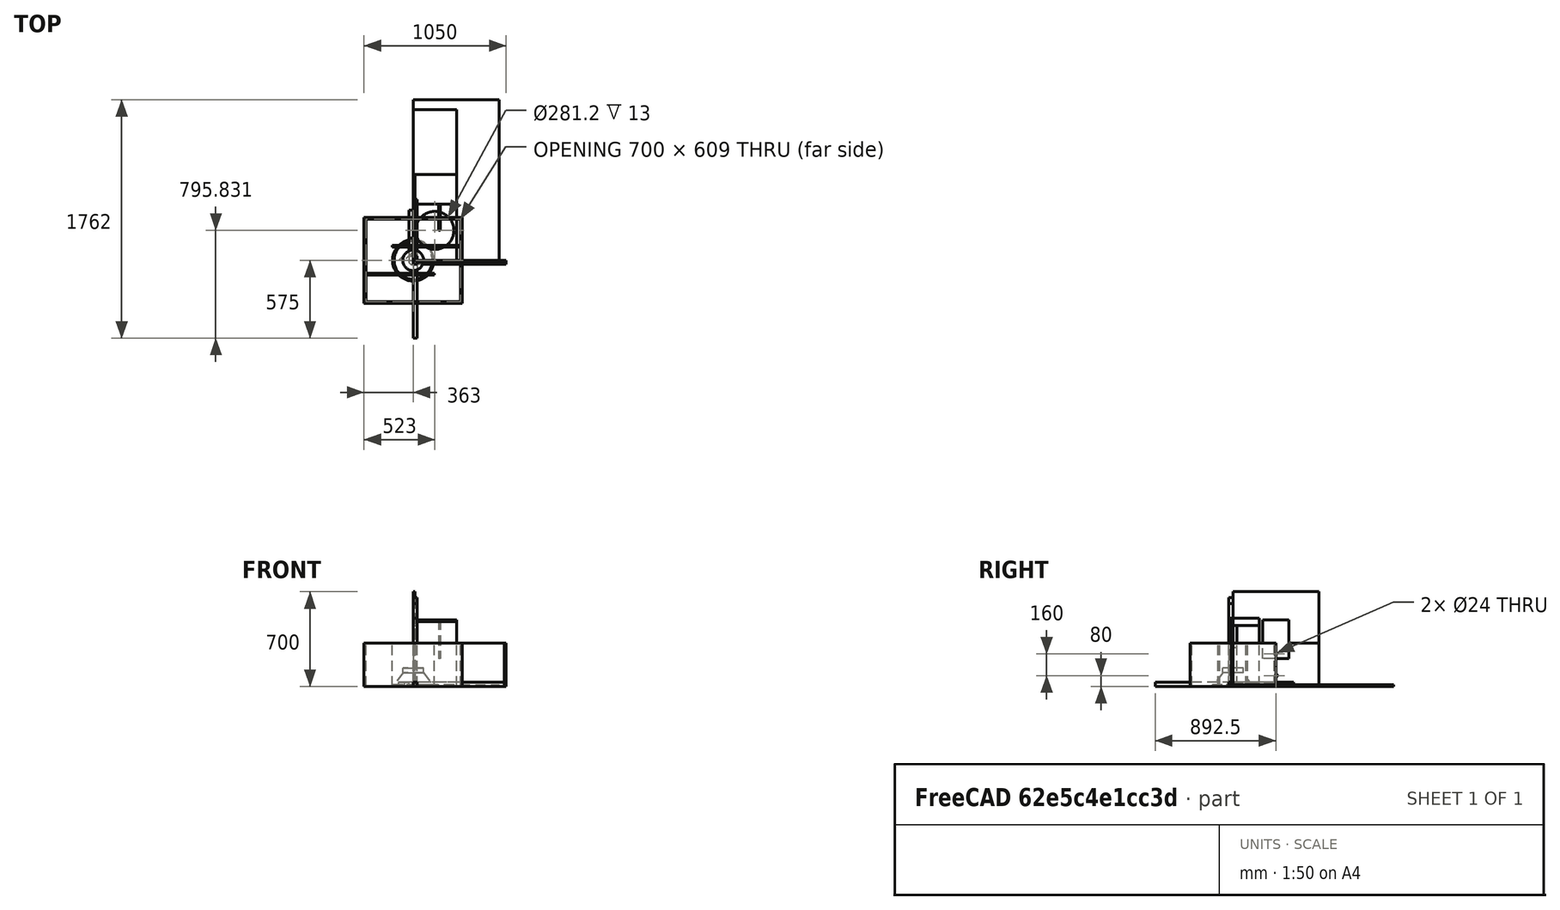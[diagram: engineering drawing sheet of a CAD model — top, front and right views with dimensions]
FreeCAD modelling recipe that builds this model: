
FCSTD DOCUMENT  (FreeCAD 1.0R39109 (Git))
Label: gfold
License: All rights reserved
LicenseURL: http://en.wikipedia.org/wiki/All_rights_reserved
objects: TechDraw::DrawViewDimension×119, TechDraw::DrawViewBalloon×73, TechDraw::DrawProjGroupItem×72, Sketcher::SketchObject×42, App::FeaturePython×42, App::Link×40, PartDesign::Body×38, PartDesign::Pad×37, TechDraw::DrawSVGTemplate×21, TechDraw::DrawPage×21, TechDraw::DrawProjGroup×20, TechDraw::DrawViewAnnotation×20, TechDraw::DrawViewSection×6, Spreadsheet::Sheet×3, App::DocumentObjectGroup×3, PartDesign::Revolution×1, Assembly::JointGroup×1, Assembly::AssemblyObject×1
note: 389 computed .brp shape members not serialized (recipe doc carries the construction recipe); baked Part::Feature solids carry a one-line shape summary decoded from their .brp

FEATURE [Spreadsheet::Sheet] Spreadsheet  label="dims"
  cells = A1='Width (internal); B1(width)==32 cm; A2='Depth (internal); B2(depth)==700 mm; A3='Height (internal); B3(height)==63.5 cm - 2 * thickness; A4='Panel Thickness; B4(thickness)==1.3 cm; A5='ratios; B5(ratio1)=0.33333; C5(ratio2)==ratio1; A6='driver offset; B6(driver_offset)==20 mm; A7='driver_mount; B7(driver_mount_diameter)==281.2 mm; A10='widths; B10(width1)==ratio1 * (height - 2 * thickness); C10(width2)==ratio2 * (height - 2 * thickness); D10(width3)==(1 - ratio1 - ratio2) * (height - 2 * thickness); H10==25.4 * 4
FEATURE [Sketcher::SketchObject] Sketch003  label="outsidepanels_2"
  ArcFitTolerance = 0
  AttachmentSupport = -> [XY_Plane]
  FullyConstrained = true
  MakeInternals = false
  MapMode = 5
  expr: Constraints[197] = <<dims>>.thickness
  expr: Constraints[198] = <<dims>>.width3
  expr: Constraints[199] = <<dims>>.depth
  expr: Constraints[200] = <<dims>>.width2
  expr: Constraints[201] = <<dims>>.width3
  expr: Constraints[202] = <<dims>>.width1
  expr: Constraints[203] = <<dims>>.width2
  expr: Constraints[206] = <<dims>>.depth / 2
  expr: Constraints[207] = <<dims>>.height / 2
  expr: Constraints[218] = <<dims>>.thickness
  expr: Constraints[219] = <<dims>>.thickness
  expr: Constraints[220] = <<dims>>.thickness
  expr: Constraints[221] = <<dims>>.thickness
  sketch-geometry (91):
    g0: LineSegment [constr] StartX=-350 StartY=304.5 StartZ=0 EndX=350 EndY=304.5 EndZ=0
    g1: LineSegment [constr] StartX=350 StartY=304.5 StartZ=0 EndX=350 EndY=-304.5 EndZ=0
    g2: LineSegment [constr] StartX=350 StartY=-304.5 StartZ=0 EndX=-350 EndY=-304.5 EndZ=0
    g3: LineSegment [constr] StartX=-350 StartY=-304.5 StartZ=0 EndX=-350 EndY=304.5 EndZ=0
    g4: LineSegment StartX=-155.669 StartY=110.169 StartZ=0 EndX=350 EndY=110.169 EndZ=0
    g5: LineSegment [constr] StartX=350 StartY=110.169 StartZ=0 EndX=350 EndY=97.1686 EndZ=0
    g6: LineSegment StartX=350 StartY=97.1686 StartZ=0 EndX=-155.669 EndY=97.1686 EndZ=0
    g7: LineSegment StartX=-155.669 StartY=97.1686 StartZ=0 EndX=-155.669 EndY=110.169 EndZ=0
    g8: LineSegment StartX=-350 StartY=-97.1628 StartZ=0 EndX=155.663 EndY=-97.1628 EndZ=0
    g9: LineSegment StartX=155.663 StartY=-97.1628 StartZ=0 EndX=155.663 EndY=-110.163 EndZ=0
    g10: LineSegment StartX=155.663 StartY=-110.163 StartZ=0 EndX=-350 EndY=-110.163 EndZ=0
    g11: LineSegment [constr] StartX=-350 StartY=-110.163 StartZ=0 EndX=-350 EndY=-97.1628 EndZ=0
    g12: LineSegment [constr] StartX=-155.669 StartY=304.5 StartZ=0 EndX=-252.834 EndY=304.5 EndZ=0
    g13: LineSegment [constr] StartX=-252.834 StartY=304.5 StartZ=0 EndX=-350 EndY=304.5 EndZ=0
    g14: LineSegment [constr] StartX=-350 StartY=304.5 StartZ=0 EndX=-350 EndY=207.334 EndZ=0
    g15: LineSegment [constr] StartX=-350 StartY=207.334 StartZ=0 EndX=-350 EndY=110.169 EndZ=0
    g16: LineSegment [constr] StartX=-252.834 StartY=304.5 StartZ=0 EndX=-204.251 EndY=207.334 EndZ=0
    g17: LineSegment [constr] StartX=-204.251 StartY=207.334 StartZ=0 EndX=-155.669 EndY=110.169 EndZ=0
    g18: LineSegment [constr] StartX=-155.669 StartY=110.169 StartZ=0 EndX=-252.834 EndY=158.751 EndZ=0
    g19: LineSegment [constr] StartX=-252.834 StartY=158.751 StartZ=0 EndX=-350 EndY=207.334 EndZ=0
    g20: LineSegment [constr] StartX=-155.669 StartY=110.169 StartZ=0 EndX=-155.669 EndY=207.334 EndZ=0
    g21: LineSegment [constr] StartX=-155.669 StartY=207.334 StartZ=0 EndX=-155.669 EndY=304.5 EndZ=0
    g22: LineSegment [constr] StartX=-155.669 StartY=110.169 StartZ=0 EndX=-252.834 EndY=110.169 EndZ=0
    g23: LineSegment [constr] StartX=-252.834 StartY=110.169 StartZ=0 EndX=-350 EndY=110.169 EndZ=0
    g24: LineSegment [constr] StartX=-155.669 StartY=97.1686 StartZ=0 EndX=-252.834 EndY=97.1686 EndZ=0
    g25: LineSegment [constr] StartX=-252.834 StartY=97.1686 StartZ=0 EndX=-350 EndY=97.1686 EndZ=0
    g26: LineSegment [constr] StartX=-155.669 StartY=97.1686 StartZ=0 EndX=-155.669 EndY=0.002915 EndZ=0
    g27: LineSegment [constr] StartX=-155.669 StartY=0.002915 StartZ=0 EndX=-155.669 EndY=-97.1628 EndZ=0
    g28: LineSegment [constr] StartX=-155.669 StartY=97.1686 StartZ=0 EndX=-252.834 EndY=48.5858 EndZ=0
    g29: LineSegment [constr] StartX=-350 StartY=97.1686 StartZ=0 EndX=-350 EndY=0.002915 EndZ=0
    g30: LineSegment [constr] StartX=-350 StartY=0.002915 StartZ=0 EndX=-350 EndY=-97.1628 EndZ=0
    g31: LineSegment [constr] StartX=-252.834 StartY=48.5858 StartZ=0 EndX=-350 EndY=0.002915 EndZ=0
    g32: LineSegment [constr] StartX=-155.669 StartY=97.1686 StartZ=0 EndX=-204.251 EndY=0.002915 EndZ=0
    g33: LineSegment [constr] StartX=-204.251 StartY=0.002915 StartZ=0 EndX=-252.834 EndY=-97.1628 EndZ=0
    g34: LineSegment [constr] StartX=-350 StartY=-97.1628 StartZ=0 EndX=-252.834 EndY=-97.1628 EndZ=0
    g35: LineSegment [constr] StartX=-252.834 StartY=-97.1628 StartZ=0 EndX=-155.669 EndY=-97.1628 EndZ=0
    g36: LineSegment [constr] StartX=155.663 StartY=97.1686 StartZ=0 EndX=155.663 EndY=0.002915 EndZ=0
    g37: LineSegment [constr] StartX=155.663 StartY=0.002915 StartZ=0 EndX=155.663 EndY=-97.1628 EndZ=0
    g38: LineSegment [constr] StartX=155.663 StartY=-97.1628 StartZ=0 EndX=252.831 EndY=-97.1628 EndZ=0
    g39: LineSegment [constr] StartX=252.831 StartY=-97.1628 StartZ=0 EndX=350 EndY=-97.1628 EndZ=0
    g40: LineSegment [constr] StartX=350 StartY=-97.1628 StartZ=0 EndX=350 EndY=0.002915 EndZ=0
    g41: LineSegment [constr] StartX=350 StartY=97.1686 StartZ=0 EndX=350 EndY=0.002915 EndZ=0
    g42: LineSegment [constr] StartX=155.663 StartY=97.1686 StartZ=0 EndX=252.831 EndY=97.1686 EndZ=0
    g43: LineSegment [constr] StartX=252.831 StartY=97.1686 StartZ=0 EndX=350 EndY=97.1686 EndZ=0
    g44: LineSegment [constr] StartX=252.831 StartY=97.1686 StartZ=0 EndX=204.247 EndY=0.002915 EndZ=0
    g45: LineSegment [constr] StartX=204.247 StartY=0.002915 StartZ=0 EndX=155.663 EndY=-97.1628 EndZ=0
    g46: LineSegment [constr] StartX=155.663 StartY=-97.1628 StartZ=0 EndX=252.831 EndY=-48.5799 EndZ=0
    g47: LineSegment [constr] StartX=252.831 StartY=-48.5799 StartZ=0 EndX=350 EndY=0.002915 EndZ=0
    g48: LineSegment [constr] StartX=155.663 StartY=-110.163 StartZ=0 EndX=252.831 EndY=-110.163 EndZ=0
    g49: LineSegment [constr] StartX=252.831 StartY=-110.163 StartZ=0 EndX=350 EndY=-110.163 EndZ=0
    g50: LineSegment [constr] StartX=155.663 StartY=-110.163 StartZ=0 EndX=155.663 EndY=-207.331 EndZ=0
    g51: LineSegment [constr] StartX=155.663 StartY=-207.331 StartZ=0 EndX=155.663 EndY=-304.5 EndZ=0
    g52: LineSegment [constr] StartX=155.663 StartY=-110.163 StartZ=0 EndX=204.247 EndY=-207.331 EndZ=0
    g53: LineSegment [constr] StartX=204.247 StartY=-207.331 StartZ=0 EndX=252.831 EndY=-304.5 EndZ=0
    g54: LineSegment [constr] StartX=155.663 StartY=-110.163 StartZ=0 EndX=252.831 EndY=-158.747 EndZ=0
    g55: LineSegment [constr] StartX=252.831 StartY=-158.747 StartZ=0 EndX=350 EndY=-207.331 EndZ=0
    g56: LineSegment [constr] StartX=350 StartY=-207.331 StartZ=0 EndX=350 EndY=-110.163 EndZ=0
    g57: LineSegment [constr] StartX=350 StartY=-207.331 StartZ=0 EndX=350 EndY=-304.5 EndZ=0
    g58: LineSegment [constr] StartX=252.831 StartY=-304.5 StartZ=0 EndX=350 EndY=-304.5 EndZ=0
    g59: LineSegment [constr] StartX=252.831 StartY=-304.5 StartZ=0 EndX=155.663 EndY=-304.5 EndZ=0
    g60: LineSegment [constr] StartX=-350 StartY=-110.163 StartZ=0 EndX=-350 EndY=-207.331 EndZ=0
    g61: LineSegment [constr] StartX=-350 StartY=-207.331 StartZ=0 EndX=-350 EndY=-304.5 EndZ=0
    g62: LineSegment [constr] StartX=350 StartY=304.5 StartZ=0 EndX=350 EndY=207.334 EndZ=0
    g63: LineSegment [constr] StartX=350 StartY=207.334 StartZ=0 EndX=350 EndY=110.169 EndZ=0
    g64: LineSegment [constr] StartX=350 StartY=207.334 StartZ=0 EndX=-155.669 EndY=207.334 EndZ=0
    g65: LineSegment [constr] StartX=-155.669 StartY=207.334 StartZ=0 EndX=-204.251 EndY=207.334 EndZ=0
    g66: LineSegment [constr] StartX=-204.251 StartY=207.334 StartZ=0 EndX=-252.834 EndY=158.751 EndZ=0
    g67: LineSegment [constr] StartX=-252.834 StartY=158.751 StartZ=0 EndX=-252.834 EndY=110.169 EndZ=0
    g68: LineSegment [constr] StartX=-252.834 StartY=110.169 StartZ=0 EndX=-252.834 EndY=97.1686 EndZ=0
    g69: LineSegment [constr] StartX=-252.834 StartY=97.1686 StartZ=0 EndX=-252.834 EndY=48.5858 EndZ=0
    g70: LineSegment [constr] StartX=-252.834 StartY=48.5858 StartZ=0 EndX=-204.251 EndY=0.002915 EndZ=0
    g71: LineSegment [constr] StartX=-204.251 StartY=0.002915 StartZ=0 EndX=-155.669 EndY=0.002915 EndZ=0
    g72: LineSegment [constr] StartX=-155.669 StartY=0.002915 StartZ=0 EndX=155.663 EndY=0.002915 EndZ=0
    g73: LineSegment [constr] StartX=155.663 StartY=0.002915 StartZ=0 EndX=204.247 EndY=0.002915 EndZ=0
    g74: LineSegment [constr] StartX=204.247 StartY=0.002915 StartZ=0 EndX=252.831 EndY=-48.5799 EndZ=0
    g75: LineSegment [constr] StartX=252.831 StartY=-48.5799 StartZ=0 EndX=252.831 EndY=-97.1628 EndZ=0
    g76: LineSegment [constr] StartX=252.831 StartY=-97.1628 StartZ=0 EndX=252.831 EndY=-110.163 EndZ=0
    g77: LineSegment [constr] StartX=252.831 StartY=-110.163 StartZ=0 EndX=252.831 EndY=-158.747 EndZ=0
    g78: LineSegment [constr] StartX=252.831 StartY=-158.747 StartZ=0 EndX=204.247 EndY=-207.331 EndZ=0
    g79: LineSegment [constr] StartX=155.663 StartY=-207.331 StartZ=0 EndX=204.247 EndY=-207.331 EndZ=0
    g80: LineSegment [constr] StartX=155.663 StartY=-207.331 StartZ=0 EndX=-350 EndY=-207.331 EndZ=0
    g81: LineSegment StartX=-363 StartY=317.5 StartZ=0 EndX=363 EndY=317.5 EndZ=0
    g82: LineSegment StartX=363 StartY=317.5 StartZ=0 EndX=363 EndY=-317.5 EndZ=0
    g83: LineSegment StartX=363 StartY=-317.5 StartZ=0 EndX=-363 EndY=-317.5 EndZ=0
    g84: LineSegment StartX=-363 StartY=-317.5 StartZ=0 EndX=-363 EndY=317.5 EndZ=0
    g85: LineSegment StartX=350 StartY=-304.5 StartZ=0 EndX=-350 EndY=-304.5 EndZ=0
    g86: LineSegment StartX=-350 StartY=304.5 StartZ=0 EndX=350 EndY=304.5 EndZ=0
    g87: LineSegment StartX=-350 StartY=304.5 StartZ=0 EndX=-350 EndY=-97.1628 EndZ=0
    g88: LineSegment StartX=-350 StartY=-110.163 StartZ=0 EndX=-350 EndY=-304.5 EndZ=0
    g89: LineSegment StartX=350 StartY=304.5 StartZ=0 EndX=350 EndY=110.169 EndZ=0
    g90: LineSegment StartX=350 StartY=97.1686 StartZ=0 EndX=350 EndY=-304.5 EndZ=0
  constraints (234):
    c: Coincident(g0,g1)
    c: Coincident(g1,g2)
    c: Coincident(g2,g3)
    c: Coincident(g3,g0)
    c: Horizontal(g0)
    c: Horizontal(g2)
    c: Vertical(g1)
    c: Vertical(g3)
    c: Coincident(g4,g5)
    c: Coincident(g5,g6)
    c: Coincident(g6,g7)
    c: Coincident(g7,g4)
    c: Horizontal(g4)
    c: Horizontal(g6)
    c: Vertical(g5)
    c: Vertical(g7)
    c: PointOnObject(g5,g1)
    c: Coincident(g8,g9)
    c: Coincident(g9,g10)
    c: Coincident(g10,g11)
    c: Coincident(g11,g8)
    c: Horizontal(g8)
    c: Horizontal(g10)
    c: Vertical(g9)
    c: Vertical(g11)
    c: PointOnObject(g8,g3)
    c: Equal(g7,g9)
    c: Coincident(g20,g4)
    c: PointOnObject(g21,g0)
    c: Coincident(g22,g4)
    c: PointOnObject(g23,g3)
    c: Coincident(g12,g21)
    c: PointOnObject(g12,g0)
    c: Coincident(g13,g12)
    c: Coincident(g13,g0)
    c: Coincident(g14,g0)
    c: PointOnObject(g14,g3)
    c: Coincident(g15,g14)
    c: Coincident(g15,g23)
    c: Equal(g14,g15)
    c: Equal(g12,g13)
    c: Coincident(g16,g12)
    c: Coincident(g17,g4)
    c: Coincident(g18,g4)
    c: Coincident(g19,g14)
    c: Coincident(g16,g17)
    c: Coincident(g18,g19)
    c: Coincident(g20,g21)
    c: Vertical(g20)
    c: Vertical(g21)
    c: Coincident(g22,g23)
    c: Horizontal(g22)
    c: Horizontal(g23)
    c: Equal(g17,g16)
    c: Equal(g21,g20)
    c: Equal(g19,g18)
    c: Equal(g22,g23)
    c: Parallel(g19,g18)
    c: Parallel(g16,g17)
    c: Coincident(g24,g6)
    c: Coincident(g25,g24)
    c: PointOnObject(g25,g3)
    c: Horizontal(g25)
    c: Parallel(g25,g24)
    c: Equal(g24,g25)
    c: Coincident(g26,g6)
    c: Coincident(g27,g26)
    c: PointOnObject(g27,g8)
    c: Parallel(g27,g26)
    c: Equal(g26,g27)
    c: Parallel(g27,g3)
    c: Coincident(g28,g6)
    c: Coincident(g29,g25)
    c: Coincident(g30,g8)
    c: Coincident(g29,g30)
    c: Equal(g29,g30)
    c: Coincident(g31,g28)
    c: Coincident(g31,g29)
    c: Parallel(g31,g28)
    c: Equal(g31,g28)
    c: Parallel(g30,g29)
    c: Coincident(g32,g6)
    c: Coincident(g33,g32)
    c: Coincident(g34,g8)
    c: Coincident(g34,g33)
    c: Coincident(g35,g33)
    c: Coincident(g35,g27)
    c: Parallel(g33,g32)
    c: Equal(g35,g34)
    c: Parallel(g35,g34)
    c: Equal(g33,g32)
    c: PointOnObject(g36,g6)
    c: Coincident(g37,g36)
    c: Coincident(g37,g8)
    c: Parallel(g37,g36)
    c: Parallel(g36,g1)
    c: Equal(g36,g37)
    c: Coincident(g38,g8)
    c: Horizontal(g38)
    c: Coincident(g39,g38)
    c: PointOnObject(g39,g1)
    c: Horizontal(g39)
    c: Coincident(g40,g39)
    c: Coincident(g41,g5)
    c: Coincident(g41,g40)
    c: Coincident(g42,g36)
    c: Coincident(g43,g42)
    c: Coincident(g43,g5)
    c: Coincident(g44,g42)
    c: Coincident(g45,g44)
    c: Coincident(g45,g8)
    c: Coincident(g46,g8)
    c: Coincident(g47,g46)
    c: Coincident(g47,g40)
    c: Equal(g42,g43)
    c: Equal(g44,g45)
    c: Parallel(g42,g43)
    c: Parallel(g45,g44)
    c: Equal(g46,g47)
    c: Equal(g41,g40)
    c: Parallel(g29,g40)
    c: Parallel(g46,g47)
    c: Equal(g38,g39)
    c: Coincident(g48,g9)
    c: Horizontal(g48)
    c: Coincident(g49,g48)
    c: PointOnObject(g49,g1)
    c: Horizontal(g49)
    c: Equal(g49,g48)
    c: Coincident(g50,g9)
    c: Vertical(g50)
    c: Coincident(g51,g50)
    c: PointOnObject(g51,g2)
    c: Vertical(g51)
    c: Equal(g50,g51)
    c: Coincident(g52,g9)
    c: Coincident(g53,g52)
    c: Coincident(g54,g9)
    c: Coincident(g55,g54)
    c: Coincident(g56,g55)
    c: Coincident(g56,g49)
    c: Coincident(g57,g55)
    c: Coincident(g57,g1)
    c: Coincident(g58,g53)
    c: Coincident(g58,g1)
    c: Coincident(g59,g53)
    c: Coincident(g59,g51)
    c: Equal(g56,g57)
    c: Parallel(g57,g56)
    c: Equal(g54,g55)
    c: Equal(g52,g53)
    c: Parallel(g52,g53)
    c: Parallel(g55,g54)
    c: Equal(g59,g58)
    c: Parallel(g59,g58)
    c: Coincident(g60,g10)
    c: Coincident(g61,g2)
    c: Equal(g60,g61)
    c: Parallel(g61,g60)
    c: Coincident(g62,g0)
    c: Coincident(g63,g62)
    c: Coincident(g63,g4)
    c: Equal(g62,g63)
    c: Parallel(g62,g63)
    c: Coincident(g64,g62)
    c: Coincident(g64,g20)
    c: Coincident(g65,g20)
    c: Coincident(g66,g16)
    c: Coincident(g66,g18)
    c: Coincident(g67,g18)
    c: Coincident(g67,g22)
    c: Coincident(g68,g22)
    c: Coincident(g68,g24)
    c: Coincident(g69,g24)
    c: Coincident(g69,g28)
    c: Coincident(g70,g28)
    c: Coincident(g70,g32)
    c: Coincident(g71,g32)
    c: Coincident(g71,g26)
    c: Coincident(g72,g26)
    c: Coincident(g72,g36)
    c: Coincident(g73,g36)
    c: Coincident(g73,g44)
    c: Coincident(g74,g44)
    c: Coincident(g74,g46)
    c: Coincident(g75,g46)
    c: Coincident(g75,g38)
    c: Coincident(g76,g38)
    c: Coincident(g76,g48)
    c: Coincident(g77,g48)
    c: Coincident(g77,g54)
    c: Coincident(g78,g54)
    c: Coincident(g78,g52)
    c: Coincident(g79,g50)
    c: Coincident(g79,g52)
    c: Coincident(g80,g50)
    c: Coincident(g65,g16)
    c: DistanceY(g10,g8) = 13
    c: DistanceY(g2,g49) = 194.337
    c: DistanceX(g0,g0) = 700
    c: DistanceX(g25,g6) = 194.331
    c: DistanceX(g9,g49) = 194.337
    c: DistanceY(g4,g0) = 194.331
    c: DistanceY(g39,g5) = 194.331
    c: Coincident(g61,g80)
    c: Coincident(g61,g60)
    c: DistanceX(g-1,g1) = 350
    c: DistanceY(g-1,g0) = 304.5
    c: Coincident(g81,g82)
    c: Coincident(g82,g83)
    c: Coincident(g83,g84)
    c: Coincident(g84,g81)
    c: Horizontal(g81)
    c: Horizontal(g83)
    c: Vertical(g82)
    c: Vertical(g84)
    c: Horizontal(g85)
    c: Horizontal(g86)
    c: DistanceY(g86,g81) = 13
    c: DistanceX(g81,g86) = 13
    c: DistanceY(g82,g85) = 13
    c: DistanceX(g85,g82) = 13
    c: Coincident(g85,g1)
    c: Coincident(g87,g86)
    c: Coincident(g87,g8)
    c: Vertical(g87)
    c: Coincident(g88,g10)
    c: Coincident(g88,g85)
    c: Vertical(g88)
    c: Coincident(g89,g86)
    c: Coincident(g89,g4)
    c: Coincident(g90,g6)
    c: Coincident(g90,g85)
    c: Coincident(g86,g0)
FEATURE [PartDesign::Pad] Pad001
  Direction = (0,0,1)
  Length = 320
  Length2 = 10
  Profile = -> Sketch003
  ReferenceAxis = -> Sketch003 [N_Axis]
  Suppressed = false
  Type = 0
  expr: Length = <<dims>>.width
FEATURE [Sketcher::SketchObject] Sketch004  label="sound_path_l12"
  ArcFitTolerance = 0
  AttachmentSupport = -> [XY_Plane]
  FullyConstrained = true
  MakeInternals = false
  MapMode = 5
  expr: Constraints[190] = <<dims>>.thickness
  expr: Constraints[191] = <<dims>>.width3
  expr: Constraints[192] = <<dims>>.depth
  expr: Constraints[193] = <<dims>>.width2
  expr: Constraints[194] = <<dims>>.width3
  expr: Constraints[195] = <<dims>>.width1
  expr: Constraints[196] = <<dims>>.width2
  expr: Constraints[199] = <<dims>>.depth / 2
  expr: Constraints[200] = <<dims>>.height / 2
  expr: Constraints[213] = <<dims>>.thickness
  expr: Constraints[234] = <<dims>>.driver_offset + <<dims>>.thickness
  sketch-geometry (91):
    g0: LineSegment [constr] StartX=-350 StartY=304.5 StartZ=0 EndX=350 EndY=304.5 EndZ=0
    g1: LineSegment [constr] StartX=350 StartY=304.5 StartZ=0 EndX=350 EndY=-304.5 EndZ=0
    g2: LineSegment [constr] StartX=350 StartY=-304.5 StartZ=0 EndX=-350 EndY=-304.5 EndZ=0
    g3: LineSegment [constr] StartX=-350 StartY=-304.5 StartZ=0 EndX=-350 EndY=304.5 EndZ=0
    g4: LineSegment [constr] StartX=-155.669 StartY=110.169 StartZ=0 EndX=350 EndY=110.169 EndZ=0
    g5: LineSegment [constr] StartX=350 StartY=110.169 StartZ=0 EndX=350 EndY=97.1686 EndZ=0
    g6: LineSegment [constr] StartX=350 StartY=97.1686 StartZ=0 EndX=-155.669 EndY=97.1686 EndZ=0
    g7: LineSegment [constr] StartX=-155.669 StartY=97.1686 StartZ=0 EndX=-155.669 EndY=110.169 EndZ=0
    g8: LineSegment [constr] StartX=-350 StartY=-97.1628 StartZ=0 EndX=155.663 EndY=-97.1628 EndZ=0
    g9: LineSegment [constr] StartX=155.663 StartY=-97.1628 StartZ=0 EndX=155.663 EndY=-110.163 EndZ=0
    g10: LineSegment [constr] StartX=155.663 StartY=-110.163 StartZ=0 EndX=-350 EndY=-110.163 EndZ=0
    g11: LineSegment [constr] StartX=-350 StartY=-110.163 StartZ=0 EndX=-350 EndY=-97.1628 EndZ=0
    g12: LineSegment [constr] StartX=-155.669 StartY=304.5 StartZ=0 EndX=-252.834 EndY=304.5 EndZ=0
    g13: LineSegment [constr] StartX=-252.834 StartY=304.5 StartZ=0 EndX=-350 EndY=304.5 EndZ=0
    g14: LineSegment [constr] StartX=-350 StartY=304.5 StartZ=0 EndX=-350 EndY=207.334 EndZ=0
    g15: LineSegment [constr] StartX=-350 StartY=207.334 StartZ=0 EndX=-350 EndY=110.169 EndZ=0
    g16: LineSegment [constr] StartX=-252.834 StartY=304.5 StartZ=0 EndX=-204.251 EndY=207.334 EndZ=0
    g17: LineSegment [constr] StartX=-204.251 StartY=207.334 StartZ=0 EndX=-155.669 EndY=110.169 EndZ=0
    g18: LineSegment [constr] StartX=-155.669 StartY=110.169 StartZ=0 EndX=-252.834 EndY=158.751 EndZ=0
    g19: LineSegment [constr] StartX=-252.834 StartY=158.751 StartZ=0 EndX=-350 EndY=207.334 EndZ=0
    g20: LineSegment [constr] StartX=-155.669 StartY=110.169 StartZ=0 EndX=-155.669 EndY=207.334 EndZ=0
    g21: LineSegment [constr] StartX=-155.669 StartY=207.334 StartZ=0 EndX=-155.669 EndY=304.5 EndZ=0
    g22: LineSegment [constr] StartX=-155.669 StartY=110.169 StartZ=0 EndX=-252.834 EndY=110.169 EndZ=0
    g23: LineSegment [constr] StartX=-252.834 StartY=110.169 StartZ=0 EndX=-350 EndY=110.169 EndZ=0
    g24: LineSegment [constr] StartX=-155.669 StartY=97.1686 StartZ=0 EndX=-252.834 EndY=97.1686 EndZ=0
    g25: LineSegment [constr] StartX=-252.834 StartY=97.1686 StartZ=0 EndX=-350 EndY=97.1686 EndZ=0
    g26: LineSegment [constr] StartX=-155.669 StartY=97.1686 StartZ=0 EndX=-155.669 EndY=0.002915 EndZ=0
    g27: LineSegment [constr] StartX=-155.669 StartY=0.002915 StartZ=0 EndX=-155.669 EndY=-97.1628 EndZ=0
    g28: LineSegment [constr] StartX=-155.669 StartY=97.1686 StartZ=0 EndX=-252.834 EndY=48.5858 EndZ=0
    g29: LineSegment [constr] StartX=-350 StartY=97.1686 StartZ=0 EndX=-350 EndY=0.002915 EndZ=0
    g30: LineSegment [constr] StartX=-350 StartY=0.002915 StartZ=0 EndX=-350 EndY=-97.1628 EndZ=0
    g31: LineSegment [constr] StartX=-252.834 StartY=48.5858 StartZ=0 EndX=-350 EndY=0.002915 EndZ=0
    g32: LineSegment [constr] StartX=-155.669 StartY=97.1686 StartZ=0 EndX=-204.251 EndY=0.002915 EndZ=0
    g33: LineSegment [constr] StartX=-204.251 StartY=0.002915 StartZ=0 EndX=-252.834 EndY=-97.1628 EndZ=0
    g34: LineSegment [constr] StartX=-350 StartY=-97.1628 StartZ=0 EndX=-252.834 EndY=-97.1628 EndZ=0
    g35: LineSegment [constr] StartX=-252.834 StartY=-97.1628 StartZ=0 EndX=-155.669 EndY=-97.1628 EndZ=0
    g36: LineSegment [constr] StartX=155.663 StartY=97.1686 StartZ=0 EndX=155.663 EndY=0.002915 EndZ=0
    g37: LineSegment [constr] StartX=155.663 StartY=0.002915 StartZ=0 EndX=155.663 EndY=-97.1628 EndZ=0
    g38: LineSegment [constr] StartX=155.663 StartY=-97.1628 StartZ=0 EndX=252.831 EndY=-97.1628 EndZ=0
    g39: LineSegment [constr] StartX=252.831 StartY=-97.1628 StartZ=0 EndX=350 EndY=-97.1628 EndZ=0
    g40: LineSegment [constr] StartX=350 StartY=-97.1628 StartZ=0 EndX=350 EndY=0.002915 EndZ=0
    g41: LineSegment [constr] StartX=350 StartY=97.1686 StartZ=0 EndX=350 EndY=0.002915 EndZ=0
    g42: LineSegment [constr] StartX=155.663 StartY=97.1686 StartZ=0 EndX=252.831 EndY=97.1686 EndZ=0
    g43: LineSegment [constr] StartX=252.831 StartY=97.1686 StartZ=0 EndX=350 EndY=97.1686 EndZ=0
    g44: LineSegment [constr] StartX=252.831 StartY=97.1686 StartZ=0 EndX=204.247 EndY=0.002915 EndZ=0
    g45: LineSegment [constr] StartX=204.247 StartY=0.002915 StartZ=0 EndX=155.663 EndY=-97.1628 EndZ=0
    g46: LineSegment [constr] StartX=155.663 StartY=-97.1628 StartZ=0 EndX=252.831 EndY=-48.5799 EndZ=0
    g47: LineSegment [constr] StartX=252.831 StartY=-48.5799 StartZ=0 EndX=350 EndY=0.002915 EndZ=0
    g48: LineSegment [constr] StartX=155.663 StartY=-110.163 StartZ=0 EndX=252.831 EndY=-110.163 EndZ=0
    g49: LineSegment [constr] StartX=252.831 StartY=-110.163 StartZ=0 EndX=350 EndY=-110.163 EndZ=0
    g50: LineSegment [constr] StartX=155.663 StartY=-110.163 StartZ=0 EndX=155.663 EndY=-207.331 EndZ=0
    g51: LineSegment [constr] StartX=155.663 StartY=-207.331 StartZ=0 EndX=155.663 EndY=-304.5 EndZ=0
    g52: LineSegment [constr] StartX=155.663 StartY=-110.163 StartZ=0 EndX=204.247 EndY=-207.331 EndZ=0
    g53: LineSegment [constr] StartX=204.247 StartY=-207.331 StartZ=0 EndX=252.831 EndY=-304.5 EndZ=0
    g54: LineSegment [constr] StartX=155.663 StartY=-110.163 StartZ=0 EndX=252.831 EndY=-158.747 EndZ=0
    g55: LineSegment [constr] StartX=252.831 StartY=-158.747 StartZ=0 EndX=350 EndY=-207.331 EndZ=0
    g56: LineSegment [constr] StartX=350 StartY=-207.331 StartZ=0 EndX=350 EndY=-110.163 EndZ=0
    g57: LineSegment [constr] StartX=350 StartY=-207.331 StartZ=0 EndX=350 EndY=-304.5 EndZ=0
    g58: LineSegment [constr] StartX=252.831 StartY=-304.5 StartZ=0 EndX=350 EndY=-304.5 EndZ=0
    g59: LineSegment [constr] StartX=252.831 StartY=-304.5 StartZ=0 EndX=155.663 EndY=-304.5 EndZ=0
    g60: LineSegment [constr] StartX=-350 StartY=-110.163 StartZ=0 EndX=-350 EndY=-207.331 EndZ=0
    g61: LineSegment [constr] StartX=-350 StartY=-207.331 StartZ=0 EndX=-350 EndY=-304.5 EndZ=0
    g62: LineSegment [constr] StartX=350 StartY=304.5 StartZ=0 EndX=350 EndY=207.334 EndZ=0
    g63: LineSegment [constr] StartX=350 StartY=207.334 StartZ=0 EndX=350 EndY=110.169 EndZ=0
    g64: LineSegment StartX=350 StartY=207.334 StartZ=0 EndX=-155.669 EndY=207.334 EndZ=0
    g65: LineSegment StartX=-155.669 StartY=207.334 StartZ=0 EndX=-204.251 EndY=207.334 EndZ=0
    g66: LineSegment StartX=-204.251 StartY=207.334 StartZ=0 EndX=-252.834 EndY=158.751 EndZ=0
    g67: LineSegment [constr] StartX=-252.834 StartY=97.1686 StartZ=0 EndX=-252.834 EndY=48.5858 EndZ=0
    g68: LineSegment [constr] StartX=-204.251 StartY=0.002915 StartZ=0 EndX=-155.669 EndY=0.002915 EndZ=0
    g69: LineSegment [constr] StartX=-155.669 StartY=0.002915 StartZ=0 EndX=155.663 EndY=0.002915 EndZ=0
    g70: LineSegment [constr] StartX=155.663 StartY=0.002915 StartZ=0 EndX=204.247 EndY=0.002915 EndZ=0
    g71: LineSegment [constr] StartX=204.247 StartY=0.002915 StartZ=0 EndX=252.831 EndY=-48.5799 EndZ=0
    g72: LineSegment [constr] StartX=252.831 StartY=-48.5799 StartZ=0 EndX=252.831 EndY=-97.1628 EndZ=0
    g73: LineSegment [constr] StartX=252.831 StartY=-97.1628 StartZ=0 EndX=252.831 EndY=-110.163 EndZ=0
    g74: LineSegment [constr] StartX=252.831 StartY=-110.163 StartZ=0 EndX=252.831 EndY=-158.747 EndZ=0
    g75: LineSegment [constr] StartX=252.831 StartY=-158.747 StartZ=0 EndX=204.247 EndY=-207.331 EndZ=0
    g76: LineSegment [constr] StartX=155.663 StartY=-207.331 StartZ=0 EndX=204.247 EndY=-207.331 EndZ=0
    g77: LineSegment [constr] StartX=155.663 StartY=-207.331 StartZ=0 EndX=-350 EndY=-207.331 EndZ=0
    g78: LineSegment [constr] StartX=-360 StartY=314.5 StartZ=0 EndX=360 EndY=314.5 EndZ=0
    g79: LineSegment [constr] StartX=360 StartY=314.5 StartZ=0 EndX=360 EndY=-317.5 EndZ=0
    g80: LineSegment [constr] StartX=360 StartY=-317.5 StartZ=0 EndX=-360 EndY=-317.5 EndZ=0
    g81: LineSegment [constr] StartX=-360 StartY=-317.5 StartZ=0 EndX=-360 EndY=314.5 EndZ=0
    g82: LineSegment [constr] StartX=350 StartY=-304.5 StartZ=0 EndX=-350 EndY=-304.5 EndZ=0
    g83: LineSegment [constr] StartX=-350 StartY=304.5 StartZ=0 EndX=350 EndY=304.5 EndZ=0
    g84: LineSegment [constr] StartX=-350 StartY=304.5 StartZ=0 EndX=-350 EndY=-97.1628 EndZ=0
    g85: LineSegment [constr] StartX=-350 StartY=-110.163 StartZ=0 EndX=-350 EndY=-304.5 EndZ=0
    g86: LineSegment [constr] StartX=350 StartY=304.5 StartZ=0 EndX=350 EndY=110.169 EndZ=0
    g87: LineSegment [constr] StartX=350 StartY=97.1686 StartZ=0 EndX=350 EndY=-304.5 EndZ=0
    g88: LineSegment [constr] StartX=-252.834 StartY=-97.1628 StartZ=0 EndX=-252.834 EndY=304.5 EndZ=0
    g89: LineSegment StartX=-252.834 StartY=158.751 StartZ=0 EndX=-252.834 EndY=77.1686 EndZ=0
    g90: LineSegment [constr] StartX=-252.834 StartY=77.1686 StartZ=0 EndX=-252.834 EndY=48.5858 EndZ=0
  constraints (235):
    c: Coincident(g0,g1)
    c: Coincident(g1,g2)
    c: Coincident(g2,g3)
    c: Coincident(g3,g0)
    c: Horizontal(g0)
    c: Horizontal(g2)
    c: Vertical(g1)
    c: Vertical(g3)
    c: Coincident(g4,g5)
    c: Coincident(g5,g6)
    c: Coincident(g6,g7)
    c: Coincident(g7,g4)
    c: Horizontal(g4)
    c: Horizontal(g6)
    c: Vertical(g5)
    c: Vertical(g7)
    c: PointOnObject(g5,g1)
    c: Coincident(g8,g9)
    c: Coincident(g9,g10)
    c: Coincident(g10,g11)
    c: Coincident(g11,g8)
    c: Horizontal(g8)
    c: Horizontal(g10)
    c: Vertical(g9)
    c: Vertical(g11)
    c: PointOnObject(g8,g3)
    c: Equal(g7,g9)
    c: Coincident(g20,g4)
    c: PointOnObject(g21,g0)
    c: Coincident(g22,g4)
    c: PointOnObject(g23,g3)
    c: Coincident(g12,g21)
    c: PointOnObject(g12,g0)
    c: Coincident(g13,g12)
    c: Coincident(g13,g0)
    c: Coincident(g14,g0)
    c: PointOnObject(g14,g3)
    c: Coincident(g15,g14)
    c: Coincident(g15,g23)
    c: Equal(g14,g15)
    c: Equal(g12,g13)
    c: Coincident(g16,g12)
    c: Coincident(g17,g4)
    c: Coincident(g18,g4)
    c: Coincident(g19,g14)
    c: Coincident(g16,g17)
    c: Coincident(g18,g19)
    c: Coincident(g20,g21)
    c: Vertical(g20)
    c: Vertical(g21)
    c: Coincident(g22,g23)
    c: Horizontal(g22)
    c: Horizontal(g23)
    c: Equal(g17,g16)
    c: Equal(g21,g20)
    c: Equal(g19,g18)
    c: Equal(g22,g23)
    c: Parallel(g19,g18)
    c: Parallel(g16,g17)
    c: Coincident(g24,g6)
    c: Coincident(g25,g24)
    c: PointOnObject(g25,g3)
    c: Horizontal(g25)
    c: Parallel(g25,g24)
    c: Equal(g24,g25)
    c: Coincident(g26,g6)
    c: Coincident(g27,g26)
    c: PointOnObject(g27,g8)
    c: Parallel(g27,g26)
    c: Equal(g26,g27)
    c: Parallel(g27,g3)
    c: Coincident(g28,g6)
    c: Coincident(g29,g25)
    c: Coincident(g30,g8)
    c: Coincident(g29,g30)
    c: Equal(g29,g30)
    c: Coincident(g31,g28)
    c: Coincident(g31,g29)
    c: Parallel(g31,g28)
    c: Equal(g31,g28)
    c: Parallel(g30,g29)
    c: Coincident(g32,g6)
    c: Coincident(g33,g32)
    c: Coincident(g34,g8)
    c: Coincident(g34,g33)
    c: Coincident(g35,g33)
    c: Coincident(g35,g27)
    c: Parallel(g33,g32)
    c: Equal(g35,g34)
    c: Parallel(g35,g34)
    c: Equal(g33,g32)
    c: PointOnObject(g36,g6)
    c: Coincident(g37,g36)
    c: Coincident(g37,g8)
    c: Parallel(g37,g36)
    c: Parallel(g36,g1)
    c: Equal(g36,g37)
    c: Coincident(g38,g8)
    c: Horizontal(g38)
    c: Coincident(g39,g38)
    c: PointOnObject(g39,g1)
    c: Horizontal(g39)
    c: Coincident(g40,g39)
    c: Coincident(g41,g5)
    c: Coincident(g41,g40)
    c: Coincident(g42,g36)
    c: Coincident(g43,g42)
    c: Coincident(g43,g5)
    c: Coincident(g44,g42)
    c: Coincident(g45,g44)
    c: Coincident(g45,g8)
    c: Coincident(g46,g8)
    c: Coincident(g47,g46)
    c: Coincident(g47,g40)
    c: Equal(g42,g43)
    c: Equal(g44,g45)
    c: Parallel(g42,g43)
    c: Parallel(g45,g44)
    c: Equal(g46,g47)
    c: Equal(g41,g40)
    c: Parallel(g29,g40)
    c: Parallel(g46,g47)
    c: Equal(g38,g39)
    c: Coincident(g48,g9)
    c: Horizontal(g48)
    c: Coincident(g49,g48)
    c: PointOnObject(g49,g1)
    c: Horizontal(g49)
    c: Equal(g49,g48)
    c: Coincident(g50,g9)
    c: Vertical(g50)
    c: Coincident(g51,g50)
    c: PointOnObject(g51,g2)
    c: Vertical(g51)
    c: Equal(g50,g51)
    c: Coincident(g52,g9)
    c: Coincident(g53,g52)
    c: Coincident(g54,g9)
    c: Coincident(g55,g54)
    c: Coincident(g56,g55)
    c: Coincident(g56,g49)
    c: Coincident(g57,g55)
    c: Coincident(g57,g1)
    c: Coincident(g58,g53)
    c: Coincident(g58,g1)
    c: Coincident(g59,g53)
    c: Coincident(g59,g51)
    c: Equal(g56,g57)
    c: Parallel(g57,g56)
    c: Equal(g54,g55)
    c: Equal(g52,g53)
    c: Parallel(g52,g53)
    c: Parallel(g55,g54)
    c: Equal(g59,g58)
    c: Parallel(g59,g58)
    c: Coincident(g60,g10)
    c: Coincident(g61,g2)
    c: Equal(g60,g61)
    c: Parallel(g61,g60)
    c: Coincident(g62,g0)
    c: Coincident(g63,g62)
    c: Coincident(g63,g4)
    c: Equal(g62,g63)
    c: Parallel(g62,g63)
    c: Coincident(g64,g62)
    c: Coincident(g64,g20)
    c: Coincident(g65,g20)
    c: Coincident(g66,g16)
    c: Coincident(g67,g24)
    c: Coincident(g67,g28)
    c: Coincident(g68,g32)
    c: Coincident(g68,g26)
    c: Coincident(g69,g26)
    c: Coincident(g69,g36)
    c: Coincident(g70,g36)
    c: Coincident(g70,g44)
    c: Coincident(g71,g44)
    c: Coincident(g71,g46)
    c: Coincident(g72,g46)
    c: Coincident(g72,g38)
    c: Coincident(g73,g38)
    c: Coincident(g73,g48)
    c: Coincident(g74,g48)
    c: Coincident(g74,g54)
    c: Coincident(g75,g54)
    c: Coincident(g75,g52)
    c: Coincident(g76,g50)
    c: Coincident(g76,g52)
    c: Coincident(g77,g50)
    c: Coincident(g65,g16)
    c: DistanceY(g10,g8) = 13
    c: DistanceY(g2,g49) = 194.337
    c: DistanceX(g0,g0) = 700
    c: DistanceX(g25,g6) = 194.331
    c: DistanceX(g9,g49) = 194.337
    c: DistanceY(g4,g0) = 194.331
    c: DistanceY(g39,g5) = 194.331
    c: Coincident(g61,g77)
    c: Coincident(g61,g60)
    c: DistanceX(g-1,g1) = 350
    c: DistanceY(g-1,g0) = 304.5
    c: Coincident(g78,g79)
    c: Coincident(g79,g80)
    c: Coincident(g80,g81)
    c: Coincident(g81,g78)
    c: Horizontal(g78)
    c: Horizontal(g80)
    c: Vertical(g79)
    c: Vertical(g81)
    c: Horizontal(g82)
    c: Horizontal(g83)
    c: DistanceY(g83,g78) = 10
    c: DistanceX(g78,g83) = 10
    c: DistanceY(g79,g82) = 13
    c: DistanceX(g82,g79) = 10
    c: Coincident(g82,g1)
    c: Coincident(g84,g83)
    c: Coincident(g84,g8)
    c: Vertical(g84)
    c: Coincident(g85,g10)
    c: Coincident(g85,g82)
    c: Vertical(g85)
    c: Coincident(g86,g83)
    c: Coincident(g86,g4)
    c: Coincident(g87,g6)
    c: Coincident(g87,g82)
    c: Coincident(g83,g0)
    c: Coincident(g88,g33)
    c: Coincident(g88,g12)
    c: Coincident(g89,g66)
    c: PointOnObject(g89,g88)
    c: Coincident(g90,g89)
    c: Coincident(g90,g28)
    c: Coincident(g66,g18)
    c: DistanceY(g89,g22) = 33
FEATURE [Spreadsheet::Sheet] Spreadsheet001  label="hornresp"
  cells = A1='Crosssections; B1==<<dims>>.width1 * <<dims>>.width; C1==<<dims>>.width2 * <<dims>>.width; D1==<<dims>>.width3 * <<dims>>.width; F1='Build modif; G1(build_mod)==3 * 3 cm * 3 cm + 1.3 cm * <<dims>>.width1; B2==B1 - build_mod; A3='L12; B3==<<sound_path_l12>>.Shape.Length; A4='L23; B4==<<sound_path_l23>>.Shape.Length; A5='L34; B5==<<sound_path_l34>>.Shape.Length; A6='L45; B6==<<sound_path_l45>>.Shape.Length
FEATURE [Sketcher::SketchObject] Sketch009  label="sound_path_l23"
  ArcFitTolerance = 0
  AttachmentSupport = -> [XY_Plane]
  FullyConstrained = true
  MakeInternals = false
  MapMode = 5
  expr: Constraints[191] = <<dims>>.width3
  expr: Constraints[192] = <<dims>>.depth
  expr: Constraints[193] = <<dims>>.width2
  expr: Constraints[194] = <<dims>>.width3
  expr: Constraints[195] = <<dims>>.width1
  expr: Constraints[196] = <<dims>>.width2
  expr: Constraints[199] = <<dims>>.depth / 2
  expr: Constraints[200] = <<dims>>.height / 2
  expr: Constraints[213] = <<dims>>.thickness
  expr: Constraints[238] = <<dims>>.driver_offset + <<dims>>.thickness
  sketch-geometry (93):
    g0: LineSegment [constr] StartX=-350 StartY=304.5 StartZ=0 EndX=350 EndY=304.5 EndZ=0
    g1: LineSegment [constr] StartX=350 StartY=304.5 StartZ=0 EndX=350 EndY=-298.5 EndZ=0
    g2: LineSegment [constr] StartX=350 StartY=-298.5 StartZ=0 EndX=-350 EndY=-298.5 EndZ=0
    g3: LineSegment [constr] StartX=-350 StartY=-298.5 StartZ=0 EndX=-350 EndY=304.5 EndZ=0
    g4: LineSegment [constr] StartX=-155.669 StartY=110.169 StartZ=0 EndX=350 EndY=110.169 EndZ=0
    g5: LineSegment [constr] StartX=350 StartY=110.169 StartZ=0 EndX=350 EndY=100.169 EndZ=0
    g6: LineSegment [constr] StartX=350 StartY=100.169 StartZ=0 EndX=-155.669 EndY=100.169 EndZ=0
    g7: LineSegment [constr] StartX=-155.669 StartY=100.169 StartZ=0 EndX=-155.669 EndY=110.169 EndZ=0
    g8: LineSegment [constr] StartX=-350 StartY=-94.1628 StartZ=0 EndX=155.663 EndY=-94.1628 EndZ=0
    g9: LineSegment [constr] StartX=155.663 StartY=-94.1628 StartZ=0 EndX=155.663 EndY=-104.163 EndZ=0
    g10: LineSegment [constr] StartX=155.663 StartY=-104.163 StartZ=0 EndX=-350 EndY=-104.163 EndZ=0
    g11: LineSegment [constr] StartX=-350 StartY=-104.163 StartZ=0 EndX=-350 EndY=-94.1628 EndZ=0
    g12: LineSegment [constr] StartX=-155.669 StartY=304.5 StartZ=0 EndX=-252.834 EndY=304.5 EndZ=0
    g13: LineSegment [constr] StartX=-252.834 StartY=304.5 StartZ=0 EndX=-350 EndY=304.5 EndZ=0
    g14: LineSegment [constr] StartX=-350 StartY=304.5 StartZ=0 EndX=-350 EndY=207.334 EndZ=0
    g15: LineSegment [constr] StartX=-350 StartY=207.334 StartZ=0 EndX=-350 EndY=110.169 EndZ=0
    g16: LineSegment [constr] StartX=-252.834 StartY=304.5 StartZ=0 EndX=-204.251 EndY=207.334 EndZ=0
    g17: LineSegment [constr] StartX=-204.251 StartY=207.334 StartZ=0 EndX=-155.669 EndY=110.169 EndZ=0
    g18: LineSegment [constr] StartX=-155.669 StartY=110.169 StartZ=0 EndX=-252.834 EndY=158.751 EndZ=0
    g19: LineSegment [constr] StartX=-252.834 StartY=158.751 StartZ=0 EndX=-350 EndY=207.334 EndZ=0
    g20: LineSegment [constr] StartX=-155.669 StartY=110.169 StartZ=0 EndX=-155.669 EndY=207.334 EndZ=0
    g21: LineSegment [constr] StartX=-155.669 StartY=207.334 StartZ=0 EndX=-155.669 EndY=304.5 EndZ=0
    g22: LineSegment [constr] StartX=-155.669 StartY=110.169 StartZ=0 EndX=-252.834 EndY=110.169 EndZ=0
    g23: LineSegment [constr] StartX=-252.834 StartY=110.169 StartZ=0 EndX=-350 EndY=110.169 EndZ=0
    g24: LineSegment [constr] StartX=-155.669 StartY=100.169 StartZ=0 EndX=-252.834 EndY=100.169 EndZ=0
    g25: LineSegment [constr] StartX=-252.834 StartY=100.169 StartZ=0 EndX=-350 EndY=100.169 EndZ=0
    g26: LineSegment [constr] StartX=-155.669 StartY=100.169 StartZ=0 EndX=-155.669 EndY=3.00292 EndZ=0
    g27: LineSegment [constr] StartX=-155.669 StartY=3.00292 StartZ=0 EndX=-155.669 EndY=-94.1628 EndZ=0
    g28: LineSegment [constr] StartX=-155.669 StartY=100.169 StartZ=0 EndX=-252.834 EndY=51.5858 EndZ=0
    g29: LineSegment [constr] StartX=-350 StartY=100.169 StartZ=0 EndX=-350 EndY=3.00292 EndZ=0
    g30: LineSegment [constr] StartX=-350 StartY=3.00292 StartZ=0 EndX=-350 EndY=-94.1628 EndZ=0
    g31: LineSegment [constr] StartX=-252.834 StartY=51.5858 StartZ=0 EndX=-350 EndY=3.00292 EndZ=0
    g32: LineSegment [constr] StartX=-155.669 StartY=100.169 StartZ=0 EndX=-204.251 EndY=3.00292 EndZ=0
    g33: LineSegment [constr] StartX=-204.251 StartY=3.00292 StartZ=0 EndX=-252.834 EndY=-94.1628 EndZ=0
    g34: LineSegment [constr] StartX=-350 StartY=-94.1628 StartZ=0 EndX=-252.834 EndY=-94.1628 EndZ=0
    g35: LineSegment [constr] StartX=-252.834 StartY=-94.1628 StartZ=0 EndX=-155.669 EndY=-94.1628 EndZ=0
    g36: LineSegment [constr] StartX=155.663 StartY=100.169 StartZ=0 EndX=155.663 EndY=3.00292 EndZ=0
    g37: LineSegment [constr] StartX=155.663 StartY=3.00292 StartZ=0 EndX=155.663 EndY=-94.1628 EndZ=0
    g38: LineSegment [constr] StartX=155.663 StartY=-94.1628 StartZ=0 EndX=252.831 EndY=-94.1628 EndZ=0
    g39: LineSegment [constr] StartX=252.831 StartY=-94.1628 StartZ=0 EndX=350 EndY=-94.1628 EndZ=0
    g40: LineSegment [constr] StartX=350 StartY=-94.1628 StartZ=0 EndX=350 EndY=3.00292 EndZ=0
    g41: LineSegment [constr] StartX=350 StartY=100.169 StartZ=0 EndX=350 EndY=3.00292 EndZ=0
    g42: LineSegment [constr] StartX=155.663 StartY=100.169 StartZ=0 EndX=252.831 EndY=100.169 EndZ=0
    g43: LineSegment [constr] StartX=252.831 StartY=100.169 StartZ=0 EndX=350 EndY=100.169 EndZ=0
    g44: LineSegment [constr] StartX=252.831 StartY=100.169 StartZ=0 EndX=204.247 EndY=3.00292 EndZ=0
    g45: LineSegment [constr] StartX=204.247 StartY=3.00292 StartZ=0 EndX=155.663 EndY=-94.1628 EndZ=0
    g46: LineSegment [constr] StartX=155.663 StartY=-94.1628 StartZ=0 EndX=252.831 EndY=-45.5799 EndZ=0
    g47: LineSegment [constr] StartX=252.831 StartY=-45.5799 StartZ=0 EndX=350 EndY=3.00292 EndZ=0
    g48: LineSegment [constr] StartX=155.663 StartY=-104.163 StartZ=0 EndX=252.831 EndY=-104.163 EndZ=0
    g49: LineSegment [constr] StartX=252.831 StartY=-104.163 StartZ=0 EndX=350 EndY=-104.163 EndZ=0
    g50: LineSegment [constr] StartX=155.663 StartY=-104.163 StartZ=0 EndX=155.663 EndY=-201.331 EndZ=0
    g51: LineSegment [constr] StartX=155.663 StartY=-201.331 StartZ=0 EndX=155.663 EndY=-298.5 EndZ=0
    g52: LineSegment [constr] StartX=155.663 StartY=-104.163 StartZ=0 EndX=204.247 EndY=-201.331 EndZ=0
    g53: LineSegment [constr] StartX=204.247 StartY=-201.331 StartZ=0 EndX=252.831 EndY=-298.5 EndZ=0
    g54: LineSegment [constr] StartX=155.663 StartY=-104.163 StartZ=0 EndX=252.831 EndY=-152.747 EndZ=0
    g55: LineSegment [constr] StartX=252.831 StartY=-152.747 StartZ=0 EndX=350 EndY=-201.331 EndZ=0
    g56: LineSegment [constr] StartX=350 StartY=-201.331 StartZ=0 EndX=350 EndY=-104.163 EndZ=0
    g57: LineSegment [constr] StartX=350 StartY=-201.331 StartZ=0 EndX=350 EndY=-298.5 EndZ=0
    g58: LineSegment [constr] StartX=252.831 StartY=-298.5 StartZ=0 EndX=350 EndY=-298.5 EndZ=0
    g59: LineSegment [constr] StartX=252.831 StartY=-298.5 StartZ=0 EndX=155.663 EndY=-298.5 EndZ=0
    g60: LineSegment [constr] StartX=-350 StartY=-104.163 StartZ=0 EndX=-350 EndY=-201.331 EndZ=0
    g61: LineSegment [constr] StartX=-350 StartY=-201.331 StartZ=0 EndX=-350 EndY=-298.5 EndZ=0
    g62: LineSegment [constr] StartX=350 StartY=304.5 StartZ=0 EndX=350 EndY=207.334 EndZ=0
    g63: LineSegment [constr] StartX=350 StartY=207.334 StartZ=0 EndX=350 EndY=110.169 EndZ=0
    g64: LineSegment [constr] StartX=350 StartY=207.334 StartZ=0 EndX=-155.669 EndY=207.334 EndZ=0
    g65: LineSegment [constr] StartX=-155.669 StartY=207.334 StartZ=0 EndX=-204.251 EndY=207.334 EndZ=0
    g66: LineSegment [constr] StartX=-204.251 StartY=207.334 StartZ=0 EndX=-252.834 EndY=158.751 EndZ=0
    g67: LineSegment [constr] StartX=-252.834 StartY=100.169 StartZ=0 EndX=-252.834 EndY=51.5858 EndZ=0
    g68: LineSegment StartX=-204.251 StartY=3.00292 StartZ=0 EndX=-155.669 EndY=3.00292 EndZ=0
    g69: LineSegment StartX=-155.669 StartY=3.00292 StartZ=0 EndX=155.663 EndY=3.00292 EndZ=0
    g70: LineSegment [constr] StartX=155.663 StartY=3.00292 StartZ=0 EndX=204.247 EndY=3.00292 EndZ=0
    g71: LineSegment [constr] StartX=204.247 StartY=3.00292 StartZ=0 EndX=252.831 EndY=-45.5799 EndZ=0
    g72: LineSegment [constr] StartX=252.831 StartY=-45.5799 StartZ=0 EndX=252.831 EndY=-94.1628 EndZ=0
    g73: LineSegment [constr] StartX=252.831 StartY=-94.1628 StartZ=0 EndX=252.831 EndY=-104.163 EndZ=0
    g74: LineSegment [constr] StartX=252.831 StartY=-104.163 StartZ=0 EndX=252.831 EndY=-152.747 EndZ=0
    g75: LineSegment [constr] StartX=252.831 StartY=-152.747 StartZ=0 EndX=204.247 EndY=-201.331 EndZ=0
    g76: LineSegment [constr] StartX=155.663 StartY=-201.331 StartZ=0 EndX=204.247 EndY=-201.331 EndZ=0
    g77: LineSegment [constr] StartX=155.663 StartY=-201.331 StartZ=0 EndX=-350 EndY=-201.331 EndZ=0
    g78: LineSegment [constr] StartX=-360 StartY=314.5 StartZ=0 EndX=360 EndY=314.5 EndZ=0
    g79: LineSegment [constr] StartX=360 StartY=314.5 StartZ=0 EndX=360 EndY=-311.5 EndZ=0
    g80: LineSegment [constr] StartX=360 StartY=-311.5 StartZ=0 EndX=-360 EndY=-311.5 EndZ=0
    g81: LineSegment [constr] StartX=-360 StartY=-311.5 StartZ=0 EndX=-360 EndY=314.5 EndZ=0
    g82: LineSegment [constr] StartX=350 StartY=-298.5 StartZ=0 EndX=-350 EndY=-298.5 EndZ=0
    g83: LineSegment [constr] StartX=-350 StartY=304.5 StartZ=0 EndX=350 EndY=304.5 EndZ=0
    g84: LineSegment [constr] StartX=-350 StartY=304.5 StartZ=0 EndX=-350 EndY=-94.1628 EndZ=0
    g85: LineSegment [constr] StartX=-350 StartY=-104.163 StartZ=0 EndX=-350 EndY=-298.5 EndZ=0
    g86: LineSegment [constr] StartX=350 StartY=304.5 StartZ=0 EndX=350 EndY=110.169 EndZ=0
    g87: LineSegment [constr] StartX=350 StartY=100.169 StartZ=0 EndX=350 EndY=-298.5 EndZ=0
    g88: LineSegment [constr] StartX=-252.834 StartY=-94.1628 StartZ=0 EndX=-252.834 EndY=304.5 EndZ=0
    g89: LineSegment [constr] StartX=-252.834 StartY=158.751 StartZ=0 EndX=-252.834 EndY=77.1686 EndZ=0
    g90: LineSegment [constr] StartX=-252.834 StartY=77.1686 StartZ=0 EndX=-252.834 EndY=51.5858 EndZ=0
    g91: LineSegment StartX=-204.251 StartY=3.00292 StartZ=0 EndX=-252.834 EndY=51.5858 EndZ=0
    g92: LineSegment StartX=-252.834 StartY=51.5858 StartZ=0 EndX=-252.834 EndY=77.1686 EndZ=0
  constraints (239):
    c: Coincident(g0,g1)
    c: Coincident(g1,g2)
    c: Coincident(g2,g3)
    c: Coincident(g3,g0)
    c: Horizontal(g0)
    c: Horizontal(g2)
    c: Vertical(g1)
    c: Vertical(g3)
    c: Coincident(g4,g5)
    c: Coincident(g5,g6)
    c: Coincident(g6,g7)
    c: Coincident(g7,g4)
    c: Horizontal(g4)
    c: Horizontal(g6)
    c: Vertical(g5)
    c: Vertical(g7)
    c: PointOnObject(g5,g1)
    c: Coincident(g8,g9)
    c: Coincident(g9,g10)
    c: Coincident(g10,g11)
    c: Coincident(g11,g8)
    c: Horizontal(g8)
    c: Horizontal(g10)
    c: Vertical(g9)
    c: Vertical(g11)
    c: PointOnObject(g8,g3)
    c: Equal(g7,g9)
    c: Coincident(g20,g4)
    c: PointOnObject(g21,g0)
    c: Coincident(g22,g4)
    c: PointOnObject(g23,g3)
    c: Coincident(g12,g21)
    c: PointOnObject(g12,g0)
    c: Coincident(g13,g12)
    c: Coincident(g13,g0)
    c: Coincident(g14,g0)
    c: PointOnObject(g14,g3)
    c: Coincident(g15,g14)
    c: Coincident(g15,g23)
    c: Equal(g14,g15)
    c: Equal(g12,g13)
    c: Coincident(g16,g12)
    c: Coincident(g17,g4)
    c: Coincident(g18,g4)
    c: Coincident(g19,g14)
    c: Coincident(g16,g17)
    c: Coincident(g18,g19)
    c: Coincident(g20,g21)
    c: Vertical(g20)
    c: Vertical(g21)
    c: Coincident(g22,g23)
    c: Horizontal(g22)
    c: Horizontal(g23)
    c: Equal(g17,g16)
    c: Equal(g21,g20)
    c: Equal(g19,g18)
    c: Equal(g22,g23)
    c: Parallel(g19,g18)
    c: Parallel(g16,g17)
    c: Coincident(g24,g6)
    c: Coincident(g25,g24)
    c: PointOnObject(g25,g3)
    c: Horizontal(g25)
    c: Parallel(g25,g24)
    c: Equal(g24,g25)
    c: Coincident(g26,g6)
    c: Coincident(g27,g26)
    c: PointOnObject(g27,g8)
    c: Parallel(g27,g26)
    c: Equal(g26,g27)
    c: Parallel(g27,g3)
    c: Coincident(g28,g6)
    c: Coincident(g29,g25)
    c: Coincident(g30,g8)
    c: Coincident(g29,g30)
    c: Equal(g29,g30)
    c: Coincident(g31,g28)
    c: Coincident(g31,g29)
    c: Parallel(g31,g28)
    c: Equal(g31,g28)
    c: Parallel(g30,g29)
    c: Coincident(g32,g6)
    c: Coincident(g33,g32)
    c: Coincident(g34,g8)
    c: Coincident(g34,g33)
    c: Coincident(g35,g33)
    c: Coincident(g35,g27)
    c: Parallel(g33,g32)
    c: Equal(g35,g34)
    c: Parallel(g35,g34)
    c: Equal(g33,g32)
    c: PointOnObject(g36,g6)
    c: Coincident(g37,g36)
    c: Coincident(g37,g8)
    c: Parallel(g37,g36)
    c: Parallel(g36,g1)
    c: Equal(g36,g37)
    c: Coincident(g38,g8)
    c: Horizontal(g38)
    c: Coincident(g39,g38)
    c: PointOnObject(g39,g1)
    c: Horizontal(g39)
    c: Coincident(g40,g39)
    c: Coincident(g41,g5)
    c: Coincident(g41,g40)
    c: Coincident(g42,g36)
    c: Coincident(g43,g42)
    c: Coincident(g43,g5)
    c: Coincident(g44,g42)
    c: Coincident(g45,g44)
    c: Coincident(g45,g8)
    c: Coincident(g46,g8)
    c: Coincident(g47,g46)
    c: Coincident(g47,g40)
    c: Equal(g42,g43)
    c: Equal(g44,g45)
    c: Parallel(g42,g43)
    c: Parallel(g45,g44)
    c: Equal(g46,g47)
    c: Equal(g41,g40)
    c: Parallel(g29,g40)
    c: Parallel(g46,g47)
    c: Equal(g38,g39)
    c: Coincident(g48,g9)
    c: Horizontal(g48)
    c: Coincident(g49,g48)
    c: PointOnObject(g49,g1)
    c: Horizontal(g49)
    c: Equal(g49,g48)
    c: Coincident(g50,g9)
    c: Vertical(g50)
    c: Coincident(g51,g50)
    c: PointOnObject(g51,g2)
    c: Vertical(g51)
    c: Equal(g50,g51)
    c: Coincident(g52,g9)
    c: Coincident(g53,g52)
    c: Coincident(g54,g9)
    c: Coincident(g55,g54)
    c: Coincident(g56,g55)
    c: Coincident(g56,g49)
    c: Coincident(g57,g55)
    c: Coincident(g57,g1)
    c: Coincident(g58,g53)
    c: Coincident(g58,g1)
    c: Coincident(g59,g53)
    c: Coincident(g59,g51)
    c: Equal(g56,g57)
    c: Parallel(g57,g56)
    c: Equal(g54,g55)
    c: Equal(g52,g53)
    c: Parallel(g52,g53)
    c: Parallel(g55,g54)
    c: Equal(g59,g58)
    c: Parallel(g59,g58)
    c: Coincident(g60,g10)
    c: Coincident(g61,g2)
    c: Equal(g60,g61)
    c: Parallel(g61,g60)
    c: Coincident(g62,g0)
    c: Coincident(g63,g62)
    c: Coincident(g63,g4)
    c: Equal(g62,g63)
    c: Parallel(g62,g63)
    c: Coincident(g64,g62)
    c: Coincident(g64,g20)
    c: Coincident(g65,g20)
    c: Coincident(g66,g16)
    c: Coincident(g67,g24)
    c: Coincident(g67,g28)
    c: Coincident(g68,g32)
    c: Coincident(g68,g26)
    c: Coincident(g69,g26)
    c: Coincident(g69,g36)
    c: Coincident(g70,g36)
    c: Coincident(g70,g44)
    c: Coincident(g71,g44)
    c: Coincident(g71,g46)
    c: Coincident(g72,g46)
    c: Coincident(g72,g38)
    c: Coincident(g73,g38)
    c: Coincident(g73,g48)
    c: Coincident(g74,g48)
    c: Coincident(g74,g54)
    c: Coincident(g75,g54)
    c: Coincident(g75,g52)
    c: Coincident(g76,g50)
    c: Coincident(g76,g52)
    c: Coincident(g77,g50)
    c: Coincident(g65,g16)
    c: DistanceY(g10,g8) = 10
    c: DistanceY(g2,g49) = 194.337
    c: DistanceX(g0,g0) = 700
    c: DistanceX(g25,g6) = 194.331
    c: DistanceX(g9,g49) = 194.337
    c: DistanceY(g4,g0) = 194.331
    c: DistanceY(g39,g5) = 194.331
    c: Coincident(g61,g77)
    c: Coincident(g61,g60)
    c: DistanceX(g-1,g1) = 350
    c: DistanceY(g-1,g0) = 304.5
    c: Coincident(g78,g79)
    c: Coincident(g79,g80)
    c: Coincident(g80,g81)
    c: Coincident(g81,g78)
    c: Horizontal(g78)
    c: Horizontal(g80)
    c: Vertical(g79)
    c: Vertical(g81)
    c: Horizontal(g82)
    c: Horizontal(g83)
    c: DistanceY(g83,g78) = 10
    c: DistanceX(g78,g83) = 10
    c: DistanceY(g79,g82) = 13
    c: DistanceX(g82,g79) = 10
    c: Coincident(g82,g1)
    c: Coincident(g84,g83)
    c: Coincident(g84,g8)
    c: Vertical(g84)
    c: Coincident(g85,g10)
    c: Coincident(g85,g82)
    c: Vertical(g85)
    c: Coincident(g86,g83)
    c: Coincident(g86,g4)
    c: Coincident(g87,g6)
    c: Coincident(g87,g82)
    c: Coincident(g83,g0)
    c: Coincident(g88,g33)
    c: Coincident(g88,g12)
    c: Coincident(g89,g66)
    c: PointOnObject(g89,g88)
    c: Coincident(g90,g89)
    c: Coincident(g90,g28)
    c: Coincident(g66,g18)
    c: Coincident(g91,g32)
    c: Coincident(g91,g28)
    c: Coincident(g92,g91)
    c: Coincident(g92,g89)
    c: DistanceY(g89,g22) = 33
FEATURE [Sketcher::SketchObject] Sketch010  label="sound_path_l34"
  ArcFitTolerance = 0
  AttachmentSupport = -> [XY_Plane]
  FullyConstrained = true
  MakeInternals = false
  MapMode = 5
  expr: Constraints[191] = <<dims>>.width3
  expr: Constraints[192] = <<dims>>.depth
  expr: Constraints[193] = <<dims>>.width2
  expr: Constraints[194] = <<dims>>.width3
  expr: Constraints[195] = <<dims>>.width1
  expr: Constraints[196] = <<dims>>.width2
  expr: Constraints[199] = <<dims>>.depth / 2
  expr: Constraints[200] = <<dims>>.height / 2
  expr: Constraints[213] = <<dims>>.thickness
  expr: Constraints[238] = <<dims>>.driver_offset + <<dims>>.thickness
  sketch-geometry (93):
    g0: LineSegment [constr] StartX=-350 StartY=304.5 StartZ=0 EndX=350 EndY=304.5 EndZ=0
    g1: LineSegment [constr] StartX=350 StartY=304.5 StartZ=0 EndX=350 EndY=-298.5 EndZ=0
    g2: LineSegment [constr] StartX=350 StartY=-298.5 StartZ=0 EndX=-350 EndY=-298.5 EndZ=0
    g3: LineSegment [constr] StartX=-350 StartY=-298.5 StartZ=0 EndX=-350 EndY=304.5 EndZ=0
    g4: LineSegment [constr] StartX=-155.669 StartY=110.169 StartZ=0 EndX=350 EndY=110.169 EndZ=0
    g5: LineSegment [constr] StartX=350 StartY=110.169 StartZ=0 EndX=350 EndY=100.169 EndZ=0
    g6: LineSegment [constr] StartX=350 StartY=100.169 StartZ=0 EndX=-155.669 EndY=100.169 EndZ=0
    g7: LineSegment [constr] StartX=-155.669 StartY=100.169 StartZ=0 EndX=-155.669 EndY=110.169 EndZ=0
    g8: LineSegment [constr] StartX=-350 StartY=-94.1628 StartZ=0 EndX=155.663 EndY=-94.1628 EndZ=0
    g9: LineSegment [constr] StartX=155.663 StartY=-94.1628 StartZ=0 EndX=155.663 EndY=-104.163 EndZ=0
    g10: LineSegment [constr] StartX=155.663 StartY=-104.163 StartZ=0 EndX=-350 EndY=-104.163 EndZ=0
    g11: LineSegment [constr] StartX=-350 StartY=-104.163 StartZ=0 EndX=-350 EndY=-94.1628 EndZ=0
    g12: LineSegment [constr] StartX=-155.669 StartY=304.5 StartZ=0 EndX=-252.834 EndY=304.5 EndZ=0
    g13: LineSegment [constr] StartX=-252.834 StartY=304.5 StartZ=0 EndX=-350 EndY=304.5 EndZ=0
    g14: LineSegment [constr] StartX=-350 StartY=304.5 StartZ=0 EndX=-350 EndY=207.334 EndZ=0
    g15: LineSegment [constr] StartX=-350 StartY=207.334 StartZ=0 EndX=-350 EndY=110.169 EndZ=0
    g16: LineSegment [constr] StartX=-252.834 StartY=304.5 StartZ=0 EndX=-204.251 EndY=207.334 EndZ=0
    g17: LineSegment [constr] StartX=-204.251 StartY=207.334 StartZ=0 EndX=-155.669 EndY=110.169 EndZ=0
    g18: LineSegment [constr] StartX=-155.669 StartY=110.169 StartZ=0 EndX=-252.834 EndY=158.751 EndZ=0
    g19: LineSegment [constr] StartX=-252.834 StartY=158.751 StartZ=0 EndX=-350 EndY=207.334 EndZ=0
    g20: LineSegment [constr] StartX=-155.669 StartY=110.169 StartZ=0 EndX=-155.669 EndY=207.334 EndZ=0
    g21: LineSegment [constr] StartX=-155.669 StartY=207.334 StartZ=0 EndX=-155.669 EndY=304.5 EndZ=0
    g22: LineSegment [constr] StartX=-155.669 StartY=110.169 StartZ=0 EndX=-252.834 EndY=110.169 EndZ=0
    g23: LineSegment [constr] StartX=-252.834 StartY=110.169 StartZ=0 EndX=-350 EndY=110.169 EndZ=0
    g24: LineSegment [constr] StartX=-155.669 StartY=100.169 StartZ=0 EndX=-252.834 EndY=100.169 EndZ=0
    g25: LineSegment [constr] StartX=-252.834 StartY=100.169 StartZ=0 EndX=-350 EndY=100.169 EndZ=0
    g26: LineSegment [constr] StartX=-155.669 StartY=100.169 StartZ=0 EndX=-155.669 EndY=3.00292 EndZ=0
    g27: LineSegment [constr] StartX=-155.669 StartY=3.00292 StartZ=0 EndX=-155.669 EndY=-94.1628 EndZ=0
    g28: LineSegment [constr] StartX=-155.669 StartY=100.169 StartZ=0 EndX=-252.834 EndY=51.5858 EndZ=0
    g29: LineSegment [constr] StartX=-350 StartY=100.169 StartZ=0 EndX=-350 EndY=3.00292 EndZ=0
    g30: LineSegment [constr] StartX=-350 StartY=3.00292 StartZ=0 EndX=-350 EndY=-94.1628 EndZ=0
    g31: LineSegment [constr] StartX=-252.834 StartY=51.5858 StartZ=0 EndX=-350 EndY=3.00292 EndZ=0
    g32: LineSegment [constr] StartX=-155.669 StartY=100.169 StartZ=0 EndX=-204.251 EndY=3.00292 EndZ=0
    g33: LineSegment [constr] StartX=-204.251 StartY=3.00292 StartZ=0 EndX=-252.834 EndY=-94.1628 EndZ=0
    g34: LineSegment [constr] StartX=-350 StartY=-94.1628 StartZ=0 EndX=-252.834 EndY=-94.1628 EndZ=0
    g35: LineSegment [constr] StartX=-252.834 StartY=-94.1628 StartZ=0 EndX=-155.669 EndY=-94.1628 EndZ=0
    g36: LineSegment [constr] StartX=155.663 StartY=100.169 StartZ=0 EndX=155.663 EndY=3.00292 EndZ=0
    g37: LineSegment [constr] StartX=155.663 StartY=3.00292 StartZ=0 EndX=155.663 EndY=-94.1628 EndZ=0
    g38: LineSegment [constr] StartX=155.663 StartY=-94.1628 StartZ=0 EndX=252.831 EndY=-94.1628 EndZ=0
    g39: LineSegment [constr] StartX=252.831 StartY=-94.1628 StartZ=0 EndX=350 EndY=-94.1628 EndZ=0
    g40: LineSegment [constr] StartX=350 StartY=-94.1628 StartZ=0 EndX=350 EndY=3.00292 EndZ=0
    g41: LineSegment [constr] StartX=350 StartY=100.169 StartZ=0 EndX=350 EndY=3.00292 EndZ=0
    g42: LineSegment [constr] StartX=155.663 StartY=100.169 StartZ=0 EndX=252.831 EndY=100.169 EndZ=0
    g43: LineSegment [constr] StartX=252.831 StartY=100.169 StartZ=0 EndX=350 EndY=100.169 EndZ=0
    g44: LineSegment [constr] StartX=252.831 StartY=100.169 StartZ=0 EndX=204.247 EndY=3.00292 EndZ=0
    g45: LineSegment [constr] StartX=204.247 StartY=3.00292 StartZ=0 EndX=155.663 EndY=-94.1628 EndZ=0
    g46: LineSegment [constr] StartX=155.663 StartY=-94.1628 StartZ=0 EndX=252.831 EndY=-45.5799 EndZ=0
    g47: LineSegment [constr] StartX=252.831 StartY=-45.5799 StartZ=0 EndX=350 EndY=3.00292 EndZ=0
    g48: LineSegment [constr] StartX=155.663 StartY=-104.163 StartZ=0 EndX=252.831 EndY=-104.163 EndZ=0
    g49: LineSegment [constr] StartX=252.831 StartY=-104.163 StartZ=0 EndX=350 EndY=-104.163 EndZ=0
    g50: LineSegment [constr] StartX=155.663 StartY=-104.163 StartZ=0 EndX=155.663 EndY=-201.331 EndZ=0
    g51: LineSegment [constr] StartX=155.663 StartY=-201.331 StartZ=0 EndX=155.663 EndY=-298.5 EndZ=0
    g52: LineSegment [constr] StartX=155.663 StartY=-104.163 StartZ=0 EndX=204.247 EndY=-201.331 EndZ=0
    g53: LineSegment [constr] StartX=204.247 StartY=-201.331 StartZ=0 EndX=252.831 EndY=-298.5 EndZ=0
    g54: LineSegment [constr] StartX=155.663 StartY=-104.163 StartZ=0 EndX=252.831 EndY=-152.747 EndZ=0
    g55: LineSegment [constr] StartX=252.831 StartY=-152.747 StartZ=0 EndX=350 EndY=-201.331 EndZ=0
    g56: LineSegment [constr] StartX=350 StartY=-201.331 StartZ=0 EndX=350 EndY=-104.163 EndZ=0
    g57: LineSegment [constr] StartX=350 StartY=-201.331 StartZ=0 EndX=350 EndY=-298.5 EndZ=0
    g58: LineSegment [constr] StartX=252.831 StartY=-298.5 StartZ=0 EndX=350 EndY=-298.5 EndZ=0
    g59: LineSegment [constr] StartX=252.831 StartY=-298.5 StartZ=0 EndX=155.663 EndY=-298.5 EndZ=0
    g60: LineSegment [constr] StartX=-350 StartY=-104.163 StartZ=0 EndX=-350 EndY=-201.331 EndZ=0
    g61: LineSegment [constr] StartX=-350 StartY=-201.331 StartZ=0 EndX=-350 EndY=-298.5 EndZ=0
    g62: LineSegment [constr] StartX=350 StartY=304.5 StartZ=0 EndX=350 EndY=207.334 EndZ=0
    g63: LineSegment [constr] StartX=350 StartY=207.334 StartZ=0 EndX=350 EndY=110.169 EndZ=0
    g64: LineSegment [constr] StartX=350 StartY=207.334 StartZ=0 EndX=-155.669 EndY=207.334 EndZ=0
    g65: LineSegment [constr] StartX=-155.669 StartY=207.334 StartZ=0 EndX=-204.251 EndY=207.334 EndZ=0
    g66: LineSegment [constr] StartX=-204.251 StartY=207.334 StartZ=0 EndX=-252.834 EndY=158.751 EndZ=0
    g67: LineSegment [constr] StartX=-252.834 StartY=100.169 StartZ=0 EndX=-252.834 EndY=51.5858 EndZ=0
    g68: LineSegment [constr] StartX=-204.251 StartY=3.00292 StartZ=0 EndX=-155.669 EndY=3.00292 EndZ=0
    g69: LineSegment [constr] StartX=-155.669 StartY=3.00292 StartZ=0 EndX=155.663 EndY=3.00292 EndZ=0
    g70: LineSegment StartX=155.663 StartY=3.00292 StartZ=0 EndX=204.247 EndY=3.00292 EndZ=0
    g71: LineSegment StartX=204.247 StartY=3.00292 StartZ=0 EndX=252.831 EndY=-45.5799 EndZ=0
    g72: LineSegment StartX=252.831 StartY=-45.5799 StartZ=0 EndX=252.831 EndY=-94.1628 EndZ=0
    g73: LineSegment [constr] StartX=252.831 StartY=-94.1628 StartZ=0 EndX=252.831 EndY=-104.163 EndZ=0
    g74: LineSegment [constr] StartX=252.831 StartY=-104.163 StartZ=0 EndX=252.831 EndY=-152.747 EndZ=0
    g75: LineSegment [constr] StartX=252.831 StartY=-152.747 StartZ=0 EndX=204.247 EndY=-201.331 EndZ=0
    g76: LineSegment [constr] StartX=155.663 StartY=-201.331 StartZ=0 EndX=204.247 EndY=-201.331 EndZ=0
    g77: LineSegment [constr] StartX=155.663 StartY=-201.331 StartZ=0 EndX=-350 EndY=-201.331 EndZ=0
    g78: LineSegment [constr] StartX=-360 StartY=314.5 StartZ=0 EndX=360 EndY=314.5 EndZ=0
    g79: LineSegment [constr] StartX=360 StartY=314.5 StartZ=0 EndX=360 EndY=-311.5 EndZ=0
    g80: LineSegment [constr] StartX=360 StartY=-311.5 StartZ=0 EndX=-360 EndY=-311.5 EndZ=0
    g81: LineSegment [constr] StartX=-360 StartY=-311.5 StartZ=0 EndX=-360 EndY=314.5 EndZ=0
    g82: LineSegment [constr] StartX=350 StartY=-298.5 StartZ=0 EndX=-350 EndY=-298.5 EndZ=0
    g83: LineSegment [constr] StartX=-350 StartY=304.5 StartZ=0 EndX=350 EndY=304.5 EndZ=0
    g84: LineSegment [constr] StartX=-350 StartY=304.5 StartZ=0 EndX=-350 EndY=-94.1628 EndZ=0
    g85: LineSegment [constr] StartX=-350 StartY=-104.163 StartZ=0 EndX=-350 EndY=-298.5 EndZ=0
    g86: LineSegment [constr] StartX=350 StartY=304.5 StartZ=0 EndX=350 EndY=110.169 EndZ=0
    g87: LineSegment [constr] StartX=350 StartY=100.169 StartZ=0 EndX=350 EndY=-298.5 EndZ=0
    g88: LineSegment [constr] StartX=-252.834 StartY=-94.1628 StartZ=0 EndX=-252.834 EndY=304.5 EndZ=0
    g89: LineSegment [constr] StartX=-252.834 StartY=158.751 StartZ=0 EndX=-252.834 EndY=77.1686 EndZ=0
    g90: LineSegment [constr] StartX=-252.834 StartY=77.1686 StartZ=0 EndX=-252.834 EndY=51.5858 EndZ=0
    g91: LineSegment [constr] StartX=-204.251 StartY=3.00292 StartZ=0 EndX=-252.834 EndY=51.5858 EndZ=0
    g92: LineSegment [constr] StartX=-252.834 StartY=51.5858 StartZ=0 EndX=-252.834 EndY=77.1686 EndZ=0
  constraints (239):
    c: Coincident(g0,g1)
    c: Coincident(g1,g2)
    c: Coincident(g2,g3)
    c: Coincident(g3,g0)
    c: Horizontal(g0)
    c: Horizontal(g2)
    c: Vertical(g1)
    c: Vertical(g3)
    c: Coincident(g4,g5)
    c: Coincident(g5,g6)
    c: Coincident(g6,g7)
    c: Coincident(g7,g4)
    c: Horizontal(g4)
    c: Horizontal(g6)
    c: Vertical(g5)
    c: Vertical(g7)
    c: PointOnObject(g5,g1)
    c: Coincident(g8,g9)
    c: Coincident(g9,g10)
    c: Coincident(g10,g11)
    c: Coincident(g11,g8)
    c: Horizontal(g8)
    c: Horizontal(g10)
    c: Vertical(g9)
    c: Vertical(g11)
    c: PointOnObject(g8,g3)
    c: Equal(g7,g9)
    c: Coincident(g20,g4)
    c: PointOnObject(g21,g0)
    c: Coincident(g22,g4)
    c: PointOnObject(g23,g3)
    c: Coincident(g12,g21)
    c: PointOnObject(g12,g0)
    c: Coincident(g13,g12)
    c: Coincident(g13,g0)
    c: Coincident(g14,g0)
    c: PointOnObject(g14,g3)
    c: Coincident(g15,g14)
    c: Coincident(g15,g23)
    c: Equal(g14,g15)
    c: Equal(g12,g13)
    c: Coincident(g16,g12)
    c: Coincident(g17,g4)
    c: Coincident(g18,g4)
    c: Coincident(g19,g14)
    c: Coincident(g16,g17)
    c: Coincident(g18,g19)
    c: Coincident(g20,g21)
    c: Vertical(g20)
    c: Vertical(g21)
    c: Coincident(g22,g23)
    c: Horizontal(g22)
    c: Horizontal(g23)
    c: Equal(g17,g16)
    c: Equal(g21,g20)
    c: Equal(g19,g18)
    c: Equal(g22,g23)
    c: Parallel(g19,g18)
    c: Parallel(g16,g17)
    c: Coincident(g24,g6)
    c: Coincident(g25,g24)
    c: PointOnObject(g25,g3)
    c: Horizontal(g25)
    c: Parallel(g25,g24)
    c: Equal(g24,g25)
    c: Coincident(g26,g6)
    c: Coincident(g27,g26)
    c: PointOnObject(g27,g8)
    c: Parallel(g27,g26)
    c: Equal(g26,g27)
    c: Parallel(g27,g3)
    c: Coincident(g28,g6)
    c: Coincident(g29,g25)
    c: Coincident(g30,g8)
    c: Coincident(g29,g30)
    c: Equal(g29,g30)
    c: Coincident(g31,g28)
    c: Coincident(g31,g29)
    c: Parallel(g31,g28)
    c: Equal(g31,g28)
    c: Parallel(g30,g29)
    c: Coincident(g32,g6)
    c: Coincident(g33,g32)
    c: Coincident(g34,g8)
    c: Coincident(g34,g33)
    c: Coincident(g35,g33)
    c: Coincident(g35,g27)
    c: Parallel(g33,g32)
    c: Equal(g35,g34)
    c: Parallel(g35,g34)
    c: Equal(g33,g32)
    c: PointOnObject(g36,g6)
    c: Coincident(g37,g36)
    c: Coincident(g37,g8)
    c: Parallel(g37,g36)
    c: Parallel(g36,g1)
    c: Equal(g36,g37)
    c: Coincident(g38,g8)
    c: Horizontal(g38)
    c: Coincident(g39,g38)
    c: PointOnObject(g39,g1)
    c: Horizontal(g39)
    c: Coincident(g40,g39)
    c: Coincident(g41,g5)
    c: Coincident(g41,g40)
    c: Coincident(g42,g36)
    c: Coincident(g43,g42)
    c: Coincident(g43,g5)
    c: Coincident(g44,g42)
    c: Coincident(g45,g44)
    c: Coincident(g45,g8)
    c: Coincident(g46,g8)
    c: Coincident(g47,g46)
    c: Coincident(g47,g40)
    c: Equal(g42,g43)
    c: Equal(g44,g45)
    c: Parallel(g42,g43)
    c: Parallel(g45,g44)
    c: Equal(g46,g47)
    c: Equal(g41,g40)
    c: Parallel(g29,g40)
    c: Parallel(g46,g47)
    c: Equal(g38,g39)
    c: Coincident(g48,g9)
    c: Horizontal(g48)
    c: Coincident(g49,g48)
    c: PointOnObject(g49,g1)
    c: Horizontal(g49)
    c: Equal(g49,g48)
    c: Coincident(g50,g9)
    c: Vertical(g50)
    c: Coincident(g51,g50)
    c: PointOnObject(g51,g2)
    c: Vertical(g51)
    c: Equal(g50,g51)
    c: Coincident(g52,g9)
    c: Coincident(g53,g52)
    c: Coincident(g54,g9)
    c: Coincident(g55,g54)
    c: Coincident(g56,g55)
    c: Coincident(g56,g49)
    c: Coincident(g57,g55)
    c: Coincident(g57,g1)
    c: Coincident(g58,g53)
    c: Coincident(g58,g1)
    c: Coincident(g59,g53)
    c: Coincident(g59,g51)
    c: Equal(g56,g57)
    c: Parallel(g57,g56)
    c: Equal(g54,g55)
    c: Equal(g52,g53)
    c: Parallel(g52,g53)
    c: Parallel(g55,g54)
    c: Equal(g59,g58)
    c: Parallel(g59,g58)
    c: Coincident(g60,g10)
    c: Coincident(g61,g2)
    c: Equal(g60,g61)
    c: Parallel(g61,g60)
    c: Coincident(g62,g0)
    c: Coincident(g63,g62)
    c: Coincident(g63,g4)
    c: Equal(g62,g63)
    c: Parallel(g62,g63)
    c: Coincident(g64,g62)
    c: Coincident(g64,g20)
    c: Coincident(g65,g20)
    c: Coincident(g66,g16)
    c: Coincident(g67,g24)
    c: Coincident(g67,g28)
    c: Coincident(g68,g32)
    c: Coincident(g68,g26)
    c: Coincident(g69,g26)
    c: Coincident(g69,g36)
    c: Coincident(g70,g36)
    c: Coincident(g70,g44)
    c: Coincident(g71,g44)
    c: Coincident(g71,g46)
    c: Coincident(g72,g46)
    c: Coincident(g72,g38)
    c: Coincident(g73,g38)
    c: Coincident(g73,g48)
    c: Coincident(g74,g48)
    c: Coincident(g74,g54)
    c: Coincident(g75,g54)
    c: Coincident(g75,g52)
    c: Coincident(g76,g50)
    c: Coincident(g76,g52)
    c: Coincident(g77,g50)
    c: Coincident(g65,g16)
    c: DistanceY(g10,g8) = 10
    c: DistanceY(g2,g49) = 194.337
    c: DistanceX(g0,g0) = 700
    c: DistanceX(g25,g6) = 194.331
    c: DistanceX(g9,g49) = 194.337
    c: DistanceY(g4,g0) = 194.331
    c: DistanceY(g39,g5) = 194.331
    c: Coincident(g61,g77)
    c: Coincident(g61,g60)
    c: DistanceX(g-1,g1) = 350
    c: DistanceY(g-1,g0) = 304.5
    c: Coincident(g78,g79)
    c: Coincident(g79,g80)
    c: Coincident(g80,g81)
    c: Coincident(g81,g78)
    c: Horizontal(g78)
    c: Horizontal(g80)
    c: Vertical(g79)
    c: Vertical(g81)
    c: Horizontal(g82)
    c: Horizontal(g83)
    c: DistanceY(g83,g78) = 10
    c: DistanceX(g78,g83) = 10
    c: DistanceY(g79,g82) = 13
    c: DistanceX(g82,g79) = 10
    c: Coincident(g82,g1)
    c: Coincident(g84,g83)
    c: Coincident(g84,g8)
    c: Vertical(g84)
    c: Coincident(g85,g10)
    c: Coincident(g85,g82)
    c: Vertical(g85)
    c: Coincident(g86,g83)
    c: Coincident(g86,g4)
    c: Coincident(g87,g6)
    c: Coincident(g87,g82)
    c: Coincident(g83,g0)
    c: Coincident(g88,g33)
    c: Coincident(g88,g12)
    c: Coincident(g89,g66)
    c: PointOnObject(g89,g88)
    c: Coincident(g90,g89)
    c: Coincident(g90,g28)
    c: Coincident(g66,g18)
    c: Coincident(g91,g32)
    c: Coincident(g91,g28)
    c: Coincident(g92,g91)
    c: Coincident(g92,g89)
    c: DistanceY(g89,g22) = 33
FEATURE [Sketcher::SketchObject] Sketch011  label="sound_path_l45"
  ArcFitTolerance = 0
  AttachmentSupport = -> [XY_Plane]
  FullyConstrained = true
  MakeInternals = false
  MapMode = 5
  expr: Constraints[191] = <<dims>>.width3
  expr: Constraints[192] = <<dims>>.depth
  expr: Constraints[193] = <<dims>>.width2
  expr: Constraints[194] = <<dims>>.width3
  expr: Constraints[195] = <<dims>>.width1
  expr: Constraints[196] = <<dims>>.width2
  expr: Constraints[199] = <<dims>>.depth / 2
  expr: Constraints[200] = <<dims>>.height / 2
  expr: Constraints[213] = <<dims>>.thickness
  expr: Constraints[238] = <<dims>>.driver_offset + <<dims>>.thickness
  sketch-geometry (93):
    g0: LineSegment [constr] StartX=-350 StartY=304.5 StartZ=0 EndX=350 EndY=304.5 EndZ=0
    g1: LineSegment [constr] StartX=350 StartY=304.5 StartZ=0 EndX=350 EndY=-298.5 EndZ=0
    g2: LineSegment [constr] StartX=350 StartY=-298.5 StartZ=0 EndX=-350 EndY=-298.5 EndZ=0
    g3: LineSegment [constr] StartX=-350 StartY=-298.5 StartZ=0 EndX=-350 EndY=304.5 EndZ=0
    g4: LineSegment [constr] StartX=-155.669 StartY=110.169 StartZ=0 EndX=350 EndY=110.169 EndZ=0
    g5: LineSegment [constr] StartX=350 StartY=110.169 StartZ=0 EndX=350 EndY=100.169 EndZ=0
    g6: LineSegment [constr] StartX=350 StartY=100.169 StartZ=0 EndX=-155.669 EndY=100.169 EndZ=0
    g7: LineSegment [constr] StartX=-155.669 StartY=100.169 StartZ=0 EndX=-155.669 EndY=110.169 EndZ=0
    g8: LineSegment [constr] StartX=-350 StartY=-94.1628 StartZ=0 EndX=155.663 EndY=-94.1628 EndZ=0
    g9: LineSegment [constr] StartX=155.663 StartY=-94.1628 StartZ=0 EndX=155.663 EndY=-104.163 EndZ=0
    g10: LineSegment [constr] StartX=155.663 StartY=-104.163 StartZ=0 EndX=-350 EndY=-104.163 EndZ=0
    g11: LineSegment [constr] StartX=-350 StartY=-104.163 StartZ=0 EndX=-350 EndY=-94.1628 EndZ=0
    g12: LineSegment [constr] StartX=-155.669 StartY=304.5 StartZ=0 EndX=-252.834 EndY=304.5 EndZ=0
    g13: LineSegment [constr] StartX=-252.834 StartY=304.5 StartZ=0 EndX=-350 EndY=304.5 EndZ=0
    g14: LineSegment [constr] StartX=-350 StartY=304.5 StartZ=0 EndX=-350 EndY=207.334 EndZ=0
    g15: LineSegment [constr] StartX=-350 StartY=207.334 StartZ=0 EndX=-350 EndY=110.169 EndZ=0
    g16: LineSegment [constr] StartX=-252.834 StartY=304.5 StartZ=0 EndX=-204.251 EndY=207.334 EndZ=0
    g17: LineSegment [constr] StartX=-204.251 StartY=207.334 StartZ=0 EndX=-155.669 EndY=110.169 EndZ=0
    g18: LineSegment [constr] StartX=-155.669 StartY=110.169 StartZ=0 EndX=-252.834 EndY=158.751 EndZ=0
    g19: LineSegment [constr] StartX=-252.834 StartY=158.751 StartZ=0 EndX=-350 EndY=207.334 EndZ=0
    g20: LineSegment [constr] StartX=-155.669 StartY=110.169 StartZ=0 EndX=-155.669 EndY=207.334 EndZ=0
    g21: LineSegment [constr] StartX=-155.669 StartY=207.334 StartZ=0 EndX=-155.669 EndY=304.5 EndZ=0
    g22: LineSegment [constr] StartX=-155.669 StartY=110.169 StartZ=0 EndX=-252.834 EndY=110.169 EndZ=0
    g23: LineSegment [constr] StartX=-252.834 StartY=110.169 StartZ=0 EndX=-350 EndY=110.169 EndZ=0
    g24: LineSegment [constr] StartX=-155.669 StartY=100.169 StartZ=0 EndX=-252.834 EndY=100.169 EndZ=0
    g25: LineSegment [constr] StartX=-252.834 StartY=100.169 StartZ=0 EndX=-350 EndY=100.169 EndZ=0
    g26: LineSegment [constr] StartX=-155.669 StartY=100.169 StartZ=0 EndX=-155.669 EndY=3.00291 EndZ=0
    g27: LineSegment [constr] StartX=-155.669 StartY=3.00291 StartZ=0 EndX=-155.669 EndY=-94.1628 EndZ=0
    g28: LineSegment [constr] StartX=-155.669 StartY=100.169 StartZ=0 EndX=-252.834 EndY=51.5858 EndZ=0
    g29: LineSegment [constr] StartX=-350 StartY=100.169 StartZ=0 EndX=-350 EndY=3.00291 EndZ=0
    g30: LineSegment [constr] StartX=-350 StartY=3.00291 StartZ=0 EndX=-350 EndY=-94.1628 EndZ=0
    g31: LineSegment [constr] StartX=-252.834 StartY=51.5858 StartZ=0 EndX=-350 EndY=3.00291 EndZ=0
    g32: LineSegment [constr] StartX=-155.669 StartY=100.169 StartZ=0 EndX=-204.251 EndY=3.00291 EndZ=0
    g33: LineSegment [constr] StartX=-204.251 StartY=3.00291 StartZ=0 EndX=-252.834 EndY=-94.1628 EndZ=0
    g34: LineSegment [constr] StartX=-350 StartY=-94.1628 StartZ=0 EndX=-252.834 EndY=-94.1628 EndZ=0
    g35: LineSegment [constr] StartX=-252.834 StartY=-94.1628 StartZ=0 EndX=-155.669 EndY=-94.1628 EndZ=0
    g36: LineSegment [constr] StartX=155.663 StartY=100.169 StartZ=0 EndX=155.663 EndY=3.00291 EndZ=0
    g37: LineSegment [constr] StartX=155.663 StartY=3.00291 StartZ=0 EndX=155.663 EndY=-94.1628 EndZ=0
    g38: LineSegment [constr] StartX=155.663 StartY=-94.1628 StartZ=0 EndX=252.831 EndY=-94.1628 EndZ=0
    g39: LineSegment [constr] StartX=252.831 StartY=-94.1628 StartZ=0 EndX=350 EndY=-94.1628 EndZ=0
    g40: LineSegment [constr] StartX=350 StartY=-94.1628 StartZ=0 EndX=350 EndY=3.00291 EndZ=0
    g41: LineSegment [constr] StartX=350 StartY=100.169 StartZ=0 EndX=350 EndY=3.00291 EndZ=0
    g42: LineSegment [constr] StartX=155.663 StartY=100.169 StartZ=0 EndX=252.831 EndY=100.169 EndZ=0
    g43: LineSegment [constr] StartX=252.831 StartY=100.169 StartZ=0 EndX=350 EndY=100.169 EndZ=0
    g44: LineSegment [constr] StartX=252.831 StartY=100.169 StartZ=0 EndX=204.247 EndY=3.00291 EndZ=0
    g45: LineSegment [constr] StartX=204.247 StartY=3.00291 StartZ=0 EndX=155.663 EndY=-94.1628 EndZ=0
    g46: LineSegment [constr] StartX=155.663 StartY=-94.1628 StartZ=0 EndX=252.831 EndY=-45.5799 EndZ=0
    g47: LineSegment [constr] StartX=252.831 StartY=-45.5799 StartZ=0 EndX=350 EndY=3.00291 EndZ=0
    g48: LineSegment [constr] StartX=155.663 StartY=-104.163 StartZ=0 EndX=252.831 EndY=-104.163 EndZ=0
    g49: LineSegment [constr] StartX=252.831 StartY=-104.163 StartZ=0 EndX=350 EndY=-104.163 EndZ=0
    g50: LineSegment [constr] StartX=155.663 StartY=-104.163 StartZ=0 EndX=155.663 EndY=-201.331 EndZ=0
    g51: LineSegment [constr] StartX=155.663 StartY=-201.331 StartZ=0 EndX=155.663 EndY=-298.5 EndZ=0
    g52: LineSegment [constr] StartX=155.663 StartY=-104.163 StartZ=0 EndX=204.247 EndY=-201.331 EndZ=0
    g53: LineSegment [constr] StartX=204.247 StartY=-201.331 StartZ=0 EndX=252.831 EndY=-298.5 EndZ=0
    g54: LineSegment [constr] StartX=155.663 StartY=-104.163 StartZ=0 EndX=252.831 EndY=-152.747 EndZ=0
    g55: LineSegment [constr] StartX=252.831 StartY=-152.747 StartZ=0 EndX=350 EndY=-201.331 EndZ=0
    g56: LineSegment [constr] StartX=350 StartY=-201.331 StartZ=0 EndX=350 EndY=-104.163 EndZ=0
    g57: LineSegment [constr] StartX=350 StartY=-201.331 StartZ=0 EndX=350 EndY=-298.5 EndZ=0
    g58: LineSegment [constr] StartX=252.831 StartY=-298.5 StartZ=0 EndX=350 EndY=-298.5 EndZ=0
    g59: LineSegment [constr] StartX=252.831 StartY=-298.5 StartZ=0 EndX=155.663 EndY=-298.5 EndZ=0
    g60: LineSegment [constr] StartX=-350 StartY=-104.163 StartZ=0 EndX=-350 EndY=-201.331 EndZ=0
    g61: LineSegment [constr] StartX=-350 StartY=-201.331 StartZ=0 EndX=-350 EndY=-298.5 EndZ=0
    g62: LineSegment [constr] StartX=350 StartY=304.5 StartZ=0 EndX=350 EndY=207.334 EndZ=0
    g63: LineSegment [constr] StartX=350 StartY=207.334 StartZ=0 EndX=350 EndY=110.169 EndZ=0
    g64: LineSegment [constr] StartX=350 StartY=207.334 StartZ=0 EndX=-155.669 EndY=207.334 EndZ=0
    g65: LineSegment [constr] StartX=-155.669 StartY=207.334 StartZ=0 EndX=-204.251 EndY=207.334 EndZ=0
    g66: LineSegment [constr] StartX=-204.251 StartY=207.334 StartZ=0 EndX=-252.834 EndY=158.751 EndZ=0
    g67: LineSegment [constr] StartX=-252.834 StartY=100.169 StartZ=0 EndX=-252.834 EndY=51.5858 EndZ=0
    g68: LineSegment [constr] StartX=-204.251 StartY=3.00291 StartZ=0 EndX=-155.669 EndY=3.00291 EndZ=0
    g69: LineSegment [constr] StartX=-155.669 StartY=3.00291 StartZ=0 EndX=155.663 EndY=3.00291 EndZ=0
    g70: LineSegment [constr] StartX=155.663 StartY=3.00291 StartZ=0 EndX=204.247 EndY=3.00291 EndZ=0
    g71: LineSegment [constr] StartX=204.247 StartY=3.00291 StartZ=0 EndX=252.831 EndY=-45.5799 EndZ=0
    g72: LineSegment [constr] StartX=252.831 StartY=-45.5799 StartZ=0 EndX=252.831 EndY=-94.1628 EndZ=0
    g73: LineSegment StartX=252.831 StartY=-94.1628 StartZ=0 EndX=252.831 EndY=-104.163 EndZ=0
    g74: LineSegment StartX=252.831 StartY=-104.163 StartZ=0 EndX=252.831 EndY=-152.747 EndZ=0
    g75: LineSegment StartX=252.831 StartY=-152.747 StartZ=0 EndX=204.247 EndY=-201.331 EndZ=0
    g76: LineSegment StartX=155.663 StartY=-201.331 StartZ=0 EndX=204.247 EndY=-201.331 EndZ=0
    g77: LineSegment StartX=155.663 StartY=-201.331 StartZ=0 EndX=-350 EndY=-201.331 EndZ=0
    g78: LineSegment [constr] StartX=-360 StartY=314.5 StartZ=0 EndX=360 EndY=314.5 EndZ=0
    g79: LineSegment [constr] StartX=360 StartY=314.5 StartZ=0 EndX=360 EndY=-311.5 EndZ=0
    g80: LineSegment [constr] StartX=360 StartY=-311.5 StartZ=0 EndX=-360 EndY=-311.5 EndZ=0
    g81: LineSegment [constr] StartX=-360 StartY=-311.5 StartZ=0 EndX=-360 EndY=314.5 EndZ=0
    g82: LineSegment [constr] StartX=350 StartY=-298.5 StartZ=0 EndX=-350 EndY=-298.5 EndZ=0
    g83: LineSegment [constr] StartX=-350 StartY=304.5 StartZ=0 EndX=350 EndY=304.5 EndZ=0
    g84: LineSegment [constr] StartX=-350 StartY=304.5 StartZ=0 EndX=-350 EndY=-94.1628 EndZ=0
    g85: LineSegment [constr] StartX=-350 StartY=-104.163 StartZ=0 EndX=-350 EndY=-298.5 EndZ=0
    g86: LineSegment [constr] StartX=350 StartY=304.5 StartZ=0 EndX=350 EndY=110.169 EndZ=0
    g87: LineSegment [constr] StartX=350 StartY=100.169 StartZ=0 EndX=350 EndY=-298.5 EndZ=0
    g88: LineSegment [constr] StartX=-252.834 StartY=-94.1628 StartZ=0 EndX=-252.834 EndY=304.5 EndZ=0
    g89: LineSegment [constr] StartX=-252.834 StartY=158.751 StartZ=0 EndX=-252.834 EndY=77.1686 EndZ=0
    g90: LineSegment [constr] StartX=-252.834 StartY=77.1686 StartZ=0 EndX=-252.834 EndY=51.5858 EndZ=0
    g91: LineSegment [constr] StartX=-204.251 StartY=3.00291 StartZ=0 EndX=-252.834 EndY=51.5858 EndZ=0
    g92: LineSegment [constr] StartX=-252.834 StartY=51.5858 StartZ=0 EndX=-252.834 EndY=77.1686 EndZ=0
  constraints (239):
    c: Coincident(g0,g1)
    c: Coincident(g1,g2)
    c: Coincident(g2,g3)
    c: Coincident(g3,g0)
    c: Horizontal(g0)
    c: Horizontal(g2)
    c: Vertical(g1)
    c: Vertical(g3)
    c: Coincident(g4,g5)
    c: Coincident(g5,g6)
    c: Coincident(g6,g7)
    c: Coincident(g7,g4)
    c: Horizontal(g4)
    c: Horizontal(g6)
    c: Vertical(g5)
    c: Vertical(g7)
    c: PointOnObject(g5,g1)
    c: Coincident(g8,g9)
    c: Coincident(g9,g10)
    c: Coincident(g10,g11)
    c: Coincident(g11,g8)
    c: Horizontal(g8)
    c: Horizontal(g10)
    c: Vertical(g9)
    c: Vertical(g11)
    c: PointOnObject(g8,g3)
    c: Equal(g7,g9)
    c: Coincident(g20,g4)
    c: PointOnObject(g21,g0)
    c: Coincident(g22,g4)
    c: PointOnObject(g23,g3)
    c: Coincident(g12,g21)
    c: PointOnObject(g12,g0)
    c: Coincident(g13,g12)
    c: Coincident(g13,g0)
    c: Coincident(g14,g0)
    c: PointOnObject(g14,g3)
    c: Coincident(g15,g14)
    c: Coincident(g15,g23)
    c: Equal(g14,g15)
    c: Equal(g12,g13)
    c: Coincident(g16,g12)
    c: Coincident(g17,g4)
    c: Coincident(g18,g4)
    c: Coincident(g19,g14)
    c: Coincident(g16,g17)
    c: Coincident(g18,g19)
    c: Coincident(g20,g21)
    c: Vertical(g20)
    c: Vertical(g21)
    c: Coincident(g22,g23)
    c: Horizontal(g22)
    c: Horizontal(g23)
    c: Equal(g17,g16)
    c: Equal(g21,g20)
    c: Equal(g19,g18)
    c: Equal(g22,g23)
    c: Parallel(g19,g18)
    c: Parallel(g16,g17)
    c: Coincident(g24,g6)
    c: Coincident(g25,g24)
    c: PointOnObject(g25,g3)
    c: Horizontal(g25)
    c: Parallel(g25,g24)
    c: Equal(g24,g25)
    c: Coincident(g26,g6)
    c: Coincident(g27,g26)
    c: PointOnObject(g27,g8)
    c: Parallel(g27,g26)
    c: Equal(g26,g27)
    c: Parallel(g27,g3)
    c: Coincident(g28,g6)
    c: Coincident(g29,g25)
    c: Coincident(g30,g8)
    c: Coincident(g29,g30)
    c: Equal(g29,g30)
    c: Coincident(g31,g28)
    c: Coincident(g31,g29)
    c: Parallel(g31,g28)
    c: Equal(g31,g28)
    c: Parallel(g30,g29)
    c: Coincident(g32,g6)
    c: Coincident(g33,g32)
    c: Coincident(g34,g8)
    c: Coincident(g34,g33)
    c: Coincident(g35,g33)
    c: Coincident(g35,g27)
    c: Parallel(g33,g32)
    c: Equal(g35,g34)
    c: Parallel(g35,g34)
    c: Equal(g33,g32)
    c: PointOnObject(g36,g6)
    c: Coincident(g37,g36)
    c: Coincident(g37,g8)
    c: Parallel(g37,g36)
    c: Parallel(g36,g1)
    c: Equal(g36,g37)
    c: Coincident(g38,g8)
    c: Horizontal(g38)
    c: Coincident(g39,g38)
    c: PointOnObject(g39,g1)
    c: Horizontal(g39)
    c: Coincident(g40,g39)
    c: Coincident(g41,g5)
    c: Coincident(g41,g40)
    c: Coincident(g42,g36)
    c: Coincident(g43,g42)
    c: Coincident(g43,g5)
    c: Coincident(g44,g42)
    c: Coincident(g45,g44)
    c: Coincident(g45,g8)
    c: Coincident(g46,g8)
    c: Coincident(g47,g46)
    c: Coincident(g47,g40)
    c: Equal(g42,g43)
    c: Equal(g44,g45)
    c: Parallel(g42,g43)
    c: Parallel(g45,g44)
    c: Equal(g46,g47)
    c: Equal(g41,g40)
    c: Parallel(g29,g40)
    c: Parallel(g46,g47)
    c: Equal(g38,g39)
    c: Coincident(g48,g9)
    c: Horizontal(g48)
    c: Coincident(g49,g48)
    c: PointOnObject(g49,g1)
    c: Horizontal(g49)
    c: Equal(g49,g48)
    c: Coincident(g50,g9)
    c: Vertical(g50)
    c: Coincident(g51,g50)
    c: PointOnObject(g51,g2)
    c: Vertical(g51)
    c: Equal(g50,g51)
    c: Coincident(g52,g9)
    c: Coincident(g53,g52)
    c: Coincident(g54,g9)
    c: Coincident(g55,g54)
    c: Coincident(g56,g55)
    c: Coincident(g56,g49)
    c: Coincident(g57,g55)
    c: Coincident(g57,g1)
    c: Coincident(g58,g53)
    c: Coincident(g58,g1)
    c: Coincident(g59,g53)
    c: Coincident(g59,g51)
    c: Equal(g56,g57)
    c: Parallel(g57,g56)
    c: Equal(g54,g55)
    c: Equal(g52,g53)
    c: Parallel(g52,g53)
    c: Parallel(g55,g54)
    c: Equal(g59,g58)
    c: Parallel(g59,g58)
    c: Coincident(g60,g10)
    c: Coincident(g61,g2)
    c: Equal(g60,g61)
    c: Parallel(g61,g60)
    c: Coincident(g62,g0)
    c: Coincident(g63,g62)
    c: Coincident(g63,g4)
    c: Equal(g62,g63)
    c: Parallel(g62,g63)
    c: Coincident(g64,g62)
    c: Coincident(g64,g20)
    c: Coincident(g65,g20)
    c: Coincident(g66,g16)
    c: Coincident(g67,g24)
    c: Coincident(g67,g28)
    c: Coincident(g68,g32)
    c: Coincident(g68,g26)
    c: Coincident(g69,g26)
    c: Coincident(g69,g36)
    c: Coincident(g70,g36)
    c: Coincident(g70,g44)
    c: Coincident(g71,g44)
    c: Coincident(g71,g46)
    c: Coincident(g72,g46)
    c: Coincident(g72,g38)
    c: Coincident(g73,g38)
    c: Coincident(g73,g48)
    c: Coincident(g74,g48)
    c: Coincident(g74,g54)
    c: Coincident(g75,g54)
    c: Coincident(g75,g52)
    c: Coincident(g76,g50)
    c: Coincident(g76,g52)
    c: Coincident(g77,g50)
    c: Coincident(g65,g16)
    c: DistanceY(g10,g8) = 10
    c: DistanceY(g2,g49) = 194.337
    c: DistanceX(g0,g0) = 700
    c: DistanceX(g25,g6) = 194.331
    c: DistanceX(g9,g49) = 194.337
    c: DistanceY(g4,g0) = 194.331
    c: DistanceY(g39,g5) = 194.331
    c: Coincident(g61,g77)
    c: Coincident(g61,g60)
    c: DistanceX(g-1,g1) = 350
    c: DistanceY(g-1,g0) = 304.5
    c: Coincident(g78,g79)
    c: Coincident(g79,g80)
    c: Coincident(g80,g81)
    c: Coincident(g81,g78)
    c: Horizontal(g78)
    c: Horizontal(g80)
    c: Vertical(g79)
    c: Vertical(g81)
    c: Horizontal(g82)
    c: Horizontal(g83)
    c: DistanceY(g83,g78) = 10
    c: DistanceX(g78,g83) = 10
    c: DistanceY(g79,g82) = 13
    c: DistanceX(g82,g79) = 10
    c: Coincident(g82,g1)
    c: Coincident(g84,g83)
    c: Coincident(g84,g8)
    c: Vertical(g84)
    c: Coincident(g85,g10)
    c: Coincident(g85,g82)
    c: Vertical(g85)
    c: Coincident(g86,g83)
    c: Coincident(g86,g4)
    c: Coincident(g87,g6)
    c: Coincident(g87,g82)
    c: Coincident(g83,g0)
    c: Coincident(g88,g33)
    c: Coincident(g88,g12)
    c: Coincident(g89,g66)
    c: PointOnObject(g89,g88)
    c: Coincident(g90,g89)
    c: Coincident(g90,g28)
    c: Coincident(g66,g18)
    c: Coincident(g91,g32)
    c: Coincident(g91,g28)
    c: Coincident(g92,g91)
    c: Coincident(g92,g89)
    c: DistanceY(g89,g22) = 33
FEATURE [PartDesign::Body] Body  label="soundpath"
  AllowCompound = false
  Group = -> [Sketch003,Pad001,Sketch004,Sketch009,Sketch010,Sketch011]
  Origin = -> Origin
  Tip = -> Pad001
FEATURE [Sketcher::SketchObject] Sketch012
  ArcFitTolerance = 1e-06
  AttachmentSupport = -> [XZ_Plane002]
  FullyConstrained = true
  MakeInternals = false
  MapMode = 5
  Placement = pos=(0,0,0) rot=(1,0,0;1.5708rad)
  expr: Constraints[10] = <<bdim>>.bpb_h
  sketch-geometry (4):
    g0: LineSegment StartX=0 StartY=0 StartZ=0 EndX=30 EndY=0 EndZ=0
    g1: LineSegment StartX=30 StartY=0 StartZ=0 EndX=30 EndY=30 EndZ=0
    g2: LineSegment StartX=30 StartY=30 StartZ=0 EndX=0 EndY=30 EndZ=0
    g3: LineSegment StartX=0 StartY=30 StartZ=0 EndX=0 EndY=0 EndZ=0
  constraints (11):
    c: Coincident(g0,g1)
    c: Coincident(g1,g2)
    c: Coincident(g2,g3)
    c: Coincident(g3,g0)
    c: Horizontal(g0)
    c: Horizontal(g2)
    c: Vertical(g1)
    c: Vertical(g3)
    c: Coincident(g0,g-1)
    c: Equal(g2,g1)
    c: DistanceX(g2,g2) = 30
FEATURE [PartDesign::Pad] Pad
  Direction = (0,-1,2e-16)
  Length = 575
  Length2 = 10
  Placement = pos=(0,0,0) rot=(1,0,0;1.5708rad)
  Profile = -> Sketch012
  ReferenceAxis = -> Sketch012 [N_Axis]
  Suppressed = false
  Type = 0
  expr: Length = <<bdim>>.bpb_w
FEATURE [PartDesign::Body] Body001  label="back_bar_001"
  AllowCompound = false
  Group = -> [Sketch012,Pad]
  Origin = -> Origin002
  Tip = -> Pad
FEATURE [Spreadsheet::Sheet] Spreadsheet002  label="bdim"
  cells = B2='width; C2='height; D2='thick; F2='bar side size; G2(bar_side_size)==30 mm; A3='back panels; B3(bp_w)==tp_w; C3(bp_h)==<<dims>>.width; D3(bp_t)==<<dims>>.thickness; F3='driver; A4='back panel bars; B4(bpb_w)==bp_w - 2 * bar_side_size; C4(bpb_h)==bar_side_size; D4(bpb_t)==bar_side_size; F4='baffle diam; G4(baffle_diameter)==<<dims>>.driver_mount_diameter; A5='bottom panel; B5(tp_w)==635 mm; C5(tp_h)==<<dims>>.depth; D5(tp_t)==<<dims>>.thickness; F5='total diam; G5(dr_tdiam)==305.6 mm; A6='side panel; B6(sp_w)==<<dims>>.width; C6(sp_h)==<<dims>>.depth - fp_t - bp_t; D6(sp_thick)==<<dims>>.thickness; F6='depth; G6(dr_d)==135.9 mm; A7='side panel bar 1; B7(spb_w)==sp_h; C7(spb_h)==bar_side_size; D7(spb_t)==bar_side_size; F7='speakon cutout diam; G7(spkon_cd)==24 mm; A8='side panel bar 2; B8(spbb_w)==sp_w - 2 * bar_side_size; C8(spbb_h)==bar_side_size; D8(spbb_t)==bar_side_size; F8='speakon bolt length; G8(spkon_bl)==29.2 mm; A9='front panel; B9(fp_w)==bp_w - <<dims>>.width3 - tp_t - f2_t; C9(fp_h)==bp_h; D9(fp_t)==<<dims>>.thickness; F9='bolt diam; G9==3.2 mm; A10='fin 1; B10(f1_w)==sp_h - <<dims>>.width1; C10(f1_h)==bp_h; D10(f1_t)==<<dims>>.thickness; A11='fin 2; B11(f2_w)==sp_h - <<dims>>.width2 + fp_t; C11(f2_h)==bp_h; D11(f2_t)==<<dims>>.thickness; G11==1187 mm - tp_h; A12='front panel bar; B12(fpb_w)==bar_side_size; C12(fpb_h)==fp_w - spb_h - sp_thick; D12(fpb_t)==bar_side_size; A13='side panel 2; B13(sp2_w)==<<dims>>.width; C13(sp2_h)==<<dims>>.depth - bp_t; D13(sp2_t)==<<dims>>.thickness; F13==bpb_w - fpb_h; A14='side panel 2 bar 1; B14(sp2b1_w)==sp2_h; C14(sp2b1_h)==bar_side_size; D14(sp2b1_t)==bar_side_size; A15='side panel 2 bar 2; B15(sp2b2_w)==sp_w - 2 * bar_side_size; C15(sp2b2_h)==bar_side_size; D15(sp2b2_t)==bar_side_size; A16='brace bar fin 2; B16(bbf2_w)==f2_w - bbf2_t - fp_t; C16(bbf2_h)==bar_side_size; D16(bbf2_t)==bar_side_size; A17='brace bar fin 1; B17(bbf1_w)==f1_w - bar_side_size; C17(bbf1_h)==bar_side_size; D17(bbf1_t)==bar_side_size; A18='brace bar back panel 1; B18(bbbp1_w)==<<dims>>.width2 + <<dims>>.width3 + f2_t - spb_t; C18(bbbp1_h)==bar_side_size; D18(bbbp1_t)==bar_side_size; A19='brace bar back panel 2; B19(bbbp2_w)==<<dims>>.width1 - spb_t; C19(bbbp2_h)==bar_side_size; D19(bbbp2_t)==bar_side_size; A20='middle brace bar fin 1 ; B20(mbbf1_w)==f1_w - bar_side_size; C20(mbbf1_h)==bar_side_size; D20(mbbf1_t)==bar_side_size; A21='driver brace bar; B21(dbb_w)==150 mm; C21(dbb_h)==bar_side_size; D21(dbb_t)==bar_side_size; A22='driver brace bar 2; B22(dbb2_w)==70 mm; C22(dbb2_h)==bar_side_size; D22(dbb2_t)==bar_side_size; A23='middle brace bar fin 2; B23(mbbf2_w)==f2_w + fp_t; C23(mbbf2_h)==bar_side_size; D23(mbbf2_t)==bar_side_size; A24='middle brace bar side pannel 2; B24(mbbsp2_w)==sp2_h - bar_side_size; C24(mbbsp2_h)==bar_side_size; D24(mbbsp2_t)==bar_side_size; A25='fin support 2; B25(f2s_w)==f2_w + fp_t; C25(f2s_h)==<<dims>>.width1; D25(f2s_t)==<<dims>>.thickness; A26='fin support 12; B26(f12s_w)==sp_h - <<dims>>.width1 - <<dims>>.width2; C26(f12s_h)==<<dims>>.width2; D26(f12s_t)==<<dims>>.thickness; A27='fin support 1; B27(f1s_w)==f1_w - bar_side_size; C27(f1s_h)==<<dims>>.width2; D27(f1s_t)==<<dims>>.thickness; A28='middle brace bar side pannel 1; B28(mbbsp1_w)==sp_h - 2 * bar_side_size; C28(mbbsp1_h)==bar_side_size; D28(mbbsp1_t)==bar_side_size; A29='middle brace bar fin 1 and 2; B29(mbbf12_w)==sp_h - <<dims>>.width1 - <<dims>>.width2; C29(mbbf12_h)==bar_side_size; D29(mbbf12_t)==bar_side_size; A30='pannel A; B30(pA_w)==1187 mm; C30(pA_h)==tp_w; D30(pA_t)==<<dims>>.thickness; A31='pannel B; B31(pB_w)==1115 mm; C31(pB_h)==<<dims>>.width; D31(pB_t)==<<dims>>.thickness; A32='pannel C; B32(pC_w)==tp_w; C32(pC_h)==<<dims>>.width; D32(pC_t)==<<dims>>.thickness; A33='middle brace bar back panel 2; B33(mbbbp2_w)==bbbp2_w - bar_side_size; C33(mbbbp2_h)==bbbp2_h; D33(mbbbp2_t)==bbbp2_t
FEATURE [Sketcher::SketchObject] Sketch014
  ArcFitTolerance = 1e-06
  AttachmentSupport = -> [YZ_Plane004]
  FullyConstrained = true
  MakeInternals = false
  MapMode = 5
  Placement = pos=(0,0,0) rot=(0.57735,0.57735,0.57735;2.0944rad)
  expr: Constraints[10] = <<bdim>>.bp_w
  expr: Constraints[25] = <<bdim>>.bp_h * 0.25
  expr: Constraints[26] = <<bdim>>.spkon_bl
  expr: Constraints[28] = <<bdim>>.spkon_cd
  expr: Constraints[29] = <<bdim>>.bp_w / 2
  expr: Constraints[31] = <<bdim>>.bp_h * 0.25
  expr: Constraints[32] = <<bdim>>.bp_w / 2
  expr: Constraints[9] = <<bdim>>.bp_h
  sketch-geometry (13):
    g0: LineSegment StartX=0 StartY=0 StartZ=0 EndX=635 EndY=0 EndZ=0
    g1: LineSegment StartX=635 StartY=0 StartZ=0 EndX=635 EndY=320 EndZ=0
    g2: LineSegment StartX=635 StartY=320 StartZ=0 EndX=0 EndY=320 EndZ=0
    g3: LineSegment StartX=0 StartY=320 StartZ=0 EndX=0 EndY=0 EndZ=0
    g4: LineSegment [constr] StartX=332.1 StartY=254.6 StartZ=0 EndX=332.1 EndY=225.4 EndZ=0
    g5: LineSegment [constr] StartX=332.1 StartY=225.4 StartZ=0 EndX=302.9 EndY=225.4 EndZ=0
    g6: LineSegment [constr] StartX=302.9 StartY=225.4 StartZ=0 EndX=302.9 EndY=254.6 EndZ=0
    g7: LineSegment [constr] StartX=302.9 StartY=254.6 StartZ=0 EndX=332.1 EndY=254.6 EndZ=0
    g8: LineSegment [constr] StartX=332.1 StartY=225.4 StartZ=0 EndX=302.9 EndY=254.6 EndZ=0
    g9: LineSegment [constr] StartX=302.9 StartY=225.4 StartZ=0 EndX=332.1 EndY=254.6 EndZ=0
    g10: GeomPoint [constr] X=317.5 Y=240 Z=0
    g11: Circle CenterX=317.5 CenterY=240 CenterZ=0 NormalX=0 NormalY=0 NormalZ=1 AngleXU=0 Radius=12
    g12: Circle CenterX=317.5 CenterY=80 CenterZ=0 NormalX=0 NormalY=0 NormalZ=1 AngleXU=0 Radius=12
  constraints (33):
    c: Coincident(g0,g1)
    c: Coincident(g1,g2)
    c: Coincident(g2,g3)
    c: Coincident(g3,g0)
    c: Horizontal(g0)
    c: Horizontal(g2)
    c: Vertical(g1)
    c: Vertical(g3)
    c: Coincident(g0,g-1)
    c: DistanceY(g3,g3) = 320
    c: DistanceX(g0,g0) = 635
    c: Coincident(g4,g5)
    c: Coincident(g5,g6)
    c: Coincident(g6,g7)
    c: Coincident(g7,g4)
    c: Vertical(g4)
    c: Vertical(g6)
    c: Horizontal(g5)
    c: Horizontal(g7)
    c: Equal(g5,g4)
    c: Coincident(g8,g4)
    c: Coincident(g8,g6)
    c: Coincident(g9,g5)
    c: Coincident(g9,g4)
    c: Symmetric(g8,g8,g10)
    c: DistanceY(g10,g2) = 80
    c: DistanceY(g6,g6) = 29.2
    c: Coincident(g11,g10)
    c: Diameter(g11) = 24
    c: DistanceX(g2,g10) = 317.5
    c: Equal(g12,g11)
    c: DistanceY(g0,g12) = 80
    c: DistanceX(g0,g12) = 317.5
FEATURE [PartDesign::Pad] Pad003
  Direction = (1,0,0)
  Length = 13
  Length2 = 10
  Placement = pos=(0,0,0) rot=(1,1,1;2.0944rad)
  Profile = -> Sketch014
  ReferenceAxis = -> Sketch014 [N_Axis]
  Suppressed = false
  Type = 0
  expr: Length = <<bdim>>.bp_t
FEATURE [PartDesign::Body] Body003  label="back_panel"
  AllowCompound = false
  Group = -> [Sketch014,Pad003]
  Origin = -> Origin004
  Tip = -> Pad003
FEATURE [Sketcher::SketchObject] Sketch015
  ArcFitTolerance = 1e-06
  AttachmentSupport = -> [XZ_Plane005]
  FullyConstrained = true
  MakeInternals = false
  MapMode = 5
  Placement = pos=(0,0,0) rot=(1,0,0;1.5708rad)
  expr: Constraints[10] = <<bdim>>.bpb_h
  sketch-geometry (4):
    g0: LineSegment StartX=0 StartY=0 StartZ=0 EndX=30 EndY=0 EndZ=0
    g1: LineSegment StartX=30 StartY=0 StartZ=0 EndX=30 EndY=30 EndZ=0
    g2: LineSegment StartX=30 StartY=30 StartZ=0 EndX=0 EndY=30 EndZ=0
    g3: LineSegment StartX=0 StartY=30 StartZ=0 EndX=0 EndY=0 EndZ=0
  constraints (11):
    c: Coincident(g0,g1)
    c: Coincident(g1,g2)
    c: Coincident(g2,g3)
    c: Coincident(g3,g0)
    c: Horizontal(g0)
    c: Horizontal(g2)
    c: Vertical(g1)
    c: Vertical(g3)
    c: Coincident(g0,g-1)
    c: Equal(g2,g1)
    c: DistanceX(g2,g2) = 30
FEATURE [PartDesign::Pad] Pad004
  Direction = (0,-1,2e-16)
  Length = 575
  Length2 = 10
  Placement = pos=(0,0,0) rot=(1,0,0;1.5708rad)
  Profile = -> Sketch015
  ReferenceAxis = -> Sketch015 [N_Axis]
  Suppressed = false
  Type = 0
  expr: Length = <<bdim>>.bpb_w
FEATURE [PartDesign::Body] Body004  label="back_bar_002"
  AllowCompound = false
  Group = -> [Sketch015,Pad004]
  Origin = -> Origin005
  Tip = -> Pad004
FEATURE [Sketcher::SketchObject] Sketch017
  ArcFitTolerance = 1e-06
  AttachmentSupport = -> [YZ_Plane007]
  FullyConstrained = true
  MakeInternals = false
  MapMode = 5
  Placement = pos=(0,0,0) rot=(0.57735,0.57735,0.57735;2.0944rad)
  expr: Constraints[10] = <<bdim>>.tp_h
  expr: Constraints[9] = <<bdim>>.tp_w
  sketch-geometry (4):
    g0: LineSegment StartX=0 StartY=0 StartZ=0 EndX=635 EndY=0 EndZ=0
    g1: LineSegment StartX=635 StartY=0 StartZ=0 EndX=635 EndY=700 EndZ=0
    g2: LineSegment StartX=635 StartY=700 StartZ=0 EndX=0 EndY=700 EndZ=0
    g3: LineSegment StartX=0 StartY=700 StartZ=0 EndX=0 EndY=0 EndZ=0
  constraints (11):
    c: Coincident(g0,g1)
    c: Coincident(g1,g2)
    c: Coincident(g2,g3)
    c: Coincident(g3,g0)
    c: Horizontal(g0)
    c: Horizontal(g2)
    c: Vertical(g1)
    c: Vertical(g3)
    c: Coincident(g0,g-1)
    c: DistanceX(g0,g0) = 635
    c: DistanceY(g3,g3) = 700
FEATURE [PartDesign::Pad] Pad006
  Direction = (1,0,0)
  Length = 13
  Length2 = 10
  Placement = pos=(0,0,0) rot=(1,1,1;2.0944rad)
  Profile = -> Sketch017
  ReferenceAxis = -> Sketch017 [N_Axis]
  Suppressed = false
  Type = 0
  expr: Length = <<bdim>>.tp_t
FEATURE [PartDesign::Body] Body006  label="bottom_panel"
  AllowCompound = false
  Group = -> [Sketch017,Pad006]
  Origin = -> Origin007
  Tip = -> Pad006
FEATURE [Sketcher::SketchObject] Sketch018
  ArcFitTolerance = 1e-06
  AttachmentSupport = -> [YZ_Plane008]
  FullyConstrained = true
  MakeInternals = false
  MapMode = 5
  Placement = pos=(0,0,0) rot=(0.57735,0.57735,0.57735;2.0944rad)
  expr: Constraints[10] = <<bdim>>.tp_h
  expr: Constraints[9] = <<bdim>>.tp_w
  sketch-geometry (4):
    g0: LineSegment StartX=0 StartY=0 StartZ=0 EndX=635 EndY=0 EndZ=0
    g1: LineSegment StartX=635 StartY=0 StartZ=0 EndX=635 EndY=700 EndZ=0
    g2: LineSegment StartX=635 StartY=700 StartZ=0 EndX=0 EndY=700 EndZ=0
    g3: LineSegment StartX=0 StartY=700 StartZ=0 EndX=0 EndY=0 EndZ=0
  constraints (11):
    c: Coincident(g0,g1)
    c: Coincident(g1,g2)
    c: Coincident(g2,g3)
    c: Coincident(g3,g0)
    c: Horizontal(g0)
    c: Horizontal(g2)
    c: Vertical(g1)
    c: Vertical(g3)
    c: Coincident(g0,g-1)
    c: DistanceX(g0,g0) = 635
    c: DistanceY(g3,g3) = 700
FEATURE [PartDesign::Pad] Pad007
  Direction = (1,0,0)
  Length = 13
  Length2 = 10
  Placement = pos=(0,0,0) rot=(1,1,1;2.0944rad)
  Profile = -> Sketch018
  ReferenceAxis = -> Sketch018 [N_Axis]
  Suppressed = false
  Type = 0
  expr: Length = <<bdim>>.tp_t
FEATURE [PartDesign::Body] Body007  label="top_panel"
  AllowCompound = false
  Group = -> [Sketch018,Pad007]
  Origin = -> Origin008
  Tip = -> Pad007
FEATURE [Sketcher::SketchObject] Sketch019
  ArcFitTolerance = 1e-06
  AttachmentSupport = -> [YZ_Plane009]
  FullyConstrained = true
  MakeInternals = false
  MapMode = 5
  Placement = pos=(0,0,0) rot=(0.57735,0.57735,0.57735;2.0944rad)
  expr: Constraints[18] = <<bdim>>.dr_d
  expr: Constraints[19] = <<bdim>>.dr_tdiam / 2
  expr: Constraints[20] = 6.4 mm
  expr: Constraints[22] = <<bdim>>.baffle_diameter / 2
  expr: Constraints[23] = <<bdim>>.dr_tdiam / 4
  expr: Constraints[24] = <<bdim>>.dr_d / 4
  expr: Constraints[25] = <<bdim>>.dr_d / 4
  sketch-geometry (9):
    g0: ArcOfCircle CenterX=0 CenterY=207.3 CenterZ=0 NormalX=0 NormalY=0 NormalZ=1 AngleXU=0 Radius=207.3 StartAngle=4.71239 EndAngle=4.87702
    g1: LineSegment StartX=33.975 StartY=2.80308 StartZ=0 EndX=146.4 EndY=0 EndZ=0
    g2: LineSegment StartX=146.4 StartY=0 StartZ=0 EndX=152.8 EndY=0 EndZ=0
    g3: LineSegment StartX=152.8 StartY=0 StartZ=0 EndX=152.8 EndY=12.2 EndZ=0
    g4: LineSegment StartX=152.8 StartY=12.2 StartZ=0 EndX=140.6 EndY=12.2 EndZ=0
    g5: LineSegment StartX=140.6 StartY=12.2 StartZ=0 EndX=76.4 EndY=101.925 EndZ=0
    g6: LineSegment StartX=76.4 StartY=101.925 StartZ=0 EndX=76.4 EndY=135.9 EndZ=0
    g7: LineSegment StartX=76.4 StartY=135.9 StartZ=0 EndX=0 EndY=135.9 EndZ=0
    g8: LineSegment StartX=0 StartY=135.9 StartZ=0 EndX=-3.81e-14 EndY=0 EndZ=0
  constraints (27):
    c: Coincident(g0,g-1)
    c: PointOnObject(g0,g-2)
    c: Coincident(g1,g0)
    c: PointOnObject(g1,g-1)
    c: Coincident(g1,g2)
    c: PointOnObject(g2,g-1)
    c: Coincident(g2,g3)
    c: Vertical(g3)
    c: Coincident(g3,g4)
    c: Horizontal(g4)
    c: Coincident(g4,g5)
    c: Coincident(g5,g6)
    c: Vertical(g6)
    c: Coincident(g6,g7)
    c: PointOnObject(g7,g-2)
    c: Horizontal(g7)
    c: Coincident(g7,g8)
    c: Coincident(g8,g0)
    c: DistanceY(g8,g8) = 135.9
    c: DistanceX(g0,g2) = 152.8
    c: DistanceX(g2,g2) = 6.4
    c: Radius(g0) = 207.3
    c: DistanceX(g0,g4) = 140.6
    c: DistanceX(g7,g7) = 76.4
    c: DistanceY(g6,g6) = 33.975
    c: DistanceX(g0,g0) = 33.975
    c: Equal(g3,g4)
FEATURE [PartDesign::Revolution] Revolution
  Angle = 360
  Angle2 = 60
  Axis = (0,0,1)
  Base = (0,0,0)
  Placement = pos=(0,0,0) rot=(1,1,1;2.0944rad)
  Profile = -> Sketch019
  ReferenceAxis = -> Sketch019 [V_Axis]
  Reversed = true
  Suppressed = false
  Type = 0
FEATURE [PartDesign::Body] Body008  label="12lfa_driver"
  AllowCompound = false
  Group = -> [Sketch019,Revolution]
  Origin = -> Origin009
  Tip = -> Revolution
FEATURE [Sketcher::SketchObject] Sketch020
  ArcFitTolerance = 1e-06
  AttachmentSupport = -> [XZ_Plane010]
  FullyConstrained = true
  MakeInternals = false
  MapMode = 5
  Placement = pos=(0,0,0) rot=(1,0,0;1.5708rad)
  expr: Constraints[10] = <<bdim>>.sp_h
  expr: Constraints[9] = <<bdim>>.sp_w
  sketch-geometry (4):
    g0: LineSegment StartX=0 StartY=0 StartZ=0 EndX=674 EndY=0 EndZ=0
    g1: LineSegment StartX=674 StartY=0 StartZ=0 EndX=674 EndY=320 EndZ=0
    g2: LineSegment StartX=674 StartY=320 StartZ=0 EndX=0 EndY=320 EndZ=0
    g3: LineSegment StartX=0 StartY=320 StartZ=0 EndX=0 EndY=0 EndZ=0
  constraints (11):
    c: Coincident(g0,g1)
    c: Coincident(g1,g2)
    c: Coincident(g2,g3)
    c: Coincident(g3,g0)
    c: Horizontal(g0)
    c: Horizontal(g2)
    c: Vertical(g1)
    c: Vertical(g3)
    c: Coincident(g0,g-1)
    c: DistanceY(g3,g3) = 320
    c: DistanceX(g0,g0) = 674
FEATURE [PartDesign::Pad] Pad008
  Direction = (0,-1,2e-16)
  Length = 13
  Length2 = 10
  Placement = pos=(0,0,0) rot=(1,0,0;1.5708rad)
  Profile = -> Sketch020
  ReferenceAxis = -> Sketch020 [N_Axis]
  Suppressed = false
  Type = 0
  expr: Length = <<bdim>>.sp_thick
FEATURE [PartDesign::Body] Body009  label="side_panel_001"
  AllowCompound = false
  Group = -> [Sketch020,Pad008]
  Origin = -> Origin010
  Tip = -> Pad008
FEATURE [Sketcher::SketchObject] Sketch021
  ArcFitTolerance = 1e-06
  AttachmentSupport = -> [XZ_Plane011]
  FullyConstrained = true
  MakeInternals = false
  MapMode = 5
  Placement = pos=(0,0,0) rot=(1,0,0;1.5708rad)
  expr: Constraints[10] = <<bdim>>.spb_h
  expr: Constraints[9] = <<bdim>>.spb_w
  sketch-geometry (4):
    g0: LineSegment StartX=0 StartY=0 StartZ=0 EndX=674 EndY=0 EndZ=0
    g1: LineSegment StartX=674 StartY=0 StartZ=0 EndX=674 EndY=30 EndZ=0
    g2: LineSegment StartX=674 StartY=30 StartZ=0 EndX=0 EndY=30 EndZ=0
    g3: LineSegment StartX=0 StartY=30 StartZ=0 EndX=0 EndY=0 EndZ=0
  constraints (11):
    c: Coincident(g0,g1)
    c: Coincident(g1,g2)
    c: Coincident(g2,g3)
    c: Coincident(g3,g0)
    c: Horizontal(g0)
    c: Horizontal(g2)
    c: Vertical(g1)
    c: Vertical(g3)
    c: Coincident(g0,g-1)
    c: DistanceX(g2,g2) = 674
    c: DistanceY(g3,g3) = 30
FEATURE [PartDesign::Pad] Pad009
  Direction = (0,-1,2e-16)
  Length = 30
  Length2 = 10
  Placement = pos=(0,0,0) rot=(1,0,0;1.5708rad)
  Profile = -> Sketch021
  ReferenceAxis = -> Sketch021 [N_Axis]
  Suppressed = false
  Type = 0
  expr: Length = <<bdim>>.spb_h
FEATURE [PartDesign::Body] Body010  label="side_panel_001_bar_001"
  AllowCompound = false
  Group = -> [Sketch021,Pad009]
  Origin = -> Origin011
  Tip = -> Pad009
FEATURE [Sketcher::SketchObject] Sketch022
  ArcFitTolerance = 1e-06
  AttachmentSupport = -> [XZ_Plane012]
  FullyConstrained = true
  MakeInternals = false
  MapMode = 5
  Placement = pos=(0,0,0) rot=(1,0,0;1.5708rad)
  expr: Constraints[10] = <<bdim>>.spb_h
  expr: Constraints[9] = <<bdim>>.spb_w
  sketch-geometry (4):
    g0: LineSegment StartX=0 StartY=0 StartZ=0 EndX=674 EndY=0 EndZ=0
    g1: LineSegment StartX=674 StartY=0 StartZ=0 EndX=674 EndY=30 EndZ=0
    g2: LineSegment StartX=674 StartY=30 StartZ=0 EndX=0 EndY=30 EndZ=0
    g3: LineSegment StartX=0 StartY=30 StartZ=0 EndX=0 EndY=0 EndZ=0
  constraints (11):
    c: Coincident(g0,g1)
    c: Coincident(g1,g2)
    c: Coincident(g2,g3)
    c: Coincident(g3,g0)
    c: Horizontal(g0)
    c: Horizontal(g2)
    c: Vertical(g1)
    c: Vertical(g3)
    c: Coincident(g0,g-1)
    c: DistanceX(g2,g2) = 674
    c: DistanceY(g3,g3) = 30
FEATURE [PartDesign::Pad] Pad010
  Direction = (0,-1,2e-16)
  Length = 30
  Length2 = 10
  Placement = pos=(0,0,0) rot=(1,0,0;1.5708rad)
  Profile = -> Sketch022
  ReferenceAxis = -> Sketch022 [N_Axis]
  Suppressed = false
  Type = 0
  expr: Length = <<bdim>>.spb_h
FEATURE [PartDesign::Body] Body011  label="side_panel_001_bar_002"
  AllowCompound = false
  Group = -> [Sketch022,Pad010]
  Origin = -> Origin012
  Tip = -> Pad010
FEATURE [Sketcher::SketchObject] Sketch023
  ArcFitTolerance = 1e-06
  AttachmentSupport = -> [XZ_Plane013]
  FullyConstrained = true
  MakeInternals = false
  MapMode = 5
  Placement = pos=(0,0,0) rot=(1,0,0;1.5708rad)
  expr: Constraints[10] = <<bdim>>.spbb_w
  expr: Constraints[9] = <<bdim>>.spbb_h
  sketch-geometry (4):
    g0: LineSegment StartX=0 StartY=0 StartZ=0 EndX=30 EndY=0 EndZ=0
    g1: LineSegment StartX=30 StartY=0 StartZ=0 EndX=30 EndY=260 EndZ=0
    g2: LineSegment StartX=30 StartY=260 StartZ=0 EndX=0 EndY=260 EndZ=0
    g3: LineSegment StartX=0 StartY=260 StartZ=0 EndX=0 EndY=0 EndZ=0
  constraints (11):
    c: Coincident(g0,g1)
    c: Coincident(g1,g2)
    c: Coincident(g2,g3)
    c: Coincident(g3,g0)
    c: Horizontal(g0)
    c: Horizontal(g2)
    c: Vertical(g1)
    c: Vertical(g3)
    c: Coincident(g0,g-1)
    c: DistanceX(g2,g2) = 30
    c: DistanceY(g3,g3) = 260
FEATURE [Sketcher::SketchObject] Sketch024
  ArcFitTolerance = 1e-06
  AttachmentSupport = -> [XZ_Plane014]
  FullyConstrained = true
  MakeInternals = false
  MapMode = 5
  Placement = pos=(0,0,0) rot=(1,0,0;1.5708rad)
  expr: Constraints[10] = <<bdim>>.spbb_w
  expr: Constraints[9] = <<bdim>>.spbb_h
  sketch-geometry (4):
    g0: LineSegment StartX=0 StartY=0 StartZ=0 EndX=30 EndY=0 EndZ=0
    g1: LineSegment StartX=30 StartY=0 StartZ=0 EndX=30 EndY=260 EndZ=0
    g2: LineSegment StartX=30 StartY=260 StartZ=0 EndX=0 EndY=260 EndZ=0
    g3: LineSegment StartX=0 StartY=260 StartZ=0 EndX=0 EndY=0 EndZ=0
  constraints (11):
    c: Coincident(g0,g1)
    c: Coincident(g1,g2)
    c: Coincident(g2,g3)
    c: Coincident(g3,g0)
    c: Horizontal(g0)
    c: Horizontal(g2)
    c: Vertical(g1)
    c: Vertical(g3)
    c: Coincident(g0,g-1)
    c: DistanceX(g2,g2) = 30
    c: DistanceY(g3,g3) = 260
FEATURE [PartDesign::Pad] Pad012
  Direction = (0,-1,2e-16)
  Length = 30
  Length2 = 10
  Placement = pos=(0,0,0) rot=(1,0,0;1.5708rad)
  Profile = -> Sketch024
  ReferenceAxis = -> Sketch024 [N_Axis]
  Suppressed = false
  Type = 0
  expr: Length = <<bdim>>.spb_h
FEATURE [PartDesign::Body] Body013  label="side_panel_001_bar_004"
  AllowCompound = false
  Group = -> [Sketch024,Pad012]
  Origin = -> Origin014
  Tip = -> Pad012
FEATURE [Sketcher::SketchObject] Sketch025
  ArcFitTolerance = 1e-06
  AttachmentSupport = -> [XZ_Plane015]
  FullyConstrained = true
  MakeInternals = false
  MapMode = 5
  Placement = pos=(0,0,0) rot=(1,0,0;1.5708rad)
  expr: Constraints[10] = <<bdim>>.sp2_h
  expr: Constraints[9] = <<bdim>>.sp2_w
  sketch-geometry (4):
    g0: LineSegment StartX=0 StartY=0 StartZ=0 EndX=687 EndY=0 EndZ=0
    g1: LineSegment StartX=687 StartY=0 StartZ=0 EndX=687 EndY=320 EndZ=0
    g2: LineSegment StartX=687 StartY=320 StartZ=0 EndX=0 EndY=320 EndZ=0
    g3: LineSegment StartX=0 StartY=320 StartZ=0 EndX=0 EndY=0 EndZ=0
  constraints (11):
    c: Coincident(g0,g1)
    c: Coincident(g1,g2)
    c: Coincident(g2,g3)
    c: Coincident(g3,g0)
    c: Horizontal(g0)
    c: Horizontal(g2)
    c: Vertical(g1)
    c: Vertical(g3)
    c: Coincident(g0,g-1)
    c: DistanceY(g3,g3) = 320
    c: DistanceX(g0,g0) = 687
FEATURE [PartDesign::Pad] Pad013
  Direction = (0,-1,2e-16)
  Length = 13
  Length2 = 10
  Placement = pos=(0,0,0) rot=(1,0,0;1.5708rad)
  Profile = -> Sketch025
  ReferenceAxis = -> Sketch025 [N_Axis]
  Suppressed = false
  Type = 0
  expr: Length = <<bdim>>.sp_thick
FEATURE [PartDesign::Body] Body014  label="side_panel_002"
  AllowCompound = false
  Group = -> [Sketch025,Pad013]
  Origin = -> Origin015
  Tip = -> Pad013
FEATURE [Sketcher::SketchObject] Sketch026
  ArcFitTolerance = 1e-06
  AttachmentSupport = -> [XZ_Plane016]
  FullyConstrained = true
  MakeInternals = false
  MapMode = 5
  Placement = pos=(0,0,0) rot=(1,0,0;1.5708rad)
  expr: Constraints[10] = <<bdim>>.sp2b1_h
  expr: Constraints[9] = <<bdim>>.sp2b1_w
  sketch-geometry (4):
    g0: LineSegment StartX=0 StartY=0 StartZ=0 EndX=687 EndY=0 EndZ=0
    g1: LineSegment StartX=687 StartY=0 StartZ=0 EndX=687 EndY=30 EndZ=0
    g2: LineSegment StartX=687 StartY=30 StartZ=0 EndX=0 EndY=30 EndZ=0
    g3: LineSegment StartX=0 StartY=30 StartZ=0 EndX=0 EndY=0 EndZ=0
  constraints (11):
    c: Coincident(g0,g1)
    c: Coincident(g1,g2)
    c: Coincident(g2,g3)
    c: Coincident(g3,g0)
    c: Horizontal(g0)
    c: Horizontal(g2)
    c: Vertical(g1)
    c: Vertical(g3)
    c: Coincident(g0,g-1)
    c: DistanceX(g2,g2) = 687
    c: DistanceY(g3,g3) = 30
FEATURE [PartDesign::Pad] Pad014
  Direction = (0,-1,2e-16)
  Length = 30
  Length2 = 10
  Placement = pos=(0,0,0) rot=(1,0,0;1.5708rad)
  Profile = -> Sketch026
  ReferenceAxis = -> Sketch026 [N_Axis]
  Suppressed = false
  Type = 0
  expr: Length = <<bdim>>.spb_h
FEATURE [PartDesign::Body] Body015  label="side_panel_002_bar_001"
  AllowCompound = false
  Group = -> [Sketch026,Pad014]
  Origin = -> Origin016
  Tip = -> Pad014
FEATURE [Sketcher::SketchObject] Sketch027
  ArcFitTolerance = 1e-06
  AttachmentSupport = -> [XZ_Plane017]
  FullyConstrained = true
  MakeInternals = false
  MapMode = 5
  Placement = pos=(0,0,0) rot=(1,0,0;1.5708rad)
  expr: Constraints[10] = <<bdim>>.sp2b1_h
  expr: Constraints[9] = <<bdim>>.sp2b1_w
  sketch-geometry (4):
    g0: LineSegment StartX=0 StartY=0 StartZ=0 EndX=687 EndY=0 EndZ=0
    g1: LineSegment StartX=687 StartY=0 StartZ=0 EndX=687 EndY=30 EndZ=0
    g2: LineSegment StartX=687 StartY=30 StartZ=0 EndX=0 EndY=30 EndZ=0
    g3: LineSegment StartX=0 StartY=30 StartZ=0 EndX=0 EndY=0 EndZ=0
  constraints (11):
    c: Coincident(g0,g1)
    c: Coincident(g1,g2)
    c: Coincident(g2,g3)
    c: Coincident(g3,g0)
    c: Horizontal(g0)
    c: Horizontal(g2)
    c: Vertical(g1)
    c: Vertical(g3)
    c: Coincident(g0,g-1)
    c: DistanceX(g2,g2) = 687
    c: DistanceY(g3,g3) = 30
FEATURE [PartDesign::Pad] Pad015
  Direction = (0,-1,2e-16)
  Length = 30
  Length2 = 10
  Placement = pos=(0,0,0) rot=(1,0,0;1.5708rad)
  Profile = -> Sketch027
  ReferenceAxis = -> Sketch027 [N_Axis]
  Suppressed = false
  Type = 0
  expr: Length = <<bdim>>.spb_h
FEATURE [PartDesign::Body] Body016  label="side_panel_002_bar_002"
  AllowCompound = false
  Group = -> [Sketch027,Pad015]
  Origin = -> Origin017
  Tip = -> Pad015
FEATURE [Sketcher::SketchObject] Sketch028
  ArcFitTolerance = 1e-06
  AttachmentSupport = -> [XZ_Plane018]
  FullyConstrained = true
  MakeInternals = false
  MapMode = 5
  Placement = pos=(0,0,0) rot=(1,0,0;1.5708rad)
  expr: Constraints[10] = <<bdim>>.sp2b2_w
  expr: Constraints[9] = <<bdim>>.sp2b2_h
  sketch-geometry (4):
    g0: LineSegment StartX=0 StartY=0 StartZ=0 EndX=30 EndY=0 EndZ=0
    g1: LineSegment StartX=30 StartY=0 StartZ=0 EndX=30 EndY=260 EndZ=0
    g2: LineSegment StartX=30 StartY=260 StartZ=0 EndX=0 EndY=260 EndZ=0
    g3: LineSegment StartX=0 StartY=260 StartZ=0 EndX=0 EndY=0 EndZ=0
  constraints (11):
    c: Coincident(g0,g1)
    c: Coincident(g1,g2)
    c: Coincident(g2,g3)
    c: Coincident(g3,g0)
    c: Horizontal(g0)
    c: Horizontal(g2)
    c: Vertical(g1)
    c: Vertical(g3)
    c: Coincident(g0,g-1)
    c: DistanceX(g2,g2) = 30
    c: DistanceY(g3,g3) = 260
FEATURE [PartDesign::Pad] Pad016
  Direction = (0,-1,2e-16)
  Length = 30
  Length2 = 10
  Placement = pos=(0,0,0) rot=(1,0,0;1.5708rad)
  Profile = -> Sketch028
  ReferenceAxis = -> Sketch028 [N_Axis]
  Suppressed = false
  Type = 0
  expr: Length = <<bdim>>.spb_h
FEATURE [PartDesign::Body] Body017  label="side_panel_002_bar_003"
  AllowCompound = false
  Group = -> [Sketch028,Pad016]
  Origin = -> Origin018
  Tip = -> Pad016
FEATURE [Sketcher::SketchObject] Sketch029
  ArcFitTolerance = 1e-06
  AttachmentSupport = -> [XZ_Plane019]
  FullyConstrained = true
  MakeInternals = false
  MapMode = 5
  Placement = pos=(0,0,0) rot=(1,0,0;1.5708rad)
  expr: Constraints[10] = <<bdim>>.sp2b2_w
  expr: Constraints[9] = <<bdim>>.sp2b2_h
  sketch-geometry (4):
    g0: LineSegment StartX=0 StartY=0 StartZ=0 EndX=30 EndY=0 EndZ=0
    g1: LineSegment StartX=30 StartY=0 StartZ=0 EndX=30 EndY=260 EndZ=0
    g2: LineSegment StartX=30 StartY=260 StartZ=0 EndX=0 EndY=260 EndZ=0
    g3: LineSegment StartX=0 StartY=260 StartZ=0 EndX=0 EndY=0 EndZ=0
  constraints (11):
    c: Coincident(g0,g1)
    c: Coincident(g1,g2)
    c: Coincident(g2,g3)
    c: Coincident(g3,g0)
    c: Horizontal(g0)
    c: Horizontal(g2)
    c: Vertical(g1)
    c: Vertical(g3)
    c: Coincident(g0,g-1)
    c: DistanceX(g2,g2) = 30
    c: DistanceY(g3,g3) = 260
FEATURE [PartDesign::Pad] Pad017
  Direction = (0,-1,2e-16)
  Length = 30
  Length2 = 10
  Placement = pos=(0,0,0) rot=(1,0,0;1.5708rad)
  Profile = -> Sketch029
  ReferenceAxis = -> Sketch029 [N_Axis]
  Suppressed = false
  Type = 0
  expr: Length = <<bdim>>.spb_h
FEATURE [PartDesign::Body] Body018  label="side_panel_002_bar_004"
  AllowCompound = false
  Group = -> [Sketch029,Pad017]
  Origin = -> Origin019
  Tip = -> Pad017
FEATURE [App::Link] bottom_panel  label="bottom_panel001"
  LinkedObject = -> Body006
FEATURE [App::FeaturePython] GroundedJoint  # Assembly grounded joint (typed FeaturePython)
  ObjectToGround = -> bottom_panel
FEATURE [App::Link] back_panel  label="back_panel001"
  LinkPlacement = pos=(13,-6e-15,13) rot=(0,1,0;1.5708rad)
  LinkedObject = -> Body003
  Placement = pos=(13,-6e-15,13) rot=(0,1,0;1.5708rad)
FEATURE [App::FeaturePython] Joint  label="back_panel_to_bottom"  # Assembly joint (typed FeaturePython)
  Activated = true
  AngleMax = 0
  AngleMin = 0
  Detach1 = false
  Detach2 = false
  Distance = 0
  Distance2 = 0
  EnableAngleMax = false
  EnableAngleMin = false
  EnableLengthMax = false
  EnableLengthMin = false
  JointType = 0 (Fixed)
  LengthMax = 0
  LengthMin = 0
  Offset1 = pos=(0,0,0) rot=(0,0,1;1.5708rad)
  Placement1 = pos=(13,317.5,-1.043e-13) rot=(1,0,0;4.71239rad)
  Placement2 = pos=(13,317.5,-1.048e-13) rot=(0.57735,0.57735,0.57735;4.18879rad)
  Reference1 = -> Assembly [bottom_panel.Edge4,bottom_panel.Edge4]
  Reference2 = -> Assembly [back_panel.Edge4,back_panel.Edge4]
FEATURE [App::Link] top_panel  label="top_panel001"
  LinkPlacement = pos=(333,-1.39e-14,2.7e-13) rot=(0,0,1;0rad)
  LinkedObject = -> Body007
  Placement = pos=(333,-1.39e-14,2.7e-13) rot=(0,0,1;0rad)
FEATURE [App::FeaturePython] Joint003  label="Fixed002"  # Assembly joint (typed FeaturePython)
  Activated = true
  AngleMax = 0
  AngleMin = 0
  Detach1 = false
  Detach2 = false
  Distance = 0
  Distance2 = 0
  EnableAngleMax = false
  EnableAngleMin = false
  EnableLengthMax = false
  EnableLengthMin = false
  JointType = 0 (Fixed)
  LengthMax = 0
  LengthMin = 0
  Offset2 = pos=(0,0,0) rot=(0,0,-1;1.5708rad)
  Placement1 = pos=(13,317.5,320) rot=(-0.57735,-0.57735,0.57735;4.18879rad)
  Placement2 = pos=(0,317.5,-1.057e-13) rot=(0,0.707107,0.707107;3.14159rad)
  Reference1 = -> Assembly [back_panel.Edge10,back_panel.Edge10]
  Reference2 = -> Assembly [top_panel.Edge3,top_panel.Edge3]
FEATURE [App::Link] side_panel_001  label="side_panel_1"
  LinkPlacement = pos=(13,635,687) rot=(0,1,0;1.5708rad)
  LinkedObject = -> Body009
  Placement = pos=(13,635,687) rot=(0,1,0;1.5708rad)
FEATURE [App::FeaturePython] Joint004  label="Fixed003"  # Assembly joint (typed FeaturePython)
  Activated = true
  AngleMax = 0
  AngleMin = 0
  Detach1 = false
  Detach2 = false
  Distance = 0
  Distance2 = 0
  EnableAngleMax = false
  EnableAngleMin = false
  EnableLengthMax = false
  EnableLengthMin = false
  JointType = 0 (Fixed)
  LengthMax = 0
  LengthMin = 0
  Offset2 = pos=(0,0,0) rot=(0,0,1;3.14159rad)
  Placement1 = pos=(337,1.137e-13,320) rot=(-0.707107,0,0.707107;3.14159rad)
  Placement2 = pos=(-1.137e-13,635,350) rot=(0,0,1;3.14159rad)
  Reference1 = -> Assembly [side_panel_001.Edge9,side_panel_001.Edge9]
  Reference2 = -> Assembly [top_panel.Edge6,top_panel.Edge6]
FEATURE [App::Link] side_panel_001_bar_001  label="side_panel_1_bar_a"
  LinkPlacement = pos=(13,592,687) rot=(-0.57735,0.57735,0.57735;2.0944rad)
  LinkedObject = -> Body010
  Placement = pos=(13,592,687) rot=(-0.57735,0.57735,0.57735;2.0944rad)
FEATURE [App::Link] side_panel_001_bar_002  label="side_panel_1_bar_b"
  LinkPlacement = pos=(303,622,687) rot=(0,1,0;1.5708rad)
  LinkedObject = -> Body011
  Placement = pos=(303,622,687) rot=(0,1,0;1.5708rad)
FEATURE [App::Link] side_panel_001_bar_003  label="side_panel_1_bar_c"
  LinkPlacement = pos=(43,622,43) rot=(0,1,0;1.5708rad)
  LinkedObject = -> Body012
  Placement = pos=(43,622,43) rot=(0,1,0;1.5708rad)
FEATURE [App::Link] side_panel_001_bar_004  label="side_panel_1_bar_d"
  LinkPlacement = pos=(43,592,687) rot=(0.57735,0.57735,0.57735;2.0944rad)
  LinkedObject = -> Body013
  Placement = pos=(43,592,687) rot=(0.57735,0.57735,0.57735;2.0944rad)
FEATURE [App::FeaturePython] Joint005  label="Fixed"  # Assembly joint (typed FeaturePython)
  Activated = true
  AngleMax = 0
  AngleMin = 0
  Detach1 = false
  Detach2 = false
  Distance = 0
  Distance2 = 0
  EnableAngleMax = false
  EnableAngleMin = false
  EnableLengthMax = false
  EnableLengthMin = false
  JointType = 0 (Fixed)
  LengthMax = 0
  LengthMin = 0
  Placement1 = pos=(337,0,30) rot=(-0.707107,0,0.707107;3.14159rad)
  Placement2 = pos=(337,-13,320) rot=(-0.707107,0,0.707107;3.14159rad)
  Reference1 = -> Assembly [side_panel_001_bar_002.Edge9,side_panel_001_bar_002.Edge9]
  Reference2 = -> Assembly [side_panel_001.Edge10,side_panel_001.Edge10]
FEATURE [App::FeaturePython] Joint006  label="Fixed004"  # Assembly joint (typed FeaturePython)
  Activated = true
  AngleMax = 0
  AngleMin = 0
  Detach1 = false
  Detach2 = false
  Distance = 0
  Distance2 = 0
  EnableAngleMax = false
  EnableAngleMin = false
  EnableLengthMax = false
  EnableLengthMin = false
  JointType = 0 (Fixed)
  LengthMax = 0
  LengthMin = 0
  Offset2 = pos=(0,0,0) rot=(0,0,1;1.5708rad)
  Placement1 = pos=(30,0,130) rot=(0,0,1;0rad)
  Placement2 = pos=(0,-13,160) rot=(0.707107,0.707107,0;3.14159rad)
  Reference1 = -> Assembly [side_panel_001_bar_004.Edge6,side_panel_001_bar_004.Edge6]
  Reference2 = -> Assembly [side_panel_001.Edge12,side_panel_001.Edge12]
FEATURE [App::FeaturePython] Joint007  label="Fixed005"  # Assembly joint (typed FeaturePython)
  Activated = true
  AngleMax = 0
  AngleMin = 0
  Detach1 = false
  Detach2 = false
  Distance = 0
  Distance2 = 0
  EnableAngleMax = false
  EnableAngleMin = false
  EnableLengthMax = false
  EnableLengthMin = false
  JointType = 0 (Fixed)
  LengthMax = 0
  LengthMin = 0
  Offset2 = pos=(0,0,0) rot=(0,0,1;1.5708rad)
  Placement1 = pos=(337,-13,1.8e-15) rot=(0.707107,0,0.707107;3.14159rad)
  Placement2 = pos=(337,-1.24e-14,30) rot=(-0.57735,0.57735,0.57735;4.18879rad)
  Reference1 = -> Assembly [side_panel_001.Edge4,side_panel_001.Edge4]
  Reference2 = -> Assembly [side_panel_001_bar_001.Edge9,side_panel_001_bar_001.Edge9]
FEATURE [App::FeaturePython] Joint008  label="Fixed006"  # Assembly joint (typed FeaturePython)
  Activated = true
  AngleMax = 0
  AngleMin = 0
  Detach1 = false
  Detach2 = false
  Distance = 0
  Distance2 = 0
  EnableAngleMax = false
  EnableAngleMin = false
  EnableLengthMax = false
  EnableLengthMin = false
  JointType = 0 (Fixed)
  LengthMax = 0
  LengthMin = 0
  Placement1 = pos=(674,-13,160) rot=(0,0,1;0rad)
  Placement2 = pos=(30,1.137e-13,130) rot=(0,0,1;0rad)
  Reference1 = -> Assembly [side_panel_001.Edge7,side_panel_001.Edge7]
  Reference2 = -> Assembly [side_panel_001_bar_003.Edge6,side_panel_001_bar_003.Edge6]
FEATURE [App::Link] side_panel_002_bar_001  label="side_panel_2_bar_a"
  LinkPlacement = pos=(303,43,13) rot=(0.57735,-0.57735,0.57735;2.0944rad)
  LinkedObject = -> Body015
  Placement = pos=(303,43,13) rot=(0.57735,-0.57735,0.57735;2.0944rad)
FEATURE [App::Link] side_panel_002_bar_004  label="side_panel_2_bar_c"
  LinkPlacement = pos=(303,13,43) rot=(-0.707107,0,0.707107;3.14159rad)
  LinkedObject = -> Body018
  Placement = pos=(303,13,43) rot=(-0.707107,0,0.707107;3.14159rad)
FEATURE [App::Link] side_panel_002_bar_002  label="side_panel_2_bar_b"
  LinkPlacement = pos=(43,43,700) rot=(-0.57735,-0.57735,0.57735;4.18879rad)
  LinkedObject = -> Body016
  Placement = pos=(43,43,700) rot=(-0.57735,-0.57735,0.57735;4.18879rad)
FEATURE [App::Link] side_panel_002  label="side_panel_2"
  LinkPlacement = pos=(333,13,13) rot=(0,-1,0;1.5708rad)
  LinkedObject = -> Body014
  Placement = pos=(333,13,13) rot=(0,-1,0;1.5708rad)
FEATURE [App::FeaturePython] Joint009  label="Fixed007"  # Assembly joint (typed FeaturePython)
  Activated = true
  AngleMax = 0
  AngleMin = 0
  Detach1 = false
  Detach2 = false
  Distance = 0
  Distance2 = 0
  EnableAngleMax = false
  EnableAngleMin = false
  EnableLengthMax = false
  EnableLengthMin = false
  JointType = 0 (Fixed)
  LengthMax = 0
  LengthMin = 0
  Offset2 = pos=(0,0,-6.5) rot=(0,0,1;3.14159rad)
  Placement1 = pos=(343.5,-13,320) rot=(-0.707107,0,0.707107;3.14159rad)
  Placement2 = pos=(13,3.6e-14,356.5) rot=(1,0,0;3.14159rad)
  Reference1 = -> Assembly [side_panel_002.Edge10,side_panel_002.Edge10]
  Reference2 = -> Assembly [bottom_panel.Edge12,bottom_panel.Edge12]
  expr: .Offset2.Base.z = -<<bdim>>.bp_t / 2
FEATURE [App::FeaturePython] Joint010  label="Fixed008"  # Assembly joint (typed FeaturePython)
  Activated = true
  AngleMax = 0
  AngleMin = 0
  Detach1 = false
  Detach2 = false
  Distance = 0
  Distance2 = 0
  EnableAngleMax = false
  EnableAngleMin = false
  EnableLengthMax = false
  EnableLengthMin = false
  JointType = 0 (Fixed)
  LengthMax = 0
  LengthMin = 0
  Offset2 = pos=(0,0,0) rot=(0,0,-1;1.5708rad)
  Placement1 = pos=(343.5,-30,30) rot=(-0.707107,0,0.707107;3.14159rad)
  Placement2 = pos=(343.5,7.11e-14,320) rot=(-0.57735,-0.57735,0.57735;2.0944rad)
  Reference1 = -> Assembly [side_panel_002_bar_002.Edge10,side_panel_002_bar_002.Edge10]
  Reference2 = -> Assembly [side_panel_002.Edge9,side_panel_002.Edge9]
FEATURE [App::FeaturePython] Joint011  label="Fixed009"  # Assembly joint (typed FeaturePython)
  Activated = true
  AngleMax = 0
  AngleMin = 0
  Detach1 = false
  Detach2 = false
  Distance = 0
  Distance2 = 0
  EnableAngleMax = false
  EnableAngleMin = false
  EnableLengthMax = false
  EnableLengthMin = false
  JointType = 0 (Fixed)
  LengthMax = 0
  LengthMin = 0
  Offset2 = pos=(0,0,0) rot=(0,0,-1;1.5708rad)
  Placement1 = pos=(343.5,0,0) rot=(0.707107,0,0.707107;3.14159rad)
  Placement2 = pos=(343.5,-30,30) rot=(-0.57735,-0.57735,0.57735;2.0944rad)
  Reference1 = -> Assembly [side_panel_002.Edge3,side_panel_002.Edge3]
  Reference2 = -> Assembly [side_panel_002_bar_001.Edge10,side_panel_002_bar_001.Edge10]
FEATURE [App::FeaturePython] Joint013  label="Fixed011"  # Assembly joint (typed FeaturePython)
  Activated = true
  AngleMax = 0
  AngleMin = 0
  Detach1 = false
  Detach2 = false
  Distance = 0
  Distance2 = 0
  EnableAngleMax = false
  EnableAngleMin = false
  EnableLengthMax = false
  EnableLengthMin = false
  JointType = 0 (Fixed)
  LengthMax = 0
  LengthMin = 0
  Placement1 = pos=(0,3.55e-14,160) rot=(0,1,0;3.14159rad)
  Placement2 = pos=(30,2.84e-14,130) rot=(0,0,1;0rad)
  Reference1 = -> Assembly [side_panel_002.Edge11,side_panel_002.Edge11]
  Reference2 = -> Assembly [side_panel_002_bar_004.Edge6,side_panel_002_bar_004.Edge6]
FEATURE [Sketcher::SketchObject] Sketch030
  ArcFitTolerance = 1e-06
  AttachmentSupport = -> [XZ_Plane020]
  FullyConstrained = true
  MakeInternals = false
  MapMode = 5
  Placement = pos=(0,0,0) rot=(1,0,0;1.5708rad)
  expr: Constraints[10] = <<bdim>>.f1_h
  expr: Constraints[9] = <<bdim>>.f1_w
  sketch-geometry (4):
    g0: LineSegment StartX=0 StartY=0 StartZ=0 EndX=320 EndY=0 EndZ=0
    g1: LineSegment StartX=320 StartY=0 StartZ=0 EndX=320 EndY=479.669 EndZ=0
    g2: LineSegment StartX=320 StartY=479.669 StartZ=0 EndX=0 EndY=479.669 EndZ=0
    g3: LineSegment StartX=0 StartY=479.669 StartZ=0 EndX=0 EndY=0 EndZ=0
  constraints (11):
    c: Coincident(g0,g1)
    c: Coincident(g1,g2)
    c: Coincident(g2,g3)
    c: Coincident(g3,g0)
    c: Horizontal(g0)
    c: Horizontal(g2)
    c: Vertical(g1)
    c: Vertical(g3)
    c: Coincident(g0,g-1)
    c: DistanceY(g1,g1) = 479.669
    c: DistanceX(g0,g0) = 320
FEATURE [Sketcher::SketchObject] Sketch031
  ArcFitTolerance = 1e-06
  AttachmentSupport = -> [XZ_Plane021]
  FullyConstrained = true
  MakeInternals = false
  MapMode = 5
  Placement = pos=(0,0,0) rot=(1,0,0;1.5708rad)
  expr: Constraints[10] = <<bdim>>.f2_h
  expr: Constraints[9] = <<bdim>>.f2_w
  sketch-geometry (4):
    g0: LineSegment StartX=0 StartY=0 StartZ=0 EndX=320 EndY=0 EndZ=0
    g1: LineSegment StartX=320 StartY=0 StartZ=0 EndX=320 EndY=492.669 EndZ=0
    g2: LineSegment StartX=320 StartY=492.669 StartZ=0 EndX=0 EndY=492.669 EndZ=0
    g3: LineSegment StartX=0 StartY=492.669 StartZ=0 EndX=0 EndY=0 EndZ=0
  constraints (11):
    c: Coincident(g0,g1)
    c: Coincident(g1,g2)
    c: Coincident(g2,g3)
    c: Coincident(g3,g0)
    c: Horizontal(g0)
    c: Horizontal(g2)
    c: Vertical(g1)
    c: Vertical(g3)
    c: Coincident(g0,g-1)
    c: DistanceY(g1,g1) = 492.669
    c: DistanceX(g0,g0) = 320
FEATURE [PartDesign::Pad] Pad019
  Direction = (0,-1,2e-16)
  Length = 13
  Length2 = 10
  Placement = pos=(0,0,0) rot=(1,0,0;1.5708rad)
  Profile = -> Sketch031
  ReferenceAxis = -> Sketch031 [N_Axis]
  Suppressed = false
  Type = 0
  expr: Length = <<bdim>>.f2_t
FEATURE [PartDesign::Body] Body020  label="fin_2_model"
  AllowCompound = false
  Group = -> [Sketch031,Pad019]
  Origin = -> Origin021
  Tip = -> Pad019
FEATURE [Sketcher::SketchObject] Sketch032
  ArcFitTolerance = 1e-06
  AttachmentSupport = -> [XY_Plane022]
  FullyConstrained = true
  MakeInternals = false
  MapMode = 5
  expr: Constraints[10] = <<bdim>>.fp_w
  expr: Constraints[18] = <<bdim>>.baffle_diameter
  expr: Constraints[19] = <<dims>>.width1 + <<bdim>>.sp_thick * 0.5 + <<dims>>.driver_offset
  expr: Constraints[9] = <<bdim>>.fp_h
  sketch-geometry (7):
    g0: LineSegment StartX=0 StartY=0 StartZ=0 EndX=320 EndY=0 EndZ=0
    g1: LineSegment StartX=320 StartY=0 StartZ=0 EndX=320 EndY=414.663 EndZ=0
    g2: LineSegment StartX=320 StartY=414.663 StartZ=0 EndX=0 EndY=414.663 EndZ=0
    g3: LineSegment StartX=0 StartY=414.663 StartZ=0 EndX=0 EndY=0 EndZ=0
    g4: Circle CenterX=160 CenterY=220.831 CenterZ=0 NormalX=0 NormalY=0 NormalZ=1 AngleXU=0 Radius=140.6
    g5: LineSegment [constr] StartX=0 StartY=220.831 StartZ=0 EndX=160 EndY=220.831 EndZ=0
    g6: LineSegment [constr] StartX=160 StartY=220.831 StartZ=0 EndX=320 EndY=220.831 EndZ=0
  constraints (20):
    c: Coincident(g0,g1)
    c: Coincident(g1,g2)
    c: Coincident(g2,g3)
    c: Coincident(g3,g0)
    c: Horizontal(g0)
    c: Horizontal(g2)
    c: Vertical(g1)
    c: Vertical(g3)
    c: Coincident(g0,g-1)
    c: DistanceX(g2,g2) = 320
    c: DistanceY(g3,g3) = 414.663
    c: PointOnObject(g5,g3)
    c: Coincident(g5,g4)
    c: Horizontal(g5)
    c: Coincident(g6,g4)
    c: PointOnObject(g6,g1)
    c: Parallel(g6,g5)
    c: Equal(g5,g6)
    c: Diameter(g4) = 281.2
    c: DistanceY(g0,g5) = 220.831
FEATURE [Sketcher::SketchObject] Sketch033
  ArcFitTolerance = 1e-06
  AttachmentSupport = -> [XY_Plane023]
  FullyConstrained = true
  MakeInternals = false
  MapMode = 5
  expr: Constraints[13] = <<bdim>>.fpb_h
  expr: Constraints[15] = (<<bdim>>.baffle_diameter + <<bdim>>.dr_tdiam) / 4
  expr: Constraints[16] = <<bdim>>.fp_h / 2
  expr: Constraints[17] = <<dims>>.width1 + <<bdim>>.sp_thick * 0.5 + <<dims>>.driver_offset - <<bdim>>.bar_side_size - <<bdim>>.sp_thick
  expr: Constraints[6] = <<bdim>>.fpb_t
  sketch-geometry (6):
    g0: LineSegment StartX=0 StartY=0 StartZ=0 EndX=30 EndY=0 EndZ=0
    g1: LineSegment StartX=30 StartY=371.663 StartZ=0 EndX=0 EndY=371.663 EndZ=0
    g2: LineSegment StartX=0 StartY=371.663 StartZ=0 EndX=0 EndY=0 EndZ=0
    g3: LineSegment StartX=30 StartY=371.663 StartZ=0 EndX=30 EndY=261.809 EndZ=0
    g4: LineSegment StartX=30 StartY=0 StartZ=0 EndX=30 EndY=125.854 EndZ=0
    g5: ArcOfCircle CenterX=160 CenterY=193.831 CenterZ=0 NormalX=0 NormalY=0 NormalZ=1 AngleXU=0 Radius=146.7 StartAngle=2.65979 EndAngle=3.62339
  constraints (18):
    c: Coincident(g1,g2)
    c: Coincident(g2,g0)
    c: Horizontal(g0)
    c: Horizontal(g1)
    c: Vertical(g2)
    c: Coincident(g0,g-1)
    c: DistanceX(g1,g1) = 30
    c: Coincident(g3,g1)
    c: Vertical(g3)
    c: Coincident(g4,g0)
    c: Vertical(g4)
    c: Coincident(g5,g3)
    c: Coincident(g5,g4)
    c: DistanceY(g2,g2) = 371.663
    c: Equal(g1,g0)
    c: Radius(g5) = 146.7
    c: DistanceX(g0,g5) = 160
    c: DistanceY(g5,g1) = 177.831
FEATURE [PartDesign::Pad] Pad021
  Direction = (0,0,1)
  Length = 30
  Length2 = 10
  Profile = -> Sketch033
  ReferenceAxis = -> Sketch033 [N_Axis]
  Suppressed = false
  Type = 0
  expr: Length = <<bdim>>.bar_side_size
FEATURE [PartDesign::Body] Body022  label="fp_bar_1"
  AllowCompound = false
  Group = -> [Sketch033,Pad021]
  Origin = -> Origin023
  Tip = -> Pad021
FEATURE [App::Link] front_panel  label="front_panel001"
  LinkPlacement = pos=(333,635,687) rot=(0,0,1;3.14159rad)
  LinkedObject = -> Body021
  Placement = pos=(333,635,687) rot=(0,0,1;3.14159rad)
FEATURE [App::Link] fp_bar_1  label="front_panel_bar_a"
  LinkPlacement = pos=(333,220.337,687) rot=(0,1,0;3.14159rad)
  LinkedObject = -> Body022
  Placement = pos=(333,220.337,687) rot=(0,1,0;3.14159rad)
FEATURE [App::Link] fp_bar_002  label="front_panel_bar_b"
  LinkPlacement = pos=(13,220.337,657) rot=(0,0,1;0rad)
  LinkedObject = -> Body022
  Placement = pos=(13,220.337,657) rot=(0,0,1;0rad)
FEATURE [App::Link] _2lfa_driver  label="12lfa_driver001"
  LinkPlacement = pos=(173,414.169,712.2) rot=(0.707107,0.707107,0;3.14159rad)
  LinkedObject = -> Body008
  Placement = pos=(173,414.169,712.2) rot=(0.707107,0.707107,0;3.14159rad)
FEATURE [App::FeaturePython] Joint019  label="Fixed017"  # Assembly joint (typed FeaturePython)
  Activated = true
  AngleMax = 0
  AngleMin = 0
  Detach1 = false
  Detach2 = false
  Distance = 0
  Distance2 = 0
  EnableAngleMax = false
  EnableAngleMin = false
  EnableLengthMax = false
  EnableLengthMin = false
  JointType = 0 (Fixed)
  LengthMax = 0
  LengthMin = 0
  Offset1 = pos=(0,0,0) rot=(1,0,0;3.14159rad)
  Placement1 = pos=(160,220.831,13) rot=(1,0,0;3.14159rad)
  Placement2 = pos=(0,0,12.2) rot=(-0.707107,-0.707107,0;3.14159rad)
  Reference1 = -> Assembly [front_panel.Edge15,front_panel.Edge15]
  Reference2 = -> Assembly [_2lfa_driver.Edge9,_2lfa_driver.Edge9]
FEATURE [App::FeaturePython] Joint021  label="Fixed018"  # Assembly joint (typed FeaturePython)
  Activated = true
  AngleMax = 0
  AngleMin = 0
  Detach1 = false
  Detach2 = false
  Distance = 0
  Distance2 = 0
  EnableAngleMax = false
  EnableAngleMin = false
  EnableLengthMax = false
  EnableLengthMin = false
  JointType = 0 (Fixed)
  LengthMax = 0
  LengthMin = 0
  Offset2 = pos=(0,0,0) rot=(0,0,1;3.14159rad)
  Placement1 = pos=(13,635,700) rot=(-0.57735,-0.57735,0.57735;4.18879rad)
  Placement2 = pos=(320,0,13) rot=(0.57735,-0.57735,-0.57735;4.18879rad)
  Reference1 = -> Assembly [bottom_panel.Edge10,bottom_panel.Vertex6]
  Reference2 = -> Assembly [front_panel.Edge7,front_panel.Vertex4]
FEATURE [App::FeaturePython] Joint022  label="Fixed019"  # Assembly joint (typed FeaturePython)
  Activated = true
  AngleMax = 0
  AngleMin = 0
  Detach1 = false
  Detach2 = false
  Distance = 0
  Distance2 = 0
  EnableAngleMax = false
  EnableAngleMin = false
  EnableLengthMax = false
  EnableLengthMin = false
  JointType = 0 (Fixed)
  LengthMax = 0
  LengthMin = 0
  Offset2 = pos=(0,0,0) rot=(0,0,1;3.14159rad)
  Placement1 = pos=(0,414.663,0) rot=(-0.57735,-0.57735,0.57735;4.18879rad)
  Placement2 = pos=(0,0,0) rot=(-0.57735,0.57735,-0.57735;4.18879rad)
  Reference1 = -> Assembly [front_panel.Edge11,front_panel.Vertex7]
  Reference2 = -> Assembly [fp_bar_1.Edge6,fp_bar_1.Vertex5]
  expr: .Offset2.Base.z = 0
FEATURE [App::FeaturePython] Joint026  label="Unnamed"  # WARN: FeaturePython — macro-defined, semantics opaque (R4)
FEATURE [Sketcher::SketchObject] Sketch034
  ArcFitTolerance = 1e-06
  AttachmentSupport = -> [YZ_Plane024]
  FullyConstrained = true
  MakeInternals = false
  MapMode = 5
  Placement = pos=(0,0,0) rot=(0.57735,0.57735,0.57735;2.0944rad)
  expr: Constraints[10] = <<bdim>>.bbf2_w
  expr: Constraints[9] = <<bdim>>.bbf2_h
  sketch-geometry (4):
    g0: LineSegment StartX=0 StartY=0 StartZ=0 EndX=30 EndY=0 EndZ=0
    g1: LineSegment StartX=30 StartY=0 StartZ=0 EndX=30 EndY=449.669 EndZ=0
    g2: LineSegment StartX=30 StartY=449.669 StartZ=0 EndX=0 EndY=449.669 EndZ=0
    g3: LineSegment StartX=0 StartY=449.669 StartZ=0 EndX=0 EndY=0 EndZ=0
  constraints (11):
    c: Coincident(g0,g1)
    c: Coincident(g1,g2)
    c: Coincident(g2,g3)
    c: Coincident(g3,g0)
    c: Horizontal(g0)
    c: Horizontal(g2)
    c: Vertical(g1)
    c: Vertical(g3)
    c: Coincident(g0,g-1)
    c: DistanceX(g2,g2) = 30
    c: DistanceY(g1,g1) = 449.669
FEATURE [PartDesign::Pad] Pad022
  Direction = (1,0,0)
  Length = 30
  Length2 = 10
  Placement = pos=(0,0,0) rot=(1,1,1;2.0944rad)
  Profile = -> Sketch034
  ReferenceAxis = -> Sketch034 [N_Axis]
  Suppressed = false
  Type = 0
  expr: Length = <<bdim>>.bbf2_t
FEATURE [PartDesign::Body] Body023  label="brace bar fin 2"
  AllowCompound = false
  Group = -> [Sketch034,Pad022]
  Origin = -> Origin024
  Tip = -> Pad022
FEATURE [App::Link] brace_bar_fin_2  label="brace bar fin 2 b"
  LinkPlacement = pos=(43,250.337,207.331) rot=(0,0,1;3.14159rad)
  LinkedObject = -> Body023
  Placement = pos=(43,250.337,207.331) rot=(0,0,1;3.14159rad)
FEATURE [App::Link] brace_bar_fin_003  label="brace bar fin 2 a"
  LinkPlacement = pos=(303,250.337,207.331) rot=(0,0,1;4.71239rad)
  LinkedObject = -> Body023
  Placement = pos=(303,250.337,207.331) rot=(0,0,1;4.71239rad)
FEATURE [Sketcher::SketchObject] Sketch035
  ArcFitTolerance = 1e-06
  AttachmentSupport = -> [YZ_Plane025]
  FullyConstrained = true
  MakeInternals = false
  MapMode = 5
  Placement = pos=(0,0,0) rot=(0.57735,0.57735,0.57735;2.0944rad)
  expr: Constraints[10] = <<bdim>>.bbf1_w
  expr: Constraints[9] = <<bdim>>.bbf2_h
  sketch-geometry (4):
    g0: LineSegment StartX=0 StartY=0 StartZ=0 EndX=30 EndY=0 EndZ=0
    g1: LineSegment StartX=30 StartY=0 StartZ=0 EndX=30 EndY=449.669 EndZ=0
    g2: LineSegment StartX=30 StartY=449.669 StartZ=0 EndX=0 EndY=449.669 EndZ=0
    g3: LineSegment StartX=0 StartY=449.669 StartZ=0 EndX=0 EndY=0 EndZ=0
  constraints (11):
    c: Coincident(g0,g1)
    c: Coincident(g1,g2)
    c: Coincident(g2,g3)
    c: Coincident(g3,g0)
    c: Horizontal(g0)
    c: Horizontal(g2)
    c: Vertical(g1)
    c: Vertical(g3)
    c: Coincident(g0,g-1)
    c: DistanceX(g2,g2) = 30
    c: DistanceY(g1,g1) = 449.669
FEATURE [PartDesign::Pad] Pad023
  Direction = (1,0,0)
  Length = 30
  Length2 = 10
  Placement = pos=(0,0,0) rot=(1,1,1;2.0944rad)
  Profile = -> Sketch035
  ReferenceAxis = -> Sketch035 [N_Axis]
  Suppressed = false
  Type = 0
  expr: Length = <<bdim>>.bbf2_t
FEATURE [PartDesign::Body] Body024  label="brace bar fin 1"
  AllowCompound = false
  Group = -> [Sketch035,Pad023]
  Origin = -> Origin025
  Tip = -> Pad023
FEATURE [App::Link] brace_bar_fin_1  label="brace bar fin 1 b"
  LinkPlacement = pos=(303,427.669,43) rot=(0,0,1;0rad)
  LinkedObject = -> Body024
  Placement = pos=(303,427.669,43) rot=(0,0,1;0rad)
FEATURE [App::Link] brace_bar_fin_004  label="brace bar fin 1 a"
  LinkPlacement = pos=(13,427.669,43) rot=(0,0,1;0rad)
  LinkedObject = -> Body024
  Placement = pos=(13,427.669,43) rot=(0,0,1;0rad)
FEATURE [Sketcher::SketchObject] Sketch036
  ArcFitTolerance = 1e-06
  AttachmentSupport = -> [XY_Plane026]
  FullyConstrained = true
  MakeInternals = false
  MapMode = 5
  expr: Constraints[10] = <<bdim>>.bbbp2_w
  expr: Constraints[9] = <<bdim>>.bbbp2_t
  sketch-geometry (4):
    g0: LineSegment StartX=0 StartY=0 StartZ=0 EndX=0 EndY=164.331 EndZ=0
    g1: LineSegment StartX=0 StartY=164.331 StartZ=0 EndX=-30 EndY=164.331 EndZ=0
    g2: LineSegment StartX=-30 StartY=164.331 StartZ=0 EndX=-30 EndY=0 EndZ=0
    g3: LineSegment StartX=-30 StartY=0 StartZ=0 EndX=0 EndY=0 EndZ=0
  constraints (11):
    c: Coincident(g0,g1)
    c: Coincident(g1,g2)
    c: Coincident(g2,g3)
    c: Coincident(g3,g0)
    c: Vertical(g0)
    c: Vertical(g2)
    c: Horizontal(g1)
    c: Horizontal(g3)
    c: Coincident(g0,g-1)
    c: DistanceX(g1,g1) = 30
    c: DistanceY(g2,g2) = 164.331
FEATURE [Sketcher::SketchObject] Sketch037
  ArcFitTolerance = 1e-06
  AttachmentSupport = -> [XY_Plane027]
  FullyConstrained = true
  MakeInternals = false
  MapMode = 5
  expr: Constraints[10] = <<bdim>>.bbbp1_w
  expr: Constraints[9] = <<bdim>>.bbbp1_t
  sketch-geometry (4):
    g0: LineSegment StartX=0 StartY=0 StartZ=0 EndX=0 EndY=371.669 EndZ=0
    g1: LineSegment StartX=0 StartY=371.669 StartZ=0 EndX=-30 EndY=371.669 EndZ=0
    g2: LineSegment StartX=-30 StartY=371.669 StartZ=0 EndX=-30 EndY=0 EndZ=0
    g3: LineSegment StartX=-30 StartY=0 StartZ=0 EndX=0 EndY=0 EndZ=0
  constraints (11):
    c: Coincident(g0,g1)
    c: Coincident(g1,g2)
    c: Coincident(g2,g3)
    c: Coincident(g3,g0)
    c: Vertical(g0)
    c: Vertical(g2)
    c: Horizontal(g1)
    c: Horizontal(g3)
    c: Coincident(g0,g-1)
    c: DistanceX(g1,g1) = 30
    c: DistanceY(g2,g2) = 371.669
FEATURE [PartDesign::Pad] Pad025
  Direction = (0,0,1)
  Length = 30
  Length2 = 10
  Profile = -> Sketch037
  ReferenceAxis = -> Sketch037 [N_Axis]
  Suppressed = false
  Type = 0
  expr: Length = <<bdim>>.bbbp1_t
FEATURE [PartDesign::Body] Body026  label="brace_bar_back_panel_2"
  AllowCompound = false
  Group = -> [Sketch037,Pad025]
  Origin = -> Origin027
  Tip = -> Pad025
FEATURE [App::Link] brace_bar_back_panel_1  label="brace_bar_back_panel_f"
  LinkPlacement = pos=(43,427.669,13) rot=(0,0,1;0rad)
  LinkedObject = -> Body025
  Placement = pos=(43,427.669,13) rot=(0,0,1;0rad)
FEATURE [App::Link] brace_bar_back_panel_2  label="brace_bar_back_panel_a"
  LinkPlacement = pos=(43,43,13) rot=(0,0,1;0rad)
  LinkedObject = -> Body026
  Placement = pos=(43,43,13) rot=(0,0,1;0rad)
FEATURE [App::FeaturePython] Joint037  label="Fixed031"  # Assembly joint (typed FeaturePython)
  Activated = true
  AngleMax = 0
  AngleMin = 0
  Detach1 = false
  Detach2 = false
  Distance = 0
  Distance2 = 0
  EnableAngleMax = false
  EnableAngleMin = false
  EnableLengthMax = false
  EnableLengthMin = false
  JointType = 0 (Fixed)
  LengthMax = 0
  LengthMin = 0
  Offset2 = pos=(0,0,0) rot=(0,0,-1;1.5708rad)
  Placement1 = pos=(-30,0,0) rot=(0,0,1;0rad)
  Placement2 = pos=(687,-30,0) rot=(0.57735,0.57735,0.57735;2.0944rad)
  Reference1 = -> Assembly [brace_bar_back_panel_2.Edge8,brace_bar_back_panel_2.Vertex7]
  Reference2 = -> Assembly [side_panel_002_bar_002.Edge4,side_panel_002_bar_002.Vertex4]
FEATURE [App::FeaturePython] Joint038  label="Fixed032"  # Assembly joint (typed FeaturePython)
  Activated = true
  AngleMax = 0
  AngleMin = 0
  Detach1 = false
  Detach2 = false
  Distance = 0
  Distance2 = 0
  EnableAngleMax = false
  EnableAngleMin = false
  EnableLengthMax = false
  EnableLengthMin = false
  JointType = 0 (Fixed)
  LengthMax = 0
  LengthMin = 0
  Offset2 = pos=(0,0,0) rot=(0,0,1;1.5708rad)
  Placement1 = pos=(674,-3.73e-14,0) rot=(0.707107,0,0.707107;3.14159rad)
  Placement2 = pos=(-30,164.331,0) rot=(0,0,1;1.5708rad)
  Reference1 = -> Assembly [side_panel_001_bar_001.Edge3,side_panel_001_bar_001.Vertex3]
  Reference2 = -> Assembly [brace_bar_back_panel_1.Edge5,brace_bar_back_panel_1.Vertex5]
FEATURE [App::Link] brace_bar_back_panel_003  label="brace_bar_back_panel_b"
  LinkPlacement = pos=(333,43,13) rot=(0,0,1;0rad)
  LinkedObject = -> Body026
  Placement = pos=(333,43,13) rot=(0,0,1;0rad)
FEATURE [App::Link] brace_bar_back_panel_004  label="brace_bar_back_panel_c"
  LinkPlacement = pos=(303,427.669,13) rot=(0,1,0;1.5708rad)
  LinkedObject = -> Body025
  Placement = pos=(303,427.669,13) rot=(0,1,0;1.5708rad)
FEATURE [App::FeaturePython] Joint039  label="Fixed033"  # Assembly joint (typed FeaturePython)
  Activated = true
  AngleMax = 0
  AngleMin = 0
  Detach1 = false
  Detach2 = false
  Distance = 0
  Distance2 = 0
  EnableAngleMax = false
  EnableAngleMin = false
  EnableLengthMax = false
  EnableLengthMin = false
  JointType = 0 (Fixed)
  LengthMax = 0
  LengthMin = 0
  Offset2 = pos=(0,0,-43) rot=(0,0,-1;1.5708rad)
  Placement1 = pos=(0,0,0) rot=(0.57735,0.57735,0.57735;4.18879rad)
  Placement2 = pos=(-1.066e-13,43,320) rot=(0,-0.707107,0.707107;3.14159rad)
  Reference1 = -> Assembly [brace_bar_back_panel_003.Edge3,brace_bar_back_panel_003.Vertex1]
  Reference2 = -> Assembly [back_panel.Edge9,back_panel.Vertex7]
  expr: .Offset2.Base.z = -(<<bdim>>.sp_thick + <<bdim>>.spb_t)
FEATURE [App::FeaturePython] Joint040  label="Fixed034"  # Assembly joint (typed FeaturePython)
  Activated = true
  AngleMax = 0
  AngleMin = 0
  Detach1 = false
  Detach2 = false
  Distance = 0
  Distance2 = 0
  EnableAngleMax = false
  EnableAngleMin = false
  EnableLengthMax = false
  EnableLengthMin = false
  JointType = 0 (Fixed)
  LengthMax = 0
  LengthMin = 0
  Offset2 = pos=(0,0,43) rot=(0,0,-1;3.14159rad)
  Placement1 = pos=(0,164.331,30) rot=(0.57735,0.57735,0.57735;4.18879rad)
  Placement2 = pos=(-1.066e-13,592,320) rot=(0.57735,-0.57735,0.57735;2.0944rad)
  Reference1 = -> Assembly [brace_bar_back_panel_004.Edge4,brace_bar_back_panel_004.Vertex4]
  Reference2 = -> Assembly [back_panel.Edge9,back_panel.Vertex5]
  expr: .Offset2.Base.z = <<bdim>>.sp_thick + <<bdim>>.spb_t
  expr: .Offset2.Rotation.Yaw = -180
FEATURE [App::Link] brace_bar_back_panel_005  label="brace_bar_back_panel_d"
  LinkPlacement = pos=(188,43,13) rot=(0,0,1;0rad)
  LinkedObject = -> Body026
  Placement = pos=(188,43,13) rot=(0,0,1;0rad)
FEATURE [App::FeaturePython] Joint041  label="Fixed035"  # Assembly joint (typed FeaturePython)
  Activated = true
  AngleMax = 0
  AngleMin = 0
  Detach1 = false
  Detach2 = false
  Distance = 0
  Distance2 = 0
  EnableAngleMax = false
  EnableAngleMin = false
  EnableLengthMax = false
  EnableLengthMin = false
  JointType = 0 (Fixed)
  LengthMax = 0
  LengthMin = 0
  Offset2 = pos=(0,0,0) rot=(0,0,1;3.14159rad)
  Placement1 = pos=(30,-30,130) rot=(0,0,1;0rad)
  Placement2 = pos=(-15,0,0) rot=(0,-1,0;4.71239rad)
  Reference1 = -> Assembly [side_panel_002_bar_004.Edge7,side_panel_002_bar_004.Edge7]
  Reference2 = -> Assembly [brace_bar_back_panel_005.Edge11,brace_bar_back_panel_005.Edge11]
FEATURE [Sketcher::SketchObject] Sketch
  ArcFitTolerance = 1e-06
  AttachmentSupport = -> [YZ_Plane028]
  FullyConstrained = true
  MakeInternals = false
  MapMode = 5
  Placement = pos=(0,0,0) rot=(0.57735,0.57735,0.57735;2.0944rad)
  expr: Constraints[10] = <<bdim>>.mbbf1_w
  expr: Constraints[9] = <<bdim>>.mbbf1_h
  sketch-geometry (4):
    g0: LineSegment StartX=0 StartY=0 StartZ=0 EndX=449.669 EndY=0 EndZ=0
    g1: LineSegment StartX=449.669 StartY=0 StartZ=0 EndX=449.669 EndY=30 EndZ=0
    g2: LineSegment StartX=449.669 StartY=30 StartZ=0 EndX=0 EndY=30 EndZ=0
    g3: LineSegment StartX=0 StartY=30 StartZ=0 EndX=0 EndY=0 EndZ=0
  constraints (11):
    c: Coincident(g0,g1)
    c: Coincident(g1,g2)
    c: Coincident(g2,g3)
    c: Coincident(g3,g0)
    c: Horizontal(g0)
    c: Horizontal(g2)
    c: Vertical(g1)
    c: Vertical(g3)
    c: Coincident(g0,g-1)
    c: DistanceY(g1,g1) = 30
    c: DistanceX(g2,g2) = 449.669
FEATURE [PartDesign::Pad] Pad026
  Direction = (1,0,0)
  Length = 30
  Length2 = 10
  Placement = pos=(0,0,0) rot=(1,1,1;2.0944rad)
  Profile = -> Sketch
  ReferenceAxis = -> Sketch [N_Axis]
  Suppressed = false
  Type = 0
  expr: Length = <<bdim>>.mbbf1_t
FEATURE [PartDesign::Body] Body027  label="middle brace bar fin 1 model"
  AllowCompound = false
  Group = -> [Sketch,Pad026]
  Origin = -> Origin028
  Tip = -> Pad026
FEATURE [App::Link] side_panel_001_bar_008  label="cross_brace_fin_1"
  LinkPlacement = pos=(303,457.669,13) rot=(0,-1,0;1.5708rad)
  LinkedObject = -> Body013
  Placement = pos=(303,457.669,13) rot=(0,-1,0;1.5708rad)
FEATURE [App::Link] middle_brace_bar_fin_1  label="middle brace bar fin 1"
  LinkPlacement = pos=(158,427.669,492.669) rot=(-1,0,0;1.5708rad)
  LinkedObject = -> Body027
  Placement = pos=(158,427.669,492.669) rot=(-1,0,0;1.5708rad)
FEATURE [App::FeaturePython] Joint044  label="Fixed038"  # Assembly joint (typed FeaturePython)
  Activated = true
  AngleMax = 0
  AngleMin = 0
  Detach1 = false
  Detach2 = false
  Distance = 0
  Distance2 = 0
  EnableAngleMax = false
  EnableAngleMin = false
  EnableLengthMax = false
  EnableLengthMin = false
  JointType = 0 (Fixed)
  LengthMax = 0
  LengthMin = 0
  Offset2 = pos=(0,0,0) rot=(0,0,1;1.5708rad)
  Placement1 = pos=(30,5.68e-14,130) rot=(0,0,1;0rad)
  Placement2 = pos=(15,449.669,30) rot=(0.57735,-0.57735,0.57735;4.18879rad)
  Reference1 = -> Assembly [side_panel_001_bar_008.Edge6,side_panel_001_bar_008.Edge6]
  Reference2 = -> Assembly [middle_brace_bar_fin_1.Edge5,middle_brace_bar_fin_1.Edge5]
FEATURE [Sketcher::SketchObject] Sketch038
  ArcFitTolerance = 1e-06
  AttachmentSupport = -> [XY_Plane029]
  FullyConstrained = true
  MakeInternals = false
  MapMode = 5
  expr: Constraints[12] = <<bdim>>.dbb_h
  expr: Constraints[13] = <<bdim>>.dbb_w
  sketch-geometry (5):
    g0: LineSegment StartX=0 StartY=106.066 StartZ=0 EndX=0 EndY=63.6396 EndZ=0
    g1: LineSegment StartX=0 StartY=63.6396 StartZ=0 EndX=-63.6396 EndY=0 EndZ=0
    g2: LineSegment StartX=-63.6396 StartY=0 StartZ=0 EndX=-106.066 EndY=0 EndZ=0
    g3: LineSegment StartX=-106.066 StartY=0 StartZ=0 EndX=0 EndY=106.066 EndZ=0
    g4: LineSegment [constr] StartX=-84.8528 StartY=21.2132 StartZ=0 EndX=-63.6396 EndY=0 EndZ=0
  constraints (15):
    c: PointOnObject(g0,g-2)
    c: PointOnObject(g0,g-2)
    c: Coincident(g0,g1)
    c: PointOnObject(g1,g-1)
    c: Coincident(g1,g2)
    c: PointOnObject(g2,g-1)
    c: Coincident(g2,g3)
    c: Coincident(g3,g0)
    c: Equal(g0,g2)
    c: Parallel(g3,g1)
    c: PointOnObject(g4,g3)
    c: Perpendicular(g3,g4)
    c: Distance(g4) = 30
    c: Distance(g3) = 150
    c: Coincident(g4,g1)
FEATURE [PartDesign::Pad] Pad027
  Direction = (0,0,1)
  Length = 30
  Length2 = 10
  Profile = -> Sketch038
  ReferenceAxis = -> Sketch038 [N_Axis]
  Suppressed = false
  Type = 0
  expr: Length = <<bdim>>.dbb_t
FEATURE [PartDesign::Body] Body028  label="driver_brace_bar"
  AllowCompound = false
  Group = -> [Sketch038,Pad027]
  Origin = -> Origin029
  Tip = -> Pad027
FEATURE [App::Link] driver_brace_bar  label="driver_brace_bar_a"
  LinkPlacement = pos=(43,592,657) rot=(0,0,1;3.14159rad)
  LinkedObject = -> Body028
  Placement = pos=(43,592,657) rot=(0,0,1;3.14159rad)
FEATURE [App::Link] driver_brace_bar001  label="driver_brace_bar_b"
  LinkPlacement = pos=(303,592,657) rot=(0,0,1;1.5708rad)
  LinkedObject = -> Body028
  Placement = pos=(303,592,657) rot=(0,0,1;1.5708rad)
FEATURE [App::FeaturePython] Joint045  label="Slider039"  # Assembly joint (typed FeaturePython)
  Activated = true
  AngleMax = 0
  AngleMin = 0
  Detach1 = false
  Detach2 = false
  Distance = 0
  Distance2 = 0
  EnableAngleMax = false
  EnableAngleMin = false
  EnableLengthMax = false
  EnableLengthMin = false
  JointType = 3 (Slider)
  LengthMax = 0
  LengthMin = 0
  Offset2 = pos=(0,0,0) rot=(0,0,-1;1.5708rad)
  Placement1 = pos=(-84.8528,0,30) rot=(-0.707107,0,0.707107;3.14159rad)
  Placement2 = pos=(0,0,130) rot=(-0.707107,0.707107,0;3.14159rad)
  Reference1 = -> Assembly [driver_brace_bar.Edge10,driver_brace_bar.Edge10]
  Reference2 = -> Assembly [side_panel_001_bar_004.Edge11,side_panel_001_bar_004.Edge11]
FEATURE [App::FeaturePython] Joint046  label="Slider"  # Assembly joint (typed FeaturePython)
  Activated = true
  AngleMax = 0
  AngleMin = 0
  Detach1 = false
  Detach2 = false
  Distance = 0
  Distance2 = 0
  EnableAngleMax = false
  EnableAngleMin = false
  EnableLengthMax = false
  EnableLengthMin = false
  JointType = 3 (Slider)
  LengthMax = 0
  LengthMin = 0
  Placement1 = pos=(0,84.8528,30) rot=(-0.57735,-0.57735,0.57735;4.18879rad)
  Placement2 = pos=(30,316.736,30) rot=(-0.57735,-0.57735,0.57735;4.18879rad)
  Reference1 = -> Assembly [driver_brace_bar.Edge4,driver_brace_bar.Edge4]
  Reference2 = -> Assembly [fp_bar_002.Edge18,fp_bar_002.Edge18]
FEATURE [App::FeaturePython] Joint047  label="Slider040"  # Assembly joint (typed FeaturePython)
  Activated = true
  AngleMax = 0
  AngleMin = 0
  Detach1 = false
  Detach2 = false
  Distance = 0
  Distance2 = 0
  EnableAngleMax = false
  EnableAngleMin = false
  EnableLengthMax = false
  EnableLengthMin = false
  JointType = 3 (Slider)
  LengthMax = 0
  LengthMin = 0
  Offset2 = pos=(0,0,0) rot=(0,0,-1;1.5708rad)
  Placement1 = pos=(0,0,130) rot=(0,1,0;3.14159rad)
  Placement2 = pos=(-1.137e-13,84.8528,30) rot=(0,-0.707107,0.707107;3.14159rad)
  Reference1 = -> Assembly [side_panel_001_bar_004.Edge11,side_panel_001_bar_004.Edge11]
  Reference2 = -> Assembly [driver_brace_bar001.Edge4,driver_brace_bar001.Edge4]
FEATURE [App::FeaturePython] Joint048  label="Slider041"  # Assembly joint (typed FeaturePython)
  Activated = true
  AngleMax = 0
  AngleMin = 0
  Detach1 = false
  Detach2 = false
  Distance = 0
  Distance2 = 0
  EnableAngleMax = false
  EnableAngleMin = false
  EnableLengthMax = false
  EnableLengthMin = false
  JointType = 3 (Slider)
  LengthMax = 0
  LengthMin = 0
  Placement1 = pos=(-84.8528,0,30) rot=(-0.707107,0,0.707107;3.14159rad)
  Placement2 = pos=(30,316.736,0) rot=(-0.57735,-0.57735,0.57735;4.18879rad)
  Reference1 = -> Assembly [driver_brace_bar001.Edge10,driver_brace_bar001.Edge10]
  Reference2 = -> Assembly [fp_bar_1.Edge17,fp_bar_1.Edge17]
FEATURE [PartDesign::Pad] Pad011
  Direction = (0,-1,2e-16)
  Length = 30
  Length2 = 10
  Placement = pos=(0,0,0) rot=(1,0,0;1.5708rad)
  Profile = -> Sketch023
  ReferenceAxis = -> Sketch023 [N_Axis]
  Suppressed = false
  Type = 0
  expr: Length = <<bdim>>.spb_h
FEATURE [PartDesign::Body] Body012  label="side_panel_001_bar_003"
  AllowCompound = false
  Group = -> [Sketch023,Pad011]
  Origin = -> Origin013
  Tip = -> Pad011
FEATURE [Sketcher::SketchObject] Sketch040
  ArcFitTolerance = 1e-06
  AttachmentSupport = -> [XZ_Plane031]
  FullyConstrained = true
  MakeInternals = false
  MapMode = 5
  Placement = pos=(0,0,0) rot=(1,0,0;1.5708rad)
  expr: Constraints[10] = <<bdim>>.mbbf2_w
  expr: Constraints[9] = <<bdim>>.mbbf2_h
  sketch-geometry (4):
    g0: LineSegment StartX=0 StartY=0 StartZ=0 EndX=30 EndY=0 EndZ=0
    g1: LineSegment StartX=30 StartY=0 StartZ=0 EndX=30 EndY=505.669 EndZ=0
    g2: LineSegment StartX=30 StartY=505.669 StartZ=0 EndX=0 EndY=505.669 EndZ=0
    g3: LineSegment StartX=0 StartY=505.669 StartZ=0 EndX=0 EndY=0 EndZ=0
  constraints (11):
    c: Coincident(g0,g1)
    c: Coincident(g1,g2)
    c: Coincident(g2,g3)
    c: Coincident(g3,g0)
    c: Horizontal(g0)
    c: Horizontal(g2)
    c: Vertical(g1)
    c: Vertical(g3)
    c: Coincident(g0,g-1)
    c: DistanceX(g2,g2) = 30
    c: DistanceY(g1,g1) = 505.669
FEATURE [PartDesign::Pad] Pad028
  Direction = (0,-1,2e-16)
  Length = 30
  Length2 = 10
  Placement = pos=(0,0,0) rot=(1,0,0;1.5708rad)
  Profile = -> Sketch040
  ReferenceAxis = -> Sketch040 [N_Axis]
  Suppressed = false
  Type = 0
  expr: Length = <<bdim>>.mbbf2_t
FEATURE [PartDesign::Body] Body030  label="middle_brace_bar_fin_2_model"
  AllowCompound = false
  Group = -> [Sketch040,Pad028]
  Origin = -> Origin031
  Tip = -> Pad028
FEATURE [Sketcher::SketchObject] Sketch041
  ArcFitTolerance = 1e-06
  AttachmentSupport = -> [XZ_Plane032]
  FullyConstrained = true
  MakeInternals = false
  MapMode = 5
  Placement = pos=(0,0,0) rot=(1,0,0;1.5708rad)
  expr: Constraints[10] = <<bdim>>.mbbsp2_w
  expr: Constraints[9] = <<bdim>>.mbbsp2_h
  sketch-geometry (4):
    g0: LineSegment StartX=0 StartY=0 StartZ=0 EndX=30 EndY=0 EndZ=0
    g1: LineSegment StartX=30 StartY=0 StartZ=0 EndX=30 EndY=657 EndZ=0
    g2: LineSegment StartX=30 StartY=657 StartZ=0 EndX=0 EndY=657 EndZ=0
    g3: LineSegment StartX=0 StartY=657 StartZ=0 EndX=0 EndY=0 EndZ=0
  constraints (11):
    c: Coincident(g0,g1)
    c: Coincident(g1,g2)
    c: Coincident(g2,g3)
    c: Coincident(g3,g0)
    c: Horizontal(g0)
    c: Horizontal(g2)
    c: Vertical(g1)
    c: Vertical(g3)
    c: Coincident(g0,g-1)
    c: DistanceX(g2,g2) = 30
    c: DistanceY(g1,g1) = 657
FEATURE [PartDesign::Pad] Pad029
  Direction = (0,-1,2e-16)
  Length = 30
  Length2 = 10
  Placement = pos=(0,0,0) rot=(1,0,0;1.5708rad)
  Profile = -> Sketch041
  ReferenceAxis = -> Sketch041 [N_Axis]
  Suppressed = false
  Type = 0
  expr: Length = <<bdim>>.mbbsp2_t
FEATURE [PartDesign::Body] Body031  label="middle_brace_bar_side_panel_003"
  AllowCompound = false
  Group = -> [Sketch041,Pad029]
  Origin = -> Origin032
  Tip = -> Pad029
FEATURE [TechDraw::DrawSVGTemplate] Template
  Height = 215.9
  Orientation = 1
  Template = <path>
  Width = 279.4
FEATURE [TechDraw::DrawProjGroupItem] View  label="P1 (côté)"
  Caption = P1 (côté)
  CoarseView = false
  Direction = (-2e-16,1,0)
  Focus = 100
  HardHidden = false
  IsoCount = 0
  IsoHidden = false
  IsoVisible = false
  LockPosition = true
  Perspective = false
  Rotation = 0
  RotationVector = (1,0,0)
  Scale = 0.1
  ScaleType = 2
  ScrubCount = 1
  SeamHidden = false
  SeamVisible = true
  SmoothHidden = false
  SmoothVisible = true
  Type = 0
  X = 0
  XDirection = (-1,-2e-16,0)
  XSource = -> [top_panel]
  Y = 0
FEATURE [TechDraw::DrawProjGroupItem] ProjItem  label="P1 (devant)"
  Caption = P1 (devant)
  CoarseView = false
  Direction = (-1,-1e-16,0)
  Focus = 100
  HardHidden = false
  IsoCount = 0
  IsoHidden = false
  IsoVisible = false
  LockPosition = false
  Perspective = false
  Rotation = 0
  RotationVector = (1,0,0)
  Scale = 0.1
  ScaleType = 0
  ScrubCount = 1
  SeamHidden = false
  SeamVisible = true
  SmoothHidden = false
  SmoothVisible = true
  Type = 2
  X = -47.4
  XDirection = (1e-16,-1,0)
  XSource = -> [top_panel]
  Y = 0
FEATURE [TechDraw::DrawProjGroup] ProjGroup
  Anchor = -> View
  AutoDistribute = true
  LockPosition = false
  ProjectionType = 0
  Rotation = 0
  Scale = 0.1
  ScaleType = 0
  Views = -> [View,ProjItem]
  X = 82.9098
  XSource = -> [top_panel]
  Y = 178.334
  spacingX = 15
  spacingY = 15
FEATURE [TechDraw::DrawProjGroupItem] View002  label="P2 (devant)"
  Caption = P2 (devant)
  CoarseView = false
  Direction = (1,-1e-16,0)
  Focus = 100
  HardHidden = false
  IsoCount = 0
  IsoHidden = false
  IsoVisible = false
  LockPosition = true
  Perspective = false
  Rotation = 0
  RotationVector = (1,0,0)
  Scale = 0.1
  ScaleType = 2
  ScrubCount = 1
  SeamHidden = false
  SeamVisible = true
  SmoothHidden = false
  SmoothVisible = true
  Type = 0
  X = 0
  XDirection = (1e-16,1,0)
  XSource = -> [bottom_panel]
  Y = 0
FEATURE [TechDraw::DrawProjGroupItem] ProjItem002  label="P2 (côté)"
  Caption = P2 (côté)
  CoarseView = false
  Direction = (0,-1,0)
  Focus = 100
  HardHidden = false
  IsoCount = 0
  IsoHidden = false
  IsoVisible = false
  LockPosition = false
  Perspective = false
  Rotation = 0
  RotationVector = (1,0,0)
  ScaleType = 2
  ScrubCount = 1
  SeamHidden = false
  SeamVisible = true
  SmoothHidden = false
  SmoothVisible = true
  Type = 1
  X = 47.4
  XDirection = (1,0,0)
  XSource = -> [bottom_panel]
  Y = 0
FEATURE [TechDraw::DrawProjGroup] ProjGroup002
  Anchor = -> View002
  AutoDistribute = true
  LockPosition = false
  ProjectionType = 0
  Rotation = 0
  Scale = 0.1
  ScaleType = 0
  Views = -> [View002,ProjItem002]
  X = 35.4839
  XSource = -> [bottom_panel]
  Y = 87.3167
  spacingX = 15
  spacingY = 15
FEATURE [TechDraw::DrawProjGroupItem] View003  label="P4 (devant)"
  Caption = P4 (devant)
  CoarseView = false
  Direction = (0,-1,0)
  Focus = 100
  HardHidden = false
  IsoCount = 0
  IsoHidden = false
  IsoVisible = false
  LockPosition = true
  Perspective = false
  Rotation = 0
  RotationVector = (1,0,0)
  Scale = 0.1
  ScaleType = 2
  ScrubCount = 1
  SeamHidden = false
  SeamVisible = true
  SmoothHidden = false
  SmoothVisible = true
  Type = 0
  X = 0
  XDirection = (1,0,0)
  XSource = -> [side_panel_002]
  Y = 0
FEATURE [TechDraw::DrawProjGroupItem] ProjItem003  label="P4 (côté)"
  Caption = P4 (côté)
  CoarseView = false
  Direction = (1,-1e-16,0)
  Focus = 100
  HardHidden = false
  IsoCount = 0
  IsoHidden = false
  IsoVisible = false
  LockPosition = false
  Perspective = false
  Rotation = 0
  RotationVector = (1,0,0)
  ScaleType = 2
  ScrubCount = 1
  SeamHidden = false
  SeamVisible = true
  SmoothHidden = false
  SmoothVisible = true
  Type = 2
  X = -31.65
  XDirection = (1e-16,1,0)
  XSource = -> [side_panel_002]
  Y = 0
FEATURE [TechDraw::DrawProjGroup] ProjGroup003
  Anchor = -> View003
  AutoDistribute = true
  LockPosition = false
  ProjectionType = 0
  Rotation = 0
  Scale = 0.1
  ScaleType = 0
  Views = -> [View003,ProjItem003]
  X = 148.911
  XSource = -> [side_panel_002]
  Y = 79.8518
  spacingX = 15
  spacingY = 15
FEATURE [TechDraw::DrawProjGroupItem] View004  label="P5 (devant)"
  Caption = P5 (devant)
  CoarseView = false
  Direction = (0,0,1)
  Focus = 100
  HardHidden = false
  IsoCount = 0
  IsoHidden = false
  IsoVisible = false
  LockPosition = true
  Perspective = false
  Rotation = 0
  RotationVector = (1,0,0)
  Scale = 0.1
  ScaleType = 2
  ScrubCount = 1
  SeamHidden = false
  SeamVisible = true
  SmoothHidden = false
  SmoothVisible = true
  Type = 0
  X = 0
  XDirection = (-1,1e-16,0)
  XSource = -> [front_panel]
  Y = 0
FEATURE [TechDraw::DrawProjGroupItem] ProjItem004  label="P5 (côté)"
  Caption = P5 (côté)
  CoarseView = false
  Direction = (1,-1e-16,1e-16)
  Focus = 100
  HardHidden = false
  IsoCount = 0
  IsoHidden = false
  IsoVisible = false
  LockPosition = false
  Perspective = false
  Rotation = 0
  RotationVector = (1,0,0)
  ScaleType = 2
  ScrubCount = 1
  SeamHidden = false
  SeamVisible = true
  SmoothHidden = false
  SmoothVisible = true
  Type = 1
  X = 31.65
  XDirection = (-1e-16,0,1)
  XSource = -> [front_panel]
  Y = 0
FEATURE [TechDraw::DrawProjGroup] ProjGroup004
  Anchor = -> View004
  AutoDistribute = true
  LockPosition = false
  ProjectionType = 0
  Rotation = 0
  Scale = 0.1
  ScaleType = 0
  Views = -> [View004,ProjItem004]
  X = 220.332
  XSource = -> [front_panel]
  Y = 188.094
  spacingX = 15
  spacingY = 15
FEATURE [TechDraw::DrawProjGroupItem] View005  label="P6 (devant)"
  Caption = P6 (devant)
  CoarseView = false
  Direction = (0,0,1)
  Focus = 100
  HardHidden = false
  IsoCount = 0
  IsoHidden = false
  IsoVisible = false
  LockPosition = true
  Perspective = false
  Rotation = 0
  RotationVector = (1,0,0)
  Scale = 0.1
  ScaleType = 2
  ScrubCount = 1
  SeamHidden = false
  SeamVisible = true
  SmoothHidden = false
  SmoothVisible = true
  Type = 0
  X = 0
  XDirection = (-1,-2e-16,0)
  XSource = -> [back_panel]
  Y = 0
FEATURE [TechDraw::DrawProjGroupItem] ProjItem005  label="P6 (côté)"
  Caption = P6 (côté)
  CoarseView = false
  Direction = (1,2e-16,1e-16)
  Focus = 100
  HardHidden = false
  IsoCount = 0
  IsoHidden = false
  IsoVisible = false
  LockPosition = false
  Perspective = false
  Rotation = 0
  RotationVector = (1,0,0)
  ScaleType = 2
  ScrubCount = 1
  SeamHidden = false
  SeamVisible = true
  SmoothHidden = false
  SmoothVisible = true
  Type = 1
  X = 31.65
  XDirection = (-1e-16,0,1)
  XSource = -> [back_panel]
  Y = 0
FEATURE [TechDraw::DrawProjGroup] ProjGroup005
  Anchor = -> View005
  AutoDistribute = true
  LockPosition = false
  ProjectionType = 0
  Rotation = 0
  Scale = 0.1
  ScaleType = 0
  Views = -> [View005,ProjItem005]
  X = 221.075
  XSource = -> [back_panel]
  Y = 112.677
  spacingX = 15
  spacingY = 15
FEATURE [TechDraw::DrawViewDimension] Dimension
  AngleOverride = false
  Arbitrary = false
  ArbitraryTolerances = false
  BoxCorners = (2) [(-31.75,-35,0),(31.75,35,0)]
  EqualTolerance = true
  ExtensionAngle = 0
  FormatSpec = %.2w
  FormatSpecOverTolerance = %+.2w
  FormatSpecUnderTolerance = %+.2w
  Inverted = false
  LineAngle = 0
  LockPosition = false
  MeasureType = 1
  OverTolerance = 0
  References2D = -> [ProjItem]
  Rotation = 0
  Scale = 0.1
  ScaleType = 0
  TheoreticalExact = false
  Type = 2
  UnderTolerance = 0
  X = 19.6478
  Y = 0
FEATURE [TechDraw::DrawViewDimension] Dimension001
  AngleOverride = false
  Arbitrary = false
  ArbitraryTolerances = false
  BoxCorners = (2) [(-31.75,-35,0),(31.75,35,0)]
  EqualTolerance = true
  ExtensionAngle = 0
  FormatSpec = %.2w
  FormatSpecOverTolerance = %+.2w
  FormatSpecUnderTolerance = %+.2w
  Inverted = false
  LineAngle = 0
  LockPosition = false
  MeasureType = 1
  OverTolerance = 0
  References2D = -> [ProjItem]
  Rotation = 0
  Scale = 0.1
  ScaleType = 0
  TheoreticalExact = false
  Type = 1
  UnderTolerance = 0
  X = 0
  Y = -23.8556
FEATURE [TechDraw::DrawViewDimension] Dimension002
  AngleOverride = false
  Arbitrary = false
  ArbitraryTolerances = false
  BoxCorners = (2) [(-0.65,-35,0),(0.65,35,0)]
  EqualTolerance = true
  ExtensionAngle = 0
  FormatSpec = %.2w
  FormatSpecOverTolerance = %+.2w
  FormatSpecUnderTolerance = %+.2w
  Inverted = false
  LineAngle = 0
  LockPosition = false
  MeasureType = 1
  OverTolerance = 0
  References2D = -> [View]
  Rotation = 0
  Scale = 0.1
  ScaleType = 0
  TheoreticalExact = false
  Type = 1
  UnderTolerance = 0
  X = 8.24101
  Y = -32.5462
FEATURE [TechDraw::DrawViewDimension] Dimension005
  AngleOverride = false
  Arbitrary = false
  ArbitraryTolerances = false
  BoxCorners = (2) [(-31.75,-35,0),(31.75,35,0)]
  EqualTolerance = true
  ExtensionAngle = 0
  FormatSpec = %.2w
  FormatSpecOverTolerance = %+.2w
  FormatSpecUnderTolerance = %+.2w
  Inverted = false
  LineAngle = 0
  LockPosition = false
  MeasureType = 1
  OverTolerance = 0
  References2D = -> [View002]
  Rotation = 0
  Scale = 0.1
  ScaleType = 0
  TheoreticalExact = false
  Type = 1
  UnderTolerance = 0
  X = 0
  Y = 28.4383
FEATURE [TechDraw::DrawViewDimension] Dimension006
  AngleOverride = false
  Arbitrary = false
  ArbitraryTolerances = false
  BoxCorners = (2) [(-31.75,-35,0),(31.75,35,0)]
  EqualTolerance = true
  ExtensionAngle = 0
  FormatSpec = %.2w
  FormatSpecOverTolerance = %+.2w
  FormatSpecUnderTolerance = %+.2w
  Inverted = false
  LineAngle = 0
  LockPosition = false
  MeasureType = 1
  OverTolerance = 0
  References2D = -> [View002]
  Rotation = 0
  Scale = 0.1
  ScaleType = 0
  TheoreticalExact = false
  Type = 2
  UnderTolerance = 0
  X = 17.069
  Y = 0
FEATURE [TechDraw::DrawViewDimension] Dimension007
  AngleOverride = false
  Arbitrary = false
  ArbitraryTolerances = false
  BoxCorners = (2) [(-16,-34.35,0),(16,34.35,0)]
  EqualTolerance = true
  ExtensionAngle = 0
  FormatSpec = %.2w
  FormatSpecOverTolerance = %+.2w
  FormatSpecUnderTolerance = %+.2w
  Inverted = false
  LineAngle = 0
  LockPosition = false
  MeasureType = 1
  OverTolerance = 0
  References2D = -> [View003]
  Rotation = 0
  Scale = 0.1
  ScaleType = 0
  TheoreticalExact = false
  Type = 2
  UnderTolerance = 0
  X = 5.32102
  Y = 0
FEATURE [TechDraw::DrawViewDimension] Dimension008
  AngleOverride = false
  Arbitrary = false
  ArbitraryTolerances = false
  BoxCorners = (2) [(-16,-34.35,0),(16,34.35,0)]
  EqualTolerance = true
  ExtensionAngle = 0
  FormatSpec = %.2w
  FormatSpecOverTolerance = %+.2w
  FormatSpecUnderTolerance = %+.2w
  Inverted = false
  LineAngle = 0
  LockPosition = false
  MeasureType = 1
  OverTolerance = 0
  References2D = -> [View003]
  Rotation = 0
  Scale = 0.1
  ScaleType = 0
  TheoreticalExact = false
  Type = 1
  UnderTolerance = 0
  X = 0
  Y = -20.426
FEATURE [TechDraw::DrawViewDimension] Dimension013
  AngleOverride = false
  Arbitrary = false
  ArbitraryTolerances = false
  BoxCorners = (2) [(-16,-21.3735,0),(16,21.3735,0)]
  EqualTolerance = true
  ExtensionAngle = 0
  FormatSpec = %.2w
  FormatSpecOverTolerance = %+.2w
  FormatSpecUnderTolerance = %+.2w
  Inverted = false
  LineAngle = 0
  LockPosition = false
  MeasureType = 1
  OverTolerance = 0
  References2D = -> [View004]
  Rotation = 0
  Scale = 0.1
  ScaleType = 0
  TheoreticalExact = false
  Type = 1
  UnderTolerance = 0
  X = -41.0727
  Y = 5.45329
FEATURE [TechDraw::DrawViewDimension] Dimension014
  AngleOverride = false
  Arbitrary = false
  ArbitraryTolerances = false
  BoxCorners = (2) [(-16,-21.3735,0),(16,21.3735,0)]
  EqualTolerance = true
  ExtensionAngle = 0
  FormatSpec = %.0w
  FormatSpecOverTolerance = %+.2w
  FormatSpecUnderTolerance = %+.2w
  Inverted = false
  LineAngle = 0
  LockPosition = false
  MeasureType = 1
  OverTolerance = 0
  References2D = -> [View004]
  Rotation = 0
  Scale = 0.1
  ScaleType = 0
  TheoreticalExact = false
  Type = 2
  UnderTolerance = 0
  X = -39.2453
  Y = -31.5495
FEATURE [TechDraw::DrawViewDimension] Dimension015
  AngleOverride = false
  Arbitrary = false
  ArbitraryTolerances = false
  BoxCorners = (2) [(-16,-21.3735,0),(16,21.3735,0)]
  EqualTolerance = true
  ExtensionAngle = 0
  FormatSpec = %.0w
  FormatSpecOverTolerance = %+.2w
  FormatSpecUnderTolerance = %+.2w
  Inverted = false
  LineAngle = 0
  LockPosition = false
  MeasureType = 1
  OverTolerance = 0
  References2D = -> [View004]
  Rotation = 0
  Scale = 0.1
  ScaleType = 0
  TheoreticalExact = false
  Type = 2
  UnderTolerance = 0
  X = -26.7795
  Y = -9.19157
FEATURE [TechDraw::DrawViewDimension] Dimension016
  AngleOverride = false
  Arbitrary = false
  ArbitraryTolerances = false
  BoxCorners = (2) [(-16,-21.3735,0),(16,21.3735,0)]
  EqualTolerance = true
  ExtensionAngle = 0
  FormatSpec = %.2w
  FormatSpecOverTolerance = %+.2w
  FormatSpecUnderTolerance = %+.2w
  Inverted = false
  LineAngle = 0
  LockPosition = false
  MeasureType = 1
  OverTolerance = 0
  References2D = -> [View004]
  Rotation = 0
  Scale = 0.1
  ScaleType = 0
  TheoreticalExact = false
  Type = 1
  UnderTolerance = 0
  X = -28.3615
  Y = 14.6531
FEATURE [TechDraw::DrawViewDimension] Dimension017
  AngleOverride = false
  Arbitrary = false
  ArbitraryTolerances = false
  BoxCorners = (2) [(-16,-21.3735,0),(16,21.3735,0)]
  EqualTolerance = true
  ExtensionAngle = 0
  FormatSpec = R%.0w
  FormatSpecOverTolerance = %+.2w
  FormatSpecUnderTolerance = %+.2w
  Inverted = false
  LineAngle = 0
  LockPosition = false
  MeasureType = 1
  OverTolerance = 0
  References2D = -> [View004]
  Rotation = 0
  Scale = 0.1
  ScaleType = 0
  TheoreticalExact = false
  Type = 4
  UnderTolerance = 0
  X = 6.96392
  Y = -3.79915
FEATURE [TechDraw::DrawViewDimension] Dimension018
  AngleOverride = false
  Arbitrary = false
  ArbitraryTolerances = false
  BoxCorners = (2) [(-16,-31.75,0),(16,31.75,0)]
  EqualTolerance = true
  ExtensionAngle = 0
  FormatSpec = %.2w
  FormatSpecOverTolerance = %+.2w
  FormatSpecUnderTolerance = %+.2w
  Inverted = false
  LineAngle = 0
  LockPosition = false
  MeasureType = 1
  OverTolerance = 0
  References2D = -> [View005]
  Rotation = 0
  Scale = 0.1
  ScaleType = 0
  TheoreticalExact = false
  Type = 2
  UnderTolerance = 0
  X = -26.1882
  Y = -42.9207
FEATURE [TechDraw::DrawViewDimension] Dimension019
  AngleOverride = false
  Arbitrary = false
  ArbitraryTolerances = false
  BoxCorners = (2) [(-16,-31.75,0),(16,31.75,0)]
  EqualTolerance = true
  ExtensionAngle = 0
  FormatSpec = %.2w
  FormatSpecOverTolerance = %+.2w
  FormatSpecUnderTolerance = %+.2w
  Inverted = false
  LineAngle = 0
  LockPosition = false
  MeasureType = 1
  OverTolerance = 0
  References2D = -> [View005]
  Rotation = 0
  Scale = 0.1
  ScaleType = 0
  TheoreticalExact = false
  Type = 1
  UnderTolerance = 0
  X = -30.9983
  Y = -19.7121
FEATURE [TechDraw::DrawViewBalloon] Balloon
  BubbleShape = 0
  EndType = 0
  EndTypeScale = 1
  KinkLength = 5
  LockPosition = false
  OriginX = 22.2232
  OriginY = -10.9673
  Rotation = 0
  Scale = 0.1
  ScaleType = 0
  ShapeScale = 1
  SourceView = -> ProjItem
  Text = A
  TextWrapLen = -1
  X = -168.944
  Y = 206.341
FEATURE [TechDraw::DrawViewBalloon] Balloon001
  BubbleShape = 0
  EndType = 0
  EndTypeScale = 1
  KinkLength = 5
  LockPosition = false
  OriginX = -5.21113
  OriginY = -7.66096
  Rotation = 0
  Scale = 0.1
  ScaleType = 0
  ShapeScale = 1
  SourceView = -> View002
  Text = A
  TextWrapLen = -1
  X = -161.762
  Y = 157.722
FEATURE [TechDraw::DrawViewBalloon] Balloon003
  BubbleShape = 0
  EndType = 0
  EndTypeScale = 1
  KinkLength = 5
  LockPosition = false
  OriginX = -60.1623
  OriginY = 120.42
  Rotation = 0
  Scale = 0.1
  ScaleType = 0
  ShapeScale = 1
  SourceView = -> View003
  Text = B
  TextWrapLen = -1
  X = 29.0647
  Y = 265.034
FEATURE [TechDraw::DrawViewBalloon] Balloon004
  BubbleShape = 0
  EndType = 0
  EndTypeScale = 1
  KinkLength = 5
  LockPosition = false
  OriginX = 32.5366
  OriginY = -165.408
  Rotation = 0
  Scale = 0.1
  ScaleType = 0
  ShapeScale = 1
  SourceView = -> View004
  Text = C
  TextWrapLen = -1
  X = -106.706
  Y = -169.646
FEATURE [TechDraw::DrawViewBalloon] Balloon005
  BubbleShape = 0
  EndType = 0
  EndTypeScale = 1
  KinkLength = 5
  LockPosition = false
  OriginX = -91.2013
  OriginY = 54.2872
  Rotation = 0
  Scale = 0.1
  ScaleType = 0
  ShapeScale = 1
  SourceView = -> View005
  Text = C
  TextWrapLen = -1
  X = 108.799
  Y = 254.287
FEATURE [Sketcher::SketchObject] Sketch042
  ArcFitTolerance = 1e-06
  AttachmentSupport = -> [YZ_Plane033]
  FullyConstrained = true
  MakeInternals = false
  MapMode = 5
  Placement = pos=(0,0,0) rot=(0.57735,0.57735,0.57735;2.0944rad)
  expr: Constraints[10] = <<bdim>>.f2s_w
  expr: Constraints[9] = <<bdim>>.f2s_h
  sketch-geometry (4):
    g0: LineSegment StartX=0 StartY=0 StartZ=0 EndX=194.331 EndY=0 EndZ=0
    g1: LineSegment StartX=194.331 StartY=0 StartZ=0 EndX=194.331 EndY=505.669 EndZ=0
    g2: LineSegment StartX=194.331 StartY=505.669 StartZ=0 EndX=0 EndY=505.669 EndZ=0
    g3: LineSegment StartX=0 StartY=505.669 StartZ=0 EndX=0 EndY=0 EndZ=0
  constraints (11):
    c: Coincident(g0,g1)
    c: Coincident(g1,g2)
    c: Coincident(g2,g3)
    c: Coincident(g3,g0)
    c: Horizontal(g0)
    c: Horizontal(g2)
    c: Vertical(g1)
    c: Vertical(g3)
    c: Coincident(g0,g-1)
    c: DistanceX(g2,g2) = 194.331
    c: DistanceY(g3,g3) = 505.669
FEATURE [PartDesign::Pad] Pad030
  Direction = (1,0,0)
  Length = 13
  Length2 = 10
  Placement = pos=(0,0,0) rot=(1,1,1;2.0944rad)
  Profile = -> Sketch042
  ReferenceAxis = -> Sketch042 [N_Axis]
  Suppressed = false
  Type = 0
  expr: Length = <<bdim>>.f2s_t
FEATURE [PartDesign::Body] Body032  label="fin 2 support"
  AllowCompound = false
  Group = -> [Sketch042,Pad030]
  Origin = -> Origin033
  Tip = -> Pad030
FEATURE [App::Link] fin_1_support  label="fin 1 support001"
  LinkPlacement = pos=(188,13,194.331) rot=(0,0,1;0rad)
  LinkedObject = -> Body032
  Placement = pos=(188,13,194.331) rot=(0,0,1;0rad)
FEATURE [App::Link] middle_brace_bar_side_panel_1  label="middle_brace_bar_side_panel_2"
  LinkPlacement = pos=(158,43,43) rot=(0,0,1;0rad)
  LinkedObject = -> Body031
  Placement = pos=(158,43,43) rot=(0,0,1;0rad)
FEATURE [App::FeaturePython] Joint052  label="Fixed040"  # Assembly joint (typed FeaturePython)
  Activated = true
  AngleMax = 0
  AngleMin = 0
  Detach1 = false
  Detach2 = false
  Distance = 0
  Distance2 = 0
  EnableAngleMax = false
  EnableAngleMin = false
  EnableLengthMax = false
  EnableLengthMin = false
  JointType = 0 (Fixed)
  LengthMax = 0
  LengthMin = 0
  Placement1 = pos=(-15,0,30) rot=(0.707107,0,0.707107;3.14159rad)
  Placement2 = pos=(15,0,0) rot=(0.707107,0,0.707107;3.14159rad)
  Reference1 = -> Assembly [brace_bar_back_panel_005.Edge12,brace_bar_back_panel_005.Edge12]
  Reference2 = -> Assembly [middle_brace_bar_side_panel_1.Edge3,middle_brace_bar_side_panel_1.Edge3]
FEATURE [PartDesign::Pad] Pad020
  Direction = (0,0,1)
  Length = 13
  Length2 = 10
  Profile = -> Sketch032
  ReferenceAxis = -> Sketch032 [N_Axis]
  Suppressed = false
  Type = 0
  expr: Length = <<bdim>>.fp_t
FEATURE [PartDesign::Body] Body021  label="front_panel"
  AllowCompound = false
  Group = -> [Sketch032,Pad020]
  Origin = -> Origin022
  Tip = -> Pad020
FEATURE [PartDesign::Pad] Pad018
  Direction = (0,-1,2e-16)
  Length = 13
  Length2 = 10
  Placement = pos=(0,0,0) rot=(1,0,0;1.5708rad)
  Profile = -> Sketch030
  ReferenceAxis = -> Sketch030 [N_Axis]
  Suppressed = false
  Type = 0
  expr: Length = <<bdim>>.f1_t
FEATURE [PartDesign::Body] Body019  label="fin_1_model"
  AllowCompound = false
  Group = -> [Sketch030,Pad018]
  Origin = -> Origin020
  Tip = -> Pad018
FEATURE [App::Link] middle_brace_bar_fin_2
  LinkPlacement = pos=(158,207.337,194.331) rot=(0,0,1;0rad)
  LinkedObject = -> Body030
  Placement = pos=(158,207.337,194.331) rot=(0,0,1;0rad)
FEATURE [App::FeaturePython] Joint054  label="Fixed042"  # Assembly joint (typed FeaturePython)
  Activated = true
  AngleMax = 0
  AngleMin = 0
  Detach1 = false
  Detach2 = false
  Distance = 0
  Distance2 = 0
  EnableAngleMax = false
  EnableAngleMin = false
  EnableLengthMax = false
  EnableLengthMin = false
  JointType = 0 (Fixed)
  LengthMax = 0
  LengthMin = 0
  Offset2 = pos=(0,0,0) rot=(0,0,1;3.14159rad)
  Placement1 = pos=(-1.421e-13,5.68e-14,505.669) rot=(0,1,0;3.14159rad)
  Placement2 = pos=(30,-30,657) rot=(0,0,1;3.14159rad)
  Reference1 = -> Assembly [fin_1_support.Edge11,fin_1_support.Vertex7]
  Reference2 = -> Assembly [middle_brace_bar_side_panel_1.Edge7,middle_brace_bar_side_panel_1.Vertex6]
FEATURE [Sketcher::SketchObject] Sketch043
  ArcFitTolerance = 1e-06
  AttachmentSupport = -> [YZ_Plane034]
  FullyConstrained = true
  MakeInternals = false
  MapMode = 5
  Placement = pos=(0,0,0) rot=(0.57735,0.57735,0.57735;2.0944rad)
  expr: Constraints[10] = <<bdim>>.f1s_w
  expr: Constraints[9] = <<bdim>>.f1s_h
  sketch-geometry (4):
    g0: LineSegment StartX=0 StartY=0 StartZ=0 EndX=194.331 EndY=0 EndZ=0
    g1: LineSegment StartX=194.331 StartY=0 StartZ=0 EndX=194.331 EndY=449.669 EndZ=0
    g2: LineSegment StartX=194.331 StartY=449.669 StartZ=0 EndX=0 EndY=449.669 EndZ=0
    g3: LineSegment StartX=0 StartY=449.669 StartZ=0 EndX=0 EndY=0 EndZ=0
  constraints (11):
    c: Coincident(g0,g1)
    c: Coincident(g1,g2)
    c: Coincident(g2,g3)
    c: Coincident(g3,g0)
    c: Horizontal(g0)
    c: Horizontal(g2)
    c: Vertical(g1)
    c: Vertical(g3)
    c: Coincident(g0,g-1)
    c: DistanceX(g2,g2) = 194.331
    c: DistanceY(g3,g3) = 449.669
FEATURE [PartDesign::Pad] Pad031
  Direction = (1,0,0)
  Length = 13
  Length2 = 10
  Placement = pos=(0,0,0) rot=(1,1,1;2.0944rad)
  Profile = -> Sketch043
  ReferenceAxis = -> Sketch043 [N_Axis]
  Suppressed = false
  Type = 0
  expr: Length = <<bdim>>.f1s_t
FEATURE [PartDesign::Body] Body033  label="fin 1 support"
  AllowCompound = false
  Group = -> [Sketch043,Pad031]
  Origin = -> Origin034
  Tip = -> Pad031
FEATURE [App::Link] fin_1_support001  label="fin 1 support002"
  LinkPlacement = pos=(188,427.669,43) rot=(0,0,1;0rad)
  LinkedObject = -> Body033
  Placement = pos=(188,427.669,43) rot=(0,0,1;0rad)
FEATURE [App::FeaturePython] Joint055  label="Fixed043"  # Assembly joint (typed FeaturePython)
  Activated = true
  AngleMax = 0
  AngleMin = 0
  Detach1 = false
  Detach2 = false
  Distance = 0
  Distance2 = 0
  EnableAngleMax = false
  EnableAngleMin = false
  EnableLengthMax = false
  EnableLengthMin = false
  JointType = 0 (Fixed)
  LengthMax = 0
  LengthMin = 0
  Offset2 = pos=(0,0,0) rot=(0,0,1;1.5708rad)
  Placement1 = pos=(30,224.834,-1.137e-13) rot=(0.57735,0.57735,0.57735;4.18879rad)
  Placement2 = pos=(-5.68e-14,5.68e-14,224.834) rot=(0.707107,0.707107,0;3.14159rad)
  Reference1 = -> Assembly [middle_brace_bar_fin_1.Edge4,middle_brace_bar_fin_1.Edge4]
  Reference2 = -> Assembly [fin_1_support001.Edge11,fin_1_support001.Edge11]
FEATURE [Sketcher::SketchObject] Sketch044
  ArcFitTolerance = 1e-06
  AttachmentSupport = -> [XZ_Plane035]
  FullyConstrained = true
  MakeInternals = false
  MapMode = 5
  Placement = pos=(0,0,0) rot=(1,0,0;1.5708rad)
  expr: Constraints[10] = <<bdim>>.mbbsp1_w
  expr: Constraints[9] = <<bdim>>.mbbsp1_h
  sketch-geometry (4):
    g0: LineSegment StartX=0 StartY=0 StartZ=0 EndX=30 EndY=0 EndZ=0
    g1: LineSegment StartX=30 StartY=0 StartZ=0 EndX=30 EndY=614 EndZ=0
    g2: LineSegment StartX=30 StartY=614 StartZ=0 EndX=0 EndY=614 EndZ=0
    g3: LineSegment StartX=0 StartY=614 StartZ=0 EndX=0 EndY=0 EndZ=0
  constraints (11):
    c: Coincident(g0,g1)
    c: Coincident(g1,g2)
    c: Coincident(g2,g3)
    c: Coincident(g3,g0)
    c: Horizontal(g0)
    c: Horizontal(g2)
    c: Vertical(g1)
    c: Vertical(g3)
    c: Coincident(g0,g-1)
    c: DistanceX(g2,g2) = 30
    c: DistanceY(g1,g1) = 614
FEATURE [PartDesign::Pad] Pad032
  AlongSketchNormal = false
  Direction = (0,-1,2e-16)
  Length = 30
  Length2 = 10
  Placement = pos=(0,0,0) rot=(1,0,0;1.5708rad)
  Profile = -> Sketch044
  ReferenceAxis = -> Sketch044 [N_Axis]
  Suppressed = false
  Type = 0
  expr: Length = <<bdim>>.mbbsp1_t
FEATURE [PartDesign::Body] Body034  label="middle_brace_bar_side_panel_1_model"
  AllowCompound = false
  Group = -> [Sketch044,Pad032]
  Origin = -> Origin035
  Tip = -> Pad032
FEATURE [App::Link] middle_brace_bar_side_panel_002  label="middle_brace_bar_side_panel_1"
  LinkPlacement = pos=(158,622,43) rot=(0,0,1;0rad)
  LinkedObject = -> Body034
  Placement = pos=(158,622,43) rot=(0,0,1;0rad)
FEATURE [App::FeaturePython] Joint056  label="Fixed044"  # Assembly joint (typed FeaturePython)
  Activated = true
  AngleMax = 0
  AngleMin = 0
  Detach1 = false
  Detach2 = false
  Distance = 0
  Distance2 = 0
  EnableAngleMax = false
  EnableAngleMin = false
  EnableLengthMax = false
  EnableLengthMin = false
  JointType = 0 (Fixed)
  LengthMax = 0
  LengthMin = 0
  Placement1 = pos=(30,0,0) rot=(0,0,1;0rad)
  Placement2 = pos=(0,194.331,-6.39e-14) rot=(0,0,1;0rad)
  Reference1 = -> Assembly [middle_brace_bar_side_panel_002.Edge6,middle_brace_bar_side_panel_002.Vertex3]
  Reference2 = -> Assembly [fin_1_support001.Edge6,fin_1_support001.Vertex3]
FEATURE [Sketcher::SketchObject] Sketch045
  ArcFitTolerance = 1e-06
  AttachmentSupport = -> [YZ_Plane036]
  FullyConstrained = true
  MakeInternals = false
  MapMode = 5
  Placement = pos=(0,0,0) rot=(0.57735,0.57735,0.57735;2.0944rad)
  expr: Constraints[10] = <<bdim>>.mbbf12_w
  expr: Constraints[9] = <<bdim>>.mbbf12_h
  sketch-geometry (4):
    g0: LineSegment StartX=0 StartY=0 StartZ=0 EndX=30 EndY=0 EndZ=0
    g1: LineSegment StartX=30 StartY=0 StartZ=0 EndX=30 EndY=285.337 EndZ=0
    g2: LineSegment StartX=30 StartY=285.337 StartZ=0 EndX=0 EndY=285.337 EndZ=0
    g3: LineSegment StartX=0 StartY=285.337 StartZ=0 EndX=0 EndY=0 EndZ=0
  constraints (11):
    c: Coincident(g0,g1)
    c: Coincident(g1,g2)
    c: Coincident(g2,g3)
    c: Coincident(g3,g0)
    c: Horizontal(g0)
    c: Horizontal(g2)
    c: Vertical(g1)
    c: Vertical(g3)
    c: Coincident(g0,g-1)
    c: DistanceX(g2,g2) = 30
    c: DistanceY(g1,g1) = 285.337
FEATURE [PartDesign::Pad] Pad033
  Direction = (1,0,0)
  Length = 30
  Length2 = 10
  Placement = pos=(0,0,0) rot=(1,1,1;2.0944rad)
  Profile = -> Sketch045
  ReferenceAxis = -> Sketch045 [N_Axis]
  Suppressed = false
  Type = 0
  expr: Length = <<bdim>>.mbbf12_t
FEATURE [PartDesign::Body] Body035  label="middle_brace_bar_fin_1and_2"
  AllowCompound = false
  Group = -> [Sketch045,Pad033]
  Origin = -> Origin036
  Tip = -> Pad033
FEATURE [App::Link] middle_brace_bar_fin_1and_2  label="middle_brace_bar_fin_1and_2_fin1"
  LinkPlacement = pos=(158,384.669,207.331) rot=(0,0,1;0rad)
  LinkedObject = -> Body035
  Placement = pos=(158,384.669,207.331) rot=(0,0,1;0rad)
FEATURE [Sketcher::SketchObject] Sketch046
  ArcFitTolerance = 1e-06
  AttachmentSupport = -> [YZ_Plane037]
  FullyConstrained = true
  MakeInternals = false
  MapMode = 5
  Placement = pos=(0,0,0) rot=(0.57735,0.57735,0.57735;2.0944rad)
  expr: Constraints[10] = <<bdim>>.f12s_w
  expr: Constraints[9] = <<bdim>>.f12s_h
  sketch-geometry (4):
    g0: LineSegment StartX=0 StartY=0 StartZ=0 EndX=194.331 EndY=0 EndZ=0
    g1: LineSegment StartX=194.331 StartY=0 StartZ=0 EndX=194.331 EndY=285.337 EndZ=0
    g2: LineSegment StartX=194.331 StartY=285.337 StartZ=0 EndX=0 EndY=285.337 EndZ=0
    g3: LineSegment StartX=0 StartY=285.337 StartZ=0 EndX=0 EndY=0 EndZ=0
  constraints (11):
    c: Coincident(g0,g1)
    c: Coincident(g1,g2)
    c: Coincident(g2,g3)
    c: Coincident(g3,g0)
    c: Horizontal(g0)
    c: Horizontal(g2)
    c: Vertical(g1)
    c: Vertical(g3)
    c: Coincident(g0,g-1)
    c: DistanceX(g2,g2) = 194.331
    c: DistanceY(g1,g1) = 285.337
FEATURE [PartDesign::Pad] Pad034
  Direction = (1,0,0)
  Length = 13
  Length2 = 10
  Placement = pos=(0,0,0) rot=(1,1,1;2.0944rad)
  Profile = -> Sketch046
  ReferenceAxis = -> Sketch046 [N_Axis]
  Suppressed = false
  Type = 0
  expr: Length = <<bdim>>.f12s_t
FEATURE [PartDesign::Body] Body036  label="fin_support_1and2"
  AllowCompound = false
  Group = -> [Sketch046,Pad034]
  Origin = -> Origin037
  Placement = pos=(201,220.337,492.669) rot=(0,1,0;3.14159rad)
  Tip = -> Pad034
FEATURE [App::Link] middle_brace_bar_fin_1and_003  label="middle_brace_bar_fin_1and_2_fin2"
  LinkPlacement = pos=(188,220.337,492.669) rot=(0,1,0;3.14159rad)
  LinkedObject = -> Body035
  Placement = pos=(188,220.337,492.669) rot=(0,1,0;3.14159rad)
FEATURE [Sketcher::SketchObject] Sketch047
  ArcFitTolerance = 1e-06
  AttachmentSupport = -> [XY_Plane038]
  FullyConstrained = true
  MakeInternals = false
  MapMode = 5
  expr: Constraints[10] = <<bdim>>.pA_h
  expr: Constraints[9] = <<bdim>>.pA_w
  sketch-geometry (4):
    g0: LineSegment StartX=0 StartY=0 StartZ=0 EndX=635 EndY=0 EndZ=0
    g1: LineSegment StartX=635 StartY=0 StartZ=0 EndX=635 EndY=1187 EndZ=0
    g2: LineSegment StartX=635 StartY=1187 StartZ=0 EndX=0 EndY=1187 EndZ=0
    g3: LineSegment StartX=0 StartY=1187 StartZ=0 EndX=0 EndY=0 EndZ=0
  constraints (11):
    c: Coincident(g0,g1)
    c: Coincident(g1,g2)
    c: Coincident(g2,g3)
    c: Coincident(g3,g0)
    c: Horizontal(g0)
    c: Horizontal(g2)
    c: Vertical(g1)
    c: Vertical(g3)
    c: Coincident(g0,g-1)
    c: DistanceY(g3,g3) = 1187
    c: DistanceX(g0,g0) = 635
FEATURE [PartDesign::Pad] Pad035
  Direction = (0,0,1)
  Length = 13
  Length2 = 10
  Profile = -> Sketch047
  ReferenceAxis = -> Sketch047 [N_Axis]
  Suppressed = false
  Type = 0
  expr: Length = <<bdim>>.pA_t
FEATURE [PartDesign::Body] Body037  label="panel_A"
  AllowCompound = false
  Group = -> [Sketch047,Pad035]
  Origin = -> Origin038
  Tip = -> Pad035
FEATURE [Sketcher::SketchObject] Sketch048
  ArcFitTolerance = 1e-06
  AttachmentSupport = -> [XY_Plane039]
  FullyConstrained = true
  MakeInternals = false
  MapMode = 5
  expr: Constraints[10] = <<bdim>>.pB_h
  expr: Constraints[9] = <<bdim>>.pB_w
  sketch-geometry (4):
    g0: LineSegment StartX=0 StartY=0 StartZ=0 EndX=320 EndY=0 EndZ=0
    g1: LineSegment StartX=320 StartY=0 StartZ=0 EndX=320 EndY=1115 EndZ=0
    g2: LineSegment StartX=320 StartY=1115 StartZ=0 EndX=0 EndY=1115 EndZ=0
    g3: LineSegment StartX=0 StartY=1115 StartZ=0 EndX=0 EndY=0 EndZ=0
  constraints (11):
    c: Coincident(g0,g1)
    c: Coincident(g1,g2)
    c: Coincident(g2,g3)
    c: Coincident(g3,g0)
    c: Horizontal(g0)
    c: Horizontal(g2)
    c: Vertical(g1)
    c: Vertical(g3)
    c: Coincident(g0,g-1)
    c: DistanceY(g3,g3) = 1115
    c: DistanceX(g0,g0) = 320
FEATURE [PartDesign::Pad] Pad036
  Direction = (0,0,1)
  Length = 13
  Length2 = 10
  Profile = -> Sketch048
  ReferenceAxis = -> Sketch048 [N_Axis]
  Suppressed = false
  Type = 0
  expr: Length = <<bdim>>.pB_t
FEATURE [PartDesign::Body] Body038  label="panel_B"
  AllowCompound = false
  Group = -> [Sketch048,Pad036]
  Origin = -> Origin039
  Tip = -> Pad036
FEATURE [Sketcher::SketchObject] Sketch049
  ArcFitTolerance = 1e-06
  AttachmentSupport = -> [XY_Plane040]
  FullyConstrained = true
  MakeInternals = false
  MapMode = 5
  expr: Constraints[10] = <<bdim>>.pC_h
  expr: Constraints[9] = <<bdim>>.pC_w
  sketch-geometry (4):
    g0: LineSegment StartX=0 StartY=0 StartZ=0 EndX=320 EndY=0 EndZ=0
    g1: LineSegment StartX=320 StartY=0 StartZ=0 EndX=320 EndY=635 EndZ=0
    g2: LineSegment StartX=320 StartY=635 StartZ=0 EndX=0 EndY=635 EndZ=0
    g3: LineSegment StartX=0 StartY=635 StartZ=0 EndX=0 EndY=0 EndZ=0
  constraints (11):
    c: Coincident(g0,g1)
    c: Coincident(g1,g2)
    c: Coincident(g2,g3)
    c: Coincident(g3,g0)
    c: Horizontal(g0)
    c: Horizontal(g2)
    c: Vertical(g1)
    c: Vertical(g3)
    c: Coincident(g0,g-1)
    c: DistanceY(g3,g3) = 635
    c: DistanceX(g0,g0) = 320
FEATURE [PartDesign::Pad] Pad037
  Direction = (0,0,1)
  Length = 13
  Length2 = 10
  Profile = -> Sketch049
  ReferenceAxis = -> Sketch049 [N_Axis]
  Suppressed = false
  Type = 0
  expr: Length = <<bdim>>.pC_t
FEATURE [PartDesign::Body] Body039  label="panel_C"
  AllowCompound = false
  Group = -> [Sketch049,Pad037]
  Origin = -> Origin040
  Tip = -> Pad037
FEATURE [TechDraw::DrawSVGTemplate] Template001
  Height = 210
  Orientation = 1
  Template = <path>
  Width = 297
FEATURE [TechDraw::DrawProjGroupItem] View008  label="Pannel A 1"
  CoarseView = false
  Direction = (0,0,-1)
  Focus = 100
  HardHidden = false
  IsoCount = 0
  IsoHidden = false
  IsoVisible = false
  LockPosition = false
  Perspective = false
  Rotation = 0
  RotationVector = (1,0,0)
  Scale = 0.2
  ScaleType = 0
  ScrubCount = 1
  SeamHidden = false
  SeamVisible = true
  SmoothHidden = false
  SmoothVisible = true
  Source = -> [Body037]
  Type = 0
  X = 148.464
  XDirection = (1e-16,-1,0)
  Y = 116.148
FEATURE [TechDraw::DrawProjGroupItem] View009
  CoarseView = false
  Direction = (-1,-1e-16,0)
  Focus = 100
  HardHidden = false
  IsoCount = 0
  IsoHidden = false
  IsoVisible = false
  LockPosition = false
  Perspective = false
  Rotation = 0
  RotationVector = (1,0,0)
  Scale = 0.2
  ScaleType = 0
  ScrubCount = 1
  SeamHidden = false
  SeamVisible = true
  SmoothHidden = false
  SmoothVisible = true
  Type = 0
  X = 99.7776
  XDirection = (0,-1e-16,1)
  XSource = -> [bottom_panel]
  Y = 116.148
FEATURE [TechDraw::DrawProjGroupItem] View010
  CoarseView = false
  Direction = (-1,1e-16,0)
  Focus = 100
  HardHidden = false
  IsoCount = 0
  IsoHidden = false
  IsoVisible = false
  LockPosition = false
  Perspective = false
  Rotation = 0
  RotationVector = (1,0,0)
  Scale = 0.2
  ScaleType = 0
  ScrubCount = 1
  SeamHidden = false
  SeamVisible = true
  SmoothHidden = false
  SmoothVisible = true
  Type = 0
  X = 190.442
  XDirection = (1e-16,1,0)
  XSource = -> [fin_1_support]
  Y = 101.911
FEATURE [TechDraw::DrawViewBalloon] Balloon009
  BubbleShape = 0
  EndType = 0
  EndTypeScale = 1
  KinkLength = 5
  LockPosition = false
  OriginX = 35.1354
  OriginY = 81.0982
  Rotation = 0
  Scale = 0.2
  ScaleType = 0
  ShapeScale = 1
  SourceView = -> View010
  Text = P9
  TextWrapLen = -1
  X = 158.007
  Y = -418.465
FEATURE [TechDraw::DrawViewBalloon] Balloon010
  BubbleShape = 0
  EndType = 0
  EndTypeScale = 1
  KinkLength = 5
  LockPosition = false
  OriginX = 90.8733
  OriginY = 128.282
  Rotation = 0
  Scale = 0.2
  ScaleType = 0
  ShapeScale = 1
  SourceView = -> View009
  Text = P1
  TextWrapLen = -1
  X = 213.745
  Y = 241.351
FEATURE [TechDraw::DrawProjGroupItem] View011
  CoarseView = false
  Direction = (-1,-1e-16,0)
  Focus = 100
  HardHidden = false
  IsoCount = 0
  IsoHidden = false
  IsoVisible = false
  LockPosition = false
  Perspective = false
  Rotation = 0
  RotationVector = (1,0,0)
  Scale = 0.2
  ScaleType = 0
  ScrubCount = 1
  SeamHidden = false
  SeamVisible = true
  SmoothHidden = false
  SmoothVisible = true
  Type = 0
  X = 231.114
  XDirection = (1e-16,-1,0)
  XSource = -> [fin_1_support001]
  Y = 97.5628
FEATURE [TechDraw::DrawViewBalloon] Balloon011
  BubbleShape = 0
  EndType = 0
  EndTypeScale = 1
  KinkLength = 5
  LockPosition = false
  OriginX = -16.7112
  OriginY = 106.904
  Rotation = 0
  Scale = 0.2
  ScaleType = 0
  ShapeScale = 1
  SourceView = -> View011
  Text = P10
  TextWrapLen = -1
  X = 71.0805
  Y = 482.463
FEATURE [TechDraw::DrawViewAnnotation] Annotation
  Font = osifont
  LineSpace = 100
  LockPosition = false
  MaxWidth = -1
  Rotation = 0
  Scale = 0.2
  ScaleType = 0
  Text = Plan de coupe: Panneau A1 | Dimensions en mm | Échelle 1 pour 5
  TextSize = 5
  TextStyle = 0
  X = 45.1095
  Y = 17.7308
FEATURE [TechDraw::DrawViewDimension] Dimension020
  AngleOverride = false
  Arbitrary = false
  ArbitraryTolerances = false
  BoxCorners = (2) [(-118.7,-63.5,0),(118.7,63.5,0)]
  EqualTolerance = true
  ExtensionAngle = 0
  FormatSpec = %.2w
  FormatSpecOverTolerance = %+.2w
  FormatSpecUnderTolerance = %+.2w
  Inverted = false
  LineAngle = 0
  LockPosition = false
  MeasureType = 1
  OverTolerance = 0
  References2D = -> [View008]
  Rotation = 0
  Scale = 0.2
  ScaleType = 0
  TheoreticalExact = false
  Type = 1
  UnderTolerance = 0
  X = -4.79125
  Y = 75.9247
FEATURE [TechDraw::DrawViewDimension] Dimension021
  AngleOverride = false
  Arbitrary = false
  ArbitraryTolerances = false
  BoxCorners = (2) [(-118.7,-63.5,0),(118.7,63.5,0)]
  EqualTolerance = true
  ExtensionAngle = 0
  FormatSpec = %.2w
  FormatSpecOverTolerance = %+.2w
  FormatSpecUnderTolerance = %+.2w
  Inverted = false
  LineAngle = 0
  LockPosition = false
  MeasureType = 1
  OverTolerance = 0
  References2D = -> [View008]
  Rotation = 0
  Scale = 0.2
  ScaleType = 0
  TheoreticalExact = false
  Type = 2
  UnderTolerance = 0
  X = 128.967
  Y = 0
FEATURE [TechDraw::DrawViewDimension] Dimension022
  AngleOverride = false
  Arbitrary = false
  ArbitraryTolerances = false
  BoxCorners = (2) [(-70,-63.5,0),(70,63.5,0)]
  EqualTolerance = true
  ExtensionAngle = 0
  FormatSpec = %.2w
  FormatSpecOverTolerance = %+.2w
  FormatSpecUnderTolerance = %+.2w
  Inverted = false
  LineAngle = 0
  LockPosition = false
  MeasureType = 1
  OverTolerance = 0
  References2D = -> [View009]
  Rotation = 0
  Scale = 0.2
  ScaleType = 0
  TheoreticalExact = false
  Type = 1
  UnderTolerance = 0
  X = 0
  Y = 57.7864
FEATURE [TechDraw::DrawViewDimension] Dimension023
  AngleOverride = false
  Arbitrary = false
  ArbitraryTolerances = false
  BoxCorners = (2) [(-70,-63.5,0),(70,63.5,0)]
  EqualTolerance = true
  ExtensionAngle = 0
  FormatSpec = %.2w
  FormatSpecOverTolerance = %+.2w
  FormatSpecUnderTolerance = %+.2w
  Inverted = false
  LineAngle = 0
  LockPosition = false
  MeasureType = 1
  OverTolerance = 0
  References2D = -> [View009]
  Rotation = 0
  Scale = 0.2
  ScaleType = 0
  TheoreticalExact = false
  Type = 2
  UnderTolerance = 0
  X = -49.1238
  Y = 0
FEATURE [TechDraw::DrawViewDimension] Dimension024
  AngleOverride = false
  Arbitrary = false
  ArbitraryTolerances = false
  BoxCorners = (2) [(-19.4331,-49.2669,0),(19.4331,49.2669,0)]
  EqualTolerance = true
  ExtensionAngle = 0
  FormatSpec = %.0w
  FormatSpecOverTolerance = %+.2w
  FormatSpecUnderTolerance = %+.2w
  Inverted = false
  LineAngle = 0
  LockPosition = false
  MeasureType = 1
  OverTolerance = 0
  References2D = -> [View010]
  Rotation = 0
  Scale = 0.2
  ScaleType = 0
  TheoreticalExact = false
  Type = 1
  UnderTolerance = 0
  X = 0
  Y = 39.4465
FEATURE [TechDraw::DrawViewDimension] Dimension025
  AngleOverride = false
  Arbitrary = false
  ArbitraryTolerances = false
  BoxCorners = (2) [(-19.4331,-49.2669,0),(19.4331,49.2669,0)]
  EqualTolerance = true
  ExtensionAngle = 0
  FormatSpec = %.0w
  FormatSpecOverTolerance = %+.2w
  FormatSpecUnderTolerance = %+.2w
  Inverted = false
  LineAngle = 0
  LockPosition = false
  MeasureType = 1
  OverTolerance = 0
  References2D = -> [View010]
  Rotation = 0
  Scale = 0.2
  ScaleType = 0
  TheoreticalExact = false
  Type = 2
  UnderTolerance = 0
  X = -10.3228
  Y = 0
FEATURE [TechDraw::DrawViewDimension] Dimension026
  AngleOverride = false
  Arbitrary = false
  ArbitraryTolerances = false
  BoxCorners = (2) [(-19.4331,-44.9669,0),(19.4331,44.9669,0)]
  EqualTolerance = true
  ExtensionAngle = 0
  FormatSpec = %.0w
  FormatSpecOverTolerance = %+.2w
  FormatSpecUnderTolerance = %+.2w
  Inverted = false
  LineAngle = 0
  LockPosition = false
  MeasureType = 1
  OverTolerance = 0
  References2D = -> [View011]
  Rotation = 0
  Scale = 0.2
  ScaleType = 0
  TheoreticalExact = false
  Type = 1
  UnderTolerance = 0
  X = 0
  Y = -27.4211
FEATURE [TechDraw::DrawViewDimension] Dimension027
  AngleOverride = false
  Arbitrary = false
  ArbitraryTolerances = false
  BoxCorners = (2) [(-19.4331,-44.9669,0),(19.4331,44.9669,0)]
  EqualTolerance = true
  ExtensionAngle = 0
  FormatSpec = %.0w
  FormatSpecOverTolerance = %+.2w
  FormatSpecUnderTolerance = %+.2w
  Inverted = false
  LineAngle = 0
  LockPosition = false
  MeasureType = 1
  OverTolerance = 0
  References2D = -> [View011]
  Rotation = 0
  Scale = 0.2
  ScaleType = 0
  TheoreticalExact = false
  Type = 2
  UnderTolerance = 0
  X = 7.05495
  Y = 0
FEATURE [TechDraw::DrawPage] Page001  label="panel_A1_cuts"
  KeepUpdated = true
  NextBalloonIndex = 4
  ProjectionType = 0
  Scale = 0.2
  Template = -> Template001
  Views = -> [View008,View009,View010,Balloon009,Balloon010,View011,Balloon011,Annotation,Dimension020,Dimension021,Dimension022,Dimension023,Dimension024,Dimension025,Dimension026,Dimension027]
FEATURE [TechDraw::DrawSVGTemplate] Template002
  Height = 210
  Orientation = 1
  Template = <path>
  Width = 297
FEATURE [TechDraw::DrawProjGroupItem] View012  label="Pannel A 2"
  CoarseView = false
  Direction = (0,0,-1)
  Focus = 100
  HardHidden = false
  IsoCount = 0
  IsoHidden = false
  IsoVisible = false
  LockPosition = false
  Perspective = false
  Rotation = 0
  RotationVector = (1,0,0)
  Scale = 0.2
  ScaleType = 0
  ScrubCount = 1
  SeamHidden = false
  SeamVisible = true
  SmoothHidden = false
  SmoothVisible = true
  Source = -> [Body037]
  Type = 0
  X = 148.5
  XDirection = (1e-16,-1,0)
  Y = 105
FEATURE [TechDraw::DrawProjGroupItem] View013
  CoarseView = false
  Direction = (-1,-1e-16,0)
  Focus = 100
  HardHidden = false
  IsoCount = 0
  IsoHidden = false
  IsoVisible = false
  LockPosition = false
  Perspective = false
  Rotation = 0
  RotationVector = (1,0,0)
  Scale = 0.2
  ScaleType = 0
  ScrubCount = 1
  SeamHidden = false
  SeamVisible = true
  SmoothHidden = false
  SmoothVisible = true
  Type = 0
  X = 99.7844
  XDirection = (0,-1e-16,1)
  XSource = -> [top_panel]
  Y = 105
FEATURE [TechDraw::DrawProjGroupItem] View014
  CoarseView = false
  Direction = (-1,-1e-16,0)
  Focus = 100
  HardHidden = false
  IsoCount = 0
  IsoHidden = false
  IsoVisible = false
  LockPosition = false
  Perspective = false
  Rotation = 0
  RotationVector = (1,0,0)
  Scale = 0.2
  ScaleType = 0
  ScrubCount = 1
  SeamHidden = false
  SeamVisible = true
  SmoothHidden = false
  SmoothVisible = true
  Source = -> [Body036]
  Type = 0
  X = 190.556
  XDirection = (1e-16,-1,0)
  Y = 140.32
FEATURE [TechDraw::DrawViewBalloon] Balloon012
  BubbleShape = 0
  EndType = 0
  EndTypeScale = 1
  KinkLength = 5
  LockPosition = false
  OriginX = 128.317
  OriginY = -26.0595
  Rotation = 0
  Scale = 0.2
  ScaleType = 0
  ShapeScale = 1
  SourceView = -> View013
  Text = P2
  TextWrapLen = -1
  X = 228.317
  Y = 73.9405
FEATURE [TechDraw::DrawViewBalloon] Balloon013
  BubbleShape = 0
  EndType = 0
  EndTypeScale = 1
  KinkLength = 5
  LockPosition = false
  OriginX = 16.5907
  OriginY = 21.3529
  Rotation = 0
  Scale = 0.2
  ScaleType = 0
  ShapeScale = 1
  SourceView = -> View014
  Text = P11
  TextWrapLen = -1
  X = -39.2609
  Y = 102.171
FEATURE [TechDraw::DrawViewAnnotation] Annotation001
  Font = osifont
  LineSpace = 100
  LockPosition = false
  MaxWidth = -1
  Rotation = 0
  Scale = 0.2
  ScaleType = 0
  Text = Plan de coupe: Panneau A2 | Dimensions en mm | Échelle 1 pour 5
  TextSize = 5
  TextStyle = 0
  X = 41.8511
  Y = 16.1016
FEATURE [TechDraw::DrawViewDimension] Dimension028
  AngleOverride = false
  Arbitrary = false
  ArbitraryTolerances = false
  BoxCorners = (2) [(-70,-63.5,0),(70,63.5,0)]
  EqualTolerance = true
  ExtensionAngle = 0
  FormatSpec = %.2w
  FormatSpecOverTolerance = %+.2w
  FormatSpecUnderTolerance = %+.2w
  Inverted = false
  LineAngle = 0
  LockPosition = false
  MeasureType = 1
  OverTolerance = 0
  References2D = -> [View013]
  Rotation = 0
  Scale = 0.2
  ScaleType = 0
  TheoreticalExact = false
  Type = 1
  UnderTolerance = 0
  X = 0
  Y = -40.2278
FEATURE [TechDraw::DrawViewDimension] Dimension029
  AngleOverride = false
  Arbitrary = false
  ArbitraryTolerances = false
  BoxCorners = (2) [(-70,-63.5,0),(70,63.5,0)]
  EqualTolerance = true
  ExtensionAngle = 0
  FormatSpec = %.2w
  FormatSpecOverTolerance = %+.2w
  FormatSpecUnderTolerance = %+.2w
  Inverted = false
  LineAngle = 0
  LockPosition = false
  MeasureType = 1
  OverTolerance = 0
  References2D = -> [View013]
  Rotation = 0
  Scale = 0.2
  ScaleType = 0
  TheoreticalExact = false
  Type = 2
  UnderTolerance = 0
  X = -32.1213
  Y = 0
FEATURE [TechDraw::DrawViewDimension] Dimension030
  AngleOverride = false
  Arbitrary = false
  ArbitraryTolerances = false
  BoxCorners = (2) [(-19.4331,-28.5337,0),(19.4331,28.5337,0)]
  EqualTolerance = true
  ExtensionAngle = 0
  FormatSpec = %.0w
  FormatSpecOverTolerance = %+.2w
  FormatSpecUnderTolerance = %+.2w
  Inverted = false
  LineAngle = 0
  LockPosition = false
  MeasureType = 1
  OverTolerance = 0
  References2D = -> [View014]
  Rotation = 0
  Scale = 0.2
  ScaleType = 0
  TheoreticalExact = false
  Type = 1
  UnderTolerance = 0
  X = 0
  Y = -15.8513
FEATURE [TechDraw::DrawViewDimension] Dimension031
  AngleOverride = false
  Arbitrary = false
  ArbitraryTolerances = false
  BoxCorners = (2) [(-19.4331,-28.5337,0),(19.4331,28.5337,0)]
  EqualTolerance = true
  ExtensionAngle = 0
  FormatSpec = %.0w
  FormatSpecOverTolerance = %+.2w
  FormatSpecUnderTolerance = %+.2w
  Inverted = false
  LineAngle = 0
  LockPosition = false
  MeasureType = 1
  OverTolerance = 0
  References2D = -> [View014]
  Rotation = 0
  Scale = 0.2
  ScaleType = 0
  TheoreticalExact = false
  Type = 2
  UnderTolerance = 0
  X = 37.3074
  Y = -15.5173
FEATURE [TechDraw::DrawSVGTemplate] Template003
  Height = 210
  Orientation = 1
  Template = <path>
  Width = 297
FEATURE [TechDraw::DrawProjGroupItem] View015  label="Pannel B1"
  CoarseView = false
  Direction = (0,0,-1)
  Focus = 100
  HardHidden = false
  IsoCount = 0
  IsoHidden = false
  IsoVisible = false
  LockPosition = false
  Perspective = false
  Rotation = 0
  RotationVector = (1,0,0)
  Scale = 0.2
  ScaleType = 0
  ScrubCount = 1
  SeamHidden = false
  SeamVisible = true
  SmoothHidden = false
  SmoothVisible = true
  Source = -> [Body038]
  Type = 0
  X = 148.5
  XDirection = (1e-16,-1,0)
  Y = 105
FEATURE [TechDraw::DrawProjGroupItem] View016
  CoarseView = false
  Direction = (0,-1,0)
  Focus = 100
  HardHidden = false
  IsoCount = 0
  IsoHidden = false
  IsoVisible = false
  LockPosition = false
  Perspective = false
  Rotation = 0
  RotationVector = (1,0,0)
  Scale = 0.2
  ScaleType = 0
  ScrubCount = 1
  SeamHidden = false
  SeamVisible = true
  SmoothHidden = false
  SmoothVisible = true
  Source = -> [Body019]
  Type = 0
  X = 220.263
  XDirection = (1e-16,0,1)
  Y = 105
FEATURE [TechDraw::DrawViewDimension] Dimension032
  AngleOverride = false
  Arbitrary = false
  ArbitraryTolerances = false
  BoxCorners = (2) [(-118.7,-32,0),(118.7,32,0)]
  EqualTolerance = true
  ExtensionAngle = 0
  FormatSpec = %.2w
  FormatSpecOverTolerance = %+.2w
  FormatSpecUnderTolerance = %+.2w
  Inverted = false
  LineAngle = 0
  LockPosition = false
  MeasureType = 1
  OverTolerance = 0
  References2D = -> [View015]
  Rotation = 0
  Scale = 0.2
  ScaleType = 0
  TheoreticalExact = false
  Type = 1
  UnderTolerance = 0
  X = 0
  Y = -67.6622
FEATURE [TechDraw::DrawViewDimension] Dimension035
  AngleOverride = false
  Arbitrary = false
  ArbitraryTolerances = false
  BoxCorners = (2) [(-47.9669,-32,0),(47.9669,32,0)]
  EqualTolerance = true
  ExtensionAngle = 0
  FormatSpec = %.0w
  FormatSpecOverTolerance = %+.2w
  FormatSpecUnderTolerance = %+.2w
  Inverted = false
  LineAngle = 0
  LockPosition = false
  MeasureType = 1
  OverTolerance = 0
  References2D = -> [View016]
  Rotation = 0
  Scale = 0.2
  ScaleType = 0
  TheoreticalExact = false
  Type = 1
  UnderTolerance = 0
  X = 0
  Y = -19.4334
FEATURE [TechDraw::DrawViewAnnotation] Annotation002
  Font = osifont
  LineSpace = 100
  LockPosition = false
  MaxWidth = -1
  Rotation = 0
  Scale = 0.2
  ScaleType = 0
  Text = Plan de coupe: Panneau B1 | Dimensions en mm | Échelle 1 pour 5
  TextSize = 5
  TextStyle = 0
  X = 41.8511
  Y = 16.1016
FEATURE [TechDraw::DrawSVGTemplate] Template004
  Height = 210
  Orientation = 1
  Template = <path>
  Width = 297
FEATURE [TechDraw::DrawProjGroupItem] View018  label="Pannel B2"
  CoarseView = false
  Direction = (0,0,-1)
  Focus = 100
  HardHidden = false
  IsoCount = 0
  IsoHidden = false
  IsoVisible = false
  LockPosition = false
  Perspective = false
  Rotation = 0
  RotationVector = (1,0,0)
  Scale = 0.2
  ScaleType = 0
  ScrubCount = 1
  SeamHidden = false
  SeamVisible = true
  SmoothHidden = false
  SmoothVisible = true
  Source = -> [Body038]
  Type = 0
  X = 148.5
  XDirection = (1e-16,-1,0)
  Y = 105
FEATURE [TechDraw::DrawViewDimension] Dimension038
  AngleOverride = false
  Arbitrary = false
  ArbitraryTolerances = false
  BoxCorners = (2) [(-118.7,-32,0),(118.7,32,0)]
  EqualTolerance = true
  ExtensionAngle = 0
  FormatSpec = %.2w
  FormatSpecOverTolerance = %+.2w
  FormatSpecUnderTolerance = %+.2w
  Inverted = false
  LineAngle = 0
  LockPosition = false
  MeasureType = 1
  OverTolerance = 0
  References2D = -> [View018]
  Rotation = 0
  Scale = 0.2
  ScaleType = 0
  TheoreticalExact = false
  Type = 1
  UnderTolerance = 0
  X = 0
  Y = 46.0596
FEATURE [TechDraw::DrawViewDimension] Dimension039
  AngleOverride = false
  Arbitrary = false
  ArbitraryTolerances = false
  BoxCorners = (2) [(-118.7,-32,0),(118.7,32,0)]
  EqualTolerance = true
  ExtensionAngle = 0
  FormatSpec = %.2w
  FormatSpecOverTolerance = %+.2w
  FormatSpecUnderTolerance = %+.2w
  Inverted = false
  LineAngle = 0
  LockPosition = false
  MeasureType = 1
  OverTolerance = 0
  References2D = -> [View018]
  Rotation = 0
  Scale = 0.2
  ScaleType = 0
  TheoreticalExact = false
  Type = 2
  UnderTolerance = 0
  X = 132.737
  Y = -3.02752
FEATURE [TechDraw::DrawViewAnnotation] Annotation003
  Font = osifont
  LineSpace = 100
  LockPosition = false
  MaxWidth = -1
  Rotation = 0
  Scale = 0.2
  ScaleType = 0
  Text = Plan de coupe: Panneau B2 | Dimensions en mm | Échelle 1 pour 5 | Même pour panneaux prime '
  TextSize = 5
  TextStyle = 0
  X = 42.1383
  Y = 28.1637
FEATURE [TechDraw::DrawProjGroupItem] View021  label="P3 (devant)"
  Caption = P3 (devant)
  CoarseView = false
  Direction = (0,-1,0)
  Focus = 100
  HardHidden = false
  IsoCount = 0
  IsoHidden = false
  IsoVisible = false
  LockPosition = true
  Perspective = false
  Rotation = 0
  RotationVector = (1,0,0)
  Scale = 0.1
  ScaleType = 2
  ScrubCount = 1
  SeamHidden = false
  SeamVisible = true
  SmoothHidden = false
  SmoothVisible = true
  Type = 0
  X = 0
  XDirection = (1,0,0)
  XSource = -> [side_panel_001]
  Y = 0
FEATURE [TechDraw::DrawProjGroupItem] ProjItem008  label="P3 (côté)"
  Caption = P3 (côté)
  CoarseView = false
  Direction = (1,-1e-16,0)
  Focus = 100
  HardHidden = false
  IsoCount = 0
  IsoHidden = false
  IsoVisible = false
  LockPosition = false
  Perspective = false
  Rotation = 0
  RotationVector = (1,0,0)
  ScaleType = 2
  ScrubCount = 1
  SeamHidden = false
  SeamVisible = true
  SmoothHidden = false
  SmoothVisible = true
  Type = 2
  X = -31.65
  XDirection = (1e-16,1,0)
  XSource = -> [side_panel_001]
  Y = 0
FEATURE [TechDraw::DrawProjGroup] ProjGroup008
  Anchor = -> View021
  AutoDistribute = true
  LockPosition = false
  ProjectionType = 0
  Rotation = 0
  Scale = 0.1
  ScaleType = 0
  Views = -> [View021,ProjItem008]
  X = 147.252
  XSource = -> [side_panel_001]
  Y = 176.73
  spacingX = 15
  spacingY = 15
FEATURE [TechDraw::DrawViewDimension] Dimension041
  AngleOverride = false
  Arbitrary = false
  ArbitraryTolerances = false
  BoxCorners = (2) [(-16,-33.7,0),(16,33.7,0)]
  EqualTolerance = true
  ExtensionAngle = 0
  FormatSpec = %.2w
  FormatSpecOverTolerance = %+.2w
  FormatSpecUnderTolerance = %+.2w
  Inverted = false
  LineAngle = 0
  LockPosition = false
  MeasureType = 1
  OverTolerance = 0
  References2D = -> [View021]
  Rotation = 0
  Scale = 0.1
  ScaleType = 0
  TheoreticalExact = false
  Type = 1
  UnderTolerance = 0
  X = 0
  Y = -24.2906
FEATURE [TechDraw::DrawViewDimension] Dimension042
  AngleOverride = false
  Arbitrary = false
  ArbitraryTolerances = false
  BoxCorners = (2) [(-16,-33.7,0),(16,33.7,0)]
  EqualTolerance = true
  ExtensionAngle = 0
  FormatSpec = %.2w
  FormatSpecOverTolerance = %+.2w
  FormatSpecUnderTolerance = %+.2w
  Inverted = false
  LineAngle = 0
  LockPosition = false
  MeasureType = 1
  OverTolerance = 0
  References2D = -> [View021]
  Rotation = 0
  Scale = 0.1
  ScaleType = 0
  TheoreticalExact = false
  Type = 2
  UnderTolerance = 0
  X = 4.37964
  Y = 0
FEATURE [TechDraw::DrawViewBalloon] Balloon017
  BubbleShape = 0
  EndType = 0
  EndTypeScale = 1
  KinkLength = 5
  LockPosition = false
  OriginX = -114.061
  OriginY = -28.1487
  Rotation = 0
  Scale = 0.2
  ScaleType = 0
  ShapeScale = 1
  SourceView = -> View016
  Text = P7
  TextWrapLen = -1
  X = -14.0615
  Y = 71.8513
FEATURE [App::DocumentObjectGroup] Group001  label="Simulations"
  Group = -> [Body,Spreadsheet001]
FEATURE [TechDraw::DrawSVGTemplate] Template005
  Height = 210
  Orientation = 1
  Template = <path>
  Width = 297
FEATURE [TechDraw::DrawProjGroupItem] View022  label="P11 (devant)"
  Caption = P11 (devant)
  CoarseView = false
  Direction = (-1,-1e-16,0)
  Focus = 100
  HardHidden = false
  IsoCount = 0
  IsoHidden = false
  IsoVisible = false
  LockPosition = true
  Perspective = false
  Rotation = 0
  RotationVector = (1,0,0)
  Scale = 0.2
  ScaleType = 2
  ScrubCount = 1
  SeamHidden = false
  SeamVisible = true
  SmoothHidden = false
  SmoothVisible = true
  Source = -> [Body036]
  Type = 0
  X = 0
  XDirection = (1e-16,-1,0)
  Y = 0
FEATURE [TechDraw::DrawProjGroupItem] ProjItem009  label="P11 (côté)"
  Caption = P11 (côté)
  CoarseView = false
  Direction = (0,-1,0)
  Focus = 100
  HardHidden = false
  IsoCount = 0
  IsoHidden = false
  IsoVisible = false
  LockPosition = false
  Perspective = false
  Rotation = 0
  RotationVector = (1,0,0)
  Scale = 0.2
  ScaleType = 0
  ScrubCount = 1
  SeamHidden = false
  SeamVisible = true
  SmoothHidden = false
  SmoothVisible = true
  Source = -> [Body036]
  Type = 2
  X = -35.7331
  XDirection = (1,0,0)
  Y = 0
FEATURE [TechDraw::DrawProjGroup] ProjGroup009
  Anchor = -> View022
  AutoDistribute = true
  LockPosition = false
  ProjectionType = 0
  Rotation = 0
  Scale = 0.2
  ScaleType = 0
  Source = -> [Body036]
  Views = -> [View022,ProjItem009]
  X = 239.901
  Y = 153.343
  spacingX = 15
  spacingY = 15
FEATURE [TechDraw::DrawViewDimension] Dimension043
  AngleOverride = false
  Arbitrary = false
  ArbitraryTolerances = false
  BoxCorners = (2) [(-9.71657,-14.2669,0),(9.71657,14.2669,0)]
  EqualTolerance = true
  ExtensionAngle = 0
  FormatSpec = %.0w
  FormatSpecOverTolerance = %+.2w
  FormatSpecUnderTolerance = %+.2w
  Inverted = false
  LineAngle = 0
  LockPosition = false
  MeasureType = 1
  OverTolerance = 0
  References2D = -> [View022]
  Rotation = 0
  Scale = 0.2
  ScaleType = 0
  TheoreticalExact = false
  Type = 2
  UnderTolerance = 0
  X = -6.41382
  Y = 0
FEATURE [TechDraw::DrawViewDimension] Dimension044
  AngleOverride = false
  Arbitrary = false
  ArbitraryTolerances = false
  BoxCorners = (2) [(-9.71657,-14.2669,0),(9.71657,14.2669,0)]
  EqualTolerance = true
  ExtensionAngle = 0
  FormatSpec = %.0w
  FormatSpecOverTolerance = %+.2w
  FormatSpecUnderTolerance = %+.2w
  Inverted = false
  LineAngle = 0
  LockPosition = false
  MeasureType = 1
  OverTolerance = 0
  References2D = -> [View022]
  Rotation = 0
  Scale = 0.2
  ScaleType = 0
  TheoreticalExact = false
  Type = 1
  UnderTolerance = 0
  X = 0
  Y = 37.184
FEATURE [TechDraw::DrawViewDimension] Dimension045
  AngleOverride = false
  Arbitrary = false
  ArbitraryTolerances = false
  BoxCorners = (2) [(-0.65,-14.2669,0),(0.65,14.2669,0)]
  EqualTolerance = true
  ExtensionAngle = 0
  FormatSpec = %.2w
  FormatSpecOverTolerance = %+.2w
  FormatSpecUnderTolerance = %+.2w
  Inverted = false
  LineAngle = 0
  LockPosition = false
  MeasureType = 1
  OverTolerance = 0
  References2D = -> [ProjItem009]
  Rotation = 0
  Scale = 0.2
  ScaleType = 0
  TheoreticalExact = false
  Type = 1
  UnderTolerance = 0
  X = 0
  Y = 40.2761
FEATURE [TechDraw::DrawProjGroupItem] View023  label="P9 (devant)"
  Caption = P9 (devant)
  CoarseView = false
  Direction = (1,-1e-16,0)
  Focus = 100
  HardHidden = false
  IsoCount = 0
  IsoHidden = false
  IsoVisible = false
  LockPosition = true
  Perspective = false
  Rotation = 0
  RotationVector = (1,0,0)
  Scale = 0.2
  ScaleType = 2
  ScrubCount = 1
  SeamHidden = false
  SeamVisible = true
  SmoothHidden = false
  SmoothVisible = true
  Type = 0
  X = 0
  XDirection = (1e-16,1,0)
  XSource = -> [fin_1_support]
  Y = 0
FEATURE [TechDraw::DrawProjGroupItem] ProjItem010  label="P9 (côté)"
  Caption = P9 (côté)
  CoarseView = false
  Direction = (0,-1,0)
  Focus = 100
  HardHidden = false
  IsoCount = 0
  IsoHidden = false
  IsoVisible = false
  LockPosition = false
  Perspective = false
  Rotation = 0
  RotationVector = (1,0,0)
  Scale = 0.2
  ScaleType = 0
  ScrubCount = 1
  SeamHidden = false
  SeamVisible = true
  SmoothHidden = false
  SmoothVisible = true
  Type = 1
  X = 35.7331
  XDirection = (1,0,0)
  XSource = -> [fin_1_support]
  Y = 0
FEATURE [TechDraw::DrawProjGroup] ProjGroup010
  Anchor = -> View023
  AutoDistribute = true
  LockPosition = false
  ProjectionType = 0
  Rotation = 0
  Scale = 0.2
  ScaleType = 0
  Views = -> [View023,ProjItem010]
  X = 52.8552
  XSource = -> [fin_1_support]
  Y = 146.319
  spacingX = 15
  spacingY = 15
FEATURE [TechDraw::DrawProjGroupItem] View024  label="P10 (côté)"
  Caption = P10 (côté)
  CoarseView = false
  Direction = (0,-1,0)
  Focus = 100
  HardHidden = false
  IsoCount = 0
  IsoHidden = false
  IsoVisible = false
  LockPosition = true
  Perspective = false
  Rotation = 0
  RotationVector = (1,0,0)
  Scale = 0.2
  ScaleType = 2
  ScrubCount = 1
  SeamHidden = false
  SeamVisible = true
  SmoothHidden = false
  SmoothVisible = true
  Type = 0
  X = 0
  XDirection = (1,0,0)
  XSource = -> [fin_1_support001]
  Y = 0
FEATURE [TechDraw::DrawProjGroupItem] ProjItem011  label="P10 (devant)"
  Caption = P10 (devant)
  CoarseView = false
  Direction = (1,-1e-16,0)
  Focus = 100
  HardHidden = false
  IsoCount = 0
  IsoHidden = false
  IsoVisible = false
  LockPosition = false
  Perspective = false
  Rotation = 0
  RotationVector = (1,0,0)
  Scale = 0.2
  ScaleType = 0
  ScrubCount = 1
  SeamHidden = false
  SeamVisible = true
  SmoothHidden = false
  SmoothVisible = true
  Type = 2
  X = -35.7331
  XDirection = (1e-16,1,0)
  XSource = -> [fin_1_support001]
  Y = 0
FEATURE [TechDraw::DrawProjGroup] ProjGroup011
  Anchor = -> View024
  AutoDistribute = true
  LockPosition = false
  ProjectionType = 0
  Rotation = 0
  Scale = 0.2
  ScaleType = 0
  Views = -> [View024,ProjItem011]
  X = 166.864
  XSource = -> [fin_1_support001]
  Y = 147.084
  spacingX = 15
  spacingY = 15
FEATURE [TechDraw::DrawViewDimension] Dimension046
  AngleOverride = false
  Arbitrary = false
  ArbitraryTolerances = false
  BoxCorners = (2) [(-19.4331,-44.9669,0),(19.4331,44.9669,0)]
  EqualTolerance = true
  ExtensionAngle = 0
  FormatSpec = %.0w
  FormatSpecOverTolerance = %+.2w
  FormatSpecUnderTolerance = %+.2w
  Inverted = false
  LineAngle = 0
  LockPosition = false
  MeasureType = 1
  OverTolerance = 0
  References2D = -> [ProjItem011]
  Rotation = 0
  Scale = 0.2
  ScaleType = 0
  TheoreticalExact = false
  Type = 1
  UnderTolerance = 0
  X = 0
  Y = 54.3533
FEATURE [TechDraw::DrawViewDimension] Dimension047
  AngleOverride = false
  Arbitrary = false
  ArbitraryTolerances = false
  BoxCorners = (2) [(-19.4331,-44.9669,0),(19.4331,44.9669,0)]
  EqualTolerance = true
  ExtensionAngle = 0
  FormatSpec = %.0w
  FormatSpecOverTolerance = %+.2w
  FormatSpecUnderTolerance = %+.2w
  Inverted = false
  LineAngle = 0
  LockPosition = false
  MeasureType = 1
  OverTolerance = 0
  References2D = -> [ProjItem011]
  Rotation = 0
  Scale = 0.2
  ScaleType = 0
  TheoreticalExact = false
  Type = 2
  UnderTolerance = 0
  X = 8.33834
  Y = 0
FEATURE [TechDraw::DrawViewDimension] Dimension048
  AngleOverride = false
  Arbitrary = false
  ArbitraryTolerances = false
  BoxCorners = (2) [(-1.3,-44.9669,0),(1.3,44.9669,0)]
  EqualTolerance = true
  ExtensionAngle = 0
  FormatSpec = %.2w
  FormatSpecOverTolerance = %+.2w
  FormatSpecUnderTolerance = %+.2w
  Inverted = false
  LineAngle = 0
  LockPosition = false
  MeasureType = 1
  OverTolerance = 0
  References2D = -> [View024]
  Rotation = 0
  Scale = 0.2
  ScaleType = 0
  TheoreticalExact = false
  Type = 1
  UnderTolerance = 0
  X = 7.20703
  Y = -40.1375
FEATURE [TechDraw::DrawViewDimension] Dimension049
  AngleOverride = false
  Arbitrary = false
  ArbitraryTolerances = false
  BoxCorners = (2) [(-19.4331,-49.2669,0),(19.4331,49.2669,0)]
  EqualTolerance = true
  ExtensionAngle = 0
  FormatSpec = %.0w
  FormatSpecOverTolerance = %+.2w
  FormatSpecUnderTolerance = %+.2w
  Inverted = false
  LineAngle = 0
  LockPosition = false
  MeasureType = 1
  OverTolerance = 0
  References2D = -> [View023]
  Rotation = 0
  Scale = 0.2
  ScaleType = 0
  TheoreticalExact = false
  Type = 1
  UnderTolerance = 0
  X = 4.68457
  Y = 32.3079
FEATURE [TechDraw::DrawViewDimension] Dimension050
  AngleOverride = false
  Arbitrary = false
  ArbitraryTolerances = false
  BoxCorners = (2) [(-19.4331,-49.2669,0),(19.4331,49.2669,0)]
  EqualTolerance = true
  ExtensionAngle = 0
  FormatSpec = %.0w
  FormatSpecOverTolerance = %+.2w
  FormatSpecUnderTolerance = %+.2w
  Inverted = false
  LineAngle = 0
  LockPosition = false
  MeasureType = 1
  OverTolerance = 0
  References2D = -> [View023]
  Rotation = 0
  Scale = 0.2
  ScaleType = 0
  TheoreticalExact = false
  Type = 2
  UnderTolerance = 0
  X = -9.70365
  Y = 0
FEATURE [TechDraw::DrawViewAnnotation] Annotation004
  Font = osifont
  LineSpace = 100
  LockPosition = false
  MaxWidth = -1
  Rotation = 0
  Scale = 0.1
  ScaleType = 0
  Text = Panneaux 1 à 8 | Dimensions en mm | Échelle 1 pour 10
  TextSize = 5
  TextStyle = 0
  X = 29.0298
  Y = 16.1744
FEATURE [TechDraw::DrawViewAnnotation] Annotation005
  Font = osifont
  LineSpace = 100
  LockPosition = false
  MaxWidth = -1
  Rotation = 0
  Scale = 0.2
  ScaleType = 0
  Text = Panneaux 8 à 11 | Dimensions en mm | Échelle 1 pour 10
  TextSize = 5
  TextStyle = 0
  X = 30.0344
  Y = 21.1855
FEATURE [TechDraw::DrawSVGTemplate] Template006
  Height = 210
  Orientation = 1
  Template = <path>
  Width = 297
FEATURE [TechDraw::DrawProjGroupItem] View025  label="Panel C1"
  Caption = Panel C1
  CoarseView = false
  Direction = (0,0,-1)
  Focus = 100
  HardHidden = false
  IsoCount = 0
  IsoHidden = false
  IsoVisible = false
  LockPosition = false
  Perspective = false
  Rotation = 0
  RotationVector = (1,0,0)
  Scale = 0.2
  ScaleType = 0
  ScrubCount = 1
  SeamHidden = false
  SeamVisible = true
  SmoothHidden = false
  SmoothVisible = true
  Source = -> [Body039]
  Type = 0
  X = 148.5
  XDirection = (1,0,0)
  Y = 104.73
FEATURE [TechDraw::DrawViewAnnotation] Annotation006
  Font = osifont
  LineSpace = 100
  LockPosition = false
  MaxWidth = -1
  Rotation = 0
  Scale = 0.2
  ScaleType = 0
  Text = Plan de coupe: Panneau C1 | Dimensions en mm | Échelle 1 pour 5 | Répéter pour P8'`
  TextSize = 5
  TextStyle = 0
  X = 42.7285
  Y = 26.9227
FEATURE [PartDesign::Pad] Pad024
  Direction = (0,0,1)
  Length = 30
  Length2 = 10
  Profile = -> Sketch036
  ReferenceAxis = -> Sketch036 [N_Axis]
  Suppressed = false
  Type = 0
  expr: Length = <<bdim>>.bbbp1_t
FEATURE [PartDesign::Body] Body025  label="brace_bar_back_panel_1"
  AllowCompound = false
  Group = -> [Sketch036,Pad024]
  Origin = -> Origin026
  Tip = -> Pad024
FEATURE [TechDraw::DrawProjGroupItem] View027
  CoarseView = false
  Direction = (-1,-1e-16,0)
  Focus = 100
  HardHidden = false
  IsoCount = 0
  IsoHidden = false
  IsoVisible = false
  LockPosition = false
  Perspective = false
  Rotation = 0
  RotationVector = (1,0,0)
  Scale = 0.2
  ScaleType = 0
  ScrubCount = 1
  SeamHidden = false
  SeamVisible = true
  SmoothHidden = false
  SmoothVisible = true
  Source = -> [Pad034]
  Type = 0
  X = 190.556
  XDirection = (1e-16,-1,0)
  Y = 72.5473
FEATURE [TechDraw::DrawViewDimension] Dimension056
  AngleOverride = false
  Arbitrary = false
  ArbitraryTolerances = false
  BoxCorners = (2) [(-19.4331,-28.5337,0),(19.4331,28.5337,0)]
  EqualTolerance = true
  ExtensionAngle = 0
  FormatSpec = %.0w
  FormatSpecOverTolerance = %+.2w
  FormatSpecUnderTolerance = %+.2w
  Inverted = false
  LineAngle = 0
  LockPosition = false
  MeasureType = 1
  OverTolerance = 0
  References2D = -> [View027]
  Rotation = 0
  Scale = 0.2
  ScaleType = 0
  TheoreticalExact = false
  Type = 1
  UnderTolerance = 0
  X = 0
  Y = 9.7815
FEATURE [TechDraw::DrawViewDimension] Dimension057
  AngleOverride = false
  Arbitrary = false
  ArbitraryTolerances = false
  BoxCorners = (2) [(-19.4331,-28.5337,0),(19.4331,28.5337,0)]
  EqualTolerance = true
  ExtensionAngle = 0
  FormatSpec = %.0w
  FormatSpecOverTolerance = %+.2w
  FormatSpecUnderTolerance = %+.2w
  Inverted = false
  LineAngle = 0
  LockPosition = false
  MeasureType = 1
  OverTolerance = 0
  References2D = -> [View027]
  Rotation = 0
  Scale = 0.2
  ScaleType = 0
  TheoreticalExact = false
  Type = 2
  UnderTolerance = 0
  X = 36.3775
  Y = 0
FEATURE [TechDraw::DrawViewBalloon] Balloon019
  BubbleShape = 0
  EndType = 0
  EndTypeScale = 1
  KinkLength = 5
  LockPosition = false
  OriginX = -2.17314
  OriginY = -72.6722
  Rotation = 0
  Scale = 0.2
  ScaleType = 0
  ShapeScale = 1
  SourceView = -> View027
  Text = P11'
  TextWrapLen = -1
  X = 54.748
  Y = 101.998
FEATURE [TechDraw::DrawPage] Page002  label="panel_A2_cuts"
  KeepUpdated = true
  NextBalloonIndex = 4
  ProjectionType = 0
  Scale = 0.2
  Template = -> Template002
  Views = -> [View012,View013,View014,Balloon012,Balloon013,Annotation001,Dimension028,Dimension029,Dimension030,Dimension031,View027,Dimension056,Dimension057,Balloon019]
FEATURE [TechDraw::DrawSVGTemplate] Template007
  Height = 210
  Orientation = 1
  Template = <path>
  Width = 297
FEATURE [TechDraw::DrawViewAnnotation] Annotation007
  Font = osifont
  LineSpace = 100
  LockPosition = false
  MaxWidth = -1
  Rotation = 0
  Scale = 0.2
  ScaleType = 0
  Text = Plan de coupe: Panneau A2' | Dimensions en mm | Échelle 1 pour 5
  TextSize = 5
  TextStyle = 0
  X = 41.8511
  Y = 16.1016
FEATURE [TechDraw::DrawProjGroupItem] View028
  CoarseView = false
  Direction = (0,-2e-16,-1)
  Focus = 100
  HardHidden = false
  IsoCount = 0
  IsoHidden = false
  IsoVisible = false
  LockPosition = false
  Perspective = false
  Rotation = 0
  RotationVector = (1,0,0)
  Scale = 0.2
  ScaleType = 0
  ScrubCount = 1
  SeamHidden = false
  SeamVisible = true
  SmoothHidden = false
  SmoothVisible = true
  Source = -> [Body037]
  Type = 0
  X = 148.5
  XDirection = (1e-16,-1,2e-16)
  Y = 119.862
FEATURE [TechDraw::DrawProjGroupItem] View029
  CoarseView = false
  Direction = (-1,-1e-16,0)
  Focus = 100
  HardHidden = false
  IsoCount = 0
  IsoHidden = false
  IsoVisible = false
  LockPosition = false
  Perspective = false
  Rotation = 0
  RotationVector = (1,0,0)
  Scale = 0.2
  ScaleType = 0
  ScrubCount = 1
  SeamHidden = false
  SeamVisible = true
  SmoothHidden = false
  SmoothVisible = true
  Source = -> [Body007]
  Type = 0
  X = 99.7453
  XDirection = (0,-1e-16,1)
  Y = 119.703
FEATURE [TechDraw::DrawViewBalloon] Balloon020
  BubbleShape = 0
  EndType = 0
  EndTypeScale = 1
  KinkLength = 5
  LockPosition = false
  OriginX = 65.2982
  OriginY = 61.2385
  Rotation = 0
  Scale = 0.2
  ScaleType = 0
  ShapeScale = 1
  SourceView = -> View029
  Text = P2'
  TextWrapLen = -1
  X = 166.674
  Y = 161.239
FEATURE [TechDraw::DrawViewAnnotation] Annotation008
  Font = osifont
  LineSpace = 100
  LockPosition = false
  MaxWidth = -1
  Rotation = 0
  Scale = 0.2
  ScaleType = 0
  Text = Faire d'abord coupe 1 | Ensuite coupe 2 au milieu | La hauteur sera ~315mm au lieu de 320 mm | Ben correct
  TextSize = 5
  TextStyle = 0
  X = 170.002
  Y = 21.5711
FEATURE [App::FeaturePython] GroundedJoint001  # Assembly grounded joint (typed FeaturePython)
  ObjectToGround = -> side_panel_001_bar_008
  Placement = pos=(303,457.669,13) rot=(0,-1,0;1.5708rad)
FEATURE [App::Link] fin_1_model  label="fin_1"
  LinkPlacement = pos=(13,427.669,13) rot=(0,0,1;0rad)
  LinkedObject = -> Body019
  Placement = pos=(13,427.669,13) rot=(0,0,1;0rad)
FEATURE [App::FeaturePython] Joint060  label="Fixed048"  # Assembly joint (typed FeaturePython)
  Activated = true
  AngleMax = 0
  AngleMin = 0
  Detach1 = false
  Detach2 = false
  Distance = 0
  Distance2 = 0
  EnableAngleMax = false
  EnableAngleMin = false
  EnableLengthMax = false
  EnableLengthMin = false
  JointType = 0 (Fixed)
  LengthMax = 0
  LengthMin = 0
  Offset2 = pos=(0,0,0) rot=(0,0,1;3.14159rad)
  Placement1 = pos=(1.8e-15,-30,130) rot=(0,1,0;3.14159rad)
  Placement2 = pos=(160,0,0) rot=(0,-1,0;4.71239rad)
  Reference1 = -> Assembly [side_panel_001_bar_008.Edge12,side_panel_001_bar_008.Edge12]
  Reference2 = -> Assembly [fin_1_model.Edge3,fin_1_model.Edge3]
FEATURE [TechDraw::DrawProjGroupItem] View030
  CoarseView = false
  Direction = (0,-1,0)
  Focus = 100
  HardHidden = false
  IsoCount = 0
  IsoHidden = false
  IsoVisible = false
  LockPosition = false
  Perspective = false
  Rotation = 0
  RotationVector = (1,0,0)
  Scale = 0.2
  ScaleType = 0
  ScrubCount = 1
  SeamHidden = false
  SeamVisible = true
  SmoothHidden = false
  SmoothVisible = true
  Type = 0
  X = 218.6
  XDirection = (1e-16,0,1)
  XSource = -> [fin_1_model]
  Y = 151.105
FEATURE [TechDraw::DrawViewBalloon] Balloon021
  BubbleShape = 0
  EndType = 0
  EndTypeScale = 1
  KinkLength = 5
  LockPosition = false
  OriginX = -195.201
  OriginY = 48.5403
  Rotation = 0
  Scale = 0.2
  ScaleType = 0
  ShapeScale = 1
  SourceView = -> View030
  Text = P8
  TextWrapLen = -1
  X = -52.107
  Y = 214.618
FEATURE [TechDraw::DrawProjGroupItem] View031
  CoarseView = false
  Direction = (0,-1,0)
  Focus = 100
  HardHidden = false
  IsoCount = 0
  IsoHidden = false
  IsoVisible = false
  LockPosition = false
  Perspective = false
  Rotation = 0
  RotationVector = (1,0,0)
  Scale = 0.2
  ScaleType = 0
  ScrubCount = 1
  SeamHidden = false
  SeamVisible = true
  SmoothHidden = false
  SmoothVisible = true
  Type = 0
  X = 218.6
  XDirection = (1e-16,0,-1)
  XSource = -> [fin_1_model]
  Y = 86.4761
FEATURE [TechDraw::DrawViewBalloon] Balloon022
  BubbleShape = 0
  EndType = 0
  EndTypeScale = 1
  KinkLength = 5
  LockPosition = false
  OriginX = -110.808
  OriginY = -20.4366
  Rotation = 0
  Scale = 0.2
  ScaleType = 0
  ShapeScale = 1
  SourceView = -> View031
  Text = P8'
  TextWrapLen = -1
  X = -10.8082
  Y = 79.5634
FEATURE [TechDraw::DrawViewBalloon] Balloon023
  BubbleShape = 0
  EndType = 0
  EndTypeScale = 1
  KinkLength = 5
  LockPosition = false
  OriginX = 353.988
  OriginY = 346.969
  Rotation = 0
  Scale = 0.2
  ScaleType = 0
  ShapeScale = 1
  SourceView = -> View029
  Text = COUPE 1
  TextWrapLen = -1
  X = 161.305
  Y = 387.714
FEATURE [TechDraw::DrawViewBalloon] Balloon024
  BubbleShape = 0
  EndType = 0
  EndTypeScale = 1
  KinkLength = 5
  LockPosition = false
  OriginX = 239.834
  OriginY = 160
  Rotation = 0
  Scale = 0.2
  ScaleType = 0
  ShapeScale = 1
  SourceView = -> View031
  Text = COUPE 2
  TextWrapLen = -1
  X = 280.58
  Y = -346.913
FEATURE [TechDraw::DrawProjGroupItem] View032
  CoarseView = false
  Direction = (-1e-16,-1e-16,1)
  Focus = 100
  HardHidden = false
  IsoCount = 0
  IsoHidden = false
  IsoVisible = false
  LockPosition = false
  Perspective = false
  Rotation = 0
  RotationVector = (1,0,0)
  Scale = 0.2
  ScaleType = 0
  ScrubCount = 1
  SeamHidden = false
  SeamVisible = true
  SmoothHidden = false
  SmoothVisible = true
  Type = 0
  X = 219.143
  XDirection = (0,-1,-1e-16)
  XSource = -> [front_panel]
  Y = 104.716
FEATURE [TechDraw::DrawViewBalloon] Balloon025
  BubbleShape = 0
  EndType = 0
  EndTypeScale = 1
  KinkLength = 5
  LockPosition = false
  OriginX = -162.372
  OriginY = 73.7958
  Rotation = 0
  Scale = 0.2
  ScaleType = 0
  ShapeScale = 1
  SourceView = -> View032
  Text = P5
  TextWrapLen = -1
  X = 20.914
  Y = 308.776
FEATURE [TechDraw::DrawViewDimension] Dimension058
  AngleOverride = false
  Arbitrary = false
  ArbitraryTolerances = false
  BoxCorners = (2) [(-41.4663,-32,0),(41.4663,32,0)]
  EqualTolerance = true
  ExtensionAngle = 0
  FormatSpec = %.0w
  FormatSpecOverTolerance = %+.2w
  FormatSpecUnderTolerance = %+.2w
  Inverted = false
  LineAngle = 0
  LockPosition = false
  MeasureType = 1
  OverTolerance = 0
  References2D = -> [View032]
  Rotation = 0
  Scale = 0.2
  ScaleType = 0
  TheoreticalExact = false
  Type = 1
  UnderTolerance = 0
  X = 0
  Y = -57.932
FEATURE [TechDraw::DrawViewDimension] Dimension059
  AngleOverride = false
  Arbitrary = false
  ArbitraryTolerances = false
  BoxCorners = (2) [(-41.4663,-32,0),(41.4663,32,0)]
  EqualTolerance = true
  ExtensionAngle = 0
  FormatSpec = ⌀%.0w
  FormatSpecOverTolerance = %+.2w
  FormatSpecUnderTolerance = %+.2w
  Inverted = false
  LineAngle = 0
  LockPosition = false
  MeasureType = 1
  OverTolerance = 0
  References2D = -> [View032]
  Rotation = 0
  Scale = 0.2
  ScaleType = 0
  TheoreticalExact = false
  Type = 5
  UnderTolerance = 0
  X = 0
  Y = 0
FEATURE [TechDraw::DrawViewDimension] Dimension060
  AngleOverride = false
  Arbitrary = false
  ArbitraryTolerances = false
  BoxCorners = (2) [(-41.4663,-32,0),(41.4663,32,0)]
  EqualTolerance = true
  ExtensionAngle = 0
  FormatSpec = %.0w
  FormatSpecOverTolerance = %+.2w
  FormatSpecUnderTolerance = %+.2w
  Inverted = false
  LineAngle = 0
  LockPosition = false
  MeasureType = 1
  OverTolerance = 0
  References2D = -> [View032]
  Rotation = 0
  Scale = 0.2
  ScaleType = 0
  TheoreticalExact = false
  Type = 1
  UnderTolerance = 0
  X = -18.3831
  Y = 38.1118
FEATURE [TechDraw::DrawViewDimension] Dimension061
  AngleOverride = false
  Arbitrary = false
  ArbitraryTolerances = false
  BoxCorners = (2) [(-41.4663,-32,0),(41.4663,32,0)]
  EqualTolerance = true
  ExtensionAngle = 0
  FormatSpec = %.2w
  FormatSpecOverTolerance = %+.2w
  FormatSpecUnderTolerance = %+.2w
  Inverted = false
  LineAngle = 0
  LockPosition = false
  MeasureType = 1
  OverTolerance = 0
  References2D = -> [View032]
  Rotation = 0
  Scale = 0.2
  ScaleType = 0
  TheoreticalExact = false
  Type = 2
  UnderTolerance = 0
  X = 18.7724
  Y = -16
FEATURE [TechDraw::DrawViewDimension] Dimension062
  AngleOverride = false
  Arbitrary = false
  ArbitraryTolerances = false
  BoxCorners = (2) [(-70,-63.5,0),(70,63.5,0)]
  EqualTolerance = true
  ExtensionAngle = 0
  FormatSpec = %.2w
  FormatSpecOverTolerance = %+.2w
  FormatSpecUnderTolerance = %+.2w
  Inverted = false
  LineAngle = 0
  LockPosition = false
  MeasureType = 1
  OverTolerance = 0
  References2D = -> [View029]
  Rotation = 0
  Scale = 0.2
  ScaleType = 0
  TheoreticalExact = false
  Type = 1
  UnderTolerance = 0
  X = 0
  Y = -13.8112
FEATURE [TechDraw::DrawViewDimension] Dimension063
  AngleOverride = false
  Arbitrary = false
  ArbitraryTolerances = false
  BoxCorners = (2) [(-70,-63.5,0),(70,63.5,0)]
  EqualTolerance = true
  ExtensionAngle = 0
  FormatSpec = %.2w
  FormatSpecOverTolerance = %+.2w
  FormatSpecUnderTolerance = %+.2w
  Inverted = false
  LineAngle = 0
  LockPosition = false
  MeasureType = 1
  OverTolerance = 0
  References2D = -> [View029]
  Rotation = 0
  Scale = 0.2
  ScaleType = 0
  TheoreticalExact = false
  Type = 2
  UnderTolerance = 0
  X = -37.7592
  Y = -2.93098
FEATURE [TechDraw::DrawViewDimension] Dimension064
  AngleOverride = false
  Arbitrary = false
  ArbitraryTolerances = false
  BoxCorners = (2) [(-118.7,-63.5,0),(118.7,63.5,0)]
  EqualTolerance = true
  ExtensionAngle = 0
  FormatSpec = %.2w
  FormatSpecOverTolerance = %+.2w
  FormatSpecUnderTolerance = %+.2w
  Inverted = false
  LineAngle = 0
  LockPosition = false
  MeasureType = 1
  OverTolerance = 0
  References2D = -> [View028]
  Rotation = 0
  Scale = 0.2
  ScaleType = 0
  TheoreticalExact = false
  Type = 1
  UnderTolerance = 0
  X = 8.03819
  Y = 83.1327
FEATURE [TechDraw::DrawViewDimension] Dimension065
  AngleOverride = false
  Arbitrary = false
  ArbitraryTolerances = false
  BoxCorners = (2) [(-47.9669,-32,0),(47.9669,32,0)]
  EqualTolerance = true
  ExtensionAngle = 0
  FormatSpec = %.0w
  FormatSpecOverTolerance = %+.2w
  FormatSpecUnderTolerance = %+.2w
  Inverted = false
  LineAngle = 0
  LockPosition = false
  MeasureType = 1
  OverTolerance = 0
  References2D = -> [View031]
  Rotation = 0
  Scale = 0.2
  ScaleType = 0
  TheoreticalExact = false
  Type = 1
  UnderTolerance = 0
  X = 0
  Y = 53.9445
FEATURE [TechDraw::DrawViewDimension] Dimension066
  AngleOverride = false
  Arbitrary = false
  ArbitraryTolerances = false
  BoxCorners = (2) [(-47.9669,-32,0),(47.9669,32,0)]
  EqualTolerance = true
  ExtensionAngle = 0
  FormatSpec = %.2w
  FormatSpecOverTolerance = %+.2w
  FormatSpecUnderTolerance = %+.2w
  Inverted = false
  LineAngle = 0
  LockPosition = false
  MeasureType = 1
  OverTolerance = 0
  References2D = -> [View031]
  Rotation = 0
  Scale = 0.2
  ScaleType = 0
  TheoreticalExact = false
  Type = 2
  UnderTolerance = 0
  X = 58.8407
  Y = 0
FEATURE [TechDraw::DrawViewDimension] Dimension067
  AngleOverride = false
  Arbitrary = false
  ArbitraryTolerances = false
  BoxCorners = (2) [(-47.9669,-32,0),(47.9669,32,0)]
  EqualTolerance = true
  ExtensionAngle = 0
  FormatSpec = %.2w
  FormatSpecOverTolerance = %+.2w
  FormatSpecUnderTolerance = %+.2w
  Inverted = false
  LineAngle = 0
  LockPosition = false
  MeasureType = 1
  OverTolerance = 0
  References2D = -> [View030]
  Rotation = 0
  Scale = 0.2
  ScaleType = 0
  TheoreticalExact = false
  Type = 2
  UnderTolerance = 0
  X = 58.9215
  Y = 0
FEATURE [TechDraw::DrawPage] Page007  label="panel_A2'_cuts"
  KeepUpdated = true
  NextBalloonIndex = 10
  ProjectionType = 0
  Scale = 0.2
  Template = -> Template007
  Views = -> [Annotation007,View028,View029,Balloon020,Annotation008,View030,Balloon021,View031,Balloon022,Balloon023,Balloon024,Dimension062,Dimension063,Dimension064,Dimension065,Dimension066,Dimension067]
FEATURE [TechDraw::DrawProjGroupItem] View033  label="P8 (devant)"
  Caption = P8 (devant)
  CoarseView = false
  Direction = (0,-1,0)
  Focus = 100
  HardHidden = false
  IsoCount = 0
  IsoHidden = false
  IsoVisible = false
  LockPosition = false
  Perspective = false
  Rotation = 0
  RotationVector = (1,0,0)
  Scale = 0.2
  ScaleType = 0
  ScrubCount = 1
  SeamHidden = false
  SeamVisible = true
  SmoothHidden = false
  SmoothVisible = true
  Type = 0
  X = 239.901
  XDirection = (1e-16,0,1)
  XSource = -> [fin_1_model]
  Y = 60.5013
FEATURE [TechDraw::DrawViewDimension] Dimension068
  AngleOverride = false
  Arbitrary = false
  ArbitraryTolerances = false
  BoxCorners = (2) [(-47.9669,-32,0),(47.9669,32,0)]
  EqualTolerance = true
  ExtensionAngle = 0
  FormatSpec = %.0w
  FormatSpecOverTolerance = %+.2w
  FormatSpecUnderTolerance = %+.2w
  Inverted = false
  LineAngle = 0
  LockPosition = false
  MeasureType = 1
  OverTolerance = 0
  References2D = -> [View033]
  Rotation = 0
  Scale = 0.2
  ScaleType = 0
  TheoreticalExact = false
  Type = 1
  UnderTolerance = 0
  X = 0
  Y = -14.2868
FEATURE [TechDraw::DrawViewDimension] Dimension069
  AngleOverride = false
  Arbitrary = false
  ArbitraryTolerances = false
  BoxCorners = (2) [(-47.9669,-32,0),(47.9669,32,0)]
  EqualTolerance = true
  ExtensionAngle = 0
  FormatSpec = %.2w
  FormatSpecOverTolerance = %+.2w
  FormatSpecUnderTolerance = %+.2w
  Inverted = false
  LineAngle = 0
  LockPosition = false
  MeasureType = 1
  OverTolerance = 0
  References2D = -> [View033]
  Rotation = 0
  Scale = 0.2
  ScaleType = 0
  TheoreticalExact = false
  Type = 2
  UnderTolerance = 0
  X = -30.0913
  Y = -5.32463
FEATURE [TechDraw::DrawPage] Page005  label="panels_8_to_11"
  KeepUpdated = true
  NextBalloonIndex = 1
  ProjectionType = 0
  Scale = 0.2
  Template = -> Template005
  Views = -> [ProjGroup009,Dimension043,Dimension044,Dimension045,ProjGroup010,ProjGroup011,Dimension046,Dimension047,Dimension048,Dimension049,Dimension050,Annotation005,View033,Dimension068,Dimension069]
FEATURE [TechDraw::DrawProjGroupItem] View034
  CoarseView = false
  Direction = (0,-1,0)
  Focus = 100
  HardHidden = false
  IsoCount = 0
  IsoHidden = false
  IsoVisible = false
  LockPosition = false
  Perspective = false
  Rotation = 0
  RotationVector = (1,0,0)
  Scale = 0.2
  ScaleType = 0
  ScrubCount = 1
  SeamHidden = false
  SeamVisible = true
  SmoothHidden = false
  SmoothVisible = true
  Type = 0
  X = 148.5
  XDirection = (1,0,0)
  XSource = -> [fin_1_model]
  Y = 120.208
FEATURE [TechDraw::DrawViewBalloon] Balloon026
  BubbleShape = 0
  EndType = 0
  EndTypeScale = 1
  KinkLength = 5
  LockPosition = false
  OriginX = 36.9107
  OriginY = 152.049
  Rotation = 0
  Scale = 0.2
  ScaleType = 0
  ShapeScale = 1
  SourceView = -> View034
  Text = P7
  TextWrapLen = -1
  X = 329.97
  Y = 316.391
FEATURE [TechDraw::DrawViewDimension] Dimension070
  AngleOverride = false
  Arbitrary = false
  ArbitraryTolerances = false
  BoxCorners = (2) [(-32,-47.9669,0),(32,47.9669,0)]
  EqualTolerance = true
  ExtensionAngle = 0
  FormatSpec = %.2w
  FormatSpecOverTolerance = %+.2w
  FormatSpecUnderTolerance = %+.2w
  Inverted = false
  LineAngle = 0
  LockPosition = false
  MeasureType = 1
  OverTolerance = 0
  References2D = -> [View034]
  Rotation = 0
  Scale = 0.2
  ScaleType = 0
  TheoreticalExact = false
  Type = 1
  UnderTolerance = 0
  X = -14.6231
  Y = 67.1309
FEATURE [TechDraw::DrawViewDimension] Dimension071
  AngleOverride = false
  Arbitrary = false
  ArbitraryTolerances = false
  BoxCorners = (2) [(-32,-47.9669,0),(32,47.9669,0)]
  EqualTolerance = true
  ExtensionAngle = 0
  FormatSpec = %.0w
  FormatSpecOverTolerance = %+.2w
  FormatSpecUnderTolerance = %+.2w
  Inverted = false
  LineAngle = 0
  LockPosition = false
  MeasureType = 1
  OverTolerance = 0
  References2D = -> [View034]
  Rotation = 0
  Scale = 0.2
  ScaleType = 0
  TheoreticalExact = false
  Type = 2
  UnderTolerance = 0
  X = -85.813
  Y = -3.802
FEATURE [TechDraw::DrawViewDimension] Dimension072
  AngleOverride = false
  Arbitrary = false
  ArbitraryTolerances = false
  BoxCorners = (2) [(-32,-63.5,0),(32,63.5,0)]
  EqualTolerance = true
  ExtensionAngle = 0
  FormatSpec = %.2w
  FormatSpecOverTolerance = %+.2w
  FormatSpecUnderTolerance = %+.2w
  Inverted = false
  LineAngle = 0
  LockPosition = false
  MeasureType = 1
  OverTolerance = 0
  References2D = -> [View025]
  Rotation = 0
  Scale = 0.2
  ScaleType = 0
  TheoreticalExact = false
  Type = 2
  UnderTolerance = 0
  X = -50.1326
  Y = 0
FEATURE [TechDraw::DrawPage] Page006  label="panel_C1_cut"
  KeepUpdated = true
  NextBalloonIndex = 3
  ProjectionType = 0
  Scale = 0.2
  Template = -> Template006
  Views = -> [View025,Annotation006,View034,Balloon026,Dimension070,Dimension071,Dimension072]
FEATURE [Sketcher::SketchObject] Sketch050
  ArcFitTolerance = 1e-06
  AttachmentSupport = -> [XY_Plane041]
  FullyConstrained = true
  MakeInternals = false
  MapMode = 5
  expr: Constraints[10] = <<bdim>>.mbbbp2_h
  expr: Constraints[9] = <<bdim>>.mbbbp2_w
  sketch-geometry (4):
    g0: LineSegment StartX=0 StartY=0 StartZ=0 EndX=30 EndY=0 EndZ=0
    g1: LineSegment StartX=30 StartY=0 StartZ=0 EndX=30 EndY=134.331 EndZ=0
    g2: LineSegment StartX=30 StartY=134.331 StartZ=0 EndX=0 EndY=134.331 EndZ=0
    g3: LineSegment StartX=0 StartY=134.331 StartZ=0 EndX=0 EndY=0 EndZ=0
  constraints (11):
    c: Coincident(g0,g1)
    c: Coincident(g1,g2)
    c: Coincident(g2,g3)
    c: Coincident(g3,g0)
    c: Horizontal(g0)
    c: Horizontal(g2)
    c: Vertical(g1)
    c: Vertical(g3)
    c: Coincident(g0,g-1)
    c: DistanceY(g3,g3) = 134.331
    c: DistanceX(g2,g2) = 30
FEATURE [PartDesign::Pad] Pad038
  Direction = (0,0,1)
  Length = 30
  Length2 = 10
  Profile = -> Sketch050
  ReferenceAxis = -> Sketch050 [N_Axis]
  Suppressed = false
  Type = 0
  expr: Length = <<bdim>>.mbbbp2_t
FEATURE [PartDesign::Body] Body040  label="middle_brace_bar_back_panel_2_model"
  AllowCompound = false
  Group = -> [Sketch050,Pad038]
  Origin = -> Origin041
  Tip = -> Pad038
FEATURE [App::DocumentObjectGroup] Group  label="Models"
  Group = -> [Body003,Body004,Body006,Body007,Body008,Body009,Body010,Body011,Body012,Body013,Body014,Body015,Body016,Body017,Body018,Body019,Body020,Body021,Body022,Joint026,Body023,Body024,Body025,Body026,Body027,Body028,Body030,Body031,Body032,Body001,Body033,Body034,Body035,Body037,Body038,Body039,Body040]
FEATURE [App::Link] middle_brace_bar_back_panel_2_model  label="brace_bar_back_panel_e"
  LinkPlacement = pos=(158,457.669,13) rot=(0,0,1;0rad)
  LinkedObject = -> Body040
  Placement = pos=(158,457.669,13) rot=(0,0,1;0rad)
FEATURE [App::FeaturePython] Joint061  label="Fixed049"  # Assembly joint (typed FeaturePython)
  Activated = true
  AngleMax = 0
  AngleMin = 0
  Detach1 = false
  Detach2 = false
  Distance = 0
  Distance2 = 0
  EnableAngleMax = false
  EnableAngleMin = false
  EnableLengthMax = false
  EnableLengthMin = false
  JointType = 0 (Fixed)
  LengthMax = 0
  LengthMin = 0
  Offset2 = pos=(0,0,0) rot=(0,0,1;3.14159rad)
  Placement1 = pos=(15,0,0) rot=(0.707107,0,0.707107;3.14159rad)
  Placement2 = pos=(1.8e-15,5.68e-14,130) rot=(1,0,0;3.14159rad)
  Reference1 = -> Assembly [middle_brace_bar_back_panel_2_model.Edge3,middle_brace_bar_back_panel_2_model.Edge3]
  Reference2 = -> Assembly [side_panel_001_bar_008.Edge11,side_panel_001_bar_008.Edge11]
FEATURE [App::Link] fin_2_model  label="fin_2"
  LinkPlacement = pos=(13,220.337,207.331) rot=(0,0,1;0rad)
  LinkedObject = -> Body020
  Placement = pos=(13,220.337,207.331) rot=(0,0,1;0rad)
FEATURE [App::FeaturePython] GroundedJoint002  # Assembly grounded joint (typed FeaturePython)
  ObjectToGround = -> front_panel
  Placement = pos=(333,635,687) rot=(0,0,1;3.14159rad)
FEATURE [App::FeaturePython] Joint062  label="Fixed050"  # Assembly joint (typed FeaturePython)
  Activated = true
  AngleMax = 0
  AngleMin = 0
  Detach1 = false
  Detach2 = false
  Distance = 0
  Distance2 = 0
  EnableAngleMax = false
  EnableAngleMin = false
  EnableLengthMax = false
  EnableLengthMin = false
  JointType = 0 (Fixed)
  LengthMax = 0
  LengthMin = 0
  Placement1 = pos=(160,1.137e-13,492.669) rot=(-0.707107,0,0.707107;3.14159rad)
  Placement2 = pos=(160,414.663,13) rot=(-0.707107,0,0.707107;3.14159rad)
  Reference1 = -> Assembly [fin_2_model.Edge9,fin_2_model.Edge9]
  Reference2 = -> Assembly [front_panel.Edge10,front_panel.Edge10]
FEATURE [App::FeaturePython] Joint063  label="Fixed051"  # Assembly joint (typed FeaturePython)
  Activated = true
  AngleMax = 0
  AngleMin = 0
  Detach1 = false
  Detach2 = false
  Distance = 0
  Distance2 = 0
  EnableAngleMax = false
  EnableAngleMin = false
  EnableLengthMax = false
  EnableLengthMin = false
  JointType = 0 (Fixed)
  LengthMax = 0
  LengthMin = 0
  Offset2 = pos=(0,0,-43) rot=(0,0,1;1.5708rad)
  Placement1 = pos=(30,30,449.669) rot=(0,0,1;0rad)
  Placement2 = pos=(0,414.663,-30) rot=(0,0,1;1.5708rad)
  Reference1 = -> Assembly [brace_bar_fin_003.Edge7,brace_bar_fin_003.Vertex6]
  Reference2 = -> Assembly [front_panel.Edge8,front_panel.Vertex8]
  expr: .Offset2.Base.z = -<<bdim>>.fp_t - <<bdim>>.fpb_t
FEATURE [App::FeaturePython] Joint064  label="Fixed052"  # Assembly joint (typed FeaturePython)
  Activated = true
  AngleMax = 0
  AngleMin = 0
  Detach1 = false
  Detach2 = false
  Distance = 0
  Distance2 = 0
  EnableAngleMax = false
  EnableAngleMin = false
  EnableLengthMax = false
  EnableLengthMin = false
  JointType = 0 (Fixed)
  LengthMax = 0
  LengthMin = 0
  Placement1 = pos=(15,1.137e-13,505.669) rot=(-0.707107,0,0.707107;3.14159rad)
  Placement2 = pos=(160,-13,492.669) rot=(-0.707107,0,0.707107;3.14159rad)
  Reference1 = -> Assembly [middle_brace_bar_fin_2.Edge9,middle_brace_bar_fin_2.Edge9]
  Reference2 = -> Assembly [fin_2_model.Edge10,fin_2_model.Edge10]
FEATURE [App::FeaturePython] Joint065  label="Fixed053"  # Assembly joint (typed FeaturePython)
  Activated = true
  AngleMax = 0
  AngleMin = 0
  Detach1 = false
  Detach2 = false
  Distance = 0
  Distance2 = 0
  EnableAngleMax = false
  EnableAngleMin = false
  EnableLengthMax = false
  EnableLengthMin = false
  JointType = 0 (Fixed)
  LengthMax = 0
  LengthMin = 0
  Offset2 = pos=(0,0,-43) rot=(0,0,1;0rad)
  Placement1 = pos=(30,30,449.669) rot=(0,0,1;0rad)
  Placement2 = pos=(320,414.663,-30) rot=(0,0,1;0rad)
  Reference1 = -> Assembly [brace_bar_fin_2.Edge7,brace_bar_fin_2.Vertex6]
  Reference2 = -> Assembly [front_panel.Edge5,front_panel.Vertex6]
  expr: .Offset2.Base.z = -(<<bdim>>.fp_t + <<bdim>>.fpb_t)
FEATURE [App::Link] side_panel_001_bar_009  label="cross_brace_fin_2"
  LinkPlacement = pos=(43,250.337,687) rot=(0,1,0;1.5708rad)
  LinkedObject = -> Body013
  Placement = pos=(43,250.337,687) rot=(0,1,0;1.5708rad)
FEATURE [App::FeaturePython] Joint066  label="Fixed054"  # Assembly joint (typed FeaturePython)
  Activated = true
  AngleMax = 0
  AngleMin = 0
  Detach1 = false
  Detach2 = false
  Distance = 0
  Distance2 = 0
  EnableAngleMax = false
  EnableAngleMin = false
  EnableLengthMax = false
  EnableLengthMin = false
  JointType = 0 (Fixed)
  LengthMax = 0
  LengthMin = 0
  Offset2 = pos=(0,0,0) rot=(0,0,1;3.14159rad)
  Placement1 = pos=(-1.137e-13,-30,130) rot=(0,1,0;3.14159rad)
  Placement2 = pos=(160,414.663,0) rot=(0,1,0;4.71239rad)
  Reference1 = -> Assembly [side_panel_001_bar_009.Edge12,side_panel_001_bar_009.Edge12]
  Reference2 = -> Assembly [front_panel.Edge9,front_panel.Edge9]
FEATURE [App::FeaturePython] Joint067  label="Fixed055"  # Assembly joint (typed FeaturePython)
  Activated = true
  AngleMax = 0
  AngleMin = 0
  Detach1 = false
  Detach2 = false
  Distance = 0
  Distance2 = 0
  EnableAngleMax = false
  EnableAngleMin = false
  EnableLengthMax = false
  EnableLengthMin = false
  JointType = 0 (Fixed)
  LengthMax = 0
  LengthMin = 0
  Offset2 = pos=(0,0,0) rot=(0,0,1;3.14159rad)
  Placement1 = pos=(160,-13,479.669) rot=(-0.707107,0,0.707107;3.14159rad)
  Placement2 = pos=(15,30,285.337) rot=(0,-1,0;4.71239rad)
  Reference1 = -> Assembly [fin_1_model.Edge10,fin_1_model.Edge10]
  Reference2 = -> Assembly [middle_brace_bar_fin_1and_2.Edge5,middle_brace_bar_fin_1and_2.Edge5]
FEATURE [App::FeaturePython] Joint069  label="Fixed057"  # Assembly joint (typed FeaturePython)
  Activated = true
  AngleMax = 0
  AngleMin = 0
  Detach1 = false
  Detach2 = false
  Distance = 0
  Distance2 = 0
  EnableAngleMax = false
  EnableAngleMin = false
  EnableLengthMax = false
  EnableLengthMin = false
  JointType = 0 (Fixed)
  LengthMax = 0
  LengthMin = 0
  Offset2 = pos=(0,0,0) rot=(0,0,1;3.14159rad)
  Placement1 = pos=(15,2.84e-14,285.337) rot=(0.707107,0,0.707107;3.14159rad)
  Placement2 = pos=(160,0,0) rot=(0,-1,0;4.71239rad)
  Reference1 = -> Assembly [middle_brace_bar_fin_1and_003.Edge8,middle_brace_bar_fin_1and_003.Edge8]
  Reference2 = -> Assembly [fin_2_model.Edge3,fin_2_model.Edge3]
FEATURE [TechDraw::DrawSVGTemplate] Template008
  Height = 210
  Orientation = 1
  Template = <path>
  Width = 297
FEATURE [TechDraw::DrawSVGTemplate] Template009
  Height = 210
  Orientation = 1
  Template = <path>
  Width = 297
FEATURE [TechDraw::DrawProjGroupItem] View036  label="Front001"
  CoarseView = false
  Direction = (0,-1,0)
  Focus = 100
  HardHidden = false
  IsoCount = 0
  IsoHidden = false
  IsoVisible = false
  LockPosition = true
  Perspective = false
  Rotation = 0
  RotationVector = (1,0,0)
  Scale = 0.2
  ScaleType = 2
  ScrubCount = 1
  SeamHidden = false
  SeamVisible = true
  SmoothHidden = false
  SmoothVisible = true
  Type = 0
  X = 0
  XDirection = (1,0,0)
  XSource = -> [side_panel_001_bar_001,side_panel_001_bar_002,side_panel_001_bar_003,side_panel_001_bar_004,side_panel_001,middle_brace_bar_side_panel_002]
  Y = 0
FEATURE [TechDraw::DrawProjGroupItem] ProjItem017  label="FrontBottomLeft"
  CoarseView = false
  Direction = (-0.57735,-0.57735,-0.57735)
  Focus = 100
  HardHidden = false
  IsoCount = 0
  IsoHidden = false
  IsoVisible = false
  LockPosition = true
  Perspective = false
  Rotation = 0
  RotationVector = (1,0,0)
  Scale = 0.2
  ScaleType = 0
  ScrubCount = 1
  SeamHidden = false
  SeamVisible = true
  SmoothHidden = false
  SmoothVisible = true
  Type = 8
  X = -114.364
  XDirection = (0.707107,-0.707107,0)
  XSource = -> [side_panel_001_bar_001,side_panel_001_bar_002,side_panel_001_bar_003,side_panel_001_bar_004,side_panel_001,middle_brace_bar_side_panel_002]
  Y = 17.5458
FEATURE [TechDraw::DrawProjGroupItem] ProjItem018  label="Top"
  CoarseView = false
  Direction = (0,0,1)
  Focus = 100
  HardHidden = false
  IsoCount = 0
  IsoHidden = false
  IsoVisible = false
  LockPosition = false
  Perspective = false
  Rotation = 0
  RotationVector = (1,0,0)
  Scale = 0.2
  ScaleType = 0
  ScrubCount = 1
  SeamHidden = false
  SeamVisible = true
  SmoothHidden = false
  SmoothVisible = true
  Type = 4
  X = 0
  XDirection = (1,0,0)
  XSource = -> [side_panel_001_bar_001,side_panel_001_bar_002,side_panel_001_bar_003,side_panel_001_bar_004,side_panel_001,middle_brace_bar_side_panel_002]
  Y = -86.7
FEATURE [TechDraw::DrawProjGroupItem] ProjItem019  label="Right"
  CoarseView = false
  Direction = (1,-1e-16,0)
  Focus = 100
  HardHidden = false
  IsoCount = 0
  IsoHidden = false
  IsoVisible = false
  LockPosition = true
  Perspective = false
  Rotation = 0
  RotationVector = (1,0,0)
  Scale = 0.2
  ScaleType = 0
  ScrubCount = 1
  SeamHidden = false
  SeamVisible = true
  SmoothHidden = false
  SmoothVisible = true
  Type = 2
  X = -59.7854
  XDirection = (1e-16,1,0)
  XSource = -> [side_panel_001_bar_001,side_panel_001_bar_002,side_panel_001_bar_003,side_panel_001_bar_004,side_panel_001,middle_brace_bar_side_panel_002]
  Y = 0
FEATURE [TechDraw::DrawProjGroupItem] ProjItem020  label="Rear001"
  CoarseView = false
  Direction = (0,1,0)
  Focus = 100
  HardHidden = false
  IsoCount = 0
  IsoHidden = false
  IsoVisible = false
  LockPosition = true
  Perspective = false
  Rotation = 0
  RotationVector = (1,0,0)
  Scale = 0.2
  ScaleType = 0
  ScrubCount = 1
  SeamHidden = false
  SeamVisible = true
  SmoothHidden = false
  SmoothVisible = true
  Type = 3
  X = 98.8312
  XDirection = (-1,0,0)
  XSource = -> [side_panel_001_bar_001,side_panel_001_bar_002,side_panel_001_bar_003,side_panel_001_bar_004,side_panel_001,middle_brace_bar_side_panel_002]
  Y = 0
FEATURE [TechDraw::DrawProjGroup] ProjGroup013
  Anchor = -> View036
  AutoDistribute = true
  LockPosition = false
  ProjectionType = 0
  Rotation = 0
  Scale = 0.2
  ScaleType = 0
  Views = -> [View036,ProjItem017,ProjItem018,ProjItem019,ProjItem020]
  X = 154.824
  XSource = -> [side_panel_001_bar_001,side_panel_001_bar_002,side_panel_001_bar_003,side_panel_001_bar_004,side_panel_001,middle_brace_bar_side_panel_002]
  Y = 109.535
  spacingX = 15
  spacingY = 15
FEATURE [TechDraw::DrawViewBalloon] Balloon027
  BubbleShape = 0
  EndType = 0
  EndTypeScale = 1
  KinkLength = 5
  LockPosition = false
  OriginX = 15.8257
  OriginY = -67.1744
  Rotation = 0
  Scale = 0.2
  ScaleType = 0
  ShapeScale = 1
  SourceView = -> ProjItem020
  Text = P3
  TextWrapLen = -1
  X = -197.253
  Y = 80.6432
FEATURE [TechDraw::DrawViewDimension] Dimension073
  AngleOverride = false
  Arbitrary = false
  ArbitraryTolerances = false
  BoxCorners = (2) [(-16,-33.7,0),(16,33.7,0)]
  EqualTolerance = true
  ExtensionAngle = 0
  FormatSpec = %.2w
  FormatSpecOverTolerance = %+.2w
  FormatSpecUnderTolerance = %+.2w
  Inverted = false
  LineAngle = 0
  LockPosition = false
  MeasureType = 1
  OverTolerance = 0
  References2D = -> [ProjItem020]
  Rotation = 0
  Scale = 0.2
  ScaleType = 0
  TheoreticalExact = false
  Type = 2
  UnderTolerance = 0
  X = 19.9742
  Y = -15.367
FEATURE [TechDraw::DrawViewDimension] Dimension074
  AngleOverride = false
  Arbitrary = false
  ArbitraryTolerances = false
  BoxCorners = (2) [(-16,-33.7,0),(16,33.7,0)]
  EqualTolerance = true
  ExtensionAngle = 0
  FormatSpec = %.2w
  FormatSpecOverTolerance = %+.2w
  FormatSpecUnderTolerance = %+.2w
  Inverted = false
  LineAngle = 0
  LockPosition = false
  MeasureType = 1
  OverTolerance = 0
  References2D = -> [ProjItem020]
  Rotation = 0
  Scale = 0.2
  ScaleType = 0
  TheoreticalExact = false
  Type = 1
  UnderTolerance = 0
  X = 0
  Y = -23.7814
FEATURE [TechDraw::DrawViewBalloon] Balloon028
  BubbleShape = 0
  EndType = 0
  EndTypeScale = 1
  KinkLength = 5
  LockPosition = false
  OriginX = 144.175
  OriginY = 128.888
  Rotation = 0
  Scale = 0.2
  ScaleType = 0
  ShapeScale = 1
  SourceView = -> View036
  Text = 3
  TextWrapLen = -1
  X = 281.43
  Y = 299.735
FEATURE [TechDraw::DrawViewBalloon] Balloon029
  BubbleShape = 0
  EndType = 0
  EndTypeScale = 1
  KinkLength = 5
  LockPosition = false
  OriginX = -4.19634
  OriginY = 94.4445
  Rotation = 0
  Scale = 0.2
  ScaleType = 0
  ShapeScale = 1
  SourceView = -> View036
  Text = 4
  TextWrapLen = -1
  X = 283.197
  Y = 249.438
FEATURE [TechDraw::DrawViewBalloon] Balloon030
  BubbleShape = 0
  EndType = 0
  EndTypeScale = 1
  KinkLength = 5
  LockPosition = false
  OriginX = 48.7935
  OriginY = -329.474
  Rotation = 0
  Scale = 0.2
  ScaleType = 0
  ShapeScale = 1
  SourceView = -> View036
  Text = 5
  TextWrapLen = -1
  X = 283.197
  Y = 192.952
FEATURE [TechDraw::DrawViewBalloon] Balloon031
  BubbleShape = 0
  EndType = 0
  EndTypeScale = 1
  KinkLength = 5
  LockPosition = false
  OriginX = -1.54685
  OriginY = 324.95
  Rotation = 0
  Scale = 0.2
  ScaleType = 0
  ShapeScale = 1
  SourceView = -> View036
  Text = 1
  TextWrapLen = -1
  X = 280.693
  Y = 398.634
FEATURE [TechDraw::DrawViewBalloon] Balloon032
  BubbleShape = 0
  EndType = 0
  EndTypeScale = 1
  KinkLength = 5
  LockPosition = false
  OriginX = -141.97
  OriginY = 192.476
  Rotation = 0
  Scale = 0.2
  ScaleType = 0
  ShapeScale = 1
  SourceView = -> View036
  Text = 2
  TextWrapLen = -1
  X = 280.879
  Y = 349.6
FEATURE [TechDraw::DrawViewAnnotation] Annotation009
  Font = osifont
  LineSpace = 100
  LockPosition = false
  MaxWidth = -1
  Rotation = 0
  Scale = 0.2
  ScaleType = 0
  Text = Assemblage: Side Panel 1 | Dimensions en mm | Échelle 1 pour 5 | Répéter pour prime
  TextSize = 5
  TextStyle = 0
  X = 41.9275
  Y = 22.8352
FEATURE [TechDraw::DrawViewSection] SectionView  label="Section A - A"
  BaseView = -> View036
  Caption = Section A - A
  CoarseView = false
  CutSurfaceDisplay = 2
  Direction = (1e-16,0,-1)
  FileGeomPattern = <path>
  FileHatchPattern = <path>
  Focus = 100
  FuseBeforeCut = false
  HardHidden = false
  HatchOffset = (0,0,0)
  HatchRotation = 0
  HatchScale = 1
  IsoCount = 0
  IsoHidden = false
  IsoVisible = false
  LockPosition = false
  NameGeomPattern = Diamond
  Perspective = false
  Rotation = 0
  Scale = 0.2
  ScaleType = 0
  ScrubCount = 1
  SeamHidden = false
  SeamVisible = true
  SectionDirection = 4
  SectionLineStretch = 1
  SectionNormal = (1e-16,0,-1)
  SectionOrigin = (173,613.5,350)
  SectionSymbol = A
  SmoothHidden = false
  SmoothVisible = true
  TrimAfterCut = false
  UsePreviousCut = false
  X = 154.824
  XDirection = (1,0,1e-16)
  Y = 202.85
FEATURE [TechDraw::DrawViewDimension] Dimension075
  AngleOverride = false
  Arbitrary = false
  ArbitraryTolerances = false
  BoxCorners = (2) [(-32,-67.4,0),(32,67.4,0)]
  EqualTolerance = true
  ExtensionAngle = 0
  FormatSpec = %.2w
  FormatSpecOverTolerance = %+.2w
  FormatSpecUnderTolerance = %+.2w
  Inverted = false
  LineAngle = 0
  LockPosition = false
  MeasureType = 1
  OverTolerance = 0
  References2D = -> [View036]
  Rotation = 0
  Scale = 0.2
  ScaleType = 0
  TheoreticalExact = false
  Type = 1
  UnderTolerance = 0
  X = -36.8201
  Y = -67.5067
FEATURE [TechDraw::DrawViewDimension] Dimension076
  AngleOverride = false
  Arbitrary = false
  ArbitraryTolerances = false
  BoxCorners = (2) [(-32,-67.4,0),(32,67.4,0)]
  EqualTolerance = true
  ExtensionAngle = 0
  FormatSpec = %.2w
  FormatSpecOverTolerance = %+.2w
  FormatSpecUnderTolerance = %+.2w
  Inverted = false
  LineAngle = 0
  LockPosition = false
  MeasureType = 1
  OverTolerance = 0
  References2D = -> [View036]
  Rotation = 0
  Scale = 0.2
  ScaleType = 0
  TheoreticalExact = false
  Type = 2
  UnderTolerance = 0
  X = -19.266
  Y = -53.9732
FEATURE [TechDraw::DrawViewDimension] Dimension077
  AngleOverride = false
  Arbitrary = false
  ArbitraryTolerances = false
  BoxCorners = (2) [(-32,-67.4,0),(32,67.4,0)]
  EqualTolerance = true
  ExtensionAngle = 0
  FormatSpec = %.2w
  FormatSpecOverTolerance = %+.2w
  FormatSpecUnderTolerance = %+.2w
  Inverted = false
  LineAngle = 0
  LockPosition = false
  MeasureType = 1
  OverTolerance = 0
  References2D = -> [View036]
  Rotation = 0
  Scale = 0.2
  ScaleType = 0
  TheoreticalExact = false
  Type = 1
  UnderTolerance = 0
  X = -14.5
  Y = 38.0903
FEATURE [TechDraw::DrawViewDimension] Dimension078
  AngleOverride = false
  Arbitrary = false
  ArbitraryTolerances = false
  BoxCorners = (2) [(-32,-67.4,0),(32,67.4,0)]
  EqualTolerance = true
  ExtensionAngle = 0
  FormatSpec = %.2w
  FormatSpecOverTolerance = %+.2w
  FormatSpecUnderTolerance = %+.2w
  Inverted = false
  LineAngle = 0
  LockPosition = false
  MeasureType = 1
  OverTolerance = 0
  References2D = -> [View036]
  Rotation = 0
  Scale = 0.2
  ScaleType = 0
  TheoreticalExact = false
  Type = 1
  UnderTolerance = 0
  X = 14.5
  Y = 38.0903
FEATURE [TechDraw::DrawPage] Page009  label="side_panel_assembly_1"
  KeepUpdated = true
  NextBalloonIndex = 8
  ProjectionType = 0
  Scale = 0.2
  Template = -> Template009
  Views = -> [ProjGroup013,Balloon027,Dimension073,Dimension074,Balloon028,Balloon029,Balloon030,Balloon031,Balloon032,Annotation009,SectionView,Dimension075,Dimension076,Dimension077,Dimension078]
FEATURE [TechDraw::DrawSVGTemplate] Template010
  Height = 210
  Orientation = 1
  Template = <path>
  Width = 297
FEATURE [TechDraw::DrawProjGroupItem] View037  label="Front002"
  CoarseView = false
  Direction = (-2e-16,1,0)
  Focus = 100
  HardHidden = false
  IsoCount = 0
  IsoHidden = false
  IsoVisible = false
  LockPosition = true
  Perspective = false
  Rotation = 0
  RotationVector = (1,0,0)
  Scale = 0.2
  ScaleType = 2
  ScrubCount = 1
  SeamHidden = false
  SeamVisible = true
  SmoothHidden = false
  SmoothVisible = true
  Type = 0
  X = 0
  XDirection = (-1,-2e-16,0)
  XSource = -> [side_panel_002_bar_001,side_panel_002_bar_004,side_panel_002_bar_002,side_panel_002,middle_brace_bar_side_panel_1]
  Y = 0
FEATURE [TechDraw::DrawProjGroupItem] ProjItem021  label="FrontBottomLeft001"
  CoarseView = false
  Direction = (0.57735,0.57735,-0.57735)
  Focus = 100
  HardHidden = false
  IsoCount = 0
  IsoHidden = false
  IsoVisible = false
  LockPosition = true
  Perspective = false
  Rotation = 0
  RotationVector = (1,0,0)
  ScaleType = 2
  ScrubCount = 1
  SeamHidden = false
  SeamVisible = true
  SmoothHidden = false
  SmoothVisible = true
  Type = 8
  X = 120.234
  XDirection = (-0.707107,0.707107,0)
  XSource = -> [side_panel_002_bar_001,side_panel_002_bar_004,side_panel_002_bar_002,side_panel_002,middle_brace_bar_side_panel_1]
  Y = 0.238137
FEATURE [TechDraw::DrawProjGroupItem] ProjItem022  label="Left001"
  CoarseView = false
  Direction = (1,3e-16,0)
  Focus = 100
  HardHidden = false
  IsoCount = 0
  IsoHidden = false
  IsoVisible = false
  LockPosition = false
  Perspective = false
  Rotation = 0
  RotationVector = (1,0,0)
  ScaleType = 2
  ScrubCount = 1
  SeamHidden = false
  SeamVisible = true
  SmoothHidden = false
  SmoothVisible = true
  Type = 1
  X = 72.668
  XDirection = (-3e-16,1,0)
  XSource = -> [side_panel_002_bar_001,side_panel_002_bar_004,side_panel_002_bar_002,side_panel_002,middle_brace_bar_side_panel_1]
  Y = 0
FEATURE [TechDraw::DrawProjGroup] ProjGroup014
  Anchor = -> View037
  AutoDistribute = true
  LockPosition = false
  ProjectionType = 0
  Rotation = 0
  Scale = 0.2
  ScaleType = 0
  Views = -> [View037,ProjItem021,ProjItem022]
  X = 138.987
  XSource = -> [side_panel_002_bar_001,side_panel_002_bar_004,side_panel_002_bar_002,side_panel_002,middle_brace_bar_side_panel_1]
  Y = 104.568
  spacingX = 15
  spacingY = 15
FEATURE [TechDraw::DrawViewSection] SectionView001  label="Section001 A - A"
  BaseView = -> View037
  CoarseView = false
  CutSurfaceDisplay = 2
  Direction = (-1e-16,0,1)
  FileGeomPattern = <path>
  FileHatchPattern = <path>
  Focus = 100
  FuseBeforeCut = false
  HardHidden = false
  HatchOffset = (0,0,0)
  HatchRotation = 0
  HatchScale = 1
  IsoCount = 0
  IsoHidden = false
  IsoVisible = false
  LockPosition = false
  NameGeomPattern = Diamond
  Perspective = false
  Rotation = 0
  Scale = 0.2
  ScaleType = 0
  ScrubCount = 1
  SeamHidden = false
  SeamVisible = true
  SectionDirection = 4
  SectionLineStretch = 1
  SectionNormal = (-1e-16,0,1)
  SectionOrigin = (173,21.5,356.5)
  SectionSymbol = A
  SmoothHidden = false
  SmoothVisible = true
  TrimAfterCut = false
  UsePreviousCut = false
  X = 40.6101
  XDirection = (-1,-2e-16,-1e-16)
  Y = 85.4587
FEATURE [TechDraw::DrawViewAnnotation] Annotation010
  Font = osifont
  LineSpace = 100
  LockPosition = false
  MaxWidth = -1
  Rotation = 0
  Scale = 0.2
  ScaleType = 0
  Text = Assemblage: Side Panel 2 | Dimensions en mm | Échelle 1 pour 5 | Répéter pour prime
  TextSize = 5
  TextStyle = 0
  X = 40.6101
  Y = 22.8352
FEATURE [TechDraw::DrawViewDimension] Dimension079
  AngleOverride = false
  Arbitrary = false
  ArbitraryTolerances = false
  BoxCorners = (2) [(-32,-68.7,0),(32,68.7,0)]
  EqualTolerance = true
  ExtensionAngle = 0
  FormatSpec = %.2w
  FormatSpecOverTolerance = %+.2w
  FormatSpecUnderTolerance = %+.2w
  Inverted = false
  LineAngle = 0
  LockPosition = false
  MeasureType = 1
  OverTolerance = 0
  References2D = -> [View037]
  Rotation = 0
  Scale = 0.2
  ScaleType = 0
  TheoreticalExact = false
  Type = 2
  UnderTolerance = 0
  X = -52.6422
  Y = -3.02752
FEATURE [TechDraw::DrawViewBalloon] Balloon033
  BubbleShape = 0
  EndType = 0
  EndTypeScale = 1
  KinkLength = 5
  LockPosition = false
  OriginX = -58.555
  OriginY = 249.771
  Rotation = 0
  Scale = 0.2
  ScaleType = 0
  ShapeScale = 1
  SourceView = -> View037
  Text = P4
  TextWrapLen = -1
  X = -445.711
  Y = 327.752
FEATURE [TechDraw::DrawViewDimension] Dimension080
  AngleOverride = false
  Arbitrary = false
  ArbitraryTolerances = false
  BoxCorners = (2) [(-32,-68.7,0),(32,68.7,0)]
  EqualTolerance = true
  ExtensionAngle = 0
  FormatSpec = %.2w
  FormatSpecOverTolerance = %+.2w
  FormatSpecUnderTolerance = %+.2w
  Inverted = false
  LineAngle = 0
  LockPosition = false
  MeasureType = 1
  OverTolerance = 0
  References2D = -> [View037]
  Rotation = 0
  Scale = 0.2
  ScaleType = 0
  TheoreticalExact = false
  Type = 1
  UnderTolerance = 0
  X = -35.7798
  Y = -73.0807
FEATURE [TechDraw::DrawViewDimension] Dimension081
  AngleOverride = false
  Arbitrary = false
  ArbitraryTolerances = false
  BoxCorners = (2) [(-32,-68.7,0),(32,68.7,0)]
  EqualTolerance = true
  ExtensionAngle = 0
  FormatSpec = %.2w
  FormatSpecOverTolerance = %+.2w
  FormatSpecUnderTolerance = %+.2w
  Inverted = false
  LineAngle = 0
  LockPosition = false
  MeasureType = 1
  OverTolerance = 0
  References2D = -> [View037]
  Rotation = 0
  Scale = 0.2
  ScaleType = 0
  TheoreticalExact = false
  Type = 1
  UnderTolerance = 0
  X = -14.5
  Y = 13.1266
FEATURE [TechDraw::DrawViewDimension] Dimension082
  AngleOverride = false
  Arbitrary = false
  ArbitraryTolerances = false
  BoxCorners = (2) [(-32,-68.7,0),(32,68.7,0)]
  EqualTolerance = true
  ExtensionAngle = 0
  FormatSpec = %.2w
  FormatSpecOverTolerance = %+.2w
  FormatSpecUnderTolerance = %+.2w
  Inverted = false
  LineAngle = 0
  LockPosition = false
  MeasureType = 1
  OverTolerance = 0
  References2D = -> [View037]
  Rotation = 0
  Scale = 0.2
  ScaleType = 0
  TheoreticalExact = false
  Type = 1
  UnderTolerance = 0
  X = 14.5
  Y = 13.1266
FEATURE [TechDraw::DrawViewDimension] Dimension083
  AngleOverride = false
  Arbitrary = false
  ArbitraryTolerances = false
  BoxCorners = (2) [(-32,-68.7,0),(32,68.7,0)]
  EqualTolerance = true
  ExtensionAngle = 0
  FormatSpec = %.2w
  FormatSpecOverTolerance = %+.2w
  FormatSpecUnderTolerance = %+.2w
  Inverted = false
  LineAngle = 0
  LockPosition = false
  MeasureType = 1
  OverTolerance = 0
  References2D = -> [View037]
  Rotation = 0
  Scale = 0.2
  ScaleType = 0
  TheoreticalExact = false
  Type = 1
  UnderTolerance = 0
  X = 0
  Y = 77.7303
FEATURE [TechDraw::DrawViewDimension] Dimension084
  AngleOverride = false
  Arbitrary = false
  ArbitraryTolerances = false
  BoxCorners = (2) [(-32,-68.7,0),(32,68.7,0)]
  EqualTolerance = true
  ExtensionAngle = 0
  FormatSpec = %.2w
  FormatSpecOverTolerance = %+.2w
  FormatSpecUnderTolerance = %+.2w
  Inverted = false
  LineAngle = 0
  LockPosition = false
  MeasureType = 1
  OverTolerance = 0
  References2D = -> [View037]
  Rotation = 0
  Scale = 0.2
  ScaleType = 0
  TheoreticalExact = false
  Type = 1
  UnderTolerance = 0
  X = -8.60092
  Y = 62.6072
FEATURE [TechDraw::DrawViewBalloon] Balloon034
  BubbleShape = 0
  EndType = 0
  EndTypeScale = 1
  KinkLength = 5
  LockPosition = false
  OriginX = -143.376
  OriginY = 228.53
  Rotation = 0
  Scale = 0.2
  ScaleType = 0
  ShapeScale = 1
  SourceView = -> View037
  Text = 1
  TextWrapLen = -1
  X = -453.402
  Y = 249.438
FEATURE [TechDraw::DrawViewBalloon] Balloon035
  BubbleShape = 0
  EndType = 0
  EndTypeScale = 1
  KinkLength = 5
  LockPosition = false
  OriginX = -3.92519
  OriginY = 155.682
  Rotation = 0
  Scale = 0.2
  ScaleType = 0
  ShapeScale = 1
  SourceView = -> View037
  Text = 2
  TextWrapLen = -1
  X = -455.483
  Y = 172.428
FEATURE [TechDraw::DrawViewBalloon] Balloon036
  BubbleShape = 0
  EndType = 0
  EndTypeScale = 1
  KinkLength = 5
  LockPosition = false
  OriginX = 152.176
  OriginY = 84.9165
  Rotation = 0
  Scale = 0.2
  ScaleType = 0
  ShapeScale = 1
  SourceView = -> View037
  Text = 3
  TextWrapLen = -1
  X = 248.013
  Y = 203.649
FEATURE [TechDraw::DrawViewBalloon] Balloon037
  BubbleShape = 0
  EndType = 0
  EndTypeScale = 1
  KinkLength = 5
  LockPosition = false
  OriginX = 27.2951
  OriginY = -329.272
  Rotation = 0
  Scale = 0.2
  ScaleType = 0
  ShapeScale = 1
  SourceView = -> View037
  Text = 4
  TextWrapLen = -1
  X = 255.763
  Y = -135.611
FEATURE [TechDraw::DrawPage] Page010  label="side_panel_assembly_2"
  KeepUpdated = true
  NextBalloonIndex = 6
  ProjectionType = 0
  Scale = 0.2
  Template = -> Template010
  Views = -> [ProjGroup014,SectionView001,Annotation010,Dimension079,Balloon033,Dimension080,Dimension081,Dimension082,Dimension083,Dimension084,Balloon034,Balloon035,Balloon036,Balloon037]
FEATURE [TechDraw::DrawSVGTemplate] Template011
  Height = 210
  Orientation = 1
  Template = <path>
  Width = 297
FEATURE [TechDraw::DrawProjGroupItem] View038  label="Front003"
  CoarseView = false
  Direction = (0,0,-1)
  Focus = 100
  HardHidden = false
  IsoCount = 0
  IsoHidden = false
  IsoVisible = false
  LockPosition = true
  Perspective = false
  Rotation = 0
  RotationVector = (1,0,0)
  Scale = 0.2
  ScaleType = 2
  ScrubCount = 1
  SeamHidden = false
  SeamVisible = true
  SmoothHidden = false
  SmoothVisible = true
  Type = 0
  X = 0
  XDirection = (-1,-2e-16,0)
  XSource = -> [side_panel_001_bar_009,fp_bar_1,fp_bar_002,front_panel]
  Y = 0
FEATURE [TechDraw::DrawProjGroupItem] ProjItem023  label="Left002"
  CoarseView = false
  Direction = (1,2e-16,-1e-16)
  Focus = 100
  HardHidden = false
  IsoCount = 0
  IsoHidden = false
  IsoVisible = false
  LockPosition = false
  Perspective = false
  Rotation = 0
  RotationVector = (1,0,0)
  ScaleType = 2
  ScrubCount = 1
  SeamHidden = false
  SeamVisible = true
  SmoothHidden = false
  SmoothVisible = true
  Type = 1
  X = 72.668
  XDirection = (-1e-16,0,-1)
  XSource = -> [side_panel_001_bar_009,fp_bar_1,fp_bar_002,front_panel]
  Y = 0
FEATURE [TechDraw::DrawProjGroupItem] ProjItem024  label="FrontTopLeft001"
  CoarseView = false
  Direction = (0.57735,0.57735,-0.57735)
  Focus = 100
  HardHidden = false
  IsoCount = 0
  IsoHidden = false
  IsoVisible = false
  LockPosition = true
  Perspective = false
  Rotation = 0
  RotationVector = (1,0,0)
  ScaleType = 2
  ScrubCount = 1
  SeamHidden = false
  SeamVisible = true
  SmoothHidden = false
  SmoothVisible = true
  Type = 6
  X = 142.198
  XDirection = (-0.707107,-2e-16,-0.707107)
  XSource = -> [side_panel_001_bar_009,fp_bar_1,fp_bar_002,front_panel]
  Y = -18.6227
FEATURE [TechDraw::DrawProjGroup] ProjGroup015
  Anchor = -> View038
  AutoDistribute = true
  LockPosition = false
  ProjectionType = 0
  Rotation = 0
  Scale = 0.2
  ScaleType = 0
  Views = -> [View038,ProjItem023,ProjItem024]
  X = 112.85
  XSource = -> [side_panel_001_bar_009,fp_bar_1,fp_bar_002,front_panel]
  Y = 124.596
  spacingX = 15
  spacingY = 15
FEATURE [TechDraw::DrawViewDimension] Dimension085
  AngleOverride = false
  Arbitrary = false
  ArbitraryTolerances = false
  BoxCorners = (2) [(-32,-41.4663,0),(32,41.4663,0)]
  EqualTolerance = true
  ExtensionAngle = 0
  FormatSpec = ⌀%.2w
  FormatSpecOverTolerance = %+.2w
  FormatSpecUnderTolerance = %+.2w
  Inverted = false
  LineAngle = 0
  LockPosition = false
  MeasureType = 1
  OverTolerance = 0
  References2D = -> [View038]
  Rotation = 0
  Scale = 0.2
  ScaleType = 0
  TheoreticalExact = false
  Type = 5
  UnderTolerance = 0
  X = 14.159
  Y = 5.37423
FEATURE [TechDraw::DrawViewDimension] Dimension086
  AngleOverride = false
  Arbitrary = false
  ArbitraryTolerances = false
  BoxCorners = (2) [(-32,-41.4663,0),(32,41.4663,0)]
  EqualTolerance = true
  ExtensionAngle = 0
  FormatSpec = %.2w
  FormatSpecOverTolerance = %+.2w
  FormatSpecUnderTolerance = %+.2w
  Inverted = false
  LineAngle = 0
  LockPosition = false
  MeasureType = 1
  OverTolerance = 0
  References2D = -> [View038]
  Rotation = 0
  Scale = 0.2
  ScaleType = 0
  TheoreticalExact = false
  Type = 2
  UnderTolerance = 0
  X = 38.6867
  Y = -22.0831
FEATURE [TechDraw::DrawViewDimension] Dimension087
  AngleOverride = false
  Arbitrary = false
  ArbitraryTolerances = false
  BoxCorners = (2) [(-32,-41.4663,0),(32,41.4663,0)]
  EqualTolerance = true
  ExtensionAngle = 0
  FormatSpec = %.2w
  FormatSpecOverTolerance = %+.2w
  FormatSpecUnderTolerance = %+.2w
  Inverted = false
  LineAngle = 0
  LockPosition = false
  MeasureType = 1
  OverTolerance = 0
  References2D = -> [View038]
  Rotation = 0
  Scale = 0.2
  ScaleType = 0
  TheoreticalExact = false
  Type = 2
  UnderTolerance = 0
  X = 25.6093
  Y = -58.9635
FEATURE [TechDraw::DrawViewDimension] Dimension088
  AngleOverride = false
  Arbitrary = false
  ArbitraryTolerances = false
  BoxCorners = (2) [(-32,-41.4663,0),(32,41.4663,0)]
  EqualTolerance = true
  ExtensionAngle = 0
  FormatSpec = %.2w
  FormatSpecOverTolerance = %+.2w
  FormatSpecUnderTolerance = %+.2w
  Inverted = false
  LineAngle = 0
  LockPosition = false
  MeasureType = 1
  OverTolerance = 0
  References2D = -> [View038]
  Rotation = 0
  Scale = 0.2
  ScaleType = 0
  TheoreticalExact = false
  Type = 2
  UnderTolerance = 0
  X = 38.6867
  Y = 21.8809
FEATURE [TechDraw::DrawViewDimension] Dimension089
  AngleOverride = false
  Arbitrary = false
  ArbitraryTolerances = false
  BoxCorners = (2) [(-32,-41.4663,0),(32,41.4663,0)]
  EqualTolerance = true
  ExtensionAngle = 0
  FormatSpec = %.2w
  FormatSpecOverTolerance = %+.2w
  FormatSpecUnderTolerance = %+.2w
  Inverted = false
  LineAngle = 0
  LockPosition = false
  MeasureType = 1
  OverTolerance = 0
  References2D = -> [View038]
  Rotation = 0
  Scale = 0.2
  ScaleType = 0
  TheoreticalExact = false
  Type = 1
  UnderTolerance = 0
  X = -39.459
  Y = -43.4591
FEATURE [TechDraw::DrawViewDimension] Dimension090
  AngleOverride = false
  Arbitrary = false
  ArbitraryTolerances = false
  BoxCorners = (2) [(-32,-41.4663,0),(32,41.4663,0)]
  EqualTolerance = true
  ExtensionAngle = 0
  FormatSpec = %.2w
  FormatSpecOverTolerance = %+.2w
  FormatSpecUnderTolerance = %+.2w
  Inverted = false
  LineAngle = 0
  LockPosition = false
  MeasureType = 1
  OverTolerance = 0
  References2D = -> [View038]
  Rotation = 0
  Scale = 0.2
  ScaleType = 0
  TheoreticalExact = false
  Type = 2
  UnderTolerance = 0
  X = -55.4966
  Y = -2.7
FEATURE [TechDraw::DrawViewDimension] Dimension091
  AngleOverride = false
  Arbitrary = false
  ArbitraryTolerances = false
  BoxCorners = (2) [(-32,-41.4663,0),(32,41.4663,0)]
  EqualTolerance = true
  ExtensionAngle = 0
  FormatSpec = R%.2w
  FormatSpecOverTolerance = %+.2w
  FormatSpecUnderTolerance = %+.2w
  Inverted = false
  LineAngle = 0
  LockPosition = false
  MeasureType = 1
  OverTolerance = 0
  References2D = -> [View038]
  Rotation = 0
  Scale = 0.2
  ScaleType = 0
  TheoreticalExact = false
  Type = 4
  UnderTolerance = 0
  X = -78.2028
  Y = -30.5446
FEATURE [TechDraw::DrawViewDimension] Dimension092
  AngleOverride = false
  Arbitrary = false
  ArbitraryTolerances = false
  BoxCorners = (2) [(-32,-41.4663,0),(32,41.4663,0)]
  EqualTolerance = true
  ExtensionAngle = 0
  FormatSpec = %.2w
  FormatSpecOverTolerance = %+.2w
  FormatSpecUnderTolerance = %+.2w
  Inverted = false
  LineAngle = 0
  LockPosition = false
  MeasureType = 1
  OverTolerance = 0
  References2D = -> [View038]
  Rotation = 0
  Scale = 0.2
  ScaleType = 0
  TheoreticalExact = false
  Type = 2
  UnderTolerance = 0
  X = -96.3386
  Y = -4.33256
FEATURE [TechDraw::DrawViewDimension] Dimension093
  AngleOverride = false
  Arbitrary = false
  ArbitraryTolerances = false
  BoxCorners = (2) [(-32,-41.4663,0),(32,41.4663,0)]
  EqualTolerance = true
  ExtensionAngle = 0
  FormatSpec = %.2w
  FormatSpecOverTolerance = %+.2w
  FormatSpecUnderTolerance = %+.2w
  Inverted = false
  LineAngle = 0
  LockPosition = false
  MeasureType = 1
  OverTolerance = 0
  References2D = -> [View038]
  Rotation = 0
  Scale = 0.2
  ScaleType = 0
  TheoreticalExact = false
  Type = 2
  UnderTolerance = 0
  X = -48.4966
  Y = 25.0351
FEATURE [TechDraw::DrawViewDimension] Dimension094
  AngleOverride = false
  Arbitrary = false
  ArbitraryTolerances = false
  BoxCorners = (2) [(-32,-41.4663,0),(32,41.4663,0)]
  EqualTolerance = true
  ExtensionAngle = 0
  FormatSpec = %.2w
  FormatSpecOverTolerance = %+.2w
  FormatSpecUnderTolerance = %+.2w
  Inverted = false
  LineAngle = 0
  LockPosition = false
  MeasureType = 1
  OverTolerance = 0
  References2D = -> [View038]
  Rotation = 0
  Scale = 0.2
  ScaleType = 0
  TheoreticalExact = false
  Type = 1
  UnderTolerance = 0
  X = -19.8328
  Y = 35.1312
FEATURE [TechDraw::DrawViewAnnotation] Annotation011
  Font = osifont
  LineSpace = 100
  LockPosition = false
  MaxWidth = -1
  Rotation = 0
  Scale = 0.2
  ScaleType = 0
  Text = Assemblage: Front Panel | Dimensions en mm | Échelle 1 pour 5 | Répéter pour prime
  TextSize = 5
  TextStyle = 0
  X = 41.4939
  Y = 22.8352
FEATURE [TechDraw::DrawViewBalloon] Balloon038
  BubbleShape = 0
  EndType = 0
  EndTypeScale = 1
  KinkLength = 5
  LockPosition = false
  OriginX = 89.4668
  OriginY = 164.377
  Rotation = 0
  Scale = 0.2
  ScaleType = 0
  ShapeScale = 1
  SourceView = -> View038
  Text = P5
  TextWrapLen = -1
  X = 267.884
  Y = 239.545
FEATURE [TechDraw::DrawViewBalloon] Balloon039
  BubbleShape = 0
  EndType = 0
  EndTypeScale = 1
  KinkLength = 5
  LockPosition = false
  OriginX = 150.893
  OriginY = 96.4155
  Rotation = 0
  Scale = 0.2
  ScaleType = 0
  ShapeScale = 1
  SourceView = -> View038
  Text = 2
  TextWrapLen = -1
  X = 79.1236
  Y = 263.734
FEATURE [TechDraw::DrawViewBalloon] Balloon041
  BubbleShape = 0
  EndType = 0
  EndTypeScale = 1
  KinkLength = 5
  LockPosition = false
  OriginX = -12.4753
  OriginY = -192.421
  Rotation = 0
  Scale = 0.2
  ScaleType = 0
  ShapeScale = 1
  SourceView = -> View038
  Text = 4
  TextWrapLen = -1
  X = 152.562
  Y = -472.507
FEATURE [TechDraw::DrawViewDimension] Dimension095
  AngleOverride = false
  Arbitrary = false
  ArbitraryTolerances = false
  BoxCorners = (2) [(-32,-41.4663,0),(32,41.4663,0)]
  EqualTolerance = true
  ExtensionAngle = 0
  FormatSpec = %.2w
  FormatSpecOverTolerance = %+.2w
  FormatSpecUnderTolerance = %+.2w
  Inverted = false
  LineAngle = 0
  LockPosition = false
  MeasureType = 1
  OverTolerance = 0
  References2D = -> [View038]
  Rotation = 0
  Scale = 0.2
  ScaleType = 0
  TheoreticalExact = false
  Type = 1
  UnderTolerance = 0
  X = 0
  Y = 47.948
FEATURE [TechDraw::DrawViewDimension] Dimension096
  AngleOverride = false
  Arbitrary = false
  ArbitraryTolerances = false
  BoxCorners = (2) [(-32,-41.4663,0),(32,41.4663,0)]
  EqualTolerance = true
  ExtensionAngle = 0
  FormatSpec = %.2w
  FormatSpecOverTolerance = %+.2w
  FormatSpecUnderTolerance = %+.2w
  Inverted = false
  LineAngle = 0
  LockPosition = false
  MeasureType = 1
  OverTolerance = 0
  References2D = -> [View038]
  Rotation = 0
  Scale = 0.2
  ScaleType = 0
  TheoreticalExact = false
  Type = 1
  UnderTolerance = 0
  X = -13
  Y = 2.44389
FEATURE [TechDraw::DrawViewBalloon] Balloon048
  BubbleShape = 0
  EndType = 0
  EndTypeScale = 1
  KinkLength = 5
  LockPosition = false
  OriginX = -148.6
  OriginY = -148.769
  Rotation = 0
  Scale = 0.2
  ScaleType = 0
  ShapeScale = 1
  SourceView = -> View038
  Text = 3
  TextWrapLen = -1
  X = -21.4617
  Y = -470.131
FEATURE [TechDraw::DrawSVGTemplate] Template013
  Height = 210
  Orientation = 1
  Template = <path>
  Width = 297
FEATURE [TechDraw::DrawProjGroupItem] View040  label="Front005"
  CoarseView = false
  Direction = (0,0,1)
  Focus = 100
  HardHidden = false
  IsoCount = 0
  IsoHidden = false
  IsoVisible = false
  LockPosition = false
  Perspective = false
  Rotation = 0
  RotationVector = (1,0,0)
  Scale = 0.15
  ScaleType = 2
  ScrubCount = 1
  SeamHidden = false
  SeamVisible = true
  SmoothHidden = false
  SmoothVisible = true
  Type = 0
  X = 0
  XDirection = (-1,-2e-16,0)
  XSource = -> [middle_brace_bar_side_panel_002,middle_brace_bar_side_panel_1,side_panel_001_bar_008,brace_bar_back_panel_2,brace_bar_back_panel_1,side_panel_002,side_panel_002_bar_002,side_panel_002_bar_004,side_panel_002_bar_001,side_panel_001_bar_004,side_panel_001_bar_003,side_panel_001_bar_002,side_panel_001_bar_001,side_panel_001,back_panel,fin_1_model]
  Y = 0
FEATURE [TechDraw::DrawProjGroupItem] ProjItem026  label="Left003"
  CoarseView = false
  Direction = (1,2e-16,1e-16)
  Focus = 100
  HardHidden = false
  IsoCount = 0
  IsoHidden = false
  IsoVisible = false
  LockPosition = true
  Perspective = false
  Rotation = 0
  RotationVector = (1,0,0)
  ScaleType = 2
  ScrubCount = 1
  SeamHidden = false
  SeamVisible = true
  SmoothHidden = false
  SmoothVisible = true
  Type = 1
  X = 87.5281
  XDirection = (-1e-16,0,1)
  XSource = <same value as first occurrence — deduplicated (x4 in doc)>
  Y = 0
FEATURE [TechDraw::DrawProjGroupItem] ProjItem027  label="FrontBottomLeft002"
  CoarseView = false
  Direction = (0.57735,0.57735,0.57735)
  Focus = 100
  HardHidden = false
  IsoCount = 0
  IsoHidden = false
  IsoVisible = false
  LockPosition = true
  Perspective = false
  Rotation = 0
  RotationVector = (1,0,0)
  ScaleType = 2
  ScrubCount = 1
  SeamHidden = false
  SeamVisible = true
  SmoothHidden = false
  SmoothVisible = true
  Type = 8
  X = -94.7577
  XDirection = (-0.707107,-2e-16,0.707107)
  XSource = <same value as first occurrence — deduplicated (x4 in doc)>
  Y = -78.6618
FEATURE [TechDraw::DrawProjGroup] ProjGroup017
  Anchor = -> View040
  AutoDistribute = true
  LockPosition = false
  ProjectionType = 0
  Rotation = 0
  Scale = 0.15
  ScaleType = 0
  Views = -> [View040,ProjItem026,ProjItem027]
  X = 155.105
  XSource = <same value as first occurrence — deduplicated (x4 in doc)>
  Y = 154.937
  spacingX = 15
  spacingY = 15
FEATURE [TechDraw::DrawViewDimension] Dimension101
  AngleOverride = false
  Arbitrary = false
  ArbitraryTolerances = false
  BoxCorners = (2) [(-24,-47.625,0),(24,47.625,0)]
  EqualTolerance = true
  ExtensionAngle = 0
  FormatSpec = %.0w
  FormatSpecOverTolerance = %+.2w
  FormatSpecUnderTolerance = %+.2w
  Inverted = false
  LineAngle = 0
  LockPosition = false
  MeasureType = 1
  OverTolerance = 0
  References2D = -> [View040]
  Rotation = 0
  Scale = 0.15
  ScaleType = 0
  TheoreticalExact = false
  Type = 2
  UnderTolerance = 0
  X = 29.4262
  Y = -28.8501
FEATURE [TechDraw::DrawViewDimension] Dimension102
  AngleOverride = false
  Arbitrary = false
  ArbitraryTolerances = false
  BoxCorners = (2) [(-24,-47.625,0),(24,47.625,0)]
  EqualTolerance = true
  ExtensionAngle = 0
  FormatSpec = %.2w
  FormatSpecOverTolerance = %+.2w
  FormatSpecUnderTolerance = %+.2w
  Inverted = false
  LineAngle = 0
  LockPosition = false
  MeasureType = 1
  OverTolerance = 0
  References2D = -> [View040]
  Rotation = 0
  Scale = 0.15
  ScaleType = 0
  TheoreticalExact = false
  Type = 2
  UnderTolerance = 0
  X = 29.4262
  Y = 13.2999
FEATURE [TechDraw::DrawViewDimension] Dimension103
  AngleOverride = false
  Arbitrary = false
  ArbitraryTolerances = false
  BoxCorners = (2) [(-24,-47.625,0),(24,47.625,0)]
  EqualTolerance = true
  ExtensionAngle = 0
  FormatSpec = %.2w
  FormatSpecOverTolerance = %+.2w
  FormatSpecUnderTolerance = %+.2w
  Inverted = false
  LineAngle = 0
  LockPosition = false
  MeasureType = 1
  OverTolerance = 0
  References2D = -> [View040]
  Rotation = 0
  Scale = 0.15
  ScaleType = 0
  TheoreticalExact = false
  Type = 1
  UnderTolerance = 0
  X = 0
  Y = -2.12951
FEATURE [TechDraw::DrawViewDimension] Dimension104
  AngleOverride = false
  Arbitrary = false
  ArbitraryTolerances = false
  BoxCorners = (2) [(-52.5,-47.625,0),(52.5,47.625,0)]
  EqualTolerance = true
  ExtensionAngle = 0
  FormatSpec = %.2w
  FormatSpecOverTolerance = %+.2w
  FormatSpecUnderTolerance = %+.2w
  Inverted = false
  LineAngle = 0
  LockPosition = false
  MeasureType = 1
  OverTolerance = 0
  References2D = -> [ProjItem026]
  Rotation = 0
  Scale = 0.15
  ScaleType = 0
  TheoreticalExact = false
  Type = 2
  UnderTolerance = 0
  X = -29.0465
  Y = -31.1001
FEATURE [TechDraw::DrawViewDimension] Dimension105
  AngleOverride = false
  Arbitrary = false
  ArbitraryTolerances = false
  BoxCorners = (2) [(-52.5,-47.625,0),(52.5,47.625,0)]
  EqualTolerance = true
  ExtensionAngle = 0
  FormatSpec = %.2w
  FormatSpecOverTolerance = %+.2w
  FormatSpecUnderTolerance = %+.2w
  Inverted = false
  LineAngle = 0
  LockPosition = false
  MeasureType = 1
  OverTolerance = 0
  References2D = -> [ProjItem026]
  Rotation = 0
  Scale = 0.15
  ScaleType = 0
  TheoreticalExact = false
  Type = 2
  UnderTolerance = 0
  X = 32.7926
  Y = -11.4694
FEATURE [TechDraw::DrawViewDimension] Dimension106
  AngleOverride = false
  Arbitrary = false
  ArbitraryTolerances = false
  BoxCorners = (2) [(-52.5,-47.625,0),(52.5,47.625,0)]
  EqualTolerance = true
  ExtensionAngle = 0
  FormatSpec = %.2w
  FormatSpecOverTolerance = %+.2w
  FormatSpecUnderTolerance = %+.2w
  Inverted = false
  LineAngle = 0
  LockPosition = false
  MeasureType = 1
  OverTolerance = 0
  References2D = -> [ProjItem026]
  Rotation = 0
  Scale = 0.15
  ScaleType = 0
  TheoreticalExact = false
  Type = 2
  UnderTolerance = 0
  X = 21.2303
  Y = -31.1001
FEATURE [TechDraw::DrawViewBalloon] Balloon049
  BubbleShape = 0
  EndType = 0
  EndTypeScale = 1
  KinkLength = 5
  LockPosition = false
  OriginX = 9.69287
  OriginY = 289.36
  Rotation = 0
  Scale = 0.15
  ScaleType = 0
  ShapeScale = 1
  SourceView = -> View040
  Text = SASS2
  TextWrapLen = -1
  X = -263.771
  Y = 324.998
FEATURE [TechDraw::DrawViewBalloon] Balloon050
  BubbleShape = 0
  EndType = 0
  EndTypeScale = 1
  KinkLength = 5
  LockPosition = false
  OriginX = -3.11963
  OriginY = -283.999
  Rotation = 0
  Scale = 0.15
  ScaleType = 0
  ShapeScale = 1
  SourceView = -> View040
  Text = SASS1
  TextWrapLen = -1
  X = -57.5295
  Y = -656.568
FEATURE [TechDraw::DrawViewBalloon] Balloon051
  BubbleShape = 0
  EndType = 0
  EndTypeScale = 1
  KinkLength = 5
  LockPosition = false
  OriginX = -91.2056
  OriginY = 113.188
  Rotation = 0
  Scale = 0.15
  ScaleType = 0
  ShapeScale = 1
  SourceView = -> View040
  Text = P6
  TextWrapLen = -1
  X = -274.982
  Y = 184.061
FEATURE [TechDraw::DrawViewBalloon] Balloon052
  BubbleShape = 0
  EndType = 0
  EndTypeScale = 1
  KinkLength = 5
  LockPosition = false
  OriginX = 145.826
  OriginY = 92.368
  Rotation = 0
  Scale = 0.15
  ScaleType = 0
  ShapeScale = 1
  SourceView = -> View040
  Text = 2
  TextWrapLen = -1
  X = -276.098
  Y = 108.496
FEATURE [TechDraw::DrawViewBalloon] Balloon053
  BubbleShape = 0
  EndType = 0
  EndTypeScale = 1
  KinkLength = 5
  LockPosition = false
  OriginX = 141.021
  OriginY = -211.929
  Rotation = 0
  Scale = 0.15
  ScaleType = 0
  ShapeScale = 1
  SourceView = -> View040
  Text = 1
  TextWrapLen = -1
  X = 255.222
  Y = -559.257
FEATURE [TechDraw::DrawViewBalloon] Balloon054
  BubbleShape = 0
  EndType = 0
  EndTypeScale = 1
  KinkLength = 5
  LockPosition = false
  OriginX = -27.1431
  OriginY = -123.843
  Rotation = 0
  Scale = 0.15
  ScaleType = 0
  ShapeScale = 1
  SourceView = -> View040
  Text = 3
  TextWrapLen = -1
  X = -204.144
  Y = -486.928
FEATURE [TechDraw::DrawViewBalloon] Balloon055
  BubbleShape = 0
  EndType = 0
  EndTypeScale = 1
  KinkLength = 5
  LockPosition = false
  OriginX = -7.92432
  OriginY = -103.023
  Rotation = 0
  Scale = 0.15
  ScaleType = 0
  ShapeScale = 1
  SourceView = -> View040
  Text = P8
  TextWrapLen = -1
  X = -279.967
  Y = 9.31042
FEATURE [TechDraw::DrawViewDimension] Dimension107
  AngleOverride = false
  Arbitrary = false
  ArbitraryTolerances = false
  BoxCorners = (2) [(-52.5,-47.625,0),(52.5,47.625,0)]
  EqualTolerance = true
  ExtensionAngle = 0
  FormatSpec = %.2w
  FormatSpecOverTolerance = %+.2w
  FormatSpecUnderTolerance = %+.2w
  Inverted = false
  LineAngle = 0
  LockPosition = false
  MeasureType = 1
  OverTolerance = 0
  References2D = -> [ProjItem026]
  Rotation = 0
  Scale = 0.15
  ScaleType = 0
  TheoreticalExact = false
  Type = 1
  UnderTolerance = 0
  X = -14.5749
  Y = -5.47555
FEATURE [TechDraw::DrawViewAnnotation] Annotation013
  Font = osifont
  LineSpace = 100
  LockPosition = false
  MaxWidth = -1
  Rotation = 0
  Scale = 0.15
  ScaleType = 0
  Text = Assemblage: Back Side assembly | Dimensions en mm | Échelle 1 pour 5 | Répéter pour prime
  TextSize = 5
  TextStyle = 0
  X = 242.633
  Y = 25.7734
FEATURE [TechDraw::DrawSVGTemplate] Template014
  Height = 210
  Orientation = 1
  Template = <path>
  Width = 297
FEATURE [TechDraw::DrawProjGroupItem] View041  label="Front006"
  CoarseView = false
  Direction = (-1,-1e-16,0)
  Focus = 100
  HardHidden = false
  IsoCount = 0
  IsoHidden = false
  IsoVisible = false
  LockPosition = true
  Perspective = false
  Rotation = 0
  RotationVector = (1,0,0)
  Scale = 0.15
  ScaleType = 2
  ScrubCount = 1
  SeamHidden = false
  SeamVisible = true
  SmoothHidden = false
  SmoothVisible = true
  Type = 0
  X = 0
  XDirection = (1e-16,-1,0)
  XSource = -> [back_panel,side_panel_001,side_panel_001_bar_001,side_panel_001_bar_002,side_panel_001_bar_003,side_panel_001_bar_004,side_panel_002_bar_001,side_panel_002_bar_004,side_panel_002_bar_002,side_panel_002,front_panel,fp_bar_1,fp_bar_002,brace_bar_back_panel_1,brace_bar_back_panel_2,side_panel_001_bar_008,driver_brace_bar,driver_brace_bar001,middle_brace_bar_side_panel_1,+3 more]
  Y = 0
FEATURE [TechDraw::DrawViewSection] SectionView002  label="Section002 A - A"
  BaseView = -> View041
  Caption = Section A - A
  CoarseView = false
  CutSurfaceDisplay = 2
  Direction = (0,-1e-16,-1)
  FileGeomPattern = <path>
  FileHatchPattern = <path>
  Focus = 100
  FuseBeforeCut = false
  HardHidden = false
  HatchOffset = (0,0,0)
  HatchRotation = 0
  HatchScale = 1
  IsoCount = 0
  IsoHidden = false
  IsoVisible = false
  LockPosition = false
  NameGeomPattern = Diamond
  Perspective = false
  Rotation = 0
  Scale = 0.15
  ScaleType = 0
  ScrubCount = 1
  SeamHidden = false
  SeamVisible = true
  SectionDirection = 4
  SectionLineStretch = 1
  SectionNormal = (0,-1e-16,-1)
  SectionOrigin = (173,317,500)
  SectionSymbol = A
  SmoothHidden = false
  SmoothVisible = true
  TrimAfterCut = false
  UsePreviousCut = false
  X = 82.6776
  XDirection = (1e-16,-1,1e-16)
  Y = 170.406
FEATURE [TechDraw::DrawProjGroupItem] ProjItem029  label="FrontTopLeft002"
  CoarseView = false
  Direction = (-0.57735,0.57735,0.57735)
  Focus = 100
  HardHidden = false
  IsoCount = 0
  IsoHidden = false
  IsoVisible = false
  LockPosition = true
  Perspective = false
  Rotation = 0
  RotationVector = (1,0,0)
  ScaleType = 2
  ScrubCount = 1
  SeamHidden = false
  SeamVisible = true
  SmoothHidden = false
  SmoothVisible = true
  Type = 6
  X = 143.263
  XDirection = (-0.707107,-0.707107,0)
  XSource = <same value as first occurrence — deduplicated (x3 in doc)>
  Y = 7.82215
FEATURE [TechDraw::DrawProjGroup] ProjGroup018
  Anchor = -> View041
  AutoDistribute = true
  LockPosition = false
  ProjectionType = 0
  Rotation = 0
  Scale = 0.15
  ScaleType = 0
  Views = -> [View041,ProjItem029]
  X = 82.6776
  XSource = <same value as first occurrence — deduplicated (x3 in doc)>
  Y = 66.252
  spacingX = 15
  spacingY = 15
FEATURE [TechDraw::DrawViewDimension] Dimension108
  AngleOverride = false
  Arbitrary = false
  ArbitraryTolerances = false
  BoxCorners = (2) [(-47.625,-24,0),(47.625,24,0)]
  EqualTolerance = true
  ExtensionAngle = 0
  FormatSpec = %.2w
  FormatSpecOverTolerance = %+.2w
  FormatSpecUnderTolerance = %+.2w
  Inverted = false
  LineAngle = 0
  LockPosition = false
  MeasureType = 1
  OverTolerance = 0
  References2D = -> [SectionView002]
  Rotation = 0
  Scale = 0.15
  ScaleType = 0
  TheoreticalExact = false
  Type = 0
  UnderTolerance = 0
  X = -51.5291
  Y = 29.8541
FEATURE [TechDraw::DrawViewDimension] Dimension109
  AngleOverride = false
  Arbitrary = false
  ArbitraryTolerances = false
  BoxCorners = (2) [(-47.625,-24,0),(47.625,24,0)]
  EqualTolerance = true
  ExtensionAngle = 0
  FormatSpec = %.2w
  FormatSpecOverTolerance = %+.2w
  FormatSpecUnderTolerance = %+.2w
  Inverted = false
  LineAngle = 0
  LockPosition = false
  MeasureType = 1
  OverTolerance = 0
  References2D = -> [SectionView002]
  Rotation = 0
  Scale = 0.15
  ScaleType = 0
  TheoreticalExact = false
  Type = 2
  UnderTolerance = 0
  X = -62.8429
  Y = 0
FEATURE [TechDraw::DrawViewDimension] Dimension110
  AngleOverride = false
  Arbitrary = false
  ArbitraryTolerances = false
  BoxCorners = (2) [(-47.625,-24,0),(47.625,24,0)]
  EqualTolerance = true
  ExtensionAngle = 0
  FormatSpec = %.2w
  FormatSpecOverTolerance = %+.2w
  FormatSpecUnderTolerance = %+.2w
  Inverted = false
  LineAngle = 0
  LockPosition = false
  MeasureType = 1
  OverTolerance = 0
  References2D = -> [SectionView002]
  Rotation = 0
  Scale = 0.15
  ScaleType = 0
  TheoreticalExact = false
  Type = 2
  UnderTolerance = 0
  X = -72.0692
  Y = 14.727
FEATURE [TechDraw::DrawViewBalloon] Balloon056
  BubbleShape = 0
  EndType = 0
  EndTypeScale = 1
  KinkLength = 5
  LockPosition = false
  OriginX = 49.4873
  OriginY = 59.8418
  Rotation = 0
  Scale = 0.15
  ScaleType = 0
  ShapeScale = 1
  SourceView = -> SectionView002
  Text = FASS
  TextWrapLen = -1
  X = 304.775
  Y = 211.377
FEATURE [TechDraw::DrawViewBalloon] Balloon057
  BubbleShape = 0
  EndType = 0
  EndTypeScale = 1
  KinkLength = 5
  LockPosition = false
  OriginX = -232.646
  OriginY = 83.5046
  Rotation = 0
  Scale = 0.15
  ScaleType = 0
  ShapeScale = 1
  SourceView = -> SectionView002
  Text = 1
  TextWrapLen = -1
  X = -99.3129
  Y = 218.658
FEATURE [TechDraw::DrawViewBalloon] Balloon058
  BubbleShape = 0
  EndType = 0
  EndTypeScale = 1
  KinkLength = 5
  LockPosition = false
  OriginX = -250.848
  OriginY = -78.4946
  Rotation = 0
  Scale = 0.15
  ScaleType = 0
  ShapeScale = 1
  SourceView = -> Balloon057
  Text = 2
  TextWrapLen = -1
  X = -439.693
  Y = -210.913
FEATURE [TechDraw::DrawViewBalloon] Balloon059
  BubbleShape = 0
  EndType = 0
  EndTypeScale = 1
  KinkLength = 5
  LockPosition = false
  OriginX = -0.841566
  OriginY = -66.2126
  Rotation = 0
  Scale = 0.15
  ScaleType = 0
  ShapeScale = 1
  SourceView = -> View041
  Text = BSASS
  TextWrapLen = -1
  X = 132.492
  Y = 67.1207
FEATURE [TechDraw::DrawViewAnnotation] Annotation014
  Font = osifont
  LineSpace = 100
  LockPosition = false
  MaxWidth = -1
  Rotation = 0
  Scale = 0.15
  ScaleType = 0
  Text = Assemblage: Front add assembly | Dimensions en mm | Échelle 0.15 | Répéter pour prime
  TextSize = 5
  TextStyle = 0
  X = 242.247
  Y = 180.847
FEATURE [TechDraw::DrawPage] Page014  label="front_side_add_assembly"
  KeepUpdated = true
  NextBalloonIndex = 5
  ProjectionType = 0
  Scale = 0.15
  Template = -> Template014
  Views = -> [SectionView002,ProjGroup018,Dimension108,Dimension109,Dimension110,Balloon056,Balloon057,Balloon058,Balloon059,Annotation014]
FEATURE [TechDraw::DrawSVGTemplate] Template015
  Height = 210
  Orientation = 1
  Template = <path>
  Width = 297
FEATURE [TechDraw::DrawProjGroupItem] View042  label="Front007"
  CoarseView = false
  Direction = (1,3e-16,0)
  Focus = 100
  HardHidden = false
  IsoCount = 0
  IsoHidden = false
  IsoVisible = false
  LockPosition = true
  Perspective = false
  Rotation = 0
  RotationVector = (1,0,0)
  Scale = 0.15
  ScaleType = 2
  ScrubCount = 1
  SeamHidden = false
  SeamVisible = true
  SmoothHidden = false
  SmoothVisible = true
  Type = 0
  X = 0
  XDirection = (-3e-16,1,0)
  XSource = -> [side_panel_001_bar_009,fin_1_model,middle_brace_bar_side_panel_002,middle_brace_bar_side_panel_1,driver_brace_bar001,driver_brace_bar,side_panel_001_bar_008,brace_bar_back_panel_2,brace_bar_back_panel_1,fp_bar_002,fp_bar_1,side_panel_002,front_panel,side_panel_002_bar_002,side_panel_002_bar_004,side_panel_002_bar_001,side_panel_001_bar_004,side_panel_001_bar_002,side_panel_001_bar_003,+4 more]
  Y = 0
FEATURE [TechDraw::DrawProjGroupItem] ProjItem030  label="Rear002"
  CoarseView = false
  Direction = (-1,-3e-16,0)
  Focus = 100
  HardHidden = false
  IsoCount = 0
  IsoHidden = false
  IsoVisible = false
  LockPosition = true
  Perspective = false
  Rotation = 0
  RotationVector = (1,0,0)
  ScaleType = 2
  ScrubCount = 1
  SeamHidden = false
  SeamVisible = true
  SmoothHidden = false
  SmoothVisible = true
  Type = 3
  X = 120.698
  XDirection = (3e-16,-1,0)
  XSource = <same value as first occurrence — deduplicated (x3 in doc)>
  Y = 0
FEATURE [TechDraw::DrawProjGroup] ProjGroup019
  Anchor = -> View042
  AutoDistribute = true
  LockPosition = false
  ProjectionType = 0
  Rotation = 0
  Scale = 0.15
  ScaleType = 0
  Views = -> [View042,ProjItem030]
  X = 68.4083
  XSource = <same value as first occurrence — deduplicated (x3 in doc)>
  Y = 122.064
  spacingX = 15
  spacingY = 15
FEATURE [TechDraw::DrawViewBalloon] Balloon060
  BubbleShape = 0
  EndType = 0
  EndTypeScale = 1
  KinkLength = 5
  LockPosition = false
  OriginX = -50.5505
  OriginY = 125.688
  Rotation = 0
  Scale = 0.15
  ScaleType = 0
  ShapeScale = 1
  SourceView = -> View042
  Text = P1
  TextWrapLen = -1
  X = 275.443
  Y = 466.361
FEATURE [TechDraw::DrawViewBalloon] Balloon061
  BubbleShape = 0
  EndType = 0
  EndTypeScale = 1
  KinkLength = 5
  LockPosition = false
  OriginX = 187.982
  OriginY = -358.716
  Rotation = 0
  Scale = 0.15
  ScaleType = 0
  ShapeScale = 1
  SourceView = -> View042
  Text = BSFASS
  TextWrapLen = -1
  X = 396.544
  Y = -562.997
FEATURE [TechDraw::DrawViewAnnotation] Annotation015
  Font = osifont
  LineSpace = 100
  LockPosition = false
  MaxWidth = -1
  Rotation = 0
  Scale = 0.15
  ScaleType = 0
  Text = Assemblage: Bottom add assembly | Dimensions en mm | Échelle 0.15 | Répéter pour prime
  TextSize = 5
  TextStyle = 0
  X = 242.633
  Y = 25.7734
FEATURE [TechDraw::DrawPage] Page015  label="bottom_add_assembly"
  KeepUpdated = true
  NextBalloonIndex = 3
  ProjectionType = 0
  Scale = 0.15
  Template = -> Template015
  Views = -> [ProjGroup019,Balloon060,Balloon061,Annotation015]
FEATURE [TechDraw::DrawSVGTemplate] Template016
  Height = 210
  Orientation = 1
  Template = <path>
  Width = 297
FEATURE [TechDraw::DrawViewAnnotation] Annotation016
  Font = osifont
  LineSpace = 100
  LockPosition = false
  MaxWidth = -1
  Rotation = 0
  Scale = 0.15
  ScaleType = 0
  Text = Assemblage: Bottom Fin support | Dimensions en mm | Échelle 0.15 | Répéter pour prime
  TextSize = 5
  TextStyle = 0
  X = 221.969
  Y = 183.08
FEATURE [TechDraw::DrawProjGroupItem] View043  label="Front008"
  CoarseView = false
  Direction = (1,3e-16,0)
  Focus = 100
  HardHidden = false
  IsoCount = 0
  IsoHidden = false
  IsoVisible = false
  LockPosition = true
  Perspective = false
  Rotation = 0
  RotationVector = (1,0,0)
  Scale = 0.15
  ScaleType = 2
  ScrubCount = 1
  SeamHidden = false
  SeamVisible = true
  SmoothHidden = false
  SmoothVisible = true
  Type = 0
  X = 0
  XDirection = (-3e-16,1,0)
  XSource = -> [bottom_panel,back_panel,side_panel_001,side_panel_001_bar_001,side_panel_001_bar_002,side_panel_001_bar_003,side_panel_001_bar_004,side_panel_002_bar_001,side_panel_002_bar_004,side_panel_002_bar_002,side_panel_002,front_panel,fp_bar_1,fp_bar_002,brace_bar_fin_2,brace_bar_fin_004,brace_bar_back_panel_1,brace_bar_back_panel_2,side_panel_001_bar_008,driver_brace_bar,driver_brace_bar001,+4 more]
  Y = 0
FEATURE [TechDraw::DrawProjGroupItem] ProjItem031  label="FrontTopLeft003"
  CoarseView = false
  Direction = (0.57735,-0.57735,0.57735)
  Focus = 100
  HardHidden = false
  IsoCount = 0
  IsoHidden = false
  IsoVisible = false
  LockPosition = true
  Perspective = false
  Rotation = 0
  RotationVector = (1,0,0)
  ScaleType = 2
  ScrubCount = 1
  SeamHidden = false
  SeamVisible = true
  SmoothHidden = false
  SmoothVisible = true
  Type = 6
  X = 149.988
  XDirection = (0.707107,0.707107,0)
  XSource = <same value as first occurrence — deduplicated (x3 in doc)>
  Y = -0.421812
FEATURE [TechDraw::DrawProjGroup] ProjGroup020
  Anchor = -> View043
  AutoDistribute = true
  LockPosition = false
  ProjectionType = 0
  Rotation = 0
  Scale = 0.15
  ScaleType = 0
  Views = -> [View043,ProjItem031]
  X = 84.7438
  XSource = <same value as first occurrence — deduplicated (x3 in doc)>
  Y = 78.5987
  spacingX = 15
  spacingY = 15
FEATURE [TechDraw::DrawViewBalloon] Balloon062
  BubbleShape = 0
  EndType = 0
  EndTypeScale = 1
  KinkLength = 5
  LockPosition = false
  OriginX = -106.213
  OriginY = 187.532
  Rotation = 0
  Scale = 0.15
  ScaleType = 0
  ShapeScale = 1
  SourceView = -> View043
  Text = P7
  TextWrapLen = -1
  X = -499.501
  Y = 261.439
FEATURE [TechDraw::DrawViewSection] SectionView003  label="Section003 A - A"
  BaseView = -> View043
  Caption = A
  CoarseView = false
  CutSurfaceDisplay = 2
  Direction = (0,1e-16,1)
  FileGeomPattern = <path>
  FileHatchPattern = <path>
  Focus = 100
  FuseBeforeCut = false
  HardHidden = false
  HatchOffset = (0,0,0)
  HatchRotation = 0
  HatchScale = 1
  IsoCount = 0
  IsoHidden = false
  IsoVisible = false
  LockPosition = false
  NameGeomPattern = Diamond
  Perspective = false
  Rotation = 0
  Scale = 0.15
  ScaleType = 0
  ScrubCount = 1
  SeamHidden = false
  SeamVisible = true
  SectionDirection = 4
  SectionLineStretch = 1
  SectionNormal = (0,1e-16,1)
  SectionOrigin = (167.5,317.5,350)
  SectionSymbol = A
  SmoothHidden = false
  SmoothVisible = true
  TrimAfterCut = false
  UsePreviousCut = false
  X = 85.6563
  XDirection = (-3e-16,1,-1e-16)
  Y = 181.317
FEATURE [TechDraw::DrawViewDimension] Dimension111
  AngleOverride = false
  Arbitrary = false
  ArbitraryTolerances = false
  BoxCorners = (2) [(-47.625,-52.5,0),(47.625,52.5,0)]
  EqualTolerance = true
  ExtensionAngle = 0
  FormatSpec = %.2w
  FormatSpecOverTolerance = %+.2w
  FormatSpecUnderTolerance = %+.2w
  Inverted = false
  LineAngle = 0
  LockPosition = false
  MeasureType = 1
  OverTolerance = 0
  References2D = -> [View043]
  Rotation = 0
  Scale = 0.15
  ScaleType = 0
  TheoreticalExact = false
  Type = 2
  UnderTolerance = 0
  X = -23.1253
  Y = -33.9571
FEATURE [TechDraw::DrawViewBalloon] Balloon063
  BubbleShape = 0
  EndType = 0
  EndTypeScale = 1
  KinkLength = 5
  LockPosition = false
  OriginX = -78.446
  OriginY = 106.763
  Rotation = 0
  Scale = 0.15
  ScaleType = 0
  ShapeScale = 1
  SourceView = -> View043
  Text = 2
  TextWrapLen = -1
  X = 54.8873
  Y = 240.097
FEATURE [TechDraw::DrawViewBalloon] Balloon064
  BubbleShape = 0
  EndType = 0
  EndTypeScale = 1
  KinkLength = 5
  LockPosition = false
  OriginX = 126.916
  OriginY = 60.3122
  Rotation = 0
  Scale = 0.15
  ScaleType = 0
  ShapeScale = 1
  SourceView = -> View043
  Text = 3
  TextWrapLen = -1
  X = 10.8812
  Y = -111.953
FEATURE [TechDraw::DrawViewBalloon] Balloon065
  BubbleShape = 0
  EndType = 0
  EndTypeScale = 1
  KinkLength = 5
  LockPosition = false
  OriginX = -104.088
  OriginY = 25.8391
  Rotation = 0
  Scale = 0.15
  ScaleType = 0
  ShapeScale = 1
  SourceView = -> SectionView003
  Text = P7
  TextWrapLen = -1
  X = -212.788
  Y = -99.9749
FEATURE [TechDraw::DrawViewBalloon] Balloon066
  BubbleShape = 0
  EndType = 0
  EndTypeScale = 1
  KinkLength = 5
  LockPosition = false
  OriginX = -86.9745
  OriginY = 135.854
  Rotation = 0
  Scale = 0.15
  ScaleType = 0
  ShapeScale = 1
  SourceView = -> SectionView003
  Text = 2
  TextWrapLen = -1
  X = 19.4662
  Y = -11.9626
FEATURE [TechDraw::DrawViewBalloon] Balloon067
  BubbleShape = 0
  EndType = 0
  EndTypeScale = 1
  KinkLength = 5
  LockPosition = false
  OriginX = 125.722
  OriginY = 135.854
  Rotation = 0
  Scale = 0.15
  ScaleType = 0
  ShapeScale = 1
  SourceView = -> SectionView003
  Text = 3
  TextWrapLen = -1
  X = 202.825
  Y = -9.51782
FEATURE [TechDraw::DrawPage] Page016  label="add_bottom_fin_assembly"
  KeepUpdated = true
  NextBalloonIndex = 11
  ProjectionType = 0
  Scale = 0.15
  Template = -> Template016
  Views = -> [Annotation016,ProjGroup020,Balloon062,SectionView003,Dimension111,Balloon063,Balloon064,Balloon065,Balloon066,Balloon067]
FEATURE [TechDraw::DrawSVGTemplate] Template017
  Height = 210
  Orientation = 1
  Template = <path>
  Width = 297
FEATURE [TechDraw::DrawProjGroupItem] View044  label="View"
  CoarseView = false
  Direction = (0,2e-16,1)
  Focus = 100
  HardHidden = false
  IsoCount = 0
  IsoHidden = false
  IsoVisible = false
  LockPosition = false
  Perspective = false
  Rotation = 0
  RotationVector = (1,0,0)
  Scale = 0.15
  ScaleType = 0
  ScrubCount = 1
  SeamHidden = false
  SeamVisible = true
  SmoothHidden = false
  SmoothVisible = true
  Type = 0
  X = 65.1055
  XDirection = (1,4e-16,0)
  XSource = -> [bottom_panel,back_panel,side_panel_001,side_panel_001_bar_001,side_panel_001_bar_002,side_panel_001_bar_003,side_panel_001_bar_004,side_panel_002_bar_001,side_panel_002_bar_002,side_panel_002_bar_004,side_panel_002,front_panel,fp_bar_1,fp_bar_002,brace_bar_fin_2,brace_bar_fin_004,brace_bar_back_panel_1,brace_bar_back_panel_2,brace_bar_back_panel_005,side_panel_001_bar_008,middle_brace_bar_fin_1,+11 more]
  Y = 105.275
FEATURE [TechDraw::DrawViewSection] SectionView004  label="Section004 A - A"
  BaseView = -> View044
  CoarseView = false
  CutSurfaceDisplay = 2
  Direction = (-1,-5e-16,0)
  FileGeomPattern = <path>
  FileHatchPattern = <path>
  Focus = 100
  FuseBeforeCut = false
  HardHidden = false
  HatchOffset = (0,0,0)
  HatchRotation = 0
  HatchScale = 1
  IsoCount = 0
  IsoHidden = false
  IsoVisible = false
  LockPosition = false
  NameGeomPattern = Diamond
  Perspective = false
  Rotation = -90
  Scale = 0.15
  ScaleType = 0
  ScrubCount = 1
  SeamHidden = false
  SeamVisible = true
  SectionDirection = 4
  SectionLineStretch = 1
  SectionNormal = (-1,-5e-16,0)
  SectionOrigin = (173,317.5,350)
  SectionSymbol = A
  SmoothHidden = false
  SmoothVisible = true
  TrimAfterCut = false
  UsePreviousCut = false
  X = 176.87
  XDirection = (5e-16,-1,2e-16)
  Y = 110.651
FEATURE [TechDraw::DrawViewDimension] Dimension112
  AngleOverride = false
  Arbitrary = false
  ArbitraryTolerances = false
  BoxCorners = (2) [(-24.975,-47.625,0),(24.975,47.625,0)]
  EqualTolerance = true
  ExtensionAngle = 0
  FormatSpec = %.2w
  FormatSpecOverTolerance = %+.2w
  FormatSpecUnderTolerance = %+.2w
  Inverted = false
  LineAngle = 0
  LockPosition = false
  MeasureType = 1
  OverTolerance = 0
  References2D = -> [View044]
  Rotation = 0
  Scale = 0.15
  ScaleType = 0
  TheoreticalExact = false
  Type = 1
  UnderTolerance = 0
  X = 14.1
  Y = -22.6886
FEATURE [TechDraw::DrawViewBalloon] Balloon068
  BubbleShape = 0
  EndType = 0
  EndTypeScale = 1
  KinkLength = 5
  LockPosition = false
  OriginX = -209.721
  OriginY = -326.257
  Rotation = 0
  Scale = 0.15
  ScaleType = 0
  ShapeScale = 1
  SourceView = -> SectionView004
  Text = 1
  TextWrapLen = -1
  X = -188.904
  Y = 502.43
FEATURE [TechDraw::DrawViewBalloon] Balloon069
  BubbleShape = 0
  EndType = 0
  EndTypeScale = 1
  KinkLength = 5
  LockPosition = false
  OriginX = -126.458
  OriginY = -222.741
  Rotation = 0
  Scale = 0.15
  ScaleType = 0
  ShapeScale = 1
  SourceView = -> SectionView004
  Text = 2
  TextWrapLen = -1
  X = -69.6362
  Y = 506.931
FEATURE [TechDraw::DrawViewBalloon] Balloon070
  BubbleShape = 0
  EndType = 0
  EndTypeScale = 1
  KinkLength = 5
  LockPosition = false
  OriginX = -76.9507
  OriginY = -13.4602
  Rotation = 0
  Scale = 0.15
  ScaleType = 0
  ShapeScale = 1
  SourceView = -> SectionView004
  Text = 3
  TextWrapLen = -1
  X = 38.3799
  Y = 506.931
FEATURE [TechDraw::DrawViewBalloon] Balloon071
  BubbleShape = 0
  EndType = 0
  EndTypeScale = 1
  KinkLength = 5
  LockPosition = false
  OriginX = 49.0681
  OriginY = -321.756
  Rotation = 0
  Scale = 0.15
  ScaleType = 0
  ShapeScale = 1
  SourceView = -> SectionView004
  Text = 4
  TextWrapLen = -1
  X = -474.697
  Y = 110.872
FEATURE [TechDraw::DrawViewBalloon] Balloon072
  BubbleShape = 0
  EndType = 0
  EndTypeScale = 1
  KinkLength = 5
  LockPosition = false
  OriginX = 78.3224
  OriginY = 2.29214
  Rotation = 0
  Scale = 0.15
  ScaleType = 0
  ShapeScale = 1
  SourceView = -> SectionView004
  Text = 5
  TextWrapLen = -1
  X = 454.692
  Y = 92.8691
FEATURE [TechDraw::DrawViewBalloon] Balloon073
  BubbleShape = 0
  EndType = 0
  EndTypeScale = 1
  KinkLength = 5
  LockPosition = false
  OriginX = 127.83
  OriginY = 90.0552
  Rotation = 0
  Scale = 0.15
  ScaleType = 0
  ShapeScale = 1
  SourceView = -> SectionView004
  Text = 6
  TextWrapLen = -1
  X = 452.442
  Y = 23.1087
FEATURE [TechDraw::DrawViewAnnotation] Annotation017
  Font = osifont
  LineSpace = 100
  LockPosition = false
  MaxWidth = -1
  Rotation = 0
  Scale = 0.15
  ScaleType = 0
  Text = Assemblage: middle brace | Dimensions en mm | Échelle 0.15 | Répéter pour prime
  TextSize = 5
  TextStyle = 0
  X = 247.96
  Y = 23.419
FEATURE [TechDraw::DrawViewDimension] Dimension113
  AngleOverride = false
  Arbitrary = false
  ArbitraryTolerances = false
  BoxCorners = (2) [(-52.5,-47.625,-1e-07),(52.5,47.625,1e-07)]
  EqualTolerance = true
  ExtensionAngle = 0
  FormatSpec = %.2w
  FormatSpecOverTolerance = %+.2w
  FormatSpecUnderTolerance = %+.2w
  Inverted = false
  LineAngle = 0
  LockPosition = false
  MeasureType = 1
  OverTolerance = 0
  References2D = -> [SectionView004]
  Rotation = 0
  Scale = 0.15
  ScaleType = 0
  TheoreticalExact = false
  Type = 2
  UnderTolerance = 0
  X = -59.3332
  Y = 31.1001
FEATURE [TechDraw::DrawViewDimension] Dimension114
  AngleOverride = false
  Arbitrary = false
  ArbitraryTolerances = false
  BoxCorners = (2) [(-52.5,-47.625,-1e-07),(52.5,47.625,1e-07)]
  EqualTolerance = true
  ExtensionAngle = 0
  FormatSpec = %.2w
  FormatSpecOverTolerance = %+.2w
  FormatSpecUnderTolerance = %+.2w
  Inverted = false
  LineAngle = 0
  LockPosition = false
  MeasureType = 1
  OverTolerance = 0
  References2D = -> [SectionView004]
  Rotation = 0
  Scale = 0.15
  ScaleType = 0
  TheoreticalExact = false
  Type = 1
  UnderTolerance = 0
  X = -12.3249
  Y = 28.6042
FEATURE [TechDraw::DrawViewDimension] Dimension115
  AngleOverride = false
  Arbitrary = false
  ArbitraryTolerances = false
  BoxCorners = (2) [(-52.5,-47.625,-1e-07),(52.5,47.625,1e-07)]
  EqualTolerance = true
  ExtensionAngle = 0
  FormatSpec = %.2w
  FormatSpecOverTolerance = %+.2w
  FormatSpecUnderTolerance = %+.2w
  Inverted = false
  LineAngle = 0
  LockPosition = false
  MeasureType = 1
  OverTolerance = 0
  References2D = -> [SectionView004]
  Rotation = 0
  Scale = 0.15
  ScaleType = 0
  TheoreticalExact = false
  Type = 1
  UnderTolerance = 0
  X = 0
  Y = 6.12902
FEATURE [TechDraw::DrawViewDimension] Dimension116
  AngleOverride = false
  Arbitrary = false
  ArbitraryTolerances = false
  BoxCorners = (2) [(-52.5,-47.625,-1e-07),(52.5,47.625,1e-07)]
  EqualTolerance = true
  ExtensionAngle = 0
  FormatSpec = %.2w
  FormatSpecOverTolerance = %+.2w
  FormatSpecUnderTolerance = %+.2w
  Inverted = false
  LineAngle = 0
  LockPosition = false
  MeasureType = 1
  OverTolerance = 0
  References2D = -> [SectionView004]
  Rotation = 0
  Scale = 0.15
  ScaleType = 0
  TheoreticalExact = false
  Type = 1
  UnderTolerance = 0
  X = 0
  Y = -3.47224
FEATURE [TechDraw::DrawViewDimension] Dimension117
  AngleOverride = false
  Arbitrary = false
  ArbitraryTolerances = false
  BoxCorners = (2) [(-52.5,-47.625,-1e-07),(52.5,47.625,1e-07)]
  EqualTolerance = true
  ExtensionAngle = 0
  FormatSpec = %.2w
  FormatSpecOverTolerance = %+.2w
  FormatSpecUnderTolerance = %+.2w
  Inverted = false
  LineAngle = 0
  LockPosition = false
  MeasureType = 1
  OverTolerance = 0
  References2D = -> [SectionView004]
  Rotation = 0
  Scale = 0.15
  ScaleType = 0
  TheoreticalExact = false
  Type = 1
  UnderTolerance = 0
  X = 14.5749
  Y = -27.494
FEATURE [TechDraw::DrawViewDimension] Dimension118
  AngleOverride = false
  Arbitrary = false
  ArbitraryTolerances = false
  BoxCorners = (2) [(-52.5,-47.625,-1e-07),(52.5,47.625,1e-07)]
  EqualTolerance = true
  ExtensionAngle = 0
  FormatSpec = %.2w
  FormatSpecOverTolerance = %+.2w
  FormatSpecUnderTolerance = %+.2w
  Inverted = false
  LineAngle = 0
  LockPosition = false
  MeasureType = 1
  OverTolerance = 0
  References2D = -> [SectionView004]
  Rotation = 0
  Scale = 0.15
  ScaleType = 0
  TheoreticalExact = false
  Type = 2
  UnderTolerance = 0
  X = -62.1493
  Y = -13.2999
FEATURE [TechDraw::DrawPage] Page017  label="add_middle_brace_assembly"
  KeepUpdated = true
  NextBalloonIndex = 7
  ProjectionType = 0
  Scale = 0.15
  Template = -> Template017
  Views = -> [View044,SectionView004,Dimension112,Balloon068,Balloon069,Balloon070,Balloon071,Balloon072,Balloon073,Annotation017,Dimension113,Dimension114,Dimension115,Dimension116,Dimension117,Dimension118]
FEATURE [TechDraw::DrawSVGTemplate] Template018
  Height = 210
  Orientation = 1
  Template = <path>
  Width = 297
FEATURE [App::FeaturePython] Joint070  label="Fixed058"  # Assembly joint (typed FeaturePython)
  Activated = true
  AngleMax = 0
  AngleMin = 0
  Detach1 = false
  Detach2 = false
  Distance = 0
  Distance2 = 0
  EnableAngleMax = false
  EnableAngleMin = false
  EnableLengthMax = false
  EnableLengthMin = false
  JointType = 0 (Fixed)
  LengthMax = 0
  LengthMin = 0
  Offset2 = pos=(0,0,0) rot=(0,0,1;3.14159rad)
  Placement1 = pos=(30,30,142.669) rot=(0,0,1;0rad)
  Placement2 = pos=(13,194.331,142.669) rot=(0,0,1;3.14159rad)
  Reference1 = -> Assembly [middle_brace_bar_fin_1and_2.Edge7,middle_brace_bar_fin_1and_2.Edge7]
  Reference2 = -> Assembly [Body036.Edge7,Body036.Edge7]
FEATURE [Assembly::JointGroup] Joints
  Group = -> [GroundedJoint,Joint,Joint003,Joint004,Joint005,Joint006,Joint007,Joint008,Joint009,Joint010,Joint011,Joint013,Joint019,Joint021,Joint022,Joint037,Joint038,Joint039,Joint040,Joint041,Joint044,Joint045,Joint046,Joint047,Joint048,Joint052,Joint054,Joint055,Joint056,GroundedJoint001,Joint060,Joint061,GroundedJoint002,Joint062,Joint063,Joint064,Joint065,Joint066,Joint067,Joint069,Joint070]
FEATURE [Assembly::AssemblyObject] Assembly
  Group = -> [Joints,bottom_panel,GroundedJoint,back_panel,Joint,top_panel,Joint003,side_panel_001,Joint004,side_panel_001_bar_001,side_panel_001_bar_002,side_panel_001_bar_003,side_panel_001_bar_004,Joint005,Joint006,Joint007,Joint008,side_panel_002_bar_001,side_panel_002_bar_004,side_panel_002_bar_002,side_panel_002,Joint009,Joint010,Joint011,Joint013,front_panel,fp_bar_1,fp_bar_002,_2lfa_driver,Joint019,+53 more]
  Origin = -> Origin001
  Type = Assembly
FEATURE [TechDraw::DrawProjGroupItem] View035  label="Front"
  CoarseView = false
  Direction = (3e-16,2e-16,1)
  Focus = 100
  HardHidden = false
  IsoCount = 0
  IsoHidden = false
  IsoVisible = false
  LockPosition = true
  Perspective = false
  Rotation = 0
  RotationVector = (1,0,0)
  Scale = 0.1
  ScaleType = 2
  ScrubCount = 1
  SeamHidden = false
  SeamVisible = true
  SmoothHidden = false
  SmoothVisible = true
  Source = -> [Assembly]
  Type = 0
  X = 0
  XDirection = (1,1e-16,-3e-16)
  Y = 0
FEATURE [TechDraw::DrawProjGroupItem] ProjItem012  label="Left"
  CoarseView = false
  Direction = (-1,-1e-16,4e-16)
  Focus = 100
  HardHidden = false
  IsoCount = 0
  IsoHidden = false
  IsoVisible = false
  LockPosition = false
  Perspective = false
  Rotation = 0
  RotationVector = (1,0,0)
  ScaleType = 2
  ScrubCount = 1
  SeamHidden = false
  SeamVisible = true
  SmoothHidden = false
  SmoothVisible = true
  Source = -> [Assembly]
  Type = 1
  X = 68.3488
  XDirection = (4e-16,2e-16,1)
  Y = 0
FEATURE [TechDraw::DrawProjGroupItem] ProjItem014  label="Rear"
  CoarseView = false
  Direction = (-3e-16,-2e-16,-1)
  Focus = 100
  HardHidden = false
  IsoCount = 0
  IsoHidden = false
  IsoVisible = false
  LockPosition = false
  Perspective = false
  Rotation = 0
  RotationVector = (1,0,0)
  ScaleType = 2
  ScrubCount = 1
  SeamHidden = false
  SeamVisible = true
  SmoothHidden = false
  SmoothVisible = true
  Source = -> [Assembly]
  Type = 3
  X = 136.698
  XDirection = (-1,-1e-16,3e-16)
  Y = 0
FEATURE [TechDraw::DrawProjGroupItem] ProjItem015  label="FrontTopLeft"
  CoarseView = false
  Direction = (-0.57735,0.57735,0.57735)
  Focus = 100
  HardHidden = false
  IsoCount = 0
  IsoHidden = false
  IsoVisible = false
  LockPosition = false
  Perspective = false
  Rotation = 0
  RotationVector = (1,0,0)
  ScaleType = 2
  ScrubCount = 1
  SeamHidden = false
  SeamVisible = true
  SmoothHidden = false
  SmoothVisible = true
  Source = -> [Assembly]
  Type = 6
  X = 68.3488
  XDirection = (0.707107,2e-16,0.707107)
  Y = -93.7598
FEATURE [TechDraw::DrawProjGroupItem] ProjItem016  label="FrontTopRight"
  CoarseView = false
  Direction = (0.57735,0.57735,0.57735)
  Focus = 100
  HardHidden = false
  IsoCount = 0
  IsoHidden = false
  IsoVisible = false
  LockPosition = false
  Perspective = false
  Rotation = 0
  RotationVector = (1,0,0)
  ScaleType = 2
  ScrubCount = 1
  SeamHidden = false
  SeamVisible = true
  SmoothHidden = false
  SmoothVisible = true
  Source = -> [Assembly]
  Type = 7
  X = -68.1721
  XDirection = (0.707107,-1e-16,-0.707107)
  Y = -93.7598
FEATURE [TechDraw::DrawProjGroup] ProjGroup012
  Anchor = -> View035
  AutoDistribute = true
  LockPosition = false
  ProjectionType = 0
  Rotation = 0
  Scale = 0.1
  ScaleType = 0
  Source = -> [Assembly]
  Views = -> [View035,ProjItem012,ProjItem014,ProjItem015,ProjItem016]
  X = 125.106
  Y = 163.624
  spacingX = 15
  spacingY = 15
FEATURE [TechDraw::DrawPage] Page008  label="assembled_views"
  KeepUpdated = true
  NextBalloonIndex = 1
  ProjectionType = 0
  Scale = 0.1
  Template = -> Template008
  Views = -> [ProjGroup012]
FEATURE [TechDraw::DrawProjGroupItem] View045  label="Front009"
  CoarseView = false
  Direction = (0,0,1)
  Focus = 100
  HardHidden = false
  IsoCount = 0
  IsoHidden = false
  IsoVisible = false
  LockPosition = true
  Perspective = false
  Rotation = 0
  RotationVector = (1,0,0)
  Scale = 0.15
  ScaleType = 2
  ScrubCount = 1
  SeamHidden = false
  SeamVisible = true
  SmoothHidden = false
  SmoothVisible = true
  Source = -> [Body036]
  Type = 0
  X = 0
  XDirection = (1,-4e-16,0)
  XSource = -> [bottom_panel,back_panel,side_panel_001,side_panel_001_bar_001,side_panel_001_bar_002,side_panel_001_bar_003,side_panel_001_bar_004,side_panel_002_bar_001,side_panel_002_bar_004,side_panel_002_bar_002,side_panel_002,front_panel,fp_bar_1,fp_bar_002,brace_bar_fin_2,brace_bar_fin_004,brace_bar_back_panel_1,brace_bar_back_panel_2,brace_bar_back_panel_005,side_panel_001_bar_008,middle_brace_bar_fin_1,+12 more]
  Y = 0
FEATURE [TechDraw::DrawProjGroupItem] ProjItem032  label="Right001"
  CoarseView = false
  Direction = (1,-4e-16,1e-16)
  Focus = 100
  HardHidden = false
  IsoCount = 0
  IsoHidden = false
  IsoVisible = false
  LockPosition = false
  Perspective = false
  Rotation = 0
  RotationVector = (1,0,0)
  ScaleType = 2
  ScrubCount = 1
  SeamHidden = false
  SeamVisible = true
  SmoothHidden = false
  SmoothVisible = true
  Source = -> [Body036]
  Type = 2
  X = -92.475
  XDirection = (1e-16,0,-1)
  XSource = <same value as first occurrence — deduplicated (x3 in doc)>
  Y = 0
FEATURE [TechDraw::DrawProjGroup] ProjGroup021
  Anchor = -> View045
  AutoDistribute = true
  LockPosition = false
  ProjectionType = 0
  Rotation = 0
  Scale = 0.15
  ScaleType = 0
  Source = -> [Body036]
  Views = -> [View045,ProjItem032]
  X = 205.886
  XSource = <same value as first occurrence — deduplicated (x3 in doc)>
  Y = 119.83
  spacingX = 15
  spacingY = 15
FEATURE [TechDraw::DrawViewBalloon] Balloon074
  BubbleShape = 0
  EndType = 0
  EndTypeScale = 1
  KinkLength = 5
  LockPosition = false
  OriginX = 61.3624
  OriginY = 197.248
  Rotation = 0
  Scale = 0.15
  ScaleType = 0
  ShapeScale = 1
  SourceView = -> ProjItem032
  Text = P10
  TextWrapLen = -1
  X = 291.943
  Y = 519.572
FEATURE [TechDraw::DrawViewBalloon] Balloon075
  BubbleShape = 0
  EndType = 0
  EndTypeScale = 1
  KinkLength = 5
  LockPosition = false
  OriginX = -45.0596
  OriginY = -28.4404
  Rotation = 0
  Scale = 0.15
  ScaleType = 0
  ShapeScale = 1
  SourceView = -> ProjItem032
  Text = P11
  TextWrapLen = -1
  X = -464.102
  Y = 200.306
FEATURE [TechDraw::DrawViewBalloon] Balloon076
  BubbleShape = 0
  EndType = 0
  EndTypeScale = 1
  KinkLength = 5
  LockPosition = false
  OriginX = -43.2248
  OriginY = -208.257
  Rotation = 0
  Scale = 0.15
  ScaleType = 0
  ShapeScale = 1
  SourceView = -> ProjItem032
  Text = P9
  TextWrapLen = -1
  X = -298.882
  Y = -539.144
FEATURE [TechDraw::DrawViewBalloon] Balloon077
  BubbleShape = 0
  EndType = 0
  EndTypeScale = 1
  KinkLength = 5
  LockPosition = false
  OriginX = 26.5138
  OriginY = 188.073
  Rotation = 0
  Scale = 0.15
  ScaleType = 0
  ShapeScale = 1
  SourceView = -> View045
  Text = P10
  TextWrapLen = -1
  X = 244.251
  Y = 429.664
FEATURE [TechDraw::DrawViewDimension] Dimension120
  AngleOverride = false
  Arbitrary = false
  ArbitraryTolerances = false
  BoxCorners = (2) [(-52.5,-47.625,0),(52.5,47.625,0)]
  EqualTolerance = true
  ExtensionAngle = 0
  FormatSpec = %.0w
  FormatSpecOverTolerance = %+.2w
  FormatSpecUnderTolerance = %+.2w
  Inverted = false
  LineAngle = 0
  LockPosition = false
  MeasureType = 1
  OverTolerance = 0
  References2D = -> [ProjItem032]
  Rotation = 0
  Scale = 0.15
  ScaleType = 0
  TheoreticalExact = false
  Type = 1
  UnderTolerance = 0
  X = 0
  Y = 3.02801
FEATURE [TechDraw::DrawViewDimension] Dimension122
  AngleOverride = false
  Arbitrary = false
  ArbitraryTolerances = false
  BoxCorners = (2) [(-52.5,-47.625,0),(52.5,47.625,0)]
  EqualTolerance = true
  ExtensionAngle = 0
  FormatSpec = %.0w
  FormatSpecOverTolerance = %+.2w
  FormatSpecUnderTolerance = %+.2w
  Inverted = false
  LineAngle = 0
  LockPosition = false
  MeasureType = 1
  OverTolerance = 0
  References2D = -> [ProjItem032]
  Rotation = 0
  Scale = 0.15
  ScaleType = 0
  TheoreticalExact = false
  Type = 1
  UnderTolerance = 0
  X = -14.5749
  Y = -26.3263
FEATURE [TechDraw::DrawViewDimension] Dimension123
  AngleOverride = false
  Arbitrary = false
  ArbitraryTolerances = false
  BoxCorners = (2) [(-52.5,-47.625,0),(52.5,47.625,0)]
  EqualTolerance = true
  ExtensionAngle = 0
  FormatSpec = %.0w
  FormatSpecOverTolerance = %+.2w
  FormatSpecUnderTolerance = %+.2w
  Inverted = false
  LineAngle = 0
  LockPosition = false
  MeasureType = 1
  OverTolerance = 0
  References2D = -> [ProjItem032]
  Rotation = 0
  Scale = 0.15
  ScaleType = 0
  TheoreticalExact = false
  Type = 1
  UnderTolerance = 0
  X = 12.3249
  Y = 26.0906
FEATURE [TechDraw::DrawViewBalloon] Balloon078
  BubbleShape = 0
  EndType = 0
  EndTypeScale = 1
  KinkLength = 5
  LockPosition = false
  OriginX = 26.5727
  OriginY = 31.8126
  Rotation = 0
  Scale = 0.15
  ScaleType = 0
  ShapeScale = 1
  SourceView = -> View045
  Text = P11
  TextWrapLen = -1
  X = 252.334
  Y = 283.569
FEATURE [TechDraw::DrawViewBalloon] Balloon079
  BubbleShape = 0
  EndType = 0
  EndTypeScale = 1
  KinkLength = 5
  LockPosition = false
  OriginX = 29.461
  OriginY = -199.257
  Rotation = 0
  Scale = 0.15
  ScaleType = 0
  ShapeScale = 1
  SourceView = -> View045
  Text = P9
  TextWrapLen = -1
  X = 258.111
  Y = 152.148
FEATURE [TechDraw::DrawViewAnnotation] Annotation018
  Font = osifont
  LineSpace = 100
  LockPosition = false
  MaxWidth = -1
  Rotation = 0
  Scale = 0.15
  ScaleType = 0
  Text = Assemblage: middle fin support | Dimensions en mm | Échelle 0.15 | Répéter pour prime
  TextSize = 5
  TextStyle = 0
  X = 247.96
  Y = 23.419
FEATURE [TechDraw::DrawPage] Page018  label="add_middle_fin_support_assembly"
  KeepUpdated = true
  NextBalloonIndex = 7
  ProjectionType = 0
  Scale = 0.15
  Template = -> Template018
  Views = -> [ProjGroup021,Balloon074,Balloon075,Balloon076,Balloon077,Dimension120,Dimension122,Dimension123,Balloon078,Balloon079,Annotation018]
FEATURE [TechDraw::DrawSVGTemplate] Template019
  Height = 210
  Orientation = 1
  Template = <path>
  Width = 297
FEATURE [TechDraw::DrawProjGroupItem] View046
  CoarseView = false
  Direction = (-3e-16,1e-16,1)
  Focus = 100
  HardHidden = false
  IsoCount = 0
  IsoHidden = false
  IsoVisible = false
  LockPosition = false
  Perspective = false
  Rotation = 0
  RotationVector = (1,0,0)
  Scale = 0.15
  ScaleType = 0
  ScrubCount = 1
  SeamHidden = false
  SeamVisible = true
  SmoothHidden = false
  SmoothVisible = true
  Source = -> [Body036]
  Type = 0
  X = 87.9495
  XDirection = (1,2e-16,3e-16)
  XSource = -> [side_panel_001_bar_009,fin_2_model,middle_brace_bar_back_panel_2_model,fin_1_model,middle_brace_bar_fin_1and_003,middle_brace_bar_fin_1and_2,middle_brace_bar_side_panel_002,fin_1_support001,middle_brace_bar_fin_2,middle_brace_bar_side_panel_1,fin_1_support,driver_brace_bar001,driver_brace_bar,middle_brace_bar_fin_1,side_panel_001_bar_008,brace_bar_back_panel_005,brace_bar_back_panel_004,+21 more]
  Y = 110.505
FEATURE [TechDraw::DrawViewSection] SectionView005  label="Section005 A - A"
  BaseView = -> View046
  Caption = A
  CoarseView = false
  CutSurfaceDisplay = 2
  Direction = (-1,-3e-16,-3e-16)
  FileGeomPattern = <path>
  FileHatchPattern = <path>
  Focus = 100
  FuseBeforeCut = false
  HardHidden = false
  HatchOffset = (0,0,0)
  HatchRotation = 0
  HatchScale = 1
  IsoCount = 0
  IsoHidden = false
  IsoVisible = false
  LockPosition = false
  NameGeomPattern = Diamond
  Perspective = false
  Rotation = -90
  Scale = 0.15
  ScaleType = 0
  ScrubCount = 1
  SeamHidden = false
  SeamVisible = true
  SectionDirection = 4
  SectionLineStretch = 1
  SectionNormal = (-1,-3e-16,-3e-16)
  SectionOrigin = (315,317.5,350)
  SectionSymbol = A
  SmoothHidden = false
  SmoothVisible = true
  Source = -> [Body036]
  TrimAfterCut = false
  UsePreviousCut = false
  X = 199.486
  XDirection = (3e-16,-1,1e-16)
  Y = 119.45
FEATURE [TechDraw::DrawViewBalloon] Balloon080
  BubbleShape = 0
  EndType = 0
  EndTypeScale = 1
  KinkLength = 5
  LockPosition = false
  OriginX = -211.927
  OriginY = -322.11
  Rotation = 0
  Scale = 0.15
  ScaleType = 0
  ShapeScale = 1
  SourceView = -> SectionView005
  Text = 1
  TextWrapLen = -1
  X = -82.263
  Y = 484.618
FEATURE [TechDraw::DrawViewBalloon] Balloon081
  BubbleShape = 0
  EndType = 0
  EndTypeScale = 1
  KinkLength = 5
  LockPosition = false
  OriginX = -57.8899
  OriginY = 125.688
  Rotation = 0
  Scale = 0.15
  ScaleType = 0
  ShapeScale = 1
  SourceView = -> Balloon080
  Text = 2
  TextWrapLen = -1
  X = 33.2416
  Y = 481.04
FEATURE [TechDraw::DrawViewBalloon] Balloon082
  BubbleShape = 0
  EndType = 0
  EndTypeScale = 1
  KinkLength = 5
  LockPosition = false
  OriginX = 76.1468
  OriginY = 124.22
  Rotation = 0
  Scale = 0.15
  ScaleType = 0
  ShapeScale = 1
  SourceView = -> SectionView005
  Text = 3
  TextWrapLen = -1
  X = 296.636
  Y = 480.031
FEATURE [TechDraw::DrawViewBalloon] Balloon083
  BubbleShape = 0
  EndType = 0
  EndTypeScale = 1
  KinkLength = 5
  LockPosition = false
  OriginX = 57.7982
  OriginY = -313.853
  Rotation = 0
  Scale = 0.15
  ScaleType = 0
  ShapeScale = 1
  SourceView = -> SectionView005
  Text = 4
  TextWrapLen = -1
  X = -448.777
  Y = 44.2508
FEATURE [TechDraw::DrawViewAnnotation] Annotation019
  Font = osifont
  LineSpace = 100
  LockPosition = false
  MaxWidth = -1
  Rotation = 0
  Scale = 0.15
  ScaleType = 0
  Text = Assemblage: top brace | Dimensions en mm | Échelle 0.15 | Répéter pour prime
  TextSize = 5
  TextStyle = 0
  X = 247.96
  Y = 23.419
FEATURE [TechDraw::DrawPage] Page019  label="add_top_brace_assembly"
  KeepUpdated = true
  NextBalloonIndex = 6
  ProjectionType = 0
  Scale = 0.15
  Template = -> Template019
  Views = -> [View046,SectionView005,Balloon080,Balloon081,Balloon082,Balloon083,Annotation019]
FEATURE [TechDraw::DrawSVGTemplate] Template020
  Height = 210
  Orientation = 1
  Template = <path>
  Width = 297
FEATURE [TechDraw::DrawProjGroupItem] View047  label="Front010"
  CoarseView = false
  Direction = (0,0,1)
  Focus = 100
  HardHidden = false
  IsoCount = 0
  IsoHidden = false
  IsoVisible = false
  LockPosition = true
  Perspective = false
  Rotation = 0
  RotationVector = (1,0,0)
  Scale = 0.15
  ScaleType = 2
  ScrubCount = 1
  SeamHidden = false
  SeamVisible = true
  SmoothHidden = false
  SmoothVisible = true
  Source = -> [Assembly]
  Type = 0
  X = 0
  XDirection = (1,7e-16,0)
  Y = 0
FEATURE [TechDraw::DrawProjGroupItem] ProjItem033  label="Left004"
  CoarseView = false
  Direction = (-1,-7e-16,1e-16)
  Focus = 100
  HardHidden = false
  IsoCount = 0
  IsoHidden = false
  IsoVisible = false
  LockPosition = false
  Perspective = false
  Rotation = 0
  RotationVector = (1,0,0)
  ScaleType = 2
  ScrubCount = 1
  SeamHidden = false
  SeamVisible = true
  SmoothHidden = false
  SmoothVisible = true
  Source = -> [Assembly]
  Type = 1
  X = 93.39
  XDirection = (1e-16,0,1)
  Y = 0
FEATURE [TechDraw::DrawProjGroup] ProjGroup022
  Anchor = -> View047
  AutoDistribute = true
  LockPosition = false
  ProjectionType = 0
  Rotation = 0
  Scale = 0.15
  ScaleType = 0
  Source = -> [Assembly]
  Views = -> [View047,ProjItem033]
  X = 104.188
  Y = 106.651
  spacingX = 15
  spacingY = 15
FEATURE [TechDraw::DrawViewBalloon] Balloon084
  BubbleShape = 0
  EndType = 0
  EndTypeScale = 1
  KinkLength = 5
  LockPosition = false
  OriginX = 164.128
  OriginY = 204.587
  Rotation = 0
  Scale = 0.15
  ScaleType = 0
  ShapeScale = 1
  SourceView = -> View047
  Text = P2
  TextWrapLen = -1
  X = 36.9113
  Y = 499.388
FEATURE [TechDraw::DrawViewBalloon] Balloon085
  BubbleShape = 0
  EndType = 0
  EndTypeScale = 1
  KinkLength = 5
  LockPosition = false
  OriginX = -91.8991
  OriginY = 149.541
  Rotation = 0
  Scale = 0.15
  ScaleType = 0
  ShapeScale = 1
  SourceView = -> ProjItem033
  Text = P2
  TextWrapLen = -1
  X = 120.333
  Y = 517.737
FEATURE [TechDraw::DrawViewAnnotation] Annotation020
  Font = osifont
  LineSpace = 100
  LockPosition = false
  MaxWidth = -1
  Rotation = 0
  Scale = 0.15
  ScaleType = 0
  Text = Assemblage: close it up! | Dimensions en mm | Échelle 0.15 | Répéter pour prime
  TextSize = 5
  TextStyle = 0
  X = 247.96
  Y = 23.419
FEATURE [TechDraw::DrawPage] Page020  label="close_it_up_assembly"
  KeepUpdated = true
  NextBalloonIndex = 3
  ProjectionType = 0
  Scale = 0.15
  Template = -> Template020
  Views = -> [ProjGroup022,Balloon084,Balloon085,Annotation020]
FEATURE [TechDraw::DrawSVGTemplate] Template021
  Height = 210
  Orientation = 1
  Template = <path>
  Width = 297
FEATURE [TechDraw::DrawPage] Page021  label="add_driver_assembly"
  KeepUpdated = true
  NextBalloonIndex = 1
  ProjectionType = 0
  Template = -> Template021
FEATURE [TechDraw::DrawViewDimension] Dimension124
  AngleOverride = false
  Arbitrary = false
  ArbitraryTolerances = false
  BoxCorners = (2) [(-24,-47.625,0),(24,47.625,0)]
  EqualTolerance = true
  ExtensionAngle = 0
  FormatSpec = %.2w
  FormatSpecOverTolerance = %+.2w
  FormatSpecUnderTolerance = %+.2w
  Inverted = false
  LineAngle = 0
  LockPosition = false
  MeasureType = 1
  OverTolerance = 0
  References2D = -> [View040]
  Rotation = 0
  Scale = 0.15
  ScaleType = 0
  TheoreticalExact = false
  Type = 2
  UnderTolerance = 0
  X = -19.5367
  Y = 7.49089
FEATURE [TechDraw::DrawViewDimension] Dimension125
  AngleOverride = false
  Arbitrary = false
  ArbitraryTolerances = false
  BoxCorners = (2) [(-24,-47.625,0),(24,47.625,0)]
  EqualTolerance = true
  ExtensionAngle = 0
  FormatSpec = %.2w
  FormatSpecOverTolerance = %+.2w
  FormatSpecUnderTolerance = %+.2w
  Inverted = false
  LineAngle = 0
  LockPosition = false
  MeasureType = 1
  OverTolerance = 0
  References2D = -> [View040]
  Rotation = 0
  Scale = 0.15
  ScaleType = 0
  TheoreticalExact = false
  Type = 2
  UnderTolerance = 0
  X = 7.87495
  Y = -29.9493
FEATURE [TechDraw::DrawViewDimension] Dimension126
  AngleOverride = false
  Arbitrary = false
  ArbitraryTolerances = false
  BoxCorners = (2) [(-24,-47.625,0),(24,47.625,0)]
  EqualTolerance = true
  ExtensionAngle = 0
  FormatSpec = %.2w
  FormatSpecOverTolerance = %+.2w
  FormatSpecUnderTolerance = %+.2w
  Inverted = false
  LineAngle = 0
  LockPosition = false
  MeasureType = 1
  OverTolerance = 0
  References2D = -> [View040]
  Rotation = 0
  Scale = 0.15
  ScaleType = 0
  TheoreticalExact = false
  Type = 1
  UnderTolerance = 0
  X = 0
  Y = 9.17046
FEATURE [TechDraw::DrawViewDimension] Dimension127
  AngleOverride = false
  Arbitrary = false
  ArbitraryTolerances = false
  BoxCorners = (2) [(-24,-47.625,0),(24,47.625,0)]
  EqualTolerance = true
  ExtensionAngle = 0
  FormatSpec = %.2w
  FormatSpecOverTolerance = %+.2w
  FormatSpecUnderTolerance = %+.2w
  Inverted = false
  LineAngle = 0
  LockPosition = false
  MeasureType = 1
  OverTolerance = 0
  References2D = -> [View040]
  Rotation = 0
  Scale = 0.15
  ScaleType = 0
  TheoreticalExact = false
  Type = 1
  UnderTolerance = 0
  X = -30.7334
  Y = -5.87167
FEATURE [TechDraw::DrawViewDimension] Dimension128
  AngleOverride = false
  Arbitrary = false
  ArbitraryTolerances = false
  BoxCorners = (2) [(-24,-47.625,0),(24,47.625,0)]
  EqualTolerance = true
  ExtensionAngle = 0
  FormatSpec = %.2w
  FormatSpecOverTolerance = %+.2w
  FormatSpecUnderTolerance = %+.2w
  Inverted = false
  LineAngle = 0
  LockPosition = false
  MeasureType = 1
  OverTolerance = 0
  References2D = -> [View040]
  Rotation = 0
  Scale = 0.15
  ScaleType = 0
  TheoreticalExact = false
  Type = 1
  UnderTolerance = 0
  X = 6.16424
  Y = 29.0968
FEATURE [TechDraw::DrawViewDimension] Dimension129
  AngleOverride = false
  Arbitrary = false
  ArbitraryTolerances = false
  BoxCorners = (2) [(-24,-47.625,0),(24,47.625,0)]
  EqualTolerance = true
  ExtensionAngle = 0
  FormatSpec = ⌀%.2w
  FormatSpecOverTolerance = %+.2w
  FormatSpecUnderTolerance = %+.2w
  Inverted = false
  LineAngle = 0
  LockPosition = false
  MeasureType = 1
  OverTolerance = 0
  References2D = -> [View040]
  Rotation = 0
  Scale = 0.15
  ScaleType = 0
  TheoreticalExact = false
  Type = 5
  UnderTolerance = 0
  X = 17.993
  Y = 6.91209
FEATURE [TechDraw::DrawPage] Page013  label="back_side_assembly"
  KeepUpdated = true
  NextBalloonIndex = 8
  ProjectionType = 0
  Scale = 0.15
  Template = -> Template013
  Views = -> [ProjGroup017,Dimension101,Dimension102,Dimension103,Dimension104,Dimension105,Dimension106,Balloon049,Balloon050,Balloon051,Balloon052,Balloon053,Balloon054,Balloon055,Dimension107,Annotation013,Dimension124,Dimension125,Dimension126,Dimension127,Dimension128,Dimension129]
FEATURE [TechDraw::DrawViewDimension] Dimension130
  AngleOverride = false
  Arbitrary = false
  ArbitraryTolerances = false
  BoxCorners = (2) [(-16,-31.75,0),(16,31.75,0)]
  EqualTolerance = true
  ExtensionAngle = 0
  FormatSpec = %.2w
  FormatSpecOverTolerance = %+.2w
  FormatSpecUnderTolerance = %+.2w
  Inverted = false
  LineAngle = 0
  LockPosition = false
  MeasureType = 1
  OverTolerance = 0
  References2D = -> [View005]
  Rotation = 0
  Scale = 0.1
  ScaleType = 0
  TheoreticalExact = false
  Type = 1
  UnderTolerance = 0
  X = -24.1782
  Y = -2.79485
FEATURE [TechDraw::DrawViewDimension] Dimension131
  AngleOverride = false
  Arbitrary = false
  ArbitraryTolerances = false
  BoxCorners = (2) [(-16,-31.75,0),(16,31.75,0)]
  EqualTolerance = true
  ExtensionAngle = 0
  FormatSpec = %.2w
  FormatSpecOverTolerance = %+.2w
  FormatSpecUnderTolerance = %+.2w
  Inverted = false
  LineAngle = 0
  LockPosition = false
  MeasureType = 1
  OverTolerance = 0
  References2D = -> [View005]
  Rotation = 0
  Scale = 0.1
  ScaleType = 0
  TheoreticalExact = false
  Type = 1
  UnderTolerance = 0
  X = 0
  Y = 7.79485
FEATURE [TechDraw::DrawViewDimension] Dimension132
  AngleOverride = false
  Arbitrary = false
  ArbitraryTolerances = false
  BoxCorners = (2) [(-16,-31.75,0),(16,31.75,0)]
  EqualTolerance = true
  ExtensionAngle = 0
  FormatSpec = %.2w
  FormatSpecOverTolerance = %+.2w
  FormatSpecUnderTolerance = %+.2w
  Inverted = false
  LineAngle = 0
  LockPosition = false
  MeasureType = 1
  OverTolerance = 0
  References2D = -> [View005]
  Rotation = 0
  Scale = 0.1
  ScaleType = 0
  TheoreticalExact = false
  Type = 1
  UnderTolerance = 0
  X = -0.884141
  Y = -2.79485
FEATURE [TechDraw::DrawViewDimension] Dimension133
  AngleOverride = false
  Arbitrary = false
  ArbitraryTolerances = false
  BoxCorners = (2) [(-16,-31.75,0),(16,31.75,0)]
  EqualTolerance = true
  ExtensionAngle = 0
  FormatSpec = %.2w
  FormatSpecOverTolerance = %+.2w
  FormatSpecUnderTolerance = %+.2w
  Inverted = false
  LineAngle = 0
  LockPosition = false
  MeasureType = 1
  OverTolerance = 0
  References2D = -> [View005]
  Rotation = 0
  Scale = 0.1
  ScaleType = 0
  TheoreticalExact = false
  Type = 2
  UnderTolerance = 0
  X = 7.53157
  Y = -15.875
FEATURE [TechDraw::DrawViewDimension] Dimension134
  AngleOverride = false
  Arbitrary = false
  ArbitraryTolerances = false
  BoxCorners = (2) [(-16,-31.75,0),(16,31.75,0)]
  EqualTolerance = true
  ExtensionAngle = 0
  FormatSpec = %.2w
  FormatSpecOverTolerance = %+.2w
  FormatSpecUnderTolerance = %+.2w
  Inverted = false
  LineAngle = 0
  LockPosition = false
  MeasureType = 1
  OverTolerance = 0
  References2D = -> [View005]
  Rotation = 0
  Scale = 0.1
  ScaleType = 0
  TheoreticalExact = false
  Type = 2
  UnderTolerance = 0
  X = -36.7687
  Y = 9.69767
FEATURE [TechDraw::DrawViewDimension] Dimension135
  AngleOverride = false
  Arbitrary = false
  ArbitraryTolerances = false
  BoxCorners = (2) [(-16,-31.75,0),(16,31.75,0)]
  EqualTolerance = true
  ExtensionAngle = 0
  FormatSpec = ⌀%.2w
  FormatSpecOverTolerance = %+.2w
  FormatSpecUnderTolerance = %+.2w
  Inverted = false
  LineAngle = 0
  LockPosition = false
  MeasureType = 1
  OverTolerance = 0
  References2D = -> [View005]
  Rotation = 0
  Scale = 0.1
  ScaleType = 0
  TheoreticalExact = false
  Type = 5
  UnderTolerance = 0
  X = -9.54041
  Y = 17.7725
FEATURE [TechDraw::DrawProjGroupItem] View048  label="Front011"
  Caption = P7
  CoarseView = false
  Direction = (0,-1,0)
  Focus = 100
  HardHidden = false
  IsoCount = 0
  IsoHidden = false
  IsoVisible = false
  LockPosition = true
  Perspective = false
  Rotation = 0
  RotationVector = (1,0,0)
  Scale = 0.1
  ScaleType = 2
  ScrubCount = 1
  SeamHidden = false
  SeamVisible = true
  SmoothHidden = false
  SmoothVisible = true
  Type = 0
  X = 0
  XDirection = (1e-16,0,-1)
  XSource = -> [fin_2_model]
  Y = 0
FEATURE [TechDraw::DrawProjGroupItem] ProjItem034  label="Right002"
  CoarseView = false
  Direction = (1e-16,-1e-16,-1)
  Focus = 100
  HardHidden = false
  IsoCount = 0
  IsoHidden = false
  IsoVisible = false
  LockPosition = false
  Perspective = false
  Rotation = 0
  RotationVector = (1,0,0)
  ScaleType = 2
  ScrubCount = 1
  SeamHidden = false
  SeamVisible = true
  SmoothHidden = false
  SmoothVisible = true
  Type = 2
  X = -40.2834
  XDirection = (0,1,-1e-16)
  XSource = -> [fin_2_model]
  Y = 0
FEATURE [TechDraw::DrawProjGroup] ProjGroup023
  Anchor = -> View048
  AutoDistribute = true
  LockPosition = false
  ProjectionType = 0
  Rotation = 0
  Scale = 0.1
  ScaleType = 0
  Views = -> [View048,ProjItem034]
  X = 232.233
  XSource = -> [fin_2_model]
  Y = 36.0452
  spacingX = 15
  spacingY = 15
FEATURE [TechDraw::DrawViewDimension] Dimension136
  AngleOverride = false
  Arbitrary = false
  ArbitraryTolerances = false
  BoxCorners = (2) [(-24.6334,-16,0),(24.6334,16,0)]
  EqualTolerance = true
  ExtensionAngle = 0
  FormatSpec = %.0w
  FormatSpecOverTolerance = %+.2w
  FormatSpecUnderTolerance = %+.2w
  Inverted = false
  LineAngle = 0
  LockPosition = false
  MeasureType = 1
  OverTolerance = 0
  References2D = -> [View048]
  Rotation = 0
  Scale = 0.1
  ScaleType = 0
  TheoreticalExact = false
  Type = 1
  UnderTolerance = 0
  X = 0
  Y = 11.7221
FEATURE [TechDraw::DrawViewDimension] Dimension137
  AngleOverride = false
  Arbitrary = false
  ArbitraryTolerances = false
  BoxCorners = (2) [(-24.6334,-16,0),(24.6334,16,0)]
  EqualTolerance = true
  ExtensionAngle = 0
  FormatSpec = %.2w
  FormatSpecOverTolerance = %+.2w
  FormatSpecUnderTolerance = %+.2w
  Inverted = false
  LineAngle = 0
  LockPosition = false
  MeasureType = 1
  OverTolerance = 0
  References2D = -> [View048]
  Rotation = 0
  Scale = 0.1
  ScaleType = 0
  TheoreticalExact = false
  Type = 2
  UnderTolerance = 0
  X = 30.822
  Y = 0
FEATURE [TechDraw::DrawPage] Page  label="panels_1_to_7"
  KeepUpdated = true
  NextBalloonIndex = 10
  ProjectionType = 0
  Scale = 0.1
  Template = -> Template
  Views = -> [ProjGroup,ProjGroup002,ProjGroup003,ProjGroup004,ProjGroup005,Dimension,Dimension001,Dimension002,Dimension005,Dimension006,Dimension007,Dimension008,Dimension013,Dimension014,Dimension015,Dimension016,Dimension017,Dimension018,Dimension019,Balloon,Balloon001,Balloon003,Balloon004,Balloon005,ProjGroup008,Dimension041,Dimension042,Annotation004,Dimension130,Dimension131,Dimension132,Dimension133,+5 more]
FEATURE [TechDraw::DrawProjGroupItem] View049
  CoarseView = false
  Direction = (0,-1,0)
  Focus = 100
  HardHidden = false
  IsoCount = 0
  IsoHidden = false
  IsoVisible = false
  LockPosition = false
  Perspective = false
  Rotation = 0
  RotationVector = (1,0,0)
  Scale = 0.2
  ScaleType = 0
  ScrubCount = 1
  SeamHidden = false
  SeamVisible = true
  SmoothHidden = false
  SmoothVisible = true
  Type = 0
  X = 104.727
  XDirection = (1e-16,0,-1)
  XSource = -> [side_panel_001]
  Y = 105
FEATURE [TechDraw::DrawViewDimension] Dimension138
  AngleOverride = false
  Arbitrary = false
  ArbitraryTolerances = false
  BoxCorners = (2) [(-67.4,-32,0),(67.4,32,0)]
  EqualTolerance = true
  ExtensionAngle = 0
  FormatSpec = %.2w
  FormatSpecOverTolerance = %+.2w
  FormatSpecUnderTolerance = %+.2w
  Inverted = false
  LineAngle = 0
  LockPosition = false
  MeasureType = 1
  OverTolerance = 0
  References2D = -> [View049]
  Rotation = 0
  Scale = 0.2
  ScaleType = 0
  TheoreticalExact = false
  Type = 1
  UnderTolerance = 0
  X = 0
  Y = 20.2806
FEATURE [TechDraw::DrawViewBalloon] Balloon086
  BubbleShape = 0
  EndType = 0
  EndTypeScale = 1
  KinkLength = 5
  LockPosition = false
  OriginX = 155.272
  OriginY = -11.9874
  Rotation = 0
  Scale = 0.2
  ScaleType = 0
  ShapeScale = 1
  SourceView = -> Dimension138
  Text = P3
  TextWrapLen = -1
  X = -15.1749
  Y = 375.188
FEATURE [TechDraw::DrawPage] Page004  label="panel_B2_cuts"
  KeepUpdated = true
  NextBalloonIndex = 5
  ProjectionType = 0
  Scale = 0.2
  Template = -> Template004
  Views = -> [View018,Dimension038,Dimension039,Annotation003,View032,Balloon025,Dimension058,Dimension059,Dimension060,Dimension061,View049,Dimension138,Balloon086]
FEATURE [TechDraw::DrawProjGroupItem] View050
  CoarseView = false
  Direction = (0,-1,0)
  Focus = 100
  HardHidden = false
  IsoCount = 0
  IsoHidden = false
  IsoVisible = false
  LockPosition = false
  Perspective = false
  Rotation = 0
  RotationVector = (1,0,0)
  Scale = 0.2
  ScaleType = 0
  ScrubCount = 1
  SeamHidden = false
  SeamVisible = true
  SmoothHidden = false
  SmoothVisible = true
  Source = -> [Pad013]
  Type = 0
  X = 106.093
  XDirection = (1,0,0)
  Y = 105
FEATURE [TechDraw::DrawViewDimension] Dimension139
  AngleOverride = false
  Arbitrary = false
  ArbitraryTolerances = false
  BoxCorners = (2) [(-68.7,-32,0),(68.7,32,0)]
  EqualTolerance = true
  ExtensionAngle = 0
  FormatSpec = %.2w
  FormatSpecOverTolerance = %+.2w
  FormatSpecUnderTolerance = %+.2w
  Inverted = false
  LineAngle = 0
  LockPosition = false
  MeasureType = 1
  OverTolerance = 0
  References2D = -> [View050]
  Rotation = 0
  Scale = 0.2
  ScaleType = 0
  TheoreticalExact = false
  Type = 1
  UnderTolerance = 0
  X = 0
  Y = -2.59351
FEATURE [TechDraw::DrawViewBalloon] Balloon087
  BubbleShape = 0
  EndType = 0
  EndTypeScale = 1
  KinkLength = 5
  LockPosition = false
  OriginX = 92.4785
  OriginY = 86.2452
  Rotation = 0
  Scale = 0.2
  ScaleType = 0
  ShapeScale = 1
  SourceView = -> View050
  Text = P4
  TextWrapLen = -1
  X = 310.925
  Y = 342.712
FEATURE [TechDraw::DrawPage] Page003  label="panel_B1_cuts"
  KeepUpdated = true
  NextBalloonIndex = 4
  ProjectionType = 0
  Scale = 0.2
  Template = -> Template003
  Views = -> [View015,View016,Dimension032,Dimension035,Annotation002,Balloon017,View050,Dimension139,Balloon087]
FEATURE [TechDraw::DrawViewDimension] Dimension140
  AngleOverride = false
  Arbitrary = false
  ArbitraryTolerances = false
  BoxCorners = (2) [(-32,-41.4663,0),(32,41.4663,0)]
  EqualTolerance = true
  ExtensionAngle = 0
  FormatSpec = %.2w
  FormatSpecOverTolerance = %+.2w
  FormatSpecUnderTolerance = %+.2w
  Inverted = false
  LineAngle = 0
  LockPosition = false
  MeasureType = 1
  OverTolerance = 0
  References2D = -> [View038]
  Rotation = 0
  Scale = 0.2
  ScaleType = 0
  TheoreticalExact = false
  Type = 2
  UnderTolerance = 0
  X = 47.6725
  Y = 10.9522
FEATURE [TechDraw::DrawPage] Page011  label="front_panel_assembly"
  KeepUpdated = true
  NextBalloonIndex = 6
  ProjectionType = 0
  Scale = 0.2
  Template = -> Template011
  Views = -> [ProjGroup015,Dimension085,Dimension086,Dimension087,Dimension088,Dimension089,Dimension090,Dimension091,Dimension092,Dimension093,Dimension094,Annotation011,Balloon038,Balloon039,Balloon041,Dimension095,Dimension096,Balloon048,Dimension140]
FEATURE [App::DocumentObjectGroup] Group002  label="Drawings"
  Group = -> [Page,Page005,Page001,Page002,Page007,Page003,Page004,Page006,Page008,Page009,Page010,Page011,Page013,Page014,Page015,Page016,Page017,Page018,Page019,Page020]
note: 33 file-system paths scrubbed to <path> (originals preserved in the JSON sidecar)
